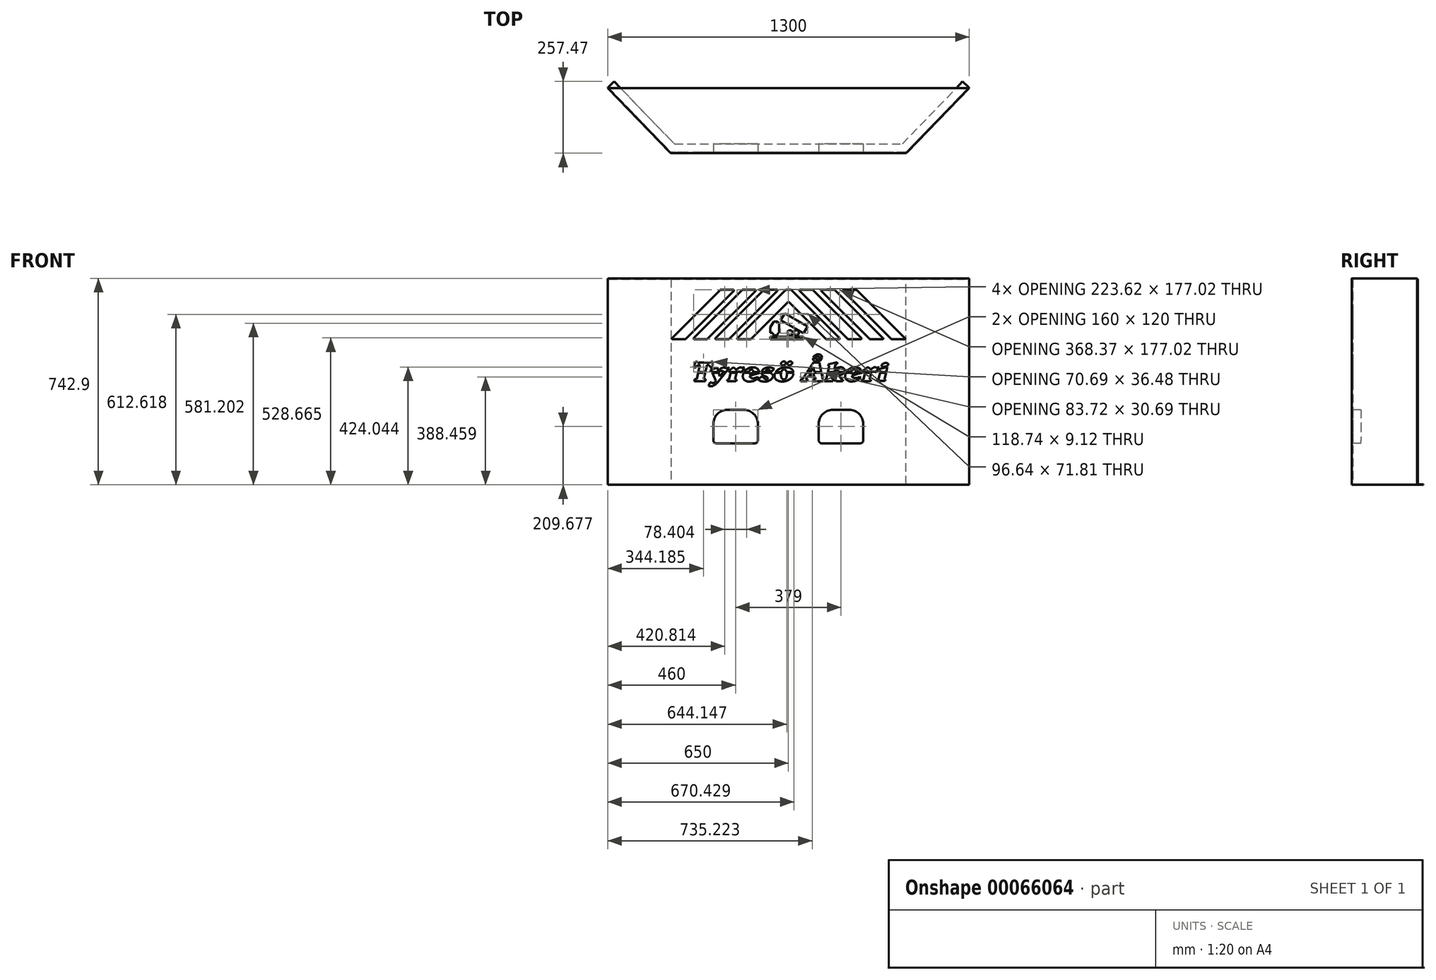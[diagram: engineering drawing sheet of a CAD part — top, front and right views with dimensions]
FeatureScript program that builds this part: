
annotation { "Feature Type Name" : "Feature", "Feature Type Description" : "" }
export const myFeature = defineFeature(function(context is Context, id is Id, definition is map)
    precondition{}
    {
        {
            var Q0;
            Q0=qCreatedBy(makeId("Front.planeOp"),FACE);
            var sketch = newSketch(context, id + "F0", { "sketchPlane" : qUnion([Q0])});
            skLineSegment(sketch, "E0", {"start": v(-649.77, 406.5) * mm, "end": v(-649.77, -376.5) * mm});
            skLineSegment(sketch, "E1", {"start": v(649.77, 406.5) * mm, "end": v(649.77, -376.5) * mm});
            skLineSegment(sketch, "E2", {"start": v(649.77, -376.5) * mm, "end": v(-649.77, -376.5) * mm});
            skLineSegment(sketch, "E3", {"start": v(649.77, 406.5) * mm, "end": v(-649.77, 406.5) * mm});
            skLineSegment(sketch, "E4", {"start": v(-423.5, 366.4) * mm, "end": v(-423.5, -376.5) * mm});
            skLineSegment(sketch, "E5", {"start": v(423.5, 366.4) * mm, "end": v(423.5, -376.5) * mm});
            skLineSegment(sketch, "E6", {"start": v(-423.5, 366.4) * mm, "end": v(423.5, 366.4) * mm});
            skLineSegment(sketch, "E7", {"start": v(134.17, 148.2) * mm, "end": v(1.41, 280.95) * mm});
            skArc(sketch, "E8", {"start": v(1.41, 280.95) * mm, "mid": v(0, 281.53) * mm, "end": v(-1.41, 280.95) * mm});
            skLineSegment(sketch, "E9", {"start": v(183.61, 151.02) * mm, "end": v(10.59, 324.04) * mm});
            skArc(sketch, "E10", {"start": v(10.59, 324.04) * mm, "mid": v(9.94, 324.48) * mm, "end": v(9.17, 324.63) * mm});
            skArc(sketch, "E11", {"start": v(182.2, 147.6) * mm, "mid": v(184.04, 148.84) * mm, "end": v(183.61, 151.02) * mm});
            skLineSegment(sketch, "E12", {"start": v(212.57, 148.2) * mm, "end": v(39.55, 321.22) * mm});
            skLineSegment(sketch, "E13", {"start": v(262.01, 151.02) * mm, "end": v(88.99, 324.04) * mm});
            skArc(sketch, "E14", {"start": v(88.99, 324.04) * mm, "mid": v(88.34, 324.48) * mm, "end": v(87.58, 324.63) * mm});
            skArc(sketch, "E15", {"start": v(260.6, 147.6) * mm, "mid": v(262.45, 148.84) * mm, "end": v(262.01, 151.02) * mm});
            skLineSegment(sketch, "E16", {"start": v(290.98, 148.2) * mm, "end": v(117.95, 321.22) * mm});
            skLineSegment(sketch, "E17", {"start": v(340.42, 151.02) * mm, "end": v(167.4, 324.04) * mm});
            skArc(sketch, "E18", {"start": v(167.4, 324.04) * mm, "mid": v(166.74, 324.48) * mm, "end": v(165.98, 324.63) * mm});
            skArc(sketch, "E19", {"start": v(339, 147.6) * mm, "mid": v(340.85, 148.84) * mm, "end": v(340.42, 151.02) * mm});
            skLineSegment(sketch, "E20", {"start": v(369.38, 148.2) * mm, "end": v(196.36, 321.22) * mm});
            skLineSegment(sketch, "E21", {"start": v(418.82, 151.02) * mm, "end": v(245.8, 324.04) * mm});
            skArc(sketch, "E22", {"start": v(245.8, 324.04) * mm, "mid": v(245.15, 324.48) * mm, "end": v(244.38, 324.63) * mm});
            skArc(sketch, "E23", {"start": v(417.4, 147.6) * mm, "mid": v(419.26, 148.84) * mm, "end": v(418.82, 151.02) * mm});
            skLineSegment(sketch, "E24", {"start": v(339, 147.6) * mm, "end": v(292.4, 147.6) * mm});
            skArc(sketch, "E25", {"start": v(290.98, 148.2) * mm, "mid": v(291.63, 147.76) * mm, "end": v(292.4, 147.6) * mm});
            skLineSegment(sketch, "E26", {"start": v(260.6, 147.6) * mm, "end": v(213.99, 147.6) * mm});
            skArc(sketch, "E27", {"start": v(212.57, 148.2) * mm, "mid": v(213.22, 147.76) * mm, "end": v(213.99, 147.6) * mm});
            skLineSegment(sketch, "E28", {"start": v(182.2, 147.6) * mm, "end": v(135.58, 147.6) * mm});
            skArc(sketch, "E29", {"start": v(134.17, 148.2) * mm, "mid": v(134.82, 147.76) * mm, "end": v(135.58, 147.6) * mm});
            skLineSegment(sketch, "E30", {"start": v(370.8, 147.6) * mm, "end": v(417.4, 147.6) * mm});
            skArc(sketch, "E31", {"start": v(369.38, 148.2) * mm, "mid": v(370.03, 147.76) * mm, "end": v(370.8, 147.6) * mm});
            skLineSegment(sketch, "E32", {"start": v(9.17, 324.63) * mm, "end": v(0, 324.63) * mm});
            skLineSegment(sketch, "E33", {"start": v(40.96, 324.63) * mm, "end": v(87.58, 324.63) * mm});
            skArc(sketch, "E34", {"start": v(40.96, 324.63) * mm, "mid": v(39.12, 323.4) * mm, "end": v(39.55, 321.22) * mm});
            skLineSegment(sketch, "E35", {"start": v(119.37, 324.63) * mm, "end": v(165.98, 324.63) * mm});
            skArc(sketch, "E36", {"start": v(119.37, 324.63) * mm, "mid": v(117.52, 323.4) * mm, "end": v(117.95, 321.22) * mm});
            skLineSegment(sketch, "E37", {"start": v(197.77, 324.63) * mm, "end": v(244.38, 324.63) * mm});
            skArc(sketch, "E38", {"start": v(197.77, 324.63) * mm, "mid": v(195.92, 323.4) * mm, "end": v(196.36, 321.22) * mm});
            skLineSegment(sketch, "E39", {"start": v(-134.17, 148.2) * mm, "end": v(-1.41, 280.95) * mm});
            skLineSegment(sketch, "E40", {"start": v(-183.61, 151.02) * mm, "end": v(-10.59, 324.04) * mm});
            skArc(sketch, "E41", {"start": v(-9.17, 324.63) * mm, "mid": v(-9.94, 324.48) * mm, "end": v(-10.59, 324.04) * mm});
            skArc(sketch, "E42", {"start": v(-183.61, 151.02) * mm, "mid": v(-184.04, 148.84) * mm, "end": v(-182.2, 147.6) * mm});
            skLineSegment(sketch, "E43", {"start": v(-212.57, 148.2) * mm, "end": v(-39.55, 321.22) * mm});
            skLineSegment(sketch, "E44", {"start": v(-262.01, 151.02) * mm, "end": v(-88.99, 324.04) * mm});
            skArc(sketch, "E45", {"start": v(-87.58, 324.63) * mm, "mid": v(-88.34, 324.48) * mm, "end": v(-88.99, 324.04) * mm});
            skArc(sketch, "E46", {"start": v(-262.01, 151.02) * mm, "mid": v(-262.45, 148.84) * mm, "end": v(-260.6, 147.6) * mm});
            skLineSegment(sketch, "E47", {"start": v(-290.98, 148.2) * mm, "end": v(-117.95, 321.22) * mm});
            skLineSegment(sketch, "E48", {"start": v(-340.42, 151.02) * mm, "end": v(-167.4, 324.04) * mm});
            skArc(sketch, "E49", {"start": v(-165.98, 324.63) * mm, "mid": v(-166.74, 324.48) * mm, "end": v(-167.4, 324.04) * mm});
            skArc(sketch, "E50", {"start": v(-340.42, 151.02) * mm, "mid": v(-340.85, 148.84) * mm, "end": v(-339, 147.6) * mm});
            skLineSegment(sketch, "E51", {"start": v(-369.38, 148.2) * mm, "end": v(-196.36, 321.22) * mm});
            skLineSegment(sketch, "E52", {"start": v(-418.82, 151.02) * mm, "end": v(-245.8, 324.04) * mm});
            skArc(sketch, "E53", {"start": v(-244.38, 324.63) * mm, "mid": v(-245.15, 324.48) * mm, "end": v(-245.8, 324.04) * mm});
            skArc(sketch, "E54", {"start": v(-418.82, 151.02) * mm, "mid": v(-419.26, 148.84) * mm, "end": v(-417.4, 147.6) * mm});
            skLineSegment(sketch, "E55", {"start": v(-339, 147.6) * mm, "end": v(-292.4, 147.6) * mm});
            skArc(sketch, "E56", {"start": v(-292.4, 147.6) * mm, "mid": v(-291.63, 147.76) * mm, "end": v(-290.98, 148.2) * mm});
            skLineSegment(sketch, "E57", {"start": v(-260.6, 147.6) * mm, "end": v(-213.99, 147.6) * mm});
            skArc(sketch, "E58", {"start": v(-213.99, 147.6) * mm, "mid": v(-213.22, 147.76) * mm, "end": v(-212.57, 148.2) * mm});
            skLineSegment(sketch, "E59", {"start": v(-182.2, 147.6) * mm, "end": v(-135.58, 147.6) * mm});
            skArc(sketch, "E60", {"start": v(-135.58, 147.6) * mm, "mid": v(-134.82, 147.76) * mm, "end": v(-134.17, 148.2) * mm});
            skLineSegment(sketch, "E61", {"start": v(-370.8, 147.6) * mm, "end": v(-417.4, 147.6) * mm});
            skLineSegment(sketch, "E62", {"start": v(-9.17, 324.63) * mm, "end": v(0, 324.63) * mm});
            skLineSegment(sketch, "E63", {"start": v(-40.96, 324.63) * mm, "end": v(-87.58, 324.63) * mm});
            skArc(sketch, "E64", {"start": v(-39.55, 321.22) * mm, "mid": v(-39.12, 323.4) * mm, "end": v(-40.96, 324.63) * mm});
            skLineSegment(sketch, "E65", {"start": v(-119.37, 324.63) * mm, "end": v(-165.98, 324.63) * mm});
            skArc(sketch, "E66", {"start": v(-117.95, 321.22) * mm, "mid": v(-117.52, 323.4) * mm, "end": v(-119.37, 324.63) * mm});
            skLineSegment(sketch, "E67", {"start": v(-197.77, 324.63) * mm, "end": v(-244.38, 324.63) * mm});
            skArc(sketch, "E68", {"start": v(-196.36, 321.22) * mm, "mid": v(-195.92, 323.4) * mm, "end": v(-197.77, 324.63) * mm});
            skLineSegment(sketch, "E69", {"start": v(119, -226.82) * mm, "end": v(189, -226.82) * mm});
            skLineSegment(sketch, "E70", {"start": v(189, -106.82) * mm, "end": v(159, -106.82) * mm});
            skArc(sketch, "E71", {"start": v(159, -106.82) * mm, "mid": v(123.64, -121.47) * mm, "end": v(109, -156.82) * mm});
            skLineSegment(sketch, "E72", {"start": v(109, -156.82) * mm, "end": v(109, -216.82) * mm});
            skArc(sketch, "E73", {"start": v(109, -216.82) * mm, "mid": v(111.93, -223.9) * mm, "end": v(119, -226.82) * mm});
            skLineSegment(sketch, "E74", {"start": v(-27.89, 215.85) * mm, "end": v(54.63, 168.8) * mm});
            skLineSegment(sketch, "E75", {"start": v(54.63, 168.8) * mm, "end": v(68.75, 193.55) * mm});
            skLineSegment(sketch, "E76", {"start": v(68.75, 193.55) * mm, "end": v(-13.77, 240.6) * mm});
            skLineSegment(sketch, "E77", {"start": v(-13.77, 240.6) * mm, "end": v(-27.89, 215.85) * mm});
            skLineSegment(sketch, "E78", {"start": v(-65.42, 190.73) * mm, "end": v(-65.42, 170.3) * mm});
            skLineSegment(sketch, "E79", {"start": v(-65.42, 170.3) * mm, "end": v(-56.4, 170.3) * mm});
            skLineSegment(sketch, "E80", {"start": v(-37.4, 170.3) * mm, "end": v(-34.07, 170.3) * mm});
            skLineSegment(sketch, "E81", {"start": v(-34.07, 170.3) * mm, "end": v(-34.07, 201.65) * mm});
            skArc(sketch, "E82", {"start": v(-34.07, 201.65) * mm, "mid": v(-36.85, 208.37) * mm, "end": v(-43.57, 211.15) * mm});
            skLineSegment(sketch, "E83", {"start": v(-43.57, 211.15) * mm, "end": v(-53.07, 211.15) * mm});
            skArc(sketch, "E84", {"start": v(-56.4, 170.3) * mm, "mid": v(-46.9, 160.8) * mm, "end": v(-37.4, 170.3) * mm});
            skCircle(sketch, "E85", {"center": v(28.2, 170.12) * mm, "radius": 9.5 * mm});
            skCircle(sketch, "E86", {"center": v(5.53, 170.1) * mm, "radius": 9.5 * mm});
            skLineSegment(sketch, "E87", {"start": v(-53.07, 211.15) * mm, "end": v(-65.42, 190.73) * mm});
            skLineSegment(sketch, "E88", {"start": v(-65.22, 147.6) * mm, "end": v(53.52, 147.6) * mm});
            skLineSegment(sketch, "E89", {"start": v(53.52, 147.6) * mm, "end": v(53.52, 156.72) * mm});
            skLineSegment(sketch, "E90", {"start": v(53.52, 156.72) * mm, "end": v(-65.22, 156.72) * mm});
            skLineSegment(sketch, "E91", {"start": v(-65.22, 156.72) * mm, "end": v(-65.22, 147.6) * mm});
            skLineSegment(sketch, "E92", {"start": v(-326.4, 63.29) * mm, "end": v(-279.7, 63.29) * mm});
            skArc(sketch, "E93", {"start": v(-370.8, 147.6) * mm, "mid": v(-370.03, 147.76) * mm, "end": v(-369.38, 148.2) * mm});
            skLineSegment(sketch, "E94", {"start": v(259, -226.82) * mm, "end": v(189, -226.82) * mm});
            skLineSegment(sketch, "E95", {"start": v(189, -106.82) * mm, "end": v(219, -106.82) * mm});
            skArc(sketch, "E96", {"start": v(269, -156.82) * mm, "mid": v(254.36, -121.47) * mm, "end": v(219, -106.82) * mm});
            skLineSegment(sketch, "E97", {"start": v(269, -156.82) * mm, "end": v(269, -216.82) * mm});
            skArc(sketch, "E98", {"start": v(259, -226.82) * mm, "mid": v(266.07, -223.9) * mm, "end": v(269, -216.82) * mm});
            skLineSegment(sketch, "E99", {"start": v(-260, -226.82) * mm, "end": v(-190, -226.82) * mm});
            skLineSegment(sketch, "E100", {"start": v(-190, -106.82) * mm, "end": v(-220, -106.82) * mm});
            skArc(sketch, "E101", {"start": v(-220, -106.82) * mm, "mid": v(-255.36, -121.47) * mm, "end": v(-270, -156.82) * mm});
            skLineSegment(sketch, "E102", {"start": v(-270, -156.82) * mm, "end": v(-270, -216.82) * mm});
            skArc(sketch, "E103", {"start": v(-270, -216.82) * mm, "mid": v(-267.07, -223.9) * mm, "end": v(-260, -226.82) * mm});
            skLineSegment(sketch, "E104", {"start": v(-120, -226.82) * mm, "end": v(-190, -226.82) * mm});
            skLineSegment(sketch, "E105", {"start": v(-190, -106.82) * mm, "end": v(-160, -106.82) * mm});
            skArc(sketch, "E106", {"start": v(-110, -156.82) * mm, "mid": v(-124.64, -121.47) * mm, "end": v(-160, -106.82) * mm});
            skLineSegment(sketch, "E107", {"start": v(-110, -156.82) * mm, "end": v(-110, -216.82) * mm});
            skArc(sketch, "E108", {"start": v(-120, -226.82) * mm, "mid": v(-112.93, -223.9) * mm, "end": v(-110, -216.82) * mm});
            skLineSegment(sketch, "E109", {"start": v(375, -396.5) * mm, "end": v(305, -396.5) * mm});
            skLineSegment(sketch, "E110", {"start": v(-305, -396.5) * mm, "end": v(-375, -396.5) * mm});
            skLineSegment(sketch, "E111", {"start": v(-295, -376.5) * mm, "end": v(-295, -396.5) * mm});
            skLineSegment(sketch, "E112", {"start": v(-385, -376.5) * mm, "end": v(-385, -396.5) * mm});
            skLineSegment(sketch, "E113", {"start": v(-440, -396.5) * mm, "end": v(-440, -406.5) * mm});
            skLineSegment(sketch, "E114", {"start": v(-240, -396.5) * mm, "end": v(-240, -406.5) * mm});
            skLineSegment(sketch, "E115", {"start": v(-440, -396.5) * mm, "end": v(-240, -396.5) * mm});
            skLineSegment(sketch, "E116", {"start": v(-440, -406.5) * mm, "end": v(-240, -406.5) * mm});
            skLineSegment(sketch, "E117", {"start": v(385, -376.5) * mm, "end": v(385, -396.5) * mm});
            skLineSegment(sketch, "E118", {"start": v(295, -376.5) * mm, "end": v(295, -396.5) * mm});
            skLineSegment(sketch, "E119", {"start": v(240, -396.5) * mm, "end": v(240, -406.5) * mm});
            skLineSegment(sketch, "E120", {"start": v(440, -396.5) * mm, "end": v(440, -406.5) * mm});
            skLineSegment(sketch, "E121", {"start": v(240, -396.5) * mm, "end": v(440, -396.5) * mm});
            skLineSegment(sketch, "E122", {"start": v(240, -406.5) * mm, "end": v(440, -406.5) * mm});
            skLineSegment(sketch, "E123", {"start": v(649.77, 406.5) * mm, "end": v(423.5, 366.4) * mm});
            skLineSegment(sketch, "E124", {"start": v(-649.77, 406.5) * mm, "end": v(-423.5, 366.4) * mm});
            skLineSegment(sketch, "E125", {"start": v(7.65, 67.35) * mm, "end": v(8.83, 67.14) * mm});
            skLineSegment(sketch, "E126", {"start": v(8.83, 67.14) * mm, "end": v(9.98, 66.77) * mm});
            skLineSegment(sketch, "E127", {"start": v(9.98, 66.77) * mm, "end": v(10.9, 66.3) * mm});
            skLineSegment(sketch, "E128", {"start": v(10.9, 66.3) * mm, "end": v(11.75, 65.7) * mm});
            skLineSegment(sketch, "E129", {"start": v(11.75, 65.7) * mm, "end": v(12.4, 65.03) * mm});
            skLineSegment(sketch, "E130", {"start": v(12.4, 65.03) * mm, "end": v(12.92, 64.26) * mm});
            skLineSegment(sketch, "E131", {"start": v(12.92, 64.26) * mm, "end": v(13.28, 63.44) * mm});
            skLineSegment(sketch, "E132", {"start": v(13.28, 63.44) * mm, "end": v(13.49, 62.57) * mm});
            skLineSegment(sketch, "E133", {"start": v(13.49, 62.57) * mm, "end": v(13.52, 61.55) * mm});
            skLineSegment(sketch, "E134", {"start": v(13.52, 61.55) * mm, "end": v(13.38, 60.54) * mm});
            skLineSegment(sketch, "E135", {"start": v(13.38, 60.54) * mm, "end": v(13.08, 59.57) * mm});
            skLineSegment(sketch, "E136", {"start": v(13.08, 59.57) * mm, "end": v(12.63, 58.66) * mm});
            skLineSegment(sketch, "E137", {"start": v(12.63, 58.66) * mm, "end": v(11.95, 57.64) * mm});
            skLineSegment(sketch, "E138", {"start": v(11.95, 57.64) * mm, "end": v(11.14, 56.72) * mm});
            skLineSegment(sketch, "E139", {"start": v(11.14, 56.72) * mm, "end": v(10.12, 55.85) * mm});
            skLineSegment(sketch, "E140", {"start": v(10.12, 55.85) * mm, "end": v(9, 55.12) * mm});
            skLineSegment(sketch, "E141", {"start": v(9, 55.12) * mm, "end": v(7.7, 54.5) * mm});
            skLineSegment(sketch, "E142", {"start": v(7.7, 54.5) * mm, "end": v(6.33, 54.04) * mm});
            skLineSegment(sketch, "E143", {"start": v(6.33, 54.04) * mm, "end": v(4.92, 53.75) * mm});
            skLineSegment(sketch, "E144", {"start": v(4.92, 53.75) * mm, "end": v(3.48, 53.63) * mm});
            skLineSegment(sketch, "E145", {"start": v(3.48, 53.63) * mm, "end": v(2.18, 53.67) * mm});
            skLineSegment(sketch, "E146", {"start": v(2.18, 53.67) * mm, "end": v(0.9, 53.9) * mm});
            skLineSegment(sketch, "E147", {"start": v(0.9, 53.9) * mm, "end": v(-0.16, 54.24) * mm});
            skLineSegment(sketch, "E148", {"start": v(-0.16, 54.24) * mm, "end": v(-1.16, 54.75) * mm});
            skLineSegment(sketch, "E149", {"start": v(-1.16, 54.75) * mm, "end": v(-1.96, 55.33) * mm});
            skLineSegment(sketch, "E150", {"start": v(-1.96, 55.33) * mm, "end": v(-2.66, 56.03) * mm});
            skLineSegment(sketch, "E151", {"start": v(-2.66, 56.03) * mm, "end": v(-3.17, 56.78) * mm});
            skLineSegment(sketch, "E152", {"start": v(-3.17, 56.78) * mm, "end": v(-3.54, 57.6) * mm});
            skLineSegment(sketch, "E153", {"start": v(-3.54, 57.6) * mm, "end": v(-3.75, 58.52) * mm});
            skLineSegment(sketch, "E154", {"start": v(-3.75, 58.52) * mm, "end": v(-3.8, 59.44) * mm});
            skLineSegment(sketch, "E155", {"start": v(-3.8, 59.44) * mm, "end": v(-3.69, 60.37) * mm});
            skLineSegment(sketch, "E156", {"start": v(-3.69, 60.37) * mm, "end": v(-3.36, 61.4) * mm});
            skLineSegment(sketch, "E157", {"start": v(-3.36, 61.4) * mm, "end": v(-2.89, 62.37) * mm});
            skLineSegment(sketch, "E158", {"start": v(-2.89, 62.37) * mm, "end": v(-2.26, 63.25) * mm});
            skLineSegment(sketch, "E159", {"start": v(-2.26, 63.25) * mm, "end": v(-1.37, 64.22) * mm});
            skLineSegment(sketch, "E160", {"start": v(-1.37, 64.22) * mm, "end": v(-0.35, 65.07) * mm});
            skLineSegment(sketch, "E161", {"start": v(-0.35, 65.07) * mm, "end": v(0.86, 65.86) * mm});
            skLineSegment(sketch, "E162", {"start": v(0.86, 65.86) * mm, "end": v(2.17, 66.5) * mm});
            skLineSegment(sketch, "E163", {"start": v(2.17, 66.5) * mm, "end": v(3.54, 66.98) * mm});
            skLineSegment(sketch, "E164", {"start": v(3.54, 66.98) * mm, "end": v(4.95, 67.3) * mm});
            skLineSegment(sketch, "E165", {"start": v(4.95, 67.3) * mm, "end": v(6.3, 67.41) * mm});
            skLineSegment(sketch, "E166", {"start": v(6.3, 67.41) * mm, "end": v(7.65, 67.35) * mm});
            skLineSegment(sketch, "E167", {"start": v(-15.3, 67.36) * mm, "end": v(-14.12, 67.15) * mm});
            skLineSegment(sketch, "E168", {"start": v(-14.12, 67.15) * mm, "end": v(-12.98, 66.78) * mm});
            skLineSegment(sketch, "E169", {"start": v(-12.98, 66.78) * mm, "end": v(-12.06, 66.32) * mm});
            skLineSegment(sketch, "E170", {"start": v(-12.06, 66.32) * mm, "end": v(-11.24, 65.72) * mm});
            skLineSegment(sketch, "E171", {"start": v(-11.24, 65.72) * mm, "end": v(-10.6, 65.06) * mm});
            skLineSegment(sketch, "E172", {"start": v(-10.6, 65.06) * mm, "end": v(-10.08, 64.3) * mm});
            skLineSegment(sketch, "E173", {"start": v(-10.08, 64.3) * mm, "end": v(-9.73, 63.47) * mm});
            skLineSegment(sketch, "E174", {"start": v(-9.73, 63.47) * mm, "end": v(-9.53, 62.6) * mm});
            skLineSegment(sketch, "E175", {"start": v(-9.53, 62.6) * mm, "end": v(-9.5, 61.56) * mm});
            skLineSegment(sketch, "E176", {"start": v(-9.5, 61.56) * mm, "end": v(-9.64, 60.54) * mm});
            skLineSegment(sketch, "E177", {"start": v(-9.64, 60.54) * mm, "end": v(-9.94, 59.56) * mm});
            skLineSegment(sketch, "E178", {"start": v(-9.94, 59.56) * mm, "end": v(-10.4, 58.63) * mm});
            skLineSegment(sketch, "E179", {"start": v(-10.4, 58.63) * mm, "end": v(-11.07, 57.6) * mm});
            skLineSegment(sketch, "E180", {"start": v(-11.07, 57.6) * mm, "end": v(-11.88, 56.69) * mm});
            skLineSegment(sketch, "E181", {"start": v(-11.88, 56.69) * mm, "end": v(-12.88, 55.82) * mm});
            skLineSegment(sketch, "E182", {"start": v(-12.88, 55.82) * mm, "end": v(-14, 55.1) * mm});
            skLineSegment(sketch, "E183", {"start": v(-14, 55.1) * mm, "end": v(-15.27, 54.48) * mm});
            skLineSegment(sketch, "E184", {"start": v(-15.27, 54.48) * mm, "end": v(-16.61, 54.03) * mm});
            skLineSegment(sketch, "E185", {"start": v(-16.61, 54.03) * mm, "end": v(-18, 53.74) * mm});
            skLineSegment(sketch, "E186", {"start": v(-18, 53.74) * mm, "end": v(-19.4, 53.63) * mm});
            skLineSegment(sketch, "E187", {"start": v(-19.4, 53.63) * mm, "end": v(-20.7, 53.68) * mm});
            skLineSegment(sketch, "E188", {"start": v(-20.7, 53.68) * mm, "end": v(-21.99, 53.9) * mm});
            skLineSegment(sketch, "E189", {"start": v(-21.99, 53.9) * mm, "end": v(-23.06, 54.26) * mm});
            skLineSegment(sketch, "E190", {"start": v(-23.06, 54.26) * mm, "end": v(-24.07, 54.76) * mm});
            skLineSegment(sketch, "E191", {"start": v(-24.07, 54.76) * mm, "end": v(-24.87, 55.34) * mm});
            skLineSegment(sketch, "E192", {"start": v(-24.87, 55.34) * mm, "end": v(-25.57, 56.05) * mm});
            skLineSegment(sketch, "E193", {"start": v(-25.57, 56.05) * mm, "end": v(-26.08, 56.8) * mm});
            skLineSegment(sketch, "E194", {"start": v(-26.08, 56.8) * mm, "end": v(-26.45, 57.62) * mm});
            skLineSegment(sketch, "E195", {"start": v(-26.45, 57.62) * mm, "end": v(-26.67, 58.52) * mm});
            skLineSegment(sketch, "E196", {"start": v(-26.67, 58.52) * mm, "end": v(-26.72, 59.45) * mm});
            skLineSegment(sketch, "E197", {"start": v(-26.72, 59.45) * mm, "end": v(-26.6, 60.37) * mm});
            skLineSegment(sketch, "E198", {"start": v(-26.6, 60.37) * mm, "end": v(-26.28, 61.4) * mm});
            skLineSegment(sketch, "E199", {"start": v(-26.28, 61.4) * mm, "end": v(-25.8, 62.36) * mm});
            skLineSegment(sketch, "E200", {"start": v(-25.8, 62.36) * mm, "end": v(-25.18, 63.24) * mm});
            skLineSegment(sketch, "E201", {"start": v(-25.18, 63.24) * mm, "end": v(-24.29, 64.22) * mm});
            skLineSegment(sketch, "E202", {"start": v(-24.29, 64.22) * mm, "end": v(-23.28, 65.07) * mm});
            skLineSegment(sketch, "E203", {"start": v(-23.28, 65.07) * mm, "end": v(-22.06, 65.85) * mm});
            skLineSegment(sketch, "E204", {"start": v(-22.06, 65.85) * mm, "end": v(-20.76, 66.5) * mm});
            skLineSegment(sketch, "E205", {"start": v(-20.76, 66.5) * mm, "end": v(-19.39, 66.97) * mm});
            skLineSegment(sketch, "E206", {"start": v(-19.39, 66.97) * mm, "end": v(-17.97, 67.3) * mm});
            skLineSegment(sketch, "E207", {"start": v(-17.97, 67.3) * mm, "end": v(-16.63, 67.41) * mm});
            skLineSegment(sketch, "E208", {"start": v(-16.63, 67.41) * mm, "end": v(-15.3, 67.36) * mm});
            skLineSegment(sketch, "E209", {"start": v(344.32, 61) * mm, "end": v(346.06, 61.47) * mm});
            skLineSegment(sketch, "E210", {"start": v(346.06, 61.47) * mm, "end": v(347.83, 61.8) * mm});
            skLineSegment(sketch, "E211", {"start": v(347.83, 61.8) * mm, "end": v(349.53, 61.95) * mm});
            skLineSegment(sketch, "E212", {"start": v(349.53, 61.95) * mm, "end": v(351.24, 61.97) * mm});
            skLineSegment(sketch, "E213", {"start": v(351.24, 61.97) * mm, "end": v(352.73, 61.86) * mm});
            skLineSegment(sketch, "E214", {"start": v(352.73, 61.86) * mm, "end": v(354.2, 61.62) * mm});
            skLineSegment(sketch, "E215", {"start": v(354.2, 61.62) * mm, "end": v(355.27, 61.32) * mm});
            skLineSegment(sketch, "E216", {"start": v(355.27, 61.32) * mm, "end": v(356.3, 60.88) * mm});
            skLineSegment(sketch, "E217", {"start": v(356.3, 60.88) * mm, "end": v(357.03, 60.45) * mm});
            skLineSegment(sketch, "E218", {"start": v(357.03, 60.45) * mm, "end": v(357.68, 59.9) * mm});
            skLineSegment(sketch, "E219", {"start": v(357.68, 59.9) * mm, "end": v(358.14, 59.38) * mm});
            skLineSegment(sketch, "E220", {"start": v(358.14, 59.38) * mm, "end": v(358.5, 58.77) * mm});
            skLineSegment(sketch, "E221", {"start": v(358.5, 58.77) * mm, "end": v(358.72, 58.15) * mm});
            skLineSegment(sketch, "E222", {"start": v(358.72, 58.15) * mm, "end": v(358.82, 57.5) * mm});
            skLineSegment(sketch, "E223", {"start": v(358.82, 57.5) * mm, "end": v(358.8, 56.7) * mm});
            skLineSegment(sketch, "E224", {"start": v(358.8, 56.7) * mm, "end": v(358.63, 55.91) * mm});
            skLineSegment(sketch, "E225", {"start": v(358.63, 55.91) * mm, "end": v(358.35, 55.16) * mm});
            skLineSegment(sketch, "E226", {"start": v(358.35, 55.16) * mm, "end": v(357.85, 54.28) * mm});
            skLineSegment(sketch, "E227", {"start": v(357.85, 54.28) * mm, "end": v(357.24, 53.46) * mm});
            skLineSegment(sketch, "E228", {"start": v(357.24, 53.46) * mm, "end": v(356.54, 52.72) * mm});
            skLineSegment(sketch, "E229", {"start": v(356.54, 52.72) * mm, "end": v(355.48, 51.83) * mm});
            skLineSegment(sketch, "E230", {"start": v(355.48, 51.83) * mm, "end": v(354.34, 51.04) * mm});
            skLineSegment(sketch, "E231", {"start": v(354.34, 51.04) * mm, "end": v(352.87, 50.22) * mm});
            skLineSegment(sketch, "E232", {"start": v(352.87, 50.22) * mm, "end": v(351.33, 49.53) * mm});
            skLineSegment(sketch, "E233", {"start": v(351.33, 49.53) * mm, "end": v(349.52, 48.9) * mm});
            skLineSegment(sketch, "E234", {"start": v(349.52, 48.9) * mm, "end": v(347.67, 48.4) * mm});
            skLineSegment(sketch, "E235", {"start": v(347.67, 48.4) * mm, "end": v(345.72, 48.04) * mm});
            skLineSegment(sketch, "E236", {"start": v(345.72, 48.04) * mm, "end": v(343.75, 47.82) * mm});
            skLineSegment(sketch, "E237", {"start": v(343.75, 47.82) * mm, "end": v(342.11, 47.76) * mm});
            skLineSegment(sketch, "E238", {"start": v(342.11, 47.76) * mm, "end": v(340.48, 47.84) * mm});
            skLineSegment(sketch, "E239", {"start": v(340.48, 47.84) * mm, "end": v(339.32, 48.01) * mm});
            skLineSegment(sketch, "E240", {"start": v(339.32, 48.01) * mm, "end": v(338.2, 48.33) * mm});
            skLineSegment(sketch, "E241", {"start": v(338.2, 48.33) * mm, "end": v(337.38, 48.69) * mm});
            skLineSegment(sketch, "E242", {"start": v(337.38, 48.69) * mm, "end": v(336.62, 49.16) * mm});
            skLineSegment(sketch, "E243", {"start": v(336.62, 49.16) * mm, "end": v(336.08, 49.63) * mm});
            skLineSegment(sketch, "E244", {"start": v(336.08, 49.63) * mm, "end": v(335.62, 50.2) * mm});
            skLineSegment(sketch, "E245", {"start": v(335.62, 50.2) * mm, "end": v(335.3, 50.79) * mm});
            skLineSegment(sketch, "E246", {"start": v(335.3, 50.79) * mm, "end": v(335.1, 51.43) * mm});
            skLineSegment(sketch, "E247", {"start": v(335.1, 51.43) * mm, "end": v(335.02, 52.21) * mm});
            skLineSegment(sketch, "E248", {"start": v(335.02, 52.21) * mm, "end": v(335.06, 53) * mm});
            skLineSegment(sketch, "E249", {"start": v(335.06, 53) * mm, "end": v(335.24, 53.77) * mm});
            skLineSegment(sketch, "E250", {"start": v(335.24, 53.77) * mm, "end": v(335.58, 54.65) * mm});
            skLineSegment(sketch, "E251", {"start": v(335.58, 54.65) * mm, "end": v(336.04, 55.47) * mm});
            skLineSegment(sketch, "E252", {"start": v(336.04, 55.47) * mm, "end": v(336.6, 56.22) * mm});
            skLineSegment(sketch, "E253", {"start": v(336.6, 56.22) * mm, "end": v(337.48, 57.15) * mm});
            skLineSegment(sketch, "E254", {"start": v(337.48, 57.15) * mm, "end": v(338.45, 57.99) * mm});
            skLineSegment(sketch, "E255", {"start": v(338.45, 57.99) * mm, "end": v(339.72, 58.88) * mm});
            skLineSegment(sketch, "E256", {"start": v(339.72, 58.88) * mm, "end": v(341.08, 59.66) * mm});
            skLineSegment(sketch, "E257", {"start": v(341.08, 59.66) * mm, "end": v(342.67, 60.4) * mm});
            skLineSegment(sketch, "E258", {"start": v(342.67, 60.4) * mm, "end": v(344.32, 61) * mm});
            skLineSegment(sketch, "E259", {"start": v(-299.17, 27.3) * mm, "end": v(-304.78, 3.67) * mm});
            skLineSegment(sketch, "E260", {"start": v(-304.78, 3.67) * mm, "end": v(-297.73, 3.67) * mm});
            skLineSegment(sketch, "E261", {"start": v(-297.73, 3.67) * mm, "end": v(-299.46, -3.82) * mm});
            skLineSegment(sketch, "E262", {"start": v(-299.46, -3.82) * mm, "end": v(-338.77, -3.82) * mm});
            skLineSegment(sketch, "E263", {"start": v(-338.77, -3.82) * mm, "end": v(-337.04, 3.67) * mm});
            skLineSegment(sketch, "E264", {"start": v(-337.04, 3.67) * mm, "end": v(-329.87, 3.67) * mm});
            skLineSegment(sketch, "E265", {"start": v(-329.87, 3.67) * mm, "end": v(-324.24, 27.3) * mm});
            skLineSegment(sketch, "E266", {"start": v(-324.24, 27.3) * mm, "end": v(-299.17, 27.3) * mm});
            skLineSegment(sketch, "E267", {"start": v(-298.7, 29.3) * mm, "end": v(-323.76, 29.3) * mm});
            skLineSegment(sketch, "E268", {"start": v(-323.76, 29.3) * mm, "end": v(-317.81, 54.27) * mm});
            skLineSegment(sketch, "E269", {"start": v(-317.81, 54.27) * mm, "end": v(-319.23, 54.27) * mm});
            skLineSegment(sketch, "E270", {"start": v(-319.23, 54.27) * mm, "end": v(-320.83, 54.22) * mm});
            skLineSegment(sketch, "E271", {"start": v(-320.83, 54.22) * mm, "end": v(-322.42, 54.03) * mm});
            skLineSegment(sketch, "E272", {"start": v(-322.42, 54.03) * mm, "end": v(-324, 53.7) * mm});
            skLineSegment(sketch, "E273", {"start": v(-324, 53.7) * mm, "end": v(-325.32, 53.28) * mm});
            skLineSegment(sketch, "E274", {"start": v(-325.32, 53.28) * mm, "end": v(-326.6, 52.72) * mm});
            skLineSegment(sketch, "E275", {"start": v(-326.6, 52.72) * mm, "end": v(-327.8, 52.03) * mm});
            skLineSegment(sketch, "E276", {"start": v(-327.8, 52.03) * mm, "end": v(-328.9, 51.2) * mm});
            skLineSegment(sketch, "E277", {"start": v(-328.9, 51.2) * mm, "end": v(-329.91, 50.27) * mm});
            skLineSegment(sketch, "E278", {"start": v(-329.91, 50.27) * mm, "end": v(-330.81, 49.24) * mm});
            skLineSegment(sketch, "E279", {"start": v(-330.81, 49.24) * mm, "end": v(-331.7, 47.98) * mm});
            skLineSegment(sketch, "E280", {"start": v(-331.7, 47.98) * mm, "end": v(-332.48, 46.65) * mm});
            skLineSegment(sketch, "E281", {"start": v(-332.48, 46.65) * mm, "end": v(-333.13, 45.26) * mm});
            skLineSegment(sketch, "E282", {"start": v(-333.13, 45.26) * mm, "end": v(-341.16, 45.26) * mm});
            skLineSegment(sketch, "E283", {"start": v(-341.16, 45.26) * mm, "end": v(-334.54, 65.68) * mm});
            skLineSegment(sketch, "E284", {"start": v(-334.54, 65.68) * mm, "end": v(-326.28, 65.79) * mm});
            skLineSegment(sketch, "E285", {"start": v(-326.28, 65.79) * mm, "end": v(-326.4, 63.29) * mm});
            skLineSegment(sketch, "E286", {"start": v(-279.7, 63.29) * mm, "end": v(-278.72, 65.79) * mm});
            skLineSegment(sketch, "E287", {"start": v(-278.72, 65.79) * mm, "end": v(-270.47, 65.79) * mm});
            skLineSegment(sketch, "E288", {"start": v(-270.47, 65.79) * mm, "end": v(-273.62, 45.26) * mm});
            skLineSegment(sketch, "E289", {"start": v(-273.62, 45.26) * mm, "end": v(-281.54, 45.26) * mm});
            skLineSegment(sketch, "E290", {"start": v(-281.54, 45.26) * mm, "end": v(-281.53, 46.7) * mm});
            skLineSegment(sketch, "E291", {"start": v(-281.53, 46.7) * mm, "end": v(-281.68, 48.12) * mm});
            skLineSegment(sketch, "E292", {"start": v(-281.68, 48.12) * mm, "end": v(-281.94, 49.27) * mm});
            skLineSegment(sketch, "E293", {"start": v(-281.94, 49.27) * mm, "end": v(-282.38, 50.36) * mm});
            skLineSegment(sketch, "E294", {"start": v(-282.38, 50.36) * mm, "end": v(-282.9, 51.24) * mm});
            skLineSegment(sketch, "E295", {"start": v(-282.9, 51.24) * mm, "end": v(-283.57, 52.03) * mm});
            skLineSegment(sketch, "E296", {"start": v(-283.57, 52.03) * mm, "end": v(-284.39, 52.71) * mm});
            skLineSegment(sketch, "E297", {"start": v(-284.39, 52.71) * mm, "end": v(-285.3, 53.26) * mm});
            skLineSegment(sketch, "E298", {"start": v(-285.3, 53.26) * mm, "end": v(-286.53, 53.76) * mm});
            skLineSegment(sketch, "E299", {"start": v(-286.53, 53.76) * mm, "end": v(-287.8, 54.08) * mm});
            skLineSegment(sketch, "E300", {"start": v(-287.8, 54.08) * mm, "end": v(-289.44, 54.3) * mm});
            skLineSegment(sketch, "E301", {"start": v(-289.44, 54.3) * mm, "end": v(-291.08, 54.4) * mm});
            skLineSegment(sketch, "E302", {"start": v(-291.08, 54.4) * mm, "end": v(-292.73, 54.38) * mm});
            skLineSegment(sketch, "E303", {"start": v(-292.73, 54.38) * mm, "end": v(-298.7, 29.3) * mm});
            skLineSegment(sketch, "E304", {"start": v(-226.14, 27.3) * mm, "end": v(-253.2, -5.89) * mm});
            skLineSegment(sketch, "E305", {"start": v(-253.2, -5.89) * mm, "end": v(-255.1, -8.14) * mm});
            skLineSegment(sketch, "E306", {"start": v(-255.1, -8.14) * mm, "end": v(-257.07, -10.32) * mm});
            skLineSegment(sketch, "E307", {"start": v(-257.07, -10.32) * mm, "end": v(-259.13, -12.42) * mm});
            skLineSegment(sketch, "E308", {"start": v(-259.13, -12.42) * mm, "end": v(-261.28, -14.44) * mm});
            skLineSegment(sketch, "E309", {"start": v(-261.28, -14.44) * mm, "end": v(-262.93, -15.84) * mm});
            skLineSegment(sketch, "E310", {"start": v(-262.93, -15.84) * mm, "end": v(-264.67, -17.14) * mm});
            skLineSegment(sketch, "E311", {"start": v(-264.67, -17.14) * mm, "end": v(-266.49, -18.32) * mm});
            skLineSegment(sketch, "E312", {"start": v(-266.49, -18.32) * mm, "end": v(-268.38, -19.4) * mm});
            skLineSegment(sketch, "E313", {"start": v(-268.38, -19.4) * mm, "end": v(-269.92, -20.13) * mm});
            skLineSegment(sketch, "E314", {"start": v(-269.92, -20.13) * mm, "end": v(-271.51, -20.75) * mm});
            skLineSegment(sketch, "E315", {"start": v(-271.51, -20.75) * mm, "end": v(-273.15, -21.25) * mm});
            skLineSegment(sketch, "E316", {"start": v(-273.15, -21.25) * mm, "end": v(-274.82, -21.62) * mm});
            skLineSegment(sketch, "E317", {"start": v(-274.82, -21.62) * mm, "end": v(-276.46, -21.84) * mm});
            skLineSegment(sketch, "E318", {"start": v(-276.46, -21.84) * mm, "end": v(-278.1, -21.95) * mm});
            skLineSegment(sketch, "E319", {"start": v(-278.1, -21.95) * mm, "end": v(-279.77, -21.95) * mm});
            skLineSegment(sketch, "E320", {"start": v(-279.77, -21.95) * mm, "end": v(-281.42, -21.83) * mm});
            skLineSegment(sketch, "E321", {"start": v(-281.42, -21.83) * mm, "end": v(-282.95, -21.62) * mm});
            skLineSegment(sketch, "E322", {"start": v(-282.95, -21.62) * mm, "end": v(-284.47, -21.3) * mm});
            skLineSegment(sketch, "E323", {"start": v(-284.47, -21.3) * mm, "end": v(-285.96, -20.87) * mm});
            skLineSegment(sketch, "E324", {"start": v(-285.96, -20.87) * mm, "end": v(-287.4, -20.33) * mm});
            skLineSegment(sketch, "E325", {"start": v(-287.4, -20.33) * mm, "end": v(-280.9, -7.4) * mm});
            skLineSegment(sketch, "E326", {"start": v(-280.9, -7.4) * mm, "end": v(-279.2, -8.14) * mm});
            skLineSegment(sketch, "E327", {"start": v(-279.2, -8.14) * mm, "end": v(-277.47, -8.76) * mm});
            skLineSegment(sketch, "E328", {"start": v(-277.47, -8.76) * mm, "end": v(-275.7, -9.28) * mm});
            skLineSegment(sketch, "E329", {"start": v(-275.7, -9.28) * mm, "end": v(-274.32, -9.58) * mm});
            skLineSegment(sketch, "E330", {"start": v(-274.32, -9.58) * mm, "end": v(-272.9, -9.75) * mm});
            skLineSegment(sketch, "E331", {"start": v(-272.9, -9.75) * mm, "end": v(-271.48, -9.8) * mm});
            skLineSegment(sketch, "E332", {"start": v(-271.48, -9.8) * mm, "end": v(-270.26, -9.71) * mm});
            skLineSegment(sketch, "E333", {"start": v(-270.26, -9.71) * mm, "end": v(-269.04, -9.51) * mm});
            skLineSegment(sketch, "E334", {"start": v(-269.04, -9.51) * mm, "end": v(-267.85, -9.2) * mm});
            skLineSegment(sketch, "E335", {"start": v(-267.85, -9.2) * mm, "end": v(-266.8, -8.82) * mm});
            skLineSegment(sketch, "E336", {"start": v(-266.8, -8.82) * mm, "end": v(-265.79, -8.33) * mm});
            skLineSegment(sketch, "E337", {"start": v(-265.79, -8.33) * mm, "end": v(-264.84, -7.75) * mm});
            skLineSegment(sketch, "E338", {"start": v(-264.84, -7.75) * mm, "end": v(-264, -7.1) * mm});
            skLineSegment(sketch, "E339", {"start": v(-264, -7.1) * mm, "end": v(-263.23, -6.37) * mm});
            skLineSegment(sketch, "E340", {"start": v(-263.23, -6.37) * mm, "end": v(-262.54, -5.56) * mm});
            skLineSegment(sketch, "E341", {"start": v(-262.54, -5.56) * mm, "end": v(-260.48, -2.84) * mm});
            skLineSegment(sketch, "E342", {"start": v(-260.48, -2.84) * mm, "end": v(-272.99, 27.3) * mm});
            skLineSegment(sketch, "E343", {"start": v(-272.99, 27.3) * mm, "end": v(-250.96, 27.3) * mm});
            skLineSegment(sketch, "E344", {"start": v(-250.96, 27.3) * mm, "end": v(-246.69, 13.77) * mm});
            skLineSegment(sketch, "E345", {"start": v(-246.69, 13.77) * mm, "end": v(-235.7, 27.3) * mm});
            skLineSegment(sketch, "E346", {"start": v(-235.7, 27.3) * mm, "end": v(-226.14, 27.3) * mm});
            skLineSegment(sketch, "E347", {"start": v(-224.5, 29.3) * mm, "end": v(-234.08, 29.3) * mm});
            skLineSegment(sketch, "E348", {"start": v(-234.08, 29.3) * mm, "end": v(-231.27, 32.77) * mm});
            skLineSegment(sketch, "E349", {"start": v(-231.27, 32.77) * mm, "end": v(-232.34, 32.37) * mm});
            skLineSegment(sketch, "E350", {"start": v(-232.34, 32.37) * mm, "end": v(-233.45, 32.09) * mm});
            skLineSegment(sketch, "E351", {"start": v(-233.45, 32.09) * mm, "end": v(-234.16, 32) * mm});
            skLineSegment(sketch, "E352", {"start": v(-234.16, 32) * mm, "end": v(-234.88, 32) * mm});
            skLineSegment(sketch, "E353", {"start": v(-234.88, 32) * mm, "end": v(-235.6, 32.1) * mm});
            skLineSegment(sketch, "E354", {"start": v(-235.6, 32.1) * mm, "end": v(-237.11, 32.44) * mm});
            skLineSegment(sketch, "E355", {"start": v(-237.11, 32.44) * mm, "end": v(-238.62, 32.86) * mm});
            skLineSegment(sketch, "E356", {"start": v(-238.62, 32.86) * mm, "end": v(-240.56, 33.44) * mm});
            skLineSegment(sketch, "E357", {"start": v(-240.56, 33.44) * mm, "end": v(-241.33, 33.62) * mm});
            skLineSegment(sketch, "E358", {"start": v(-241.33, 33.62) * mm, "end": v(-242.12, 33.74) * mm});
            skLineSegment(sketch, "E359", {"start": v(-242.12, 33.74) * mm, "end": v(-242.95, 33.75) * mm});
            skLineSegment(sketch, "E360", {"start": v(-242.95, 33.75) * mm, "end": v(-243.77, 33.64) * mm});
            skLineSegment(sketch, "E361", {"start": v(-243.77, 33.64) * mm, "end": v(-244.73, 33.37) * mm});
            skLineSegment(sketch, "E362", {"start": v(-244.73, 33.37) * mm, "end": v(-245.65, 32.97) * mm});
            skLineSegment(sketch, "E363", {"start": v(-245.65, 32.97) * mm, "end": v(-246.77, 32.33) * mm});
            skLineSegment(sketch, "E364", {"start": v(-246.77, 32.33) * mm, "end": v(-247.82, 31.58) * mm});
            skLineSegment(sketch, "E365", {"start": v(-247.82, 31.58) * mm, "end": v(-249.1, 30.49) * mm});
            skLineSegment(sketch, "E366", {"start": v(-249.1, 30.49) * mm, "end": v(-250.27, 29.3) * mm});
            skLineSegment(sketch, "E367", {"start": v(-250.27, 29.3) * mm, "end": v(-273.82, 29.3) * mm});
            skLineSegment(sketch, "E368", {"start": v(-273.82, 29.3) * mm, "end": v(-275.03, 32.23) * mm});
            skLineSegment(sketch, "E369", {"start": v(-275.03, 32.23) * mm, "end": v(-279.16, 31.04) * mm});
            skLineSegment(sketch, "E370", {"start": v(-279.16, 31.04) * mm, "end": v(-280.78, 35.38) * mm});
            skLineSegment(sketch, "E371", {"start": v(-280.78, 35.38) * mm, "end": v(-255.37, 46.02) * mm});
            skLineSegment(sketch, "E372", {"start": v(-255.37, 46.02) * mm, "end": v(-255.04, 43.08) * mm});
            skLineSegment(sketch, "E373", {"start": v(-255.04, 43.08) * mm, "end": v(-254.52, 40.16) * mm});
            skLineSegment(sketch, "E374", {"start": v(-254.52, 40.16) * mm, "end": v(-253.5, 36.29) * mm});
            skLineSegment(sketch, "E375", {"start": v(-253.5, 36.29) * mm, "end": v(-252.33, 32.45) * mm});
            skLineSegment(sketch, "E376", {"start": v(-252.33, 32.45) * mm, "end": v(-250.22, 34.83) * mm});
            skLineSegment(sketch, "E377", {"start": v(-250.22, 34.83) * mm, "end": v(-248.03, 37.13) * mm});
            skLineSegment(sketch, "E378", {"start": v(-248.03, 37.13) * mm, "end": v(-245.75, 39.36) * mm});
            skLineSegment(sketch, "E379", {"start": v(-245.75, 39.36) * mm, "end": v(-244.29, 40.68) * mm});
            skLineSegment(sketch, "E380", {"start": v(-244.29, 40.68) * mm, "end": v(-242.73, 41.9) * mm});
            skLineSegment(sketch, "E381", {"start": v(-242.73, 41.9) * mm, "end": v(-241.1, 43) * mm});
            skLineSegment(sketch, "E382", {"start": v(-241.1, 43) * mm, "end": v(-239.88, 43.7) * mm});
            skLineSegment(sketch, "E383", {"start": v(-239.88, 43.7) * mm, "end": v(-238.6, 44.27) * mm});
            skLineSegment(sketch, "E384", {"start": v(-238.6, 44.27) * mm, "end": v(-237.29, 44.75) * mm});
            skLineSegment(sketch, "E385", {"start": v(-237.29, 44.75) * mm, "end": v(-236.01, 45.08) * mm});
            skLineSegment(sketch, "E386", {"start": v(-236.01, 45.08) * mm, "end": v(-234.71, 45.28) * mm});
            skLineSegment(sketch, "E387", {"start": v(-234.71, 45.28) * mm, "end": v(-233.4, 45.36) * mm});
            skLineSegment(sketch, "E388", {"start": v(-233.4, 45.36) * mm, "end": v(-231.28, 45.26) * mm});
            skLineSegment(sketch, "E389", {"start": v(-231.28, 45.26) * mm, "end": v(-229.18, 44.97) * mm});
            skLineSegment(sketch, "E390", {"start": v(-229.18, 44.97) * mm, "end": v(-227.44, 44.62) * mm});
            skLineSegment(sketch, "E391", {"start": v(-227.44, 44.62) * mm, "end": v(-225.7, 44.22) * mm});
            skLineSegment(sketch, "E392", {"start": v(-225.7, 44.22) * mm, "end": v(-223.86, 43.83) * mm});
            skLineSegment(sketch, "E393", {"start": v(-223.86, 43.83) * mm, "end": v(-222, 43.57) * mm});
            skLineSegment(sketch, "E394", {"start": v(-222, 43.57) * mm, "end": v(-220.8, 43.52) * mm});
            skLineSegment(sketch, "E395", {"start": v(-220.8, 43.52) * mm, "end": v(-219.59, 43.59) * mm});
            skLineSegment(sketch, "E396", {"start": v(-219.59, 43.59) * mm, "end": v(-218.4, 43.76) * mm});
            skLineSegment(sketch, "E397", {"start": v(-218.4, 43.76) * mm, "end": v(-217.19, 44.05) * mm});
            skLineSegment(sketch, "E398", {"start": v(-217.19, 44.05) * mm, "end": v(-216.01, 44.45) * mm});
            skLineSegment(sketch, "E399", {"start": v(-216.01, 44.45) * mm, "end": v(-214.87, 44.94) * mm});
            skLineSegment(sketch, "E400", {"start": v(-214.87, 44.94) * mm, "end": v(-212.92, 42.76) * mm});
            skLineSegment(sketch, "E401", {"start": v(-212.92, 42.76) * mm, "end": v(-214.54, 41.18) * mm});
            skLineSegment(sketch, "E402", {"start": v(-214.54, 41.18) * mm, "end": v(-216.07, 39.51) * mm});
            skLineSegment(sketch, "E403", {"start": v(-216.07, 39.51) * mm, "end": v(-218.6, 36.54) * mm});
            skLineSegment(sketch, "E404", {"start": v(-218.6, 36.54) * mm, "end": v(-221.06, 33.53) * mm});
            skLineSegment(sketch, "E405", {"start": v(-221.06, 33.53) * mm, "end": v(-224.5, 29.3) * mm});
            skLineSegment(sketch, "E406", {"start": v(-160.46, 27.3) * mm, "end": v(-141.77, 27.3) * mm});
            skLineSegment(sketch, "E407", {"start": v(-141.77, 27.3) * mm, "end": v(-141.8, 25.76) * mm});
            skLineSegment(sketch, "E408", {"start": v(-141.8, 25.76) * mm, "end": v(-141.7, 24.2) * mm});
            skLineSegment(sketch, "E409", {"start": v(-141.7, 24.2) * mm, "end": v(-141.46, 22.67) * mm});
            skLineSegment(sketch, "E410", {"start": v(-141.46, 22.67) * mm, "end": v(-126.58, 27.3) * mm});
            skLineSegment(sketch, "E411", {"start": v(-126.58, 27.3) * mm, "end": v(-103.98, 27.3) * mm});
            skLineSegment(sketch, "E412", {"start": v(-103.98, 27.3) * mm, "end": v(-103.94, 26.66) * mm});
            skLineSegment(sketch, "E413", {"start": v(-103.94, 26.66) * mm, "end": v(-103.96, 26.35) * mm});
            skLineSegment(sketch, "E414", {"start": v(-103.96, 26.35) * mm, "end": v(-104.08, 26.07) * mm});
            skLineSegment(sketch, "E415", {"start": v(-104.08, 26.07) * mm, "end": v(-104.3, 25.84) * mm});
            skLineSegment(sketch, "E416", {"start": v(-104.3, 25.84) * mm, "end": v(-104.58, 25.67) * mm});
            skLineSegment(sketch, "E417", {"start": v(-104.58, 25.67) * mm, "end": v(-105.17, 25.5) * mm});
            skLineSegment(sketch, "E418", {"start": v(-105.17, 25.5) * mm, "end": v(-105.78, 25.39) * mm});
            skLineSegment(sketch, "E419", {"start": v(-105.78, 25.39) * mm, "end": v(-106.25, 25.3) * mm});
            skLineSegment(sketch, "E420", {"start": v(-106.25, 25.3) * mm, "end": v(-107.44, 25.07) * mm});
            skLineSegment(sketch, "E421", {"start": v(-107.44, 25.07) * mm, "end": v(-109.94, 24.55) * mm});
            skLineSegment(sketch, "E422", {"start": v(-109.94, 24.55) * mm, "end": v(-112.4, 23.93) * mm});
            skLineSegment(sketch, "E423", {"start": v(-112.4, 23.93) * mm, "end": v(-114.86, 23.22) * mm});
            skLineSegment(sketch, "E424", {"start": v(-114.86, 23.22) * mm, "end": v(-140.05, 15.4) * mm});
            skLineSegment(sketch, "E425", {"start": v(-140.05, 15.4) * mm, "end": v(-139.47, 14) * mm});
            skLineSegment(sketch, "E426", {"start": v(-139.47, 14) * mm, "end": v(-138.74, 12.66) * mm});
            skLineSegment(sketch, "E427", {"start": v(-138.74, 12.66) * mm, "end": v(-137.87, 11.42) * mm});
            skLineSegment(sketch, "E428", {"start": v(-137.87, 11.42) * mm, "end": v(-136.89, 10.33) * mm});
            skLineSegment(sketch, "E429", {"start": v(-136.89, 10.33) * mm, "end": v(-135.78, 9.38) * mm});
            skLineSegment(sketch, "E430", {"start": v(-135.78, 9.38) * mm, "end": v(-134.55, 8.58) * mm});
            skLineSegment(sketch, "E431", {"start": v(-134.55, 8.58) * mm, "end": v(-133.09, 7.87) * mm});
            skLineSegment(sketch, "E432", {"start": v(-133.09, 7.87) * mm, "end": v(-131.55, 7.34) * mm});
            skLineSegment(sketch, "E433", {"start": v(-131.55, 7.34) * mm, "end": v(-129.97, 7) * mm});
            skLineSegment(sketch, "E434", {"start": v(-129.97, 7) * mm, "end": v(-127.98, 6.76) * mm});
            skLineSegment(sketch, "E435", {"start": v(-127.98, 6.76) * mm, "end": v(-125.98, 6.71) * mm});
            skLineSegment(sketch, "E436", {"start": v(-125.98, 6.71) * mm, "end": v(-123.99, 6.84) * mm});
            skLineSegment(sketch, "E437", {"start": v(-123.99, 6.84) * mm, "end": v(-121.76, 7.18) * mm});
            skLineSegment(sketch, "E438", {"start": v(-121.76, 7.18) * mm, "end": v(-119.57, 7.7) * mm});
            skLineSegment(sketch, "E439", {"start": v(-119.57, 7.7) * mm, "end": v(-117.43, 8.42) * mm});
            skLineSegment(sketch, "E440", {"start": v(-117.43, 8.42) * mm, "end": v(-115.21, 9.38) * mm});
            skLineSegment(sketch, "E441", {"start": v(-115.21, 9.38) * mm, "end": v(-113.08, 10.51) * mm});
            skLineSegment(sketch, "E442", {"start": v(-113.08, 10.51) * mm, "end": v(-111.06, 11.82) * mm});
            skLineSegment(sketch, "E443", {"start": v(-111.06, 11.82) * mm, "end": v(-107.58, 7.9) * mm});
            skLineSegment(sketch, "E444", {"start": v(-107.58, 7.9) * mm, "end": v(-109.91, 6.01) * mm});
            skLineSegment(sketch, "E445", {"start": v(-109.91, 6.01) * mm, "end": v(-112.34, 4.24) * mm});
            skLineSegment(sketch, "E446", {"start": v(-112.34, 4.24) * mm, "end": v(-114.84, 2.58) * mm});
            skLineSegment(sketch, "E447", {"start": v(-114.84, 2.58) * mm, "end": v(-117.43, 1.05) * mm});
            skLineSegment(sketch, "E448", {"start": v(-117.43, 1.05) * mm, "end": v(-119.87, -0.22) * mm});
            skLineSegment(sketch, "E449", {"start": v(-119.87, -0.22) * mm, "end": v(-122.38, -1.36) * mm});
            skLineSegment(sketch, "E450", {"start": v(-122.38, -1.36) * mm, "end": v(-124.95, -2.34) * mm});
            skLineSegment(sketch, "E451", {"start": v(-124.95, -2.34) * mm, "end": v(-127.58, -3.17) * mm});
            skLineSegment(sketch, "E452", {"start": v(-127.58, -3.17) * mm, "end": v(-130.13, -3.82) * mm});
            skLineSegment(sketch, "E453", {"start": v(-130.13, -3.82) * mm, "end": v(-132.71, -4.33) * mm});
            skLineSegment(sketch, "E454", {"start": v(-132.71, -4.33) * mm, "end": v(-135.32, -4.7) * mm});
            skLineSegment(sketch, "E455", {"start": v(-135.32, -4.7) * mm, "end": v(-137.94, -4.93) * mm});
            skLineSegment(sketch, "E456", {"start": v(-137.94, -4.93) * mm, "end": v(-140.26, -5.02) * mm});
            skLineSegment(sketch, "E457", {"start": v(-140.26, -5.02) * mm, "end": v(-142.57, -4.97) * mm});
            skLineSegment(sketch, "E458", {"start": v(-142.57, -4.97) * mm, "end": v(-144.88, -4.8) * mm});
            skLineSegment(sketch, "E459", {"start": v(-144.88, -4.8) * mm, "end": v(-147.17, -4.48) * mm});
            skLineSegment(sketch, "E460", {"start": v(-147.17, -4.48) * mm, "end": v(-148.98, -4.1) * mm});
            skLineSegment(sketch, "E461", {"start": v(-148.98, -4.1) * mm, "end": v(-150.76, -3.59) * mm});
            skLineSegment(sketch, "E462", {"start": v(-150.76, -3.59) * mm, "end": v(-152.49, -2.94) * mm});
            skLineSegment(sketch, "E463", {"start": v(-152.49, -2.94) * mm, "end": v(-154.16, -2.15) * mm});
            skLineSegment(sketch, "E464", {"start": v(-154.16, -2.15) * mm, "end": v(-155.54, -1.37) * mm});
            skLineSegment(sketch, "E465", {"start": v(-155.54, -1.37) * mm, "end": v(-156.85, -0.47) * mm});
            skLineSegment(sketch, "E466", {"start": v(-156.85, -0.47) * mm, "end": v(-158.07, 0.53) * mm});
            skLineSegment(sketch, "E467", {"start": v(-158.07, 0.53) * mm, "end": v(-159.2, 1.64) * mm});
            skLineSegment(sketch, "E468", {"start": v(-159.2, 1.64) * mm, "end": v(-160.18, 2.78) * mm});
            skLineSegment(sketch, "E469", {"start": v(-160.18, 2.78) * mm, "end": v(-161.06, 4) * mm});
            skLineSegment(sketch, "E470", {"start": v(-161.06, 4) * mm, "end": v(-161.82, 5.3) * mm});
            skLineSegment(sketch, "E471", {"start": v(-161.82, 5.3) * mm, "end": v(-162.46, 6.67) * mm});
            skLineSegment(sketch, "E472", {"start": v(-162.46, 6.67) * mm, "end": v(-163, 8.16) * mm});
            skLineSegment(sketch, "E473", {"start": v(-163, 8.16) * mm, "end": v(-163.43, 9.7) * mm});
            skLineSegment(sketch, "E474", {"start": v(-163.43, 9.7) * mm, "end": v(-163.72, 11.26) * mm});
            skLineSegment(sketch, "E475", {"start": v(-163.72, 11.26) * mm, "end": v(-163.87, 12.85) * mm});
            skLineSegment(sketch, "E476", {"start": v(-163.87, 12.85) * mm, "end": v(-163.9, 14.68) * mm});
            skLineSegment(sketch, "E477", {"start": v(-163.9, 14.68) * mm, "end": v(-163.8, 16.5) * mm});
            skLineSegment(sketch, "E478", {"start": v(-163.8, 16.5) * mm, "end": v(-163.57, 18.32) * mm});
            skLineSegment(sketch, "E479", {"start": v(-163.57, 18.32) * mm, "end": v(-163.22, 20.11) * mm});
            skLineSegment(sketch, "E480", {"start": v(-163.22, 20.11) * mm, "end": v(-162.72, 21.98) * mm});
            skLineSegment(sketch, "E481", {"start": v(-162.72, 21.98) * mm, "end": v(-162.09, 23.8) * mm});
            skLineSegment(sketch, "E482", {"start": v(-162.09, 23.8) * mm, "end": v(-161.34, 25.58) * mm});
            skLineSegment(sketch, "E483", {"start": v(-161.34, 25.58) * mm, "end": v(-160.46, 27.3) * mm});
            skLineSegment(sketch, "E484", {"start": v(-159.27, 29.3) * mm, "end": v(-157.91, 31.22) * mm});
            skLineSegment(sketch, "E485", {"start": v(-157.91, 31.22) * mm, "end": v(-156.43, 33.05) * mm});
            skLineSegment(sketch, "E486", {"start": v(-156.43, 33.05) * mm, "end": v(-154.82, 34.77) * mm});
            skLineSegment(sketch, "E487", {"start": v(-154.82, 34.77) * mm, "end": v(-153.1, 36.37) * mm});
            skLineSegment(sketch, "E488", {"start": v(-153.1, 36.37) * mm, "end": v(-151.17, 37.94) * mm});
            skLineSegment(sketch, "E489", {"start": v(-151.17, 37.94) * mm, "end": v(-149.15, 39.4) * mm});
            skLineSegment(sketch, "E490", {"start": v(-149.15, 39.4) * mm, "end": v(-147.04, 40.71) * mm});
            skLineSegment(sketch, "E491", {"start": v(-147.04, 40.71) * mm, "end": v(-144.85, 41.9) * mm});
            skLineSegment(sketch, "E492", {"start": v(-144.85, 41.9) * mm, "end": v(-142.57, 42.96) * mm});
            skLineSegment(sketch, "E493", {"start": v(-142.57, 42.96) * mm, "end": v(-140.22, 43.89) * mm});
            skLineSegment(sketch, "E494", {"start": v(-140.22, 43.89) * mm, "end": v(-137.82, 44.66) * mm});
            skLineSegment(sketch, "E495", {"start": v(-137.82, 44.66) * mm, "end": v(-135.37, 45.28) * mm});
            skLineSegment(sketch, "E496", {"start": v(-135.37, 45.28) * mm, "end": v(-133.04, 45.7) * mm});
            skLineSegment(sketch, "E497", {"start": v(-133.04, 45.7) * mm, "end": v(-130.69, 45.99) * mm});
            skLineSegment(sketch, "E498", {"start": v(-130.69, 45.99) * mm, "end": v(-128.32, 46.12) * mm});
            skLineSegment(sketch, "E499", {"start": v(-128.32, 46.12) * mm, "end": v(-125.95, 46.1) * mm});
            skLineSegment(sketch, "E500", {"start": v(-125.95, 46.1) * mm, "end": v(-123.88, 45.94) * mm});
            skLineSegment(sketch, "E501", {"start": v(-123.88, 45.94) * mm, "end": v(-121.82, 45.64) * mm});
            skLineSegment(sketch, "E502", {"start": v(-121.82, 45.64) * mm, "end": v(-119.79, 45.2) * mm});
            skLineSegment(sketch, "E503", {"start": v(-119.79, 45.2) * mm, "end": v(-117.79, 44.62) * mm});
            skLineSegment(sketch, "E504", {"start": v(-117.79, 44.62) * mm, "end": v(-116.13, 43.98) * mm});
            skLineSegment(sketch, "E505", {"start": v(-116.13, 43.98) * mm, "end": v(-114.53, 43.2) * mm});
            skLineSegment(sketch, "E506", {"start": v(-114.53, 43.2) * mm, "end": v(-113.01, 42.27) * mm});
            skLineSegment(sketch, "E507", {"start": v(-113.01, 42.27) * mm, "end": v(-111.59, 41.21) * mm});
            skLineSegment(sketch, "E508", {"start": v(-111.59, 41.21) * mm, "end": v(-110.3, 40.04) * mm});
            skLineSegment(sketch, "E509", {"start": v(-110.3, 40.04) * mm, "end": v(-109.1, 38.77) * mm});
            skLineSegment(sketch, "E510", {"start": v(-109.1, 38.77) * mm, "end": v(-108.02, 37.4) * mm});
            skLineSegment(sketch, "E511", {"start": v(-108.02, 37.4) * mm, "end": v(-107.06, 35.94) * mm});
            skLineSegment(sketch, "E512", {"start": v(-107.06, 35.94) * mm, "end": v(-106.19, 34.36) * mm});
            skLineSegment(sketch, "E513", {"start": v(-106.19, 34.36) * mm, "end": v(-105.43, 32.72) * mm});
            skLineSegment(sketch, "E514", {"start": v(-105.43, 32.72) * mm, "end": v(-104.8, 31.04) * mm});
            skLineSegment(sketch, "E515", {"start": v(-104.8, 31.04) * mm, "end": v(-104.3, 29.3) * mm});
            skLineSegment(sketch, "E516", {"start": v(-104.3, 29.3) * mm, "end": v(-125.34, 29.3) * mm});
            skLineSegment(sketch, "E517", {"start": v(-125.34, 29.3) * mm, "end": v(-125.8, 31.07) * mm});
            skLineSegment(sketch, "E518", {"start": v(-125.8, 31.07) * mm, "end": v(-126.4, 32.8) * mm});
            skLineSegment(sketch, "E519", {"start": v(-126.4, 32.8) * mm, "end": v(-126.98, 34.03) * mm});
            skLineSegment(sketch, "E520", {"start": v(-126.98, 34.03) * mm, "end": v(-127.7, 35.19) * mm});
            skLineSegment(sketch, "E521", {"start": v(-127.7, 35.19) * mm, "end": v(-128.4, 36.05) * mm});
            skLineSegment(sketch, "E522", {"start": v(-128.4, 36.05) * mm, "end": v(-129.19, 36.81) * mm});
            skLineSegment(sketch, "E523", {"start": v(-129.19, 36.81) * mm, "end": v(-129.97, 37.38) * mm});
            skLineSegment(sketch, "E524", {"start": v(-129.97, 37.38) * mm, "end": v(-130.83, 37.82) * mm});
            skLineSegment(sketch, "E525", {"start": v(-130.83, 37.82) * mm, "end": v(-131.77, 38.12) * mm});
            skLineSegment(sketch, "E526", {"start": v(-131.77, 38.12) * mm, "end": v(-132.74, 38.28) * mm});
            skLineSegment(sketch, "E527", {"start": v(-132.74, 38.28) * mm, "end": v(-133.72, 38.32) * mm});
            skLineSegment(sketch, "E528", {"start": v(-133.72, 38.32) * mm, "end": v(-134.7, 38.21) * mm});
            skLineSegment(sketch, "E529", {"start": v(-134.7, 38.21) * mm, "end": v(-135.64, 37.99) * mm});
            skLineSegment(sketch, "E530", {"start": v(-135.64, 37.99) * mm, "end": v(-136.54, 37.62) * mm});
            skLineSegment(sketch, "E531", {"start": v(-136.54, 37.62) * mm, "end": v(-137.4, 37.12) * mm});
            skLineSegment(sketch, "E532", {"start": v(-137.4, 37.12) * mm, "end": v(-138.18, 36.5) * mm});
            skLineSegment(sketch, "E533", {"start": v(-138.18, 36.5) * mm, "end": v(-138.95, 35.69) * mm});
            skLineSegment(sketch, "E534", {"start": v(-138.95, 35.69) * mm, "end": v(-139.61, 34.78) * mm});
            skLineSegment(sketch, "E535", {"start": v(-139.61, 34.78) * mm, "end": v(-140.26, 33.61) * mm});
            skLineSegment(sketch, "E536", {"start": v(-140.26, 33.61) * mm, "end": v(-140.77, 32.38) * mm});
            skLineSegment(sketch, "E537", {"start": v(-140.77, 32.38) * mm, "end": v(-141.23, 30.86) * mm});
            skLineSegment(sketch, "E538", {"start": v(-141.23, 30.86) * mm, "end": v(-141.55, 29.3) * mm});
            skLineSegment(sketch, "E539", {"start": v(-141.55, 29.3) * mm, "end": v(-159.27, 29.3) * mm});
            skLineSegment(sketch, "E540", {"start": v(-168.1, 29.3) * mm, "end": v(-172.11, 29.3) * mm});
            skLineSegment(sketch, "E541", {"start": v(-172.11, 29.3) * mm, "end": v(-173.62, 29.74) * mm});
            skLineSegment(sketch, "E542", {"start": v(-173.62, 29.74) * mm, "end": v(-175.15, 30.07) * mm});
            skLineSegment(sketch, "E543", {"start": v(-175.15, 30.07) * mm, "end": v(-176.7, 30.3) * mm});
            skLineSegment(sketch, "E544", {"start": v(-176.7, 30.3) * mm, "end": v(-177.86, 30.39) * mm});
            skLineSegment(sketch, "E545", {"start": v(-177.86, 30.39) * mm, "end": v(-179.01, 30.36) * mm});
            skLineSegment(sketch, "E546", {"start": v(-179.01, 30.36) * mm, "end": v(-180.16, 30.22) * mm});
            skLineSegment(sketch, "E547", {"start": v(-180.16, 30.22) * mm, "end": v(-181.1, 30) * mm});
            skLineSegment(sketch, "E548", {"start": v(-181.1, 30) * mm, "end": v(-182.03, 29.7) * mm});
            skLineSegment(sketch, "E549", {"start": v(-182.03, 29.7) * mm, "end": v(-182.93, 29.3) * mm});
            skLineSegment(sketch, "E550", {"start": v(-182.93, 29.3) * mm, "end": v(-207.86, 29.3) * mm});
            skLineSegment(sketch, "E551", {"start": v(-207.86, 29.3) * mm, "end": v(-207.97, 29.74) * mm});
            skLineSegment(sketch, "E552", {"start": v(-207.97, 29.74) * mm, "end": v(-208.18, 30.13) * mm});
            skLineSegment(sketch, "E553", {"start": v(-208.18, 30.13) * mm, "end": v(-208.48, 30.47) * mm});
            skLineSegment(sketch, "E554", {"start": v(-208.48, 30.47) * mm, "end": v(-208.84, 30.77) * mm});
            skLineSegment(sketch, "E555", {"start": v(-208.84, 30.77) * mm, "end": v(-209.22, 31.04) * mm});
            skLineSegment(sketch, "E556", {"start": v(-209.22, 31.04) * mm, "end": v(-211.83, 29.52) * mm});
            skLineSegment(sketch, "E557", {"start": v(-211.83, 29.52) * mm, "end": v(-215.2, 33.42) * mm});
            skLineSegment(sketch, "E558", {"start": v(-215.2, 33.42) * mm, "end": v(-199.23, 46.02) * mm});
            skLineSegment(sketch, "E559", {"start": v(-199.23, 46.02) * mm, "end": v(-197.6, 45.32) * mm});
            skLineSegment(sketch, "E560", {"start": v(-197.6, 45.32) * mm, "end": v(-196, 44.54) * mm});
            skLineSegment(sketch, "E561", {"start": v(-196, 44.54) * mm, "end": v(-194.44, 43.67) * mm});
            skLineSegment(sketch, "E562", {"start": v(-194.44, 43.67) * mm, "end": v(-193.3, 42.95) * mm});
            skLineSegment(sketch, "E563", {"start": v(-193.3, 42.95) * mm, "end": v(-192.23, 42.13) * mm});
            skLineSegment(sketch, "E564", {"start": v(-192.23, 42.13) * mm, "end": v(-191.23, 41.24) * mm});
            skLineSegment(sketch, "E565", {"start": v(-191.23, 41.24) * mm, "end": v(-190.5, 40.48) * mm});
            skLineSegment(sketch, "E566", {"start": v(-190.5, 40.48) * mm, "end": v(-189.86, 39.65) * mm});
            skLineSegment(sketch, "E567", {"start": v(-189.86, 39.65) * mm, "end": v(-189.29, 38.76) * mm});
            skLineSegment(sketch, "E568", {"start": v(-189.29, 38.76) * mm, "end": v(-188.86, 37.92) * mm});
            skLineSegment(sketch, "E569", {"start": v(-188.86, 37.92) * mm, "end": v(-188.52, 37.05) * mm});
            skLineSegment(sketch, "E570", {"start": v(-188.52, 37.05) * mm, "end": v(-188.26, 36.14) * mm});
            skLineSegment(sketch, "E571", {"start": v(-188.26, 36.14) * mm, "end": v(-186.08, 38.28) * mm});
            skLineSegment(sketch, "E572", {"start": v(-186.08, 38.28) * mm, "end": v(-183.82, 40.35) * mm});
            skLineSegment(sketch, "E573", {"start": v(-183.82, 40.35) * mm, "end": v(-181.49, 42.34) * mm});
            skLineSegment(sketch, "E574", {"start": v(-181.49, 42.34) * mm, "end": v(-180.17, 43.4) * mm});
            skLineSegment(sketch, "E575", {"start": v(-180.17, 43.4) * mm, "end": v(-178.76, 44.32) * mm});
            skLineSegment(sketch, "E576", {"start": v(-178.76, 44.32) * mm, "end": v(-177.28, 45.13) * mm});
            skLineSegment(sketch, "E577", {"start": v(-177.28, 45.13) * mm, "end": v(-176.26, 45.56) * mm});
            skLineSegment(sketch, "E578", {"start": v(-176.26, 45.56) * mm, "end": v(-175.2, 45.87) * mm});
            skLineSegment(sketch, "E579", {"start": v(-175.2, 45.87) * mm, "end": v(-174.1, 46.07) * mm});
            skLineSegment(sketch, "E580", {"start": v(-174.1, 46.07) * mm, "end": v(-172.9, 46.13) * mm});
            skLineSegment(sketch, "E581", {"start": v(-172.9, 46.13) * mm, "end": v(-171.7, 46.06) * mm});
            skLineSegment(sketch, "E582", {"start": v(-171.7, 46.06) * mm, "end": v(-170.52, 45.86) * mm});
            skLineSegment(sketch, "E583", {"start": v(-170.52, 45.86) * mm, "end": v(-168.84, 45.46) * mm});
            skLineSegment(sketch, "E584", {"start": v(-168.84, 45.46) * mm, "end": v(-167.2, 44.97) * mm});
            skLineSegment(sketch, "E585", {"start": v(-167.2, 44.97) * mm, "end": v(-165.57, 44.4) * mm});
            skLineSegment(sketch, "E586", {"start": v(-165.57, 44.4) * mm, "end": v(-163.72, 46.56) * mm});
            skLineSegment(sketch, "E587", {"start": v(-163.72, 46.56) * mm, "end": v(-157.75, 44.72) * mm});
            skLineSegment(sketch, "E588", {"start": v(-157.75, 44.72) * mm, "end": v(-168.1, 29.3) * mm});
            skLineSegment(sketch, "E589", {"start": v(-185.5, 27.3) * mm, "end": v(-186.22, 26.34) * mm});
            skLineSegment(sketch, "E590", {"start": v(-186.22, 26.34) * mm, "end": v(-186.84, 25.3) * mm});
            skLineSegment(sketch, "E591", {"start": v(-186.84, 25.3) * mm, "end": v(-187.35, 24.12) * mm});
            skLineSegment(sketch, "E592", {"start": v(-187.35, 24.12) * mm, "end": v(-187.72, 22.9) * mm});
            skLineSegment(sketch, "E593", {"start": v(-187.72, 22.9) * mm, "end": v(-192.6, 2.37) * mm});
            skLineSegment(sketch, "E594", {"start": v(-192.6, 2.37) * mm, "end": v(-186.53, 2.37) * mm});
            skLineSegment(sketch, "E595", {"start": v(-186.53, 2.37) * mm, "end": v(-187.94, -3.71) * mm});
            skLineSegment(sketch, "E596", {"start": v(-187.94, -3.71) * mm, "end": v(-219.76, -3.71) * mm});
            skLineSegment(sketch, "E597", {"start": v(-219.76, -3.71) * mm, "end": v(-218.34, 2.37) * mm});
            skLineSegment(sketch, "E598", {"start": v(-218.34, 2.37) * mm, "end": v(-214.1, 2.37) * mm});
            skLineSegment(sketch, "E599", {"start": v(-214.1, 2.37) * mm, "end": v(-208.1, 27.3) * mm});
            skLineSegment(sketch, "E600", {"start": v(-208.1, 27.3) * mm, "end": v(-185.5, 27.3) * mm});
            skLineSegment(sketch, "E601", {"start": v(17.88, 27.3) * mm, "end": v(17.93, 25.53) * mm});
            skLineSegment(sketch, "E602", {"start": v(17.93, 25.53) * mm, "end": v(17.83, 23.76) * mm});
            skLineSegment(sketch, "E603", {"start": v(17.83, 23.76) * mm, "end": v(17.59, 22) * mm});
            skLineSegment(sketch, "E604", {"start": v(17.59, 22) * mm, "end": v(17.2, 20.27) * mm});
            skLineSegment(sketch, "E605", {"start": v(17.2, 20.27) * mm, "end": v(16.65, 18.4) * mm});
            skLineSegment(sketch, "E606", {"start": v(16.65, 18.4) * mm, "end": v(15.96, 16.6) * mm});
            skLineSegment(sketch, "E607", {"start": v(15.96, 16.6) * mm, "end": v(15.13, 14.83) * mm});
            skLineSegment(sketch, "E608", {"start": v(15.13, 14.83) * mm, "end": v(14.18, 13.14) * mm});
            skLineSegment(sketch, "E609", {"start": v(14.18, 13.14) * mm, "end": v(13, 11.33) * mm});
            skLineSegment(sketch, "E610", {"start": v(13, 11.33) * mm, "end": v(11.69, 9.61) * mm});
            skLineSegment(sketch, "E611", {"start": v(11.69, 9.61) * mm, "end": v(10.27, 7.99) * mm});
            skLineSegment(sketch, "E612", {"start": v(10.27, 7.99) * mm, "end": v(8.74, 6.47) * mm});
            skLineSegment(sketch, "E613", {"start": v(8.74, 6.47) * mm, "end": v(6.93, 4.89) * mm});
            skLineSegment(sketch, "E614", {"start": v(6.93, 4.89) * mm, "end": v(5.03, 3.42) * mm});
            skLineSegment(sketch, "E615", {"start": v(5.03, 3.42) * mm, "end": v(3.04, 2.08) * mm});
            skLineSegment(sketch, "E616", {"start": v(3.04, 2.08) * mm, "end": v(0.97, 0.86) * mm});
            skLineSegment(sketch, "E617", {"start": v(0.97, 0.86) * mm, "end": v(-1.37, -0.33) * mm});
            skLineSegment(sketch, "E618", {"start": v(-1.37, -0.33) * mm, "end": v(-3.77, -1.39) * mm});
            skLineSegment(sketch, "E619", {"start": v(-3.77, -1.39) * mm, "end": v(-6.24, -2.3) * mm});
            skLineSegment(sketch, "E620", {"start": v(-6.24, -2.3) * mm, "end": v(-8.75, -3.06) * mm});
            skLineSegment(sketch, "E621", {"start": v(-8.75, -3.06) * mm, "end": v(-11.46, -3.72) * mm});
            skLineSegment(sketch, "E622", {"start": v(-11.46, -3.72) * mm, "end": v(-14.2, -4.24) * mm});
            skLineSegment(sketch, "E623", {"start": v(-14.2, -4.24) * mm, "end": v(-16.96, -4.6) * mm});
            skLineSegment(sketch, "E624", {"start": v(-16.96, -4.6) * mm, "end": v(-19.74, -4.83) * mm});
            skLineSegment(sketch, "E625", {"start": v(-19.74, -4.83) * mm, "end": v(-22.34, -4.9) * mm});
            skLineSegment(sketch, "E626", {"start": v(-22.34, -4.9) * mm, "end": v(-24.95, -4.84) * mm});
            skLineSegment(sketch, "E627", {"start": v(-24.95, -4.84) * mm, "end": v(-27.54, -4.63) * mm});
            skLineSegment(sketch, "E628", {"start": v(-27.54, -4.63) * mm, "end": v(-30.12, -4.27) * mm});
            skLineSegment(sketch, "E629", {"start": v(-30.12, -4.27) * mm, "end": v(-32.3, -3.83) * mm});
            skLineSegment(sketch, "E630", {"start": v(-32.3, -3.83) * mm, "end": v(-34.42, -3.24) * mm});
            skLineSegment(sketch, "E631", {"start": v(-34.42, -3.24) * mm, "end": v(-36.51, -2.51) * mm});
            skLineSegment(sketch, "E632", {"start": v(-36.51, -2.51) * mm, "end": v(-38.55, -1.65) * mm});
            skLineSegment(sketch, "E633", {"start": v(-38.55, -1.65) * mm, "end": v(-40.17, -0.82) * mm});
            skLineSegment(sketch, "E634", {"start": v(-40.17, -0.82) * mm, "end": v(-41.73, 0.13) * mm});
            skLineSegment(sketch, "E635", {"start": v(-41.73, 0.13) * mm, "end": v(-43.2, 1.2) * mm});
            skLineSegment(sketch, "E636", {"start": v(-43.2, 1.2) * mm, "end": v(-44.6, 2.4) * mm});
            skLineSegment(sketch, "E637", {"start": v(-44.6, 2.4) * mm, "end": v(-45.71, 3.53) * mm});
            skLineSegment(sketch, "E638", {"start": v(-45.71, 3.53) * mm, "end": v(-46.73, 4.76) * mm});
            skLineSegment(sketch, "E639", {"start": v(-46.73, 4.76) * mm, "end": v(-47.63, 6.08) * mm});
            skLineSegment(sketch, "E640", {"start": v(-47.63, 6.08) * mm, "end": v(-48.4, 7.47) * mm});
            skLineSegment(sketch, "E641", {"start": v(-48.4, 7.47) * mm, "end": v(-49.04, 8.9) * mm});
            skLineSegment(sketch, "E642", {"start": v(-49.04, 8.9) * mm, "end": v(-49.54, 10.38) * mm});
            skLineSegment(sketch, "E643", {"start": v(-49.54, 10.38) * mm, "end": v(-49.9, 11.9) * mm});
            skLineSegment(sketch, "E644", {"start": v(-49.9, 11.9) * mm, "end": v(-50.13, 13.44) * mm});
            skLineSegment(sketch, "E645", {"start": v(-50.13, 13.44) * mm, "end": v(-50.23, 15.15) * mm});
            skLineSegment(sketch, "E646", {"start": v(-50.23, 15.15) * mm, "end": v(-50.18, 16.87) * mm});
            skLineSegment(sketch, "E647", {"start": v(-50.18, 16.87) * mm, "end": v(-50, 18.58) * mm});
            skLineSegment(sketch, "E648", {"start": v(-50, 18.58) * mm, "end": v(-49.68, 20.26) * mm});
            skLineSegment(sketch, "E649", {"start": v(-49.68, 20.26) * mm, "end": v(-49.2, 22.1) * mm});
            skLineSegment(sketch, "E650", {"start": v(-49.2, 22.1) * mm, "end": v(-48.58, 23.88) * mm});
            skLineSegment(sketch, "E651", {"start": v(-48.58, 23.88) * mm, "end": v(-47.83, 25.62) * mm});
            skLineSegment(sketch, "E652", {"start": v(-47.83, 25.62) * mm, "end": v(-46.97, 27.3) * mm});
            skLineSegment(sketch, "E653", {"start": v(-46.97, 27.3) * mm, "end": v(-25.96, 27.3) * mm});
            skLineSegment(sketch, "E654", {"start": v(-25.96, 27.3) * mm, "end": v(-26.4, 25.2) * mm});
            skLineSegment(sketch, "E655", {"start": v(-26.4, 25.2) * mm, "end": v(-26.73, 23.08) * mm});
            skLineSegment(sketch, "E656", {"start": v(-26.73, 23.08) * mm, "end": v(-26.94, 20.93) * mm});
            skLineSegment(sketch, "E657", {"start": v(-26.94, 20.93) * mm, "end": v(-27, 19.04) * mm});
            skLineSegment(sketch, "E658", {"start": v(-27, 19.04) * mm, "end": v(-26.96, 17.15) * mm});
            skLineSegment(sketch, "E659", {"start": v(-26.96, 17.15) * mm, "end": v(-26.8, 15.26) * mm});
            skLineSegment(sketch, "E660", {"start": v(-26.8, 15.26) * mm, "end": v(-26.54, 13.66) * mm});
            skLineSegment(sketch, "E661", {"start": v(-26.54, 13.66) * mm, "end": v(-26.18, 12.08) * mm});
            skLineSegment(sketch, "E662", {"start": v(-26.18, 12.08) * mm, "end": v(-25.7, 10.53) * mm});
            skLineSegment(sketch, "E663", {"start": v(-25.7, 10.53) * mm, "end": v(-25.22, 9.27) * mm});
            skLineSegment(sketch, "E664", {"start": v(-25.22, 9.27) * mm, "end": v(-24.63, 8.05) * mm});
            skLineSegment(sketch, "E665", {"start": v(-24.63, 8.05) * mm, "end": v(-23.94, 6.89) * mm});
            skLineSegment(sketch, "E666", {"start": v(-23.94, 6.89) * mm, "end": v(-23.3, 5.98) * mm});
            skLineSegment(sketch, "E667", {"start": v(-23.3, 5.98) * mm, "end": v(-22.56, 5.15) * mm});
            skLineSegment(sketch, "E668", {"start": v(-22.56, 5.15) * mm, "end": v(-21.76, 4.38) * mm});
            skLineSegment(sketch, "E669", {"start": v(-21.76, 4.38) * mm, "end": v(-21.02, 3.81) * mm});
            skLineSegment(sketch, "E670", {"start": v(-21.02, 3.81) * mm, "end": v(-20.22, 3.33) * mm});
            skLineSegment(sketch, "E671", {"start": v(-20.22, 3.33) * mm, "end": v(-19.38, 2.94) * mm});
            skLineSegment(sketch, "E672", {"start": v(-19.38, 2.94) * mm, "end": v(-18.37, 2.65) * mm});
            skLineSegment(sketch, "E673", {"start": v(-18.37, 2.65) * mm, "end": v(-17.33, 2.5) * mm});
            skLineSegment(sketch, "E674", {"start": v(-17.33, 2.5) * mm, "end": v(-16.28, 2.49) * mm});
            skLineSegment(sketch, "E675", {"start": v(-16.28, 2.49) * mm, "end": v(-15.24, 2.63) * mm});
            skLineSegment(sketch, "E676", {"start": v(-15.24, 2.63) * mm, "end": v(-14.23, 2.91) * mm});
            skLineSegment(sketch, "E677", {"start": v(-14.23, 2.91) * mm, "end": v(-13.36, 3.26) * mm});
            skLineSegment(sketch, "E678", {"start": v(-13.36, 3.26) * mm, "end": v(-12.53, 3.72) * mm});
            skLineSegment(sketch, "E679", {"start": v(-12.53, 3.72) * mm, "end": v(-11.76, 4.26) * mm});
            skLineSegment(sketch, "E680", {"start": v(-11.76, 4.26) * mm, "end": v(-10.92, 4.99) * mm});
            skLineSegment(sketch, "E681", {"start": v(-10.92, 4.99) * mm, "end": v(-10.17, 5.8) * mm});
            skLineSegment(sketch, "E682", {"start": v(-10.17, 5.8) * mm, "end": v(-9.5, 6.68) * mm});
            skLineSegment(sketch, "E683", {"start": v(-9.5, 6.68) * mm, "end": v(-8.72, 7.9) * mm});
            skLineSegment(sketch, "E684", {"start": v(-8.72, 7.9) * mm, "end": v(-8.05, 9.18) * mm});
            skLineSegment(sketch, "E685", {"start": v(-8.05, 9.18) * mm, "end": v(-7.5, 10.5) * mm});
            skLineSegment(sketch, "E686", {"start": v(-7.5, 10.5) * mm, "end": v(-6.88, 12.29) * mm});
            skLineSegment(sketch, "E687", {"start": v(-6.88, 12.29) * mm, "end": v(-6.36, 14.1) * mm});
            skLineSegment(sketch, "E688", {"start": v(-6.36, 14.1) * mm, "end": v(-5.96, 15.93) * mm});
            skLineSegment(sketch, "E689", {"start": v(-5.96, 15.93) * mm, "end": v(-5.62, 17.9) * mm});
            skLineSegment(sketch, "E690", {"start": v(-5.62, 17.9) * mm, "end": v(-5.4, 19.9) * mm});
            skLineSegment(sketch, "E691", {"start": v(-5.4, 19.9) * mm, "end": v(-5.28, 21.89) * mm});
            skLineSegment(sketch, "E692", {"start": v(-5.28, 21.89) * mm, "end": v(-5.29, 23.7) * mm});
            skLineSegment(sketch, "E693", {"start": v(-5.29, 23.7) * mm, "end": v(-5.43, 25.51) * mm});
            skLineSegment(sketch, "E694", {"start": v(-5.43, 25.51) * mm, "end": v(-5.7, 27.3) * mm});
            skLineSegment(sketch, "E695", {"start": v(-5.7, 27.3) * mm, "end": v(17.88, 27.3) * mm});
            skLineSegment(sketch, "E696", {"start": v(17.63, 29.3) * mm, "end": v(-6.16, 29.3) * mm});
            skLineSegment(sketch, "E697", {"start": v(-6.16, 29.3) * mm, "end": v(-6.75, 31.08) * mm});
            skLineSegment(sketch, "E698", {"start": v(-6.75, 31.08) * mm, "end": v(-7.52, 32.79) * mm});
            skLineSegment(sketch, "E699", {"start": v(-7.52, 32.79) * mm, "end": v(-8.34, 34.21) * mm});
            skLineSegment(sketch, "E700", {"start": v(-8.34, 34.21) * mm, "end": v(-9.32, 35.53) * mm});
            skLineSegment(sketch, "E701", {"start": v(-9.32, 35.53) * mm, "end": v(-10.25, 36.53) * mm});
            skLineSegment(sketch, "E702", {"start": v(-10.25, 36.53) * mm, "end": v(-11.3, 37.38) * mm});
            skLineSegment(sketch, "E703", {"start": v(-11.3, 37.38) * mm, "end": v(-12.47, 38.1) * mm});
            skLineSegment(sketch, "E704", {"start": v(-12.47, 38.1) * mm, "end": v(-13.49, 38.5) * mm});
            skLineSegment(sketch, "E705", {"start": v(-13.49, 38.5) * mm, "end": v(-14.56, 38.77) * mm});
            skLineSegment(sketch, "E706", {"start": v(-14.56, 38.77) * mm, "end": v(-15.66, 38.85) * mm});
            skLineSegment(sketch, "E707", {"start": v(-15.66, 38.85) * mm, "end": v(-16.83, 38.76) * mm});
            skLineSegment(sketch, "E708", {"start": v(-16.83, 38.76) * mm, "end": v(-17.98, 38.5) * mm});
            skLineSegment(sketch, "E709", {"start": v(-17.98, 38.5) * mm, "end": v(-19.07, 38.07) * mm});
            skLineSegment(sketch, "E710", {"start": v(-19.07, 38.07) * mm, "end": v(-20.1, 37.48) * mm});
            skLineSegment(sketch, "E711", {"start": v(-20.1, 37.48) * mm, "end": v(-21.17, 36.65) * mm});
            skLineSegment(sketch, "E712", {"start": v(-21.17, 36.65) * mm, "end": v(-22.12, 35.67) * mm});
            skLineSegment(sketch, "E713", {"start": v(-22.12, 35.67) * mm, "end": v(-23.11, 34.38) * mm});
            skLineSegment(sketch, "E714", {"start": v(-23.11, 34.38) * mm, "end": v(-23.95, 32.97) * mm});
            skLineSegment(sketch, "E715", {"start": v(-23.95, 32.97) * mm, "end": v(-24.77, 31.17) * mm});
            skLineSegment(sketch, "E716", {"start": v(-24.77, 31.17) * mm, "end": v(-25.42, 29.3) * mm});
            skLineSegment(sketch, "E717", {"start": v(-25.42, 29.3) * mm, "end": v(-45.74, 29.3) * mm});
            skLineSegment(sketch, "E718", {"start": v(-45.74, 29.3) * mm, "end": v(-44.3, 31.26) * mm});
            skLineSegment(sketch, "E719", {"start": v(-44.3, 31.26) * mm, "end": v(-42.73, 33.11) * mm});
            skLineSegment(sketch, "E720", {"start": v(-42.73, 33.11) * mm, "end": v(-41.03, 34.85) * mm});
            skLineSegment(sketch, "E721", {"start": v(-41.03, 34.85) * mm, "end": v(-39.2, 36.45) * mm});
            skLineSegment(sketch, "E722", {"start": v(-39.2, 36.45) * mm, "end": v(-37.08, 38.07) * mm});
            skLineSegment(sketch, "E723", {"start": v(-37.08, 38.07) * mm, "end": v(-34.86, 39.55) * mm});
            skLineSegment(sketch, "E724", {"start": v(-34.86, 39.55) * mm, "end": v(-32.54, 40.87) * mm});
            skLineSegment(sketch, "E725", {"start": v(-32.54, 40.87) * mm, "end": v(-30.14, 42.04) * mm});
            skLineSegment(sketch, "E726", {"start": v(-30.14, 42.04) * mm, "end": v(-27.43, 43.15) * mm});
            skLineSegment(sketch, "E727", {"start": v(-27.43, 43.15) * mm, "end": v(-24.67, 44.09) * mm});
            skLineSegment(sketch, "E728", {"start": v(-24.67, 44.09) * mm, "end": v(-21.85, 44.86) * mm});
            skLineSegment(sketch, "E729", {"start": v(-21.85, 44.86) * mm, "end": v(-19, 45.47) * mm});
            skLineSegment(sketch, "E730", {"start": v(-19, 45.47) * mm, "end": v(-16.09, 45.92) * mm});
            skLineSegment(sketch, "E731", {"start": v(-16.09, 45.92) * mm, "end": v(-13.16, 46.21) * mm});
            skLineSegment(sketch, "E732", {"start": v(-13.16, 46.21) * mm, "end": v(-10.21, 46.33) * mm});
            skLineSegment(sketch, "E733", {"start": v(-10.21, 46.33) * mm, "end": v(-7.27, 46.29) * mm});
            skLineSegment(sketch, "E734", {"start": v(-7.27, 46.29) * mm, "end": v(-4.72, 46.09) * mm});
            skLineSegment(sketch, "E735", {"start": v(-4.72, 46.09) * mm, "end": v(-2.2, 45.71) * mm});
            skLineSegment(sketch, "E736", {"start": v(-2.2, 45.71) * mm, "end": v(0.3, 45.17) * mm});
            skLineSegment(sketch, "E737", {"start": v(0.3, 45.17) * mm, "end": v(2.76, 44.46) * mm});
            skLineSegment(sketch, "E738", {"start": v(2.76, 44.46) * mm, "end": v(4.75, 43.73) * mm});
            skLineSegment(sketch, "E739", {"start": v(4.75, 43.73) * mm, "end": v(6.68, 42.84) * mm});
            skLineSegment(sketch, "E740", {"start": v(6.68, 42.84) * mm, "end": v(8.54, 41.8) * mm});
            skLineSegment(sketch, "E741", {"start": v(8.54, 41.8) * mm, "end": v(10.3, 40.63) * mm});
            skLineSegment(sketch, "E742", {"start": v(10.3, 40.63) * mm, "end": v(11.7, 39.5) * mm});
            skLineSegment(sketch, "E743", {"start": v(11.7, 39.5) * mm, "end": v(13, 38.26) * mm});
            skLineSegment(sketch, "E744", {"start": v(13, 38.26) * mm, "end": v(14.17, 36.9) * mm});
            skLineSegment(sketch, "E745", {"start": v(14.17, 36.9) * mm, "end": v(15.21, 35.44) * mm});
            skLineSegment(sketch, "E746", {"start": v(15.21, 35.44) * mm, "end": v(16.04, 34) * mm});
            skLineSegment(sketch, "E747", {"start": v(16.04, 34) * mm, "end": v(16.72, 32.49) * mm});
            skLineSegment(sketch, "E748", {"start": v(16.72, 32.49) * mm, "end": v(17.25, 30.92) * mm});
            skLineSegment(sketch, "E749", {"start": v(17.25, 30.92) * mm, "end": v(17.63, 29.3) * mm});
            skLineSegment(sketch, "E750", {"start": v(-67.79, 27.3) * mm, "end": v(-65.38, 26.15) * mm});
            skLineSegment(sketch, "E751", {"start": v(-65.38, 26.15) * mm, "end": v(-63.03, 24.86) * mm});
            skLineSegment(sketch, "E752", {"start": v(-63.03, 24.86) * mm, "end": v(-60.76, 23.45) * mm});
            skLineSegment(sketch, "E753", {"start": v(-60.76, 23.45) * mm, "end": v(-59.5, 22.54) * mm});
            skLineSegment(sketch, "E754", {"start": v(-59.5, 22.54) * mm, "end": v(-58.35, 21.5) * mm});
            skLineSegment(sketch, "E755", {"start": v(-58.35, 21.5) * mm, "end": v(-57.32, 20.33) * mm});
            skLineSegment(sketch, "E756", {"start": v(-57.32, 20.33) * mm, "end": v(-56.72, 19.46) * mm});
            skLineSegment(sketch, "E757", {"start": v(-56.72, 19.46) * mm, "end": v(-56.23, 18.53) * mm});
            skLineSegment(sketch, "E758", {"start": v(-56.23, 18.53) * mm, "end": v(-55.86, 17.53) * mm});
            skLineSegment(sketch, "E759", {"start": v(-55.86, 17.53) * mm, "end": v(-55.63, 16.5) * mm});
            skLineSegment(sketch, "E760", {"start": v(-55.63, 16.5) * mm, "end": v(-55.54, 15.44) * mm});
            skLineSegment(sketch, "E761", {"start": v(-55.54, 15.44) * mm, "end": v(-55.59, 14.37) * mm});
            skLineSegment(sketch, "E762", {"start": v(-55.59, 14.37) * mm, "end": v(-55.87, 12.71) * mm});
            skLineSegment(sketch, "E763", {"start": v(-55.87, 12.71) * mm, "end": v(-56.34, 11.1) * mm});
            skLineSegment(sketch, "E764", {"start": v(-56.34, 11.1) * mm, "end": v(-56.98, 9.54) * mm});
            skLineSegment(sketch, "E765", {"start": v(-56.98, 9.54) * mm, "end": v(-57.8, 8.06) * mm});
            skLineSegment(sketch, "E766", {"start": v(-57.8, 8.06) * mm, "end": v(-58.77, 6.69) * mm});
            skLineSegment(sketch, "E767", {"start": v(-58.77, 6.69) * mm, "end": v(-59.93, 5.3) * mm});
            skLineSegment(sketch, "E768", {"start": v(-59.93, 5.3) * mm, "end": v(-61.19, 4.01) * mm});
            skLineSegment(sketch, "E769", {"start": v(-61.19, 4.01) * mm, "end": v(-62.54, 2.82) * mm});
            skLineSegment(sketch, "E770", {"start": v(-62.54, 2.82) * mm, "end": v(-64.22, 1.55) * mm});
            skLineSegment(sketch, "E771", {"start": v(-64.22, 1.55) * mm, "end": v(-65.97, 0.4) * mm});
            skLineSegment(sketch, "E772", {"start": v(-65.97, 0.4) * mm, "end": v(-67.8, -0.63) * mm});
            skLineSegment(sketch, "E773", {"start": v(-67.8, -0.63) * mm, "end": v(-69.94, -1.64) * mm});
            skLineSegment(sketch, "E774", {"start": v(-69.94, -1.64) * mm, "end": v(-72.13, -2.52) * mm});
            skLineSegment(sketch, "E775", {"start": v(-72.13, -2.52) * mm, "end": v(-74.37, -3.27) * mm});
            skLineSegment(sketch, "E776", {"start": v(-74.37, -3.27) * mm, "end": v(-76.82, -3.9) * mm});
            skLineSegment(sketch, "E777", {"start": v(-76.82, -3.9) * mm, "end": v(-79.3, -4.4) * mm});
            skLineSegment(sketch, "E778", {"start": v(-79.3, -4.4) * mm, "end": v(-81.8, -4.75) * mm});
            skLineSegment(sketch, "E779", {"start": v(-81.8, -4.75) * mm, "end": v(-84.35, -4.96) * mm});
            skLineSegment(sketch, "E780", {"start": v(-84.35, -4.96) * mm, "end": v(-86.9, -5.01) * mm});
            skLineSegment(sketch, "E781", {"start": v(-86.9, -5.01) * mm, "end": v(-89.46, -4.91) * mm});
            skLineSegment(sketch, "E782", {"start": v(-89.46, -4.91) * mm, "end": v(-91.87, -4.68) * mm});
            skLineSegment(sketch, "E783", {"start": v(-91.87, -4.68) * mm, "end": v(-94.26, -4.3) * mm});
            skLineSegment(sketch, "E784", {"start": v(-94.26, -4.3) * mm, "end": v(-96.63, -3.77) * mm});
            skLineSegment(sketch, "E785", {"start": v(-96.63, -3.77) * mm, "end": v(-98.78, -3.13) * mm});
            skLineSegment(sketch, "E786", {"start": v(-98.78, -3.13) * mm, "end": v(-100.89, -2.35) * mm});
            skLineSegment(sketch, "E787", {"start": v(-100.89, -2.35) * mm, "end": v(-102.93, -1.43) * mm});
            skLineSegment(sketch, "E788", {"start": v(-102.93, -1.43) * mm, "end": v(-104.85, -0.4) * mm});
            skLineSegment(sketch, "E789", {"start": v(-104.85, -0.4) * mm, "end": v(-106.7, 0.76) * mm});
            skLineSegment(sketch, "E790", {"start": v(-106.7, 0.76) * mm, "end": v(-108.45, 2.04) * mm});
            skLineSegment(sketch, "E791", {"start": v(-108.45, 2.04) * mm, "end": v(-95.53, 14.53) * mm});
            skLineSegment(sketch, "E792", {"start": v(-95.53, 14.53) * mm, "end": v(-93.4, 12.21) * mm});
            skLineSegment(sketch, "E793", {"start": v(-93.4, 12.21) * mm, "end": v(-91.16, 9.98) * mm});
            skLineSegment(sketch, "E794", {"start": v(-91.16, 9.98) * mm, "end": v(-89.3, 8.3) * mm});
            skLineSegment(sketch, "E795", {"start": v(-89.3, 8.3) * mm, "end": v(-87.35, 6.72) * mm});
            skLineSegment(sketch, "E796", {"start": v(-87.35, 6.72) * mm, "end": v(-85.8, 5.63) * mm});
            skLineSegment(sketch, "E797", {"start": v(-85.8, 5.63) * mm, "end": v(-84.18, 4.65) * mm});
            skLineSegment(sketch, "E798", {"start": v(-84.18, 4.65) * mm, "end": v(-82.9, 4) * mm});
            skLineSegment(sketch, "E799", {"start": v(-82.9, 4) * mm, "end": v(-81.57, 3.48) * mm});
            skLineSegment(sketch, "E800", {"start": v(-81.57, 3.48) * mm, "end": v(-80.47, 3.17) * mm});
            skLineSegment(sketch, "E801", {"start": v(-80.47, 3.17) * mm, "end": v(-79.34, 2.97) * mm});
            skLineSegment(sketch, "E802", {"start": v(-79.34, 2.97) * mm, "end": v(-78.36, 2.91) * mm});
            skLineSegment(sketch, "E803", {"start": v(-78.36, 2.91) * mm, "end": v(-77.38, 2.96) * mm});
            skLineSegment(sketch, "E804", {"start": v(-77.38, 2.96) * mm, "end": v(-76.58, 3.1) * mm});
            skLineSegment(sketch, "E805", {"start": v(-76.58, 3.1) * mm, "end": v(-75.8, 3.34) * mm});
            skLineSegment(sketch, "E806", {"start": v(-75.8, 3.34) * mm, "end": v(-75.2, 3.61) * mm});
            skLineSegment(sketch, "E807", {"start": v(-75.2, 3.61) * mm, "end": v(-74.67, 3.98) * mm});
            skLineSegment(sketch, "E808", {"start": v(-74.67, 3.98) * mm, "end": v(-74.2, 4.46) * mm});
            skLineSegment(sketch, "E809", {"start": v(-74.2, 4.46) * mm, "end": v(-73.82, 5.01) * mm});
            skLineSegment(sketch, "E810", {"start": v(-73.82, 5.01) * mm, "end": v(-73.56, 5.63) * mm});
            skLineSegment(sketch, "E811", {"start": v(-73.56, 5.63) * mm, "end": v(-73.44, 6.29) * mm});
            skLineSegment(sketch, "E812", {"start": v(-73.44, 6.29) * mm, "end": v(-73.44, 6.96) * mm});
            skLineSegment(sketch, "E813", {"start": v(-73.44, 6.96) * mm, "end": v(-73.6, 7.46) * mm});
            skLineSegment(sketch, "E814", {"start": v(-73.6, 7.46) * mm, "end": v(-73.84, 7.91) * mm});
            skLineSegment(sketch, "E815", {"start": v(-73.84, 7.91) * mm, "end": v(-74.32, 8.51) * mm});
            skLineSegment(sketch, "E816", {"start": v(-74.32, 8.51) * mm, "end": v(-74.9, 9.03) * mm});
            skLineSegment(sketch, "E817", {"start": v(-74.9, 9.03) * mm, "end": v(-76.32, 10.02) * mm});
            skLineSegment(sketch, "E818", {"start": v(-76.32, 10.02) * mm, "end": v(-77.84, 10.87) * mm});
            skLineSegment(sketch, "E819", {"start": v(-77.84, 10.87) * mm, "end": v(-80.68, 12.35) * mm});
            skLineSegment(sketch, "E820", {"start": v(-80.68, 12.35) * mm, "end": v(-83.55, 13.78) * mm});
            skLineSegment(sketch, "E821", {"start": v(-83.55, 13.78) * mm, "end": v(-87.04, 15.53) * mm});
            skLineSegment(sketch, "E822", {"start": v(-87.04, 15.53) * mm, "end": v(-89.23, 16.71) * mm});
            skLineSegment(sketch, "E823", {"start": v(-89.23, 16.71) * mm, "end": v(-91.39, 17.95) * mm});
            skLineSegment(sketch, "E824", {"start": v(-91.39, 17.95) * mm, "end": v(-92.72, 18.83) * mm});
            skLineSegment(sketch, "E825", {"start": v(-92.72, 18.83) * mm, "end": v(-93.96, 19.84) * mm});
            skLineSegment(sketch, "E826", {"start": v(-93.96, 19.84) * mm, "end": v(-94.7, 20.59) * mm});
            skLineSegment(sketch, "E827", {"start": v(-94.7, 20.59) * mm, "end": v(-95.35, 21.41) * mm});
            skLineSegment(sketch, "E828", {"start": v(-95.35, 21.41) * mm, "end": v(-95.9, 22.3) * mm});
            skLineSegment(sketch, "E829", {"start": v(-95.9, 22.3) * mm, "end": v(-96.36, 23.25) * mm});
            skLineSegment(sketch, "E830", {"start": v(-96.36, 23.25) * mm, "end": v(-96.67, 24.23) * mm});
            skLineSegment(sketch, "E831", {"start": v(-96.67, 24.23) * mm, "end": v(-96.86, 25.25) * mm});
            skLineSegment(sketch, "E832", {"start": v(-96.86, 25.25) * mm, "end": v(-96.94, 26.28) * mm});
            skLineSegment(sketch, "E833", {"start": v(-96.94, 26.28) * mm, "end": v(-96.9, 27.3) * mm});
            skLineSegment(sketch, "E834", {"start": v(-96.9, 27.3) * mm, "end": v(-67.79, 27.3) * mm});
            skLineSegment(sketch, "E835", {"start": v(-72.07, 29.3) * mm, "end": v(-96.6, 29.3) * mm});
            skLineSegment(sketch, "E836", {"start": v(-96.6, 29.3) * mm, "end": v(-96.23, 30.73) * mm});
            skLineSegment(sketch, "E837", {"start": v(-96.23, 30.73) * mm, "end": v(-95.74, 32.12) * mm});
            skLineSegment(sketch, "E838", {"start": v(-95.74, 32.12) * mm, "end": v(-95.13, 33.47) * mm});
            skLineSegment(sketch, "E839", {"start": v(-95.13, 33.47) * mm, "end": v(-94.4, 34.75) * mm});
            skLineSegment(sketch, "E840", {"start": v(-94.4, 34.75) * mm, "end": v(-93.5, 36.1) * mm});
            skLineSegment(sketch, "E841", {"start": v(-93.5, 36.1) * mm, "end": v(-92.48, 37.35) * mm});
            skLineSegment(sketch, "E842", {"start": v(-92.48, 37.35) * mm, "end": v(-91.38, 38.53) * mm});
            skLineSegment(sketch, "E843", {"start": v(-91.38, 38.53) * mm, "end": v(-90.18, 39.61) * mm});
            skLineSegment(sketch, "E844", {"start": v(-90.18, 39.61) * mm, "end": v(-88.74, 40.73) * mm});
            skLineSegment(sketch, "E845", {"start": v(-88.74, 40.73) * mm, "end": v(-87.23, 41.74) * mm});
            skLineSegment(sketch, "E846", {"start": v(-87.23, 41.74) * mm, "end": v(-85.64, 42.65) * mm});
            skLineSegment(sketch, "E847", {"start": v(-85.64, 42.65) * mm, "end": v(-84, 43.43) * mm});
            skLineSegment(sketch, "E848", {"start": v(-84, 43.43) * mm, "end": v(-82.07, 44.2) * mm});
            skLineSegment(sketch, "E849", {"start": v(-82.07, 44.2) * mm, "end": v(-80.09, 44.85) * mm});
            skLineSegment(sketch, "E850", {"start": v(-80.09, 44.85) * mm, "end": v(-78.08, 45.37) * mm});
            skLineSegment(sketch, "E851", {"start": v(-78.08, 45.37) * mm, "end": v(-76.03, 45.75) * mm});
            skLineSegment(sketch, "E852", {"start": v(-76.03, 45.75) * mm, "end": v(-73.77, 46.04) * mm});
            skLineSegment(sketch, "E853", {"start": v(-73.77, 46.04) * mm, "end": v(-71.5, 46.2) * mm});
            skLineSegment(sketch, "E854", {"start": v(-71.5, 46.2) * mm, "end": v(-69.23, 46.24) * mm});
            skLineSegment(sketch, "E855", {"start": v(-69.23, 46.24) * mm, "end": v(-66.95, 46.14) * mm});
            skLineSegment(sketch, "E856", {"start": v(-66.95, 46.14) * mm, "end": v(-64.77, 45.93) * mm});
            skLineSegment(sketch, "E857", {"start": v(-64.77, 45.93) * mm, "end": v(-62.6, 45.59) * mm});
            skLineSegment(sketch, "E858", {"start": v(-62.6, 45.59) * mm, "end": v(-60.46, 45.1) * mm});
            skLineSegment(sketch, "E859", {"start": v(-60.46, 45.1) * mm, "end": v(-58.36, 44.5) * mm});
            skLineSegment(sketch, "E860", {"start": v(-58.36, 44.5) * mm, "end": v(-56.38, 43.76) * mm});
            skLineSegment(sketch, "E861", {"start": v(-56.38, 43.76) * mm, "end": v(-54.45, 42.9) * mm});
            skLineSegment(sketch, "E862", {"start": v(-54.45, 42.9) * mm, "end": v(-52.58, 41.92) * mm});
            skLineSegment(sketch, "E863", {"start": v(-52.58, 41.92) * mm, "end": v(-50.79, 40.8) * mm});
            skLineSegment(sketch, "E864", {"start": v(-50.79, 40.8) * mm, "end": v(-62.3, 29.52) * mm});
            skLineSegment(sketch, "E865", {"start": v(-62.3, 29.52) * mm, "end": v(-63.8, 31.32) * mm});
            skLineSegment(sketch, "E866", {"start": v(-63.8, 31.32) * mm, "end": v(-65.36, 33.05) * mm});
            skLineSegment(sketch, "E867", {"start": v(-65.36, 33.05) * mm, "end": v(-66.71, 34.4) * mm});
            skLineSegment(sketch, "E868", {"start": v(-66.71, 34.4) * mm, "end": v(-68.14, 35.65) * mm});
            skLineSegment(sketch, "E869", {"start": v(-68.14, 35.65) * mm, "end": v(-69.3, 36.55) * mm});
            skLineSegment(sketch, "E870", {"start": v(-69.3, 36.55) * mm, "end": v(-70.54, 37.36) * mm});
            skLineSegment(sketch, "E871", {"start": v(-70.54, 37.36) * mm, "end": v(-71.58, 37.93) * mm});
            skLineSegment(sketch, "E872", {"start": v(-71.58, 37.93) * mm, "end": v(-72.66, 38.4) * mm});
            skLineSegment(sketch, "E873", {"start": v(-72.66, 38.4) * mm, "end": v(-73.62, 38.72) * mm});
            skLineSegment(sketch, "E874", {"start": v(-73.62, 38.72) * mm, "end": v(-74.6, 38.94) * mm});
            skLineSegment(sketch, "E875", {"start": v(-74.6, 38.94) * mm, "end": v(-75.46, 39.05) * mm});
            skLineSegment(sketch, "E876", {"start": v(-75.46, 39.05) * mm, "end": v(-76.34, 39.07) * mm});
            skLineSegment(sketch, "E877", {"start": v(-76.34, 39.07) * mm, "end": v(-77.08, 39) * mm});
            skLineSegment(sketch, "E878", {"start": v(-77.08, 39) * mm, "end": v(-77.8, 38.84) * mm});
            skLineSegment(sketch, "E879", {"start": v(-77.8, 38.84) * mm, "end": v(-78.39, 38.63) * mm});
            skLineSegment(sketch, "E880", {"start": v(-78.39, 38.63) * mm, "end": v(-78.94, 38.35) * mm});
            skLineSegment(sketch, "E881", {"start": v(-78.94, 38.35) * mm, "end": v(-79.38, 38.03) * mm});
            skLineSegment(sketch, "E882", {"start": v(-79.38, 38.03) * mm, "end": v(-79.76, 37.66) * mm});
            skLineSegment(sketch, "E883", {"start": v(-79.76, 37.66) * mm, "end": v(-80.17, 37.04) * mm});
            skLineSegment(sketch, "E884", {"start": v(-80.17, 37.04) * mm, "end": v(-80.42, 36.35) * mm});
            skLineSegment(sketch, "E885", {"start": v(-80.42, 36.35) * mm, "end": v(-80.5, 35.61) * mm});
            skLineSegment(sketch, "E886", {"start": v(-80.5, 35.61) * mm, "end": v(-80.42, 34.88) * mm});
            skLineSegment(sketch, "E887", {"start": v(-80.42, 34.88) * mm, "end": v(-80.22, 34.4) * mm});
            skLineSegment(sketch, "E888", {"start": v(-80.22, 34.4) * mm, "end": v(-79.95, 33.98) * mm});
            skLineSegment(sketch, "E889", {"start": v(-79.95, 33.98) * mm, "end": v(-79.48, 33.43) * mm});
            skLineSegment(sketch, "E890", {"start": v(-79.48, 33.43) * mm, "end": v(-78.95, 32.96) * mm});
            skLineSegment(sketch, "E891", {"start": v(-78.95, 32.96) * mm, "end": v(-77.89, 32.2) * mm});
            skLineSegment(sketch, "E892", {"start": v(-77.89, 32.2) * mm, "end": v(-76.76, 31.57) * mm});
            skLineSegment(sketch, "E893", {"start": v(-76.76, 31.57) * mm, "end": v(-73.22, 29.83) * mm});
            skLineSegment(sketch, "E894", {"start": v(-73.22, 29.83) * mm, "end": v(-72.07, 29.3) * mm});
            skLineSegment(sketch, "E895", {"start": v(141.16, 27.3) * mm, "end": v(162.38, 27.3) * mm});
            skLineSegment(sketch, "E896", {"start": v(162.38, 27.3) * mm, "end": v(159.99, 17.35) * mm});
            skLineSegment(sketch, "E897", {"start": v(159.99, 17.35) * mm, "end": v(174.21, 24.74) * mm});
            skLineSegment(sketch, "E898", {"start": v(174.21, 24.74) * mm, "end": v(175.73, 24.74) * mm});
            skLineSegment(sketch, "E899", {"start": v(175.73, 24.74) * mm, "end": v(178.34, 21.05) * mm});
            skLineSegment(sketch, "E900", {"start": v(178.34, 21.05) * mm, "end": v(179.45, 21.9) * mm});
            skLineSegment(sketch, "E901", {"start": v(179.45, 21.9) * mm, "end": v(180.43, 22.88) * mm});
            skLineSegment(sketch, "E902", {"start": v(180.43, 22.88) * mm, "end": v(181.17, 23.86) * mm});
            skLineSegment(sketch, "E903", {"start": v(181.17, 23.86) * mm, "end": v(181.75, 24.94) * mm});
            skLineSegment(sketch, "E904", {"start": v(181.75, 24.94) * mm, "end": v(182.15, 26.1) * mm});
            skLineSegment(sketch, "E905", {"start": v(182.15, 26.1) * mm, "end": v(182.38, 27.3) * mm});
            skLineSegment(sketch, "E906", {"start": v(182.38, 27.3) * mm, "end": v(199.4, 27.3) * mm});
            skLineSegment(sketch, "E907", {"start": v(199.4, 27.3) * mm, "end": v(198.17, 25.81) * mm});
            skLineSegment(sketch, "E908", {"start": v(198.17, 25.81) * mm, "end": v(196.8, 24.44) * mm});
            skLineSegment(sketch, "E909", {"start": v(196.8, 24.44) * mm, "end": v(195.3, 23.21) * mm});
            skLineSegment(sketch, "E910", {"start": v(195.3, 23.21) * mm, "end": v(193.34, 21.89) * mm});
            skLineSegment(sketch, "E911", {"start": v(193.34, 21.89) * mm, "end": v(191.3, 20.72) * mm});
            skLineSegment(sketch, "E912", {"start": v(191.3, 20.72) * mm, "end": v(189.16, 19.72) * mm});
            skLineSegment(sketch, "E913", {"start": v(189.16, 19.72) * mm, "end": v(186.48, 18.69) * mm});
            skLineSegment(sketch, "E914", {"start": v(186.48, 18.69) * mm, "end": v(183.73, 17.82) * mm});
            skLineSegment(sketch, "E915", {"start": v(183.73, 17.82) * mm, "end": v(180.95, 17.14) * mm});
            skLineSegment(sketch, "E916", {"start": v(180.95, 17.14) * mm, "end": v(191.37, 2.91) * mm});
            skLineSegment(sketch, "E917", {"start": v(191.37, 2.91) * mm, "end": v(196.57, 2.91) * mm});
            skLineSegment(sketch, "E918", {"start": v(196.57, 2.91) * mm, "end": v(195.16, -3.28) * mm});
            skLineSegment(sketch, "E919", {"start": v(195.16, -3.28) * mm, "end": v(170.41, -3.28) * mm});
            skLineSegment(sketch, "E920", {"start": v(170.41, -3.28) * mm, "end": v(159.44, 14.96) * mm});
            skLineSegment(sketch, "E921", {"start": v(159.44, 14.96) * mm, "end": v(156.51, 2.8) * mm});
            skLineSegment(sketch, "E922", {"start": v(156.51, 2.8) * mm, "end": v(160.64, 2.8) * mm});
            skLineSegment(sketch, "E923", {"start": v(160.64, 2.8) * mm, "end": v(159.12, -3.28) * mm});
            skLineSegment(sketch, "E924", {"start": v(159.12, -3.28) * mm, "end": v(129.58, -3.28) * mm});
            skLineSegment(sketch, "E925", {"start": v(129.58, -3.28) * mm, "end": v(131.1, 2.8) * mm});
            skLineSegment(sketch, "E926", {"start": v(131.1, 2.8) * mm, "end": v(135.34, 2.8) * mm});
            skLineSegment(sketch, "E927", {"start": v(135.34, 2.8) * mm, "end": v(141.16, 27.3) * mm});
            skLineSegment(sketch, "E928", {"start": v(141.64, 29.3) * mm, "end": v(146.96, 51.67) * mm});
            skLineSegment(sketch, "E929", {"start": v(146.96, 51.67) * mm, "end": v(142.5, 50.58) * mm});
            skLineSegment(sketch, "E930", {"start": v(142.5, 50.58) * mm, "end": v(144.02, 56.77) * mm});
            skLineSegment(sketch, "E931", {"start": v(144.02, 56.77) * mm, "end": v(175.84, 64.7) * mm});
            skLineSegment(sketch, "E932", {"start": v(175.84, 64.7) * mm, "end": v(174.32, 58.5) * mm});
            skLineSegment(sketch, "E933", {"start": v(174.32, 58.5) * mm, "end": v(169.54, 57.32) * mm});
            skLineSegment(sketch, "E934", {"start": v(169.54, 57.32) * mm, "end": v(165.1, 38.53) * mm});
            skLineSegment(sketch, "E935", {"start": v(165.1, 38.53) * mm, "end": v(167.83, 40.12) * mm});
            skLineSegment(sketch, "E936", {"start": v(167.83, 40.12) * mm, "end": v(170.62, 41.6) * mm});
            skLineSegment(sketch, "E937", {"start": v(170.62, 41.6) * mm, "end": v(173.47, 42.99) * mm});
            skLineSegment(sketch, "E938", {"start": v(173.47, 42.99) * mm, "end": v(175.66, 43.94) * mm});
            skLineSegment(sketch, "E939", {"start": v(175.66, 43.94) * mm, "end": v(177.9, 44.78) * mm});
            skLineSegment(sketch, "E940", {"start": v(177.9, 44.78) * mm, "end": v(180.2, 45.49) * mm});
            skLineSegment(sketch, "E941", {"start": v(180.2, 45.49) * mm, "end": v(182.05, 45.94) * mm});
            skLineSegment(sketch, "E942", {"start": v(182.05, 45.94) * mm, "end": v(183.92, 46.27) * mm});
            skLineSegment(sketch, "E943", {"start": v(183.92, 46.27) * mm, "end": v(185.82, 46.49) * mm});
            skLineSegment(sketch, "E944", {"start": v(185.82, 46.49) * mm, "end": v(187.44, 46.56) * mm});
            skLineSegment(sketch, "E945", {"start": v(187.44, 46.56) * mm, "end": v(189.07, 46.53) * mm});
            skLineSegment(sketch, "E946", {"start": v(189.07, 46.53) * mm, "end": v(190.7, 46.38) * mm});
            skLineSegment(sketch, "E947", {"start": v(190.7, 46.38) * mm, "end": v(192.07, 46.16) * mm});
            skLineSegment(sketch, "E948", {"start": v(192.07, 46.16) * mm, "end": v(193.43, 45.83) * mm});
            skLineSegment(sketch, "E949", {"start": v(193.43, 45.83) * mm, "end": v(194.75, 45.39) * mm});
            skLineSegment(sketch, "E950", {"start": v(194.75, 45.39) * mm, "end": v(195.86, 44.92) * mm});
            skLineSegment(sketch, "E951", {"start": v(195.86, 44.92) * mm, "end": v(196.91, 44.36) * mm});
            skLineSegment(sketch, "E952", {"start": v(196.91, 44.36) * mm, "end": v(197.92, 43.7) * mm});
            skLineSegment(sketch, "E953", {"start": v(197.92, 43.7) * mm, "end": v(198.75, 43.05) * mm});
            skLineSegment(sketch, "E954", {"start": v(198.75, 43.05) * mm, "end": v(199.51, 42.31) * mm});
            skLineSegment(sketch, "E955", {"start": v(199.51, 42.31) * mm, "end": v(200.2, 41.5) * mm});
            skLineSegment(sketch, "E956", {"start": v(200.2, 41.5) * mm, "end": v(200.77, 40.69) * mm});
            skLineSegment(sketch, "E957", {"start": v(200.77, 40.69) * mm, "end": v(201.25, 39.82) * mm});
            skLineSegment(sketch, "E958", {"start": v(201.25, 39.82) * mm, "end": v(201.64, 38.9) * mm});
            skLineSegment(sketch, "E959", {"start": v(201.64, 38.9) * mm, "end": v(201.94, 37.94) * mm});
            skLineSegment(sketch, "E960", {"start": v(201.94, 37.94) * mm, "end": v(202.13, 36.95) * mm});
            skLineSegment(sketch, "E961", {"start": v(202.13, 36.95) * mm, "end": v(202.23, 35.95) * mm});
            skLineSegment(sketch, "E962", {"start": v(202.23, 35.95) * mm, "end": v(202.22, 34.85) * mm});
            skLineSegment(sketch, "E963", {"start": v(202.22, 34.85) * mm, "end": v(202.12, 33.76) * mm});
            skLineSegment(sketch, "E964", {"start": v(202.12, 33.76) * mm, "end": v(201.91, 32.68) * mm});
            skLineSegment(sketch, "E965", {"start": v(201.91, 32.68) * mm, "end": v(201.58, 31.52) * mm});
            skLineSegment(sketch, "E966", {"start": v(201.58, 31.52) * mm, "end": v(201.16, 30.4) * mm});
            skLineSegment(sketch, "E967", {"start": v(201.16, 30.4) * mm, "end": v(200.64, 29.3) * mm});
            skLineSegment(sketch, "E968", {"start": v(200.64, 29.3) * mm, "end": v(182.26, 29.3) * mm});
            skLineSegment(sketch, "E969", {"start": v(182.26, 29.3) * mm, "end": v(181.94, 30.3) * mm});
            skLineSegment(sketch, "E970", {"start": v(181.94, 30.3) * mm, "end": v(181.44, 31.2) * mm});
            skLineSegment(sketch, "E971", {"start": v(181.44, 31.2) * mm, "end": v(180.74, 32.08) * mm});
            skLineSegment(sketch, "E972", {"start": v(180.74, 32.08) * mm, "end": v(179.9, 32.82) * mm});
            skLineSegment(sketch, "E973", {"start": v(179.9, 32.82) * mm, "end": v(178.8, 33.52) * mm});
            skLineSegment(sketch, "E974", {"start": v(178.8, 33.52) * mm, "end": v(177.62, 34.03) * mm});
            skLineSegment(sketch, "E975", {"start": v(177.62, 34.03) * mm, "end": v(176.61, 34.33) * mm});
            skLineSegment(sketch, "E976", {"start": v(176.61, 34.33) * mm, "end": v(175.59, 34.55) * mm});
            skLineSegment(sketch, "E977", {"start": v(175.59, 34.55) * mm, "end": v(174.55, 34.67) * mm});
            skLineSegment(sketch, "E978", {"start": v(174.55, 34.67) * mm, "end": v(173.02, 34.72) * mm});
            skLineSegment(sketch, "E979", {"start": v(173.02, 34.72) * mm, "end": v(171.5, 34.63) * mm});
            skLineSegment(sketch, "E980", {"start": v(171.5, 34.63) * mm, "end": v(170, 34.42) * mm});
            skLineSegment(sketch, "E981", {"start": v(170, 34.42) * mm, "end": v(168.5, 34.07) * mm});
            skLineSegment(sketch, "E982", {"start": v(168.5, 34.07) * mm, "end": v(167.06, 33.6) * mm});
            skLineSegment(sketch, "E983", {"start": v(167.06, 33.6) * mm, "end": v(165.82, 33.08) * mm});
            skLineSegment(sketch, "E984", {"start": v(165.82, 33.08) * mm, "end": v(164.62, 32.48) * mm});
            skLineSegment(sketch, "E985", {"start": v(164.62, 32.48) * mm, "end": v(163.46, 31.8) * mm});
            skLineSegment(sketch, "E986", {"start": v(163.46, 31.8) * mm, "end": v(162.86, 29.3) * mm});
            skLineSegment(sketch, "E987", {"start": v(162.86, 29.3) * mm, "end": v(141.64, 29.3) * mm});
            skLineSegment(sketch, "E988", {"start": v(118.45, 27.3) * mm, "end": v(122.74, 4.21) * mm});
            skLineSegment(sketch, "E989", {"start": v(122.74, 4.21) * mm, "end": v(127.08, 4.21) * mm});
            skLineSegment(sketch, "E990", {"start": v(127.08, 4.21) * mm, "end": v(125.24, -3.28) * mm});
            skLineSegment(sketch, "E991", {"start": v(125.24, -3.28) * mm, "end": v(88.2, -3.39) * mm});
            skLineSegment(sketch, "E992", {"start": v(88.2, -3.39) * mm, "end": v(90.05, 4.1) * mm});
            skLineSegment(sketch, "E993", {"start": v(90.05, 4.1) * mm, "end": v(97, 4.1) * mm});
            skLineSegment(sketch, "E994", {"start": v(97, 4.1) * mm, "end": v(95.7, 13.12) * mm});
            skLineSegment(sketch, "E995", {"start": v(95.7, 13.12) * mm, "end": v(67.68, 13.12) * mm});
            skLineSegment(sketch, "E996", {"start": v(67.68, 13.12) * mm, "end": v(61.82, 4.1) * mm});
            skLineSegment(sketch, "E997", {"start": v(61.82, 4.1) * mm, "end": v(68.99, 4.1) * mm});
            skLineSegment(sketch, "E998", {"start": v(68.99, 4.1) * mm, "end": v(67.14, -3.39) * mm});
            skLineSegment(sketch, "E999", {"start": v(67.14, -3.39) * mm, "end": v(43.36, -3.39) * mm});
            skLineSegment(sketch, "E1000", {"start": v(43.36, -3.39) * mm, "end": v(45.2, 4.1) * mm});
            skLineSegment(sketch, "E1001", {"start": v(45.2, 4.1) * mm, "end": v(50.31, 4.1) * mm});
            skLineSegment(sketch, "E1002", {"start": v(50.31, 4.1) * mm, "end": v(65.65, 27.3) * mm});
            skLineSegment(sketch, "E1003", {"start": v(65.65, 27.3) * mm, "end": v(77.1, 27.3) * mm});
            skLineSegment(sketch, "E1004", {"start": v(77.1, 27.3) * mm, "end": v(73.55, 21.91) * mm});
            skLineSegment(sketch, "E1005", {"start": v(73.55, 21.91) * mm, "end": v(94.18, 22.02) * mm});
            skLineSegment(sketch, "E1006", {"start": v(94.18, 22.02) * mm, "end": v(93.28, 27.3) * mm});
            skLineSegment(sketch, "E1007", {"start": v(93.28, 27.3) * mm, "end": v(118.45, 27.3) * mm});
            skLineSegment(sketch, "E1008", {"start": v(118.08, 29.3) * mm, "end": v(92.94, 29.3) * mm});
            skLineSegment(sketch, "E1009", {"start": v(92.94, 29.3) * mm, "end": v(89.95, 46.78) * mm});
            skLineSegment(sketch, "E1010", {"start": v(89.95, 46.78) * mm, "end": v(78.42, 29.3) * mm});
            skLineSegment(sketch, "E1011", {"start": v(78.42, 29.3) * mm, "end": v(66.97, 29.3) * mm});
            skLineSegment(sketch, "E1012", {"start": v(66.97, 29.3) * mm, "end": v(89.73, 63.72) * mm});
            skLineSegment(sketch, "E1013", {"start": v(89.73, 63.72) * mm, "end": v(111.66, 63.83) * mm});
            skLineSegment(sketch, "E1014", {"start": v(111.66, 63.83) * mm, "end": v(118.08, 29.3) * mm});
            skLineSegment(sketch, "E1015", {"start": v(315.14, 29.3) * mm, "end": v(313.56, 29.3) * mm});
            skLineSegment(sketch, "E1016", {"start": v(313.56, 29.3) * mm, "end": v(310.92, 30.12) * mm});
            skLineSegment(sketch, "E1017", {"start": v(310.92, 30.12) * mm, "end": v(308.24, 30.75) * mm});
            skLineSegment(sketch, "E1018", {"start": v(308.24, 30.75) * mm, "end": v(307.1, 30.94) * mm});
            skLineSegment(sketch, "E1019", {"start": v(307.1, 30.94) * mm, "end": v(305.93, 31.03) * mm});
            skLineSegment(sketch, "E1020", {"start": v(305.93, 31.03) * mm, "end": v(304.76, 31.01) * mm});
            skLineSegment(sketch, "E1021", {"start": v(304.76, 31.01) * mm, "end": v(303.4, 30.83) * mm});
            skLineSegment(sketch, "E1022", {"start": v(303.4, 30.83) * mm, "end": v(302.07, 30.48) * mm});
            skLineSegment(sketch, "E1023", {"start": v(302.07, 30.48) * mm, "end": v(300.9, 29.97) * mm});
            skLineSegment(sketch, "E1024", {"start": v(300.9, 29.97) * mm, "end": v(299.79, 29.3) * mm});
            skLineSegment(sketch, "E1025", {"start": v(299.79, 29.3) * mm, "end": v(275.85, 29.3) * mm});
            skLineSegment(sketch, "E1026", {"start": v(275.85, 29.3) * mm, "end": v(275.88, 29.8) * mm});
            skLineSegment(sketch, "E1027", {"start": v(275.88, 29.8) * mm, "end": v(275.79, 30.29) * mm});
            skLineSegment(sketch, "E1028", {"start": v(275.79, 30.29) * mm, "end": v(275.57, 30.73) * mm});
            skLineSegment(sketch, "E1029", {"start": v(275.57, 30.73) * mm, "end": v(275.24, 31.1) * mm});
            skLineSegment(sketch, "E1030", {"start": v(275.24, 31.1) * mm, "end": v(274.55, 31.58) * mm});
            skLineSegment(sketch, "E1031", {"start": v(274.55, 31.58) * mm, "end": v(271.95, 30.06) * mm});
            skLineSegment(sketch, "E1032", {"start": v(271.95, 30.06) * mm, "end": v(268.47, 33.97) * mm});
            skLineSegment(sketch, "E1033", {"start": v(268.47, 33.97) * mm, "end": v(284.54, 46.67) * mm});
            skLineSegment(sketch, "E1034", {"start": v(284.54, 46.67) * mm, "end": v(286.2, 45.94) * mm});
            skLineSegment(sketch, "E1035", {"start": v(286.2, 45.94) * mm, "end": v(287.8, 45.13) * mm});
            skLineSegment(sketch, "E1036", {"start": v(287.8, 45.13) * mm, "end": v(289.37, 44.23) * mm});
            skLineSegment(sketch, "E1037", {"start": v(289.37, 44.23) * mm, "end": v(290.51, 43.48) * mm});
            skLineSegment(sketch, "E1038", {"start": v(290.51, 43.48) * mm, "end": v(291.59, 42.65) * mm});
            skLineSegment(sketch, "E1039", {"start": v(291.59, 42.65) * mm, "end": v(292.6, 41.73) * mm});
            skLineSegment(sketch, "E1040", {"start": v(292.6, 41.73) * mm, "end": v(293.3, 40.97) * mm});
            skLineSegment(sketch, "E1041", {"start": v(293.3, 40.97) * mm, "end": v(293.9, 40.15) * mm});
            skLineSegment(sketch, "E1042", {"start": v(293.9, 40.15) * mm, "end": v(294.45, 39.28) * mm});
            skLineSegment(sketch, "E1043", {"start": v(294.45, 39.28) * mm, "end": v(294.86, 38.45) * mm});
            skLineSegment(sketch, "E1044", {"start": v(294.86, 38.45) * mm, "end": v(295.17, 37.58) * mm});
            skLineSegment(sketch, "E1045", {"start": v(295.17, 37.58) * mm, "end": v(295.4, 36.68) * mm});
            skLineSegment(sketch, "E1046", {"start": v(295.4, 36.68) * mm, "end": v(297.58, 38.81) * mm});
            skLineSegment(sketch, "E1047", {"start": v(297.58, 38.81) * mm, "end": v(299.83, 40.87) * mm});
            skLineSegment(sketch, "E1048", {"start": v(299.83, 40.87) * mm, "end": v(302.16, 42.84) * mm});
            skLineSegment(sketch, "E1049", {"start": v(302.16, 42.84) * mm, "end": v(303.5, 43.9) * mm});
            skLineSegment(sketch, "E1050", {"start": v(303.5, 43.9) * mm, "end": v(304.94, 44.84) * mm});
            skLineSegment(sketch, "E1051", {"start": v(304.94, 44.84) * mm, "end": v(306.44, 45.66) * mm});
            skLineSegment(sketch, "E1052", {"start": v(306.44, 45.66) * mm, "end": v(307.49, 46.1) * mm});
            skLineSegment(sketch, "E1053", {"start": v(307.49, 46.1) * mm, "end": v(308.57, 46.42) * mm});
            skLineSegment(sketch, "E1054", {"start": v(308.57, 46.42) * mm, "end": v(309.68, 46.61) * mm});
            skLineSegment(sketch, "E1055", {"start": v(309.68, 46.61) * mm, "end": v(310.88, 46.67) * mm});
            skLineSegment(sketch, "E1056", {"start": v(310.88, 46.67) * mm, "end": v(312.08, 46.6) * mm});
            skLineSegment(sketch, "E1057", {"start": v(312.08, 46.6) * mm, "end": v(313.27, 46.4) * mm});
            skLineSegment(sketch, "E1058", {"start": v(313.27, 46.4) * mm, "end": v(314.9, 46) * mm});
            skLineSegment(sketch, "E1059", {"start": v(314.9, 46) * mm, "end": v(316.52, 45.52) * mm});
            skLineSegment(sketch, "E1060", {"start": v(316.52, 45.52) * mm, "end": v(318.1, 44.94) * mm});
            skLineSegment(sketch, "E1061", {"start": v(318.1, 44.94) * mm, "end": v(320.05, 47.22) * mm});
            skLineSegment(sketch, "E1062", {"start": v(320.05, 47.22) * mm, "end": v(325.92, 45.26) * mm});
            skLineSegment(sketch, "E1063", {"start": v(325.92, 45.26) * mm, "end": v(315.14, 29.3) * mm});
            skLineSegment(sketch, "E1064", {"start": v(297.77, 27.3) * mm, "end": v(297.22, 26.45) * mm});
            skLineSegment(sketch, "E1065", {"start": v(297.22, 26.45) * mm, "end": v(296.75, 25.55) * mm});
            skLineSegment(sketch, "E1066", {"start": v(296.75, 25.55) * mm, "end": v(296.35, 24.5) * mm});
            skLineSegment(sketch, "E1067", {"start": v(296.35, 24.5) * mm, "end": v(296.05, 23.43) * mm});
            skLineSegment(sketch, "E1068", {"start": v(296.05, 23.43) * mm, "end": v(291.17, 3.02) * mm});
            skLineSegment(sketch, "E1069", {"start": v(291.17, 3.02) * mm, "end": v(297.25, 3.02) * mm});
            skLineSegment(sketch, "E1070", {"start": v(297.25, 3.02) * mm, "end": v(295.84, -3.17) * mm});
            skLineSegment(sketch, "E1071", {"start": v(295.84, -3.17) * mm, "end": v(263.9, -3.17) * mm});
            skLineSegment(sketch, "E1072", {"start": v(263.9, -3.17) * mm, "end": v(265.43, 2.91) * mm});
            skLineSegment(sketch, "E1073", {"start": v(265.43, 2.91) * mm, "end": v(269.66, 2.91) * mm});
            skLineSegment(sketch, "E1074", {"start": v(269.66, 2.91) * mm, "end": v(275.44, 27.3) * mm});
            skLineSegment(sketch, "E1075", {"start": v(275.44, 27.3) * mm, "end": v(297.77, 27.3) * mm});
            skLineSegment(sketch, "E1076", {"start": v(207.07, 27.3) * mm, "end": v(225.94, 27.3) * mm});
            skLineSegment(sketch, "E1077", {"start": v(225.94, 27.3) * mm, "end": v(225.99, 25.2) * mm});
            skLineSegment(sketch, "E1078", {"start": v(225.99, 25.2) * mm, "end": v(226.23, 23.1) * mm});
            skLineSegment(sketch, "E1079", {"start": v(226.23, 23.1) * mm, "end": v(239.72, 27.3) * mm});
            skLineSegment(sketch, "E1080", {"start": v(239.72, 27.3) * mm, "end": v(263.78, 27.3) * mm});
            skLineSegment(sketch, "E1081", {"start": v(263.78, 27.3) * mm, "end": v(263.81, 26.87) * mm});
            skLineSegment(sketch, "E1082", {"start": v(263.81, 26.87) * mm, "end": v(263.78, 26.62) * mm});
            skLineSegment(sketch, "E1083", {"start": v(263.78, 26.62) * mm, "end": v(263.63, 26.42) * mm});
            skLineSegment(sketch, "E1084", {"start": v(263.63, 26.42) * mm, "end": v(263.43, 26.26) * mm});
            skLineSegment(sketch, "E1085", {"start": v(263.43, 26.26) * mm, "end": v(263.2, 26.15) * mm});
            skLineSegment(sketch, "E1086", {"start": v(263.2, 26.15) * mm, "end": v(262.2, 25.89) * mm});
            skLineSegment(sketch, "E1087", {"start": v(262.2, 25.89) * mm, "end": v(260.38, 25.53) * mm});
            skLineSegment(sketch, "E1088", {"start": v(260.38, 25.53) * mm, "end": v(257.08, 24.82) * mm});
            skLineSegment(sketch, "E1089", {"start": v(257.08, 24.82) * mm, "end": v(254.95, 24.27) * mm});
            skLineSegment(sketch, "E1090", {"start": v(254.95, 24.27) * mm, "end": v(252.83, 23.65) * mm});
            skLineSegment(sketch, "E1091", {"start": v(252.83, 23.65) * mm, "end": v(227.64, 15.83) * mm});
            skLineSegment(sketch, "E1092", {"start": v(227.64, 15.83) * mm, "end": v(228.22, 14.43) * mm});
            skLineSegment(sketch, "E1093", {"start": v(228.22, 14.43) * mm, "end": v(228.95, 13.1) * mm});
            skLineSegment(sketch, "E1094", {"start": v(228.95, 13.1) * mm, "end": v(229.82, 11.85) * mm});
            skLineSegment(sketch, "E1095", {"start": v(229.82, 11.85) * mm, "end": v(230.8, 10.77) * mm});
            skLineSegment(sketch, "E1096", {"start": v(230.8, 10.77) * mm, "end": v(231.91, 9.82) * mm});
            skLineSegment(sketch, "E1097", {"start": v(231.91, 9.82) * mm, "end": v(233.13, 9.02) * mm});
            skLineSegment(sketch, "E1098", {"start": v(233.13, 9.02) * mm, "end": v(234.6, 8.31) * mm});
            skLineSegment(sketch, "E1099", {"start": v(234.6, 8.31) * mm, "end": v(236.14, 7.78) * mm});
            skLineSegment(sketch, "E1100", {"start": v(236.14, 7.78) * mm, "end": v(237.73, 7.43) * mm});
            skLineSegment(sketch, "E1101", {"start": v(237.73, 7.43) * mm, "end": v(239.72, 7.2) * mm});
            skLineSegment(sketch, "E1102", {"start": v(239.72, 7.2) * mm, "end": v(241.72, 7.15) * mm});
            skLineSegment(sketch, "E1103", {"start": v(241.72, 7.15) * mm, "end": v(243.72, 7.27) * mm});
            skLineSegment(sketch, "E1104", {"start": v(243.72, 7.27) * mm, "end": v(245.94, 7.6) * mm});
            skLineSegment(sketch, "E1105", {"start": v(245.94, 7.6) * mm, "end": v(248.12, 8.13) * mm});
            skLineSegment(sketch, "E1106", {"start": v(248.12, 8.13) * mm, "end": v(250.25, 8.85) * mm});
            skLineSegment(sketch, "E1107", {"start": v(250.25, 8.85) * mm, "end": v(252.47, 9.81) * mm});
            skLineSegment(sketch, "E1108", {"start": v(252.47, 9.81) * mm, "end": v(254.6, 10.95) * mm});
            skLineSegment(sketch, "E1109", {"start": v(254.6, 10.95) * mm, "end": v(256.63, 12.25) * mm});
            skLineSegment(sketch, "E1110", {"start": v(256.63, 12.25) * mm, "end": v(260.1, 8.34) * mm});
            skLineSegment(sketch, "E1111", {"start": v(260.1, 8.34) * mm, "end": v(257.79, 6.46) * mm});
            skLineSegment(sketch, "E1112", {"start": v(257.79, 6.46) * mm, "end": v(255.38, 4.7) * mm});
            skLineSegment(sketch, "E1113", {"start": v(255.38, 4.7) * mm, "end": v(252.9, 3.05) * mm});
            skLineSegment(sketch, "E1114", {"start": v(252.9, 3.05) * mm, "end": v(250.33, 1.53) * mm});
            skLineSegment(sketch, "E1115", {"start": v(250.33, 1.53) * mm, "end": v(247.92, 0.26) * mm});
            skLineSegment(sketch, "E1116", {"start": v(247.92, 0.26) * mm, "end": v(245.45, -0.87) * mm});
            skLineSegment(sketch, "E1117", {"start": v(245.45, -0.87) * mm, "end": v(242.91, -1.84) * mm});
            skLineSegment(sketch, "E1118", {"start": v(242.91, -1.84) * mm, "end": v(240.32, -2.67) * mm});
            skLineSegment(sketch, "E1119", {"start": v(240.32, -2.67) * mm, "end": v(237.76, -3.32) * mm});
            skLineSegment(sketch, "E1120", {"start": v(237.76, -3.32) * mm, "end": v(235.18, -3.83) * mm});
            skLineSegment(sketch, "E1121", {"start": v(235.18, -3.83) * mm, "end": v(232.57, -4.21) * mm});
            skLineSegment(sketch, "E1122", {"start": v(232.57, -4.21) * mm, "end": v(229.94, -4.46) * mm});
            skLineSegment(sketch, "E1123", {"start": v(229.94, -4.46) * mm, "end": v(227.65, -4.57) * mm});
            skLineSegment(sketch, "E1124", {"start": v(227.65, -4.57) * mm, "end": v(225.35, -4.55) * mm});
            skLineSegment(sketch, "E1125", {"start": v(225.35, -4.55) * mm, "end": v(223.07, -4.4) * mm});
            skLineSegment(sketch, "E1126", {"start": v(223.07, -4.4) * mm, "end": v(220.8, -4.11) * mm});
            skLineSegment(sketch, "E1127", {"start": v(220.8, -4.11) * mm, "end": v(218.98, -3.75) * mm});
            skLineSegment(sketch, "E1128", {"start": v(218.98, -3.75) * mm, "end": v(217.2, -3.25) * mm});
            skLineSegment(sketch, "E1129", {"start": v(217.2, -3.25) * mm, "end": v(215.47, -2.62) * mm});
            skLineSegment(sketch, "E1130", {"start": v(215.47, -2.62) * mm, "end": v(213.79, -1.85) * mm});
            skLineSegment(sketch, "E1131", {"start": v(213.79, -1.85) * mm, "end": v(212.4, -1.1) * mm});
            skLineSegment(sketch, "E1132", {"start": v(212.4, -1.1) * mm, "end": v(211.1, -0.21) * mm});
            skLineSegment(sketch, "E1133", {"start": v(211.1, -0.21) * mm, "end": v(209.86, 0.77) * mm});
            skLineSegment(sketch, "E1134", {"start": v(209.86, 0.77) * mm, "end": v(208.71, 1.85) * mm});
            skLineSegment(sketch, "E1135", {"start": v(208.71, 1.85) * mm, "end": v(207.72, 2.96) * mm});
            skLineSegment(sketch, "E1136", {"start": v(207.72, 2.96) * mm, "end": v(206.84, 4.15) * mm});
            skLineSegment(sketch, "E1137", {"start": v(206.84, 4.15) * mm, "end": v(206.07, 5.42) * mm});
            skLineSegment(sketch, "E1138", {"start": v(206.07, 5.42) * mm, "end": v(205.4, 6.75) * mm});
            skLineSegment(sketch, "E1139", {"start": v(205.4, 6.75) * mm, "end": v(204.84, 8.21) * mm});
            skLineSegment(sketch, "E1140", {"start": v(204.84, 8.21) * mm, "end": v(204.4, 9.72) * mm});
            skLineSegment(sketch, "E1141", {"start": v(204.4, 9.72) * mm, "end": v(204.09, 11.25) * mm});
            skLineSegment(sketch, "E1142", {"start": v(204.09, 11.25) * mm, "end": v(203.9, 12.8) * mm});
            skLineSegment(sketch, "E1143", {"start": v(203.9, 12.8) * mm, "end": v(203.85, 14.6) * mm});
            skLineSegment(sketch, "E1144", {"start": v(203.85, 14.6) * mm, "end": v(203.91, 16.4) * mm});
            skLineSegment(sketch, "E1145", {"start": v(203.91, 16.4) * mm, "end": v(204.1, 18.18) * mm});
            skLineSegment(sketch, "E1146", {"start": v(204.1, 18.18) * mm, "end": v(204.43, 19.94) * mm});
            skLineSegment(sketch, "E1147", {"start": v(204.43, 19.94) * mm, "end": v(204.9, 21.84) * mm});
            skLineSegment(sketch, "E1148", {"start": v(204.9, 21.84) * mm, "end": v(205.5, 23.71) * mm});
            skLineSegment(sketch, "E1149", {"start": v(205.5, 23.71) * mm, "end": v(206.23, 25.53) * mm});
            skLineSegment(sketch, "E1150", {"start": v(206.23, 25.53) * mm, "end": v(207.07, 27.3) * mm});
            skLineSegment(sketch, "E1151", {"start": v(208.2, 29.3) * mm, "end": v(209.52, 31.26) * mm});
            skLineSegment(sketch, "E1152", {"start": v(209.52, 31.26) * mm, "end": v(210.98, 33.11) * mm});
            skLineSegment(sketch, "E1153", {"start": v(210.98, 33.11) * mm, "end": v(212.56, 34.86) * mm});
            skLineSegment(sketch, "E1154", {"start": v(212.56, 34.86) * mm, "end": v(214.27, 36.5) * mm});
            skLineSegment(sketch, "E1155", {"start": v(214.27, 36.5) * mm, "end": v(216.2, 38.11) * mm});
            skLineSegment(sketch, "E1156", {"start": v(216.2, 38.11) * mm, "end": v(218.23, 39.6) * mm});
            skLineSegment(sketch, "E1157", {"start": v(218.23, 39.6) * mm, "end": v(220.34, 40.96) * mm});
            skLineSegment(sketch, "E1158", {"start": v(220.34, 40.96) * mm, "end": v(222.55, 42.18) * mm});
            skLineSegment(sketch, "E1159", {"start": v(222.55, 42.18) * mm, "end": v(224.85, 43.28) * mm});
            skLineSegment(sketch, "E1160", {"start": v(224.85, 43.28) * mm, "end": v(227.22, 44.23) * mm});
            skLineSegment(sketch, "E1161", {"start": v(227.22, 44.23) * mm, "end": v(229.64, 45.03) * mm});
            skLineSegment(sketch, "E1162", {"start": v(229.64, 45.03) * mm, "end": v(232.11, 45.67) * mm});
            skLineSegment(sketch, "E1163", {"start": v(232.11, 45.67) * mm, "end": v(234.47, 46.12) * mm});
            skLineSegment(sketch, "E1164", {"start": v(234.47, 46.12) * mm, "end": v(236.86, 46.41) * mm});
            skLineSegment(sketch, "E1165", {"start": v(236.86, 46.41) * mm, "end": v(239.26, 46.55) * mm});
            skLineSegment(sketch, "E1166", {"start": v(239.26, 46.55) * mm, "end": v(241.67, 46.53) * mm});
            skLineSegment(sketch, "E1167", {"start": v(241.67, 46.53) * mm, "end": v(243.8, 46.37) * mm});
            skLineSegment(sketch, "E1168", {"start": v(243.8, 46.37) * mm, "end": v(245.9, 46.08) * mm});
            skLineSegment(sketch, "E1169", {"start": v(245.9, 46.08) * mm, "end": v(247.98, 45.63) * mm});
            skLineSegment(sketch, "E1170", {"start": v(247.98, 45.63) * mm, "end": v(250.03, 45.03) * mm});
            skLineSegment(sketch, "E1171", {"start": v(250.03, 45.03) * mm, "end": v(251.7, 44.4) * mm});
            skLineSegment(sketch, "E1172", {"start": v(251.7, 44.4) * mm, "end": v(253.3, 43.6) * mm});
            skLineSegment(sketch, "E1173", {"start": v(253.3, 43.6) * mm, "end": v(254.82, 42.65) * mm});
            skLineSegment(sketch, "E1174", {"start": v(254.82, 42.65) * mm, "end": v(256.25, 41.57) * mm});
            skLineSegment(sketch, "E1175", {"start": v(256.25, 41.57) * mm, "end": v(257.54, 40.37) * mm});
            skLineSegment(sketch, "E1176", {"start": v(257.54, 40.37) * mm, "end": v(258.72, 39.07) * mm});
            skLineSegment(sketch, "E1177", {"start": v(258.72, 39.07) * mm, "end": v(259.8, 37.67) * mm});
            skLineSegment(sketch, "E1178", {"start": v(259.8, 37.67) * mm, "end": v(260.74, 36.19) * mm});
            skLineSegment(sketch, "E1179", {"start": v(260.74, 36.19) * mm, "end": v(261.62, 34.55) * mm});
            skLineSegment(sketch, "E1180", {"start": v(261.62, 34.55) * mm, "end": v(262.38, 32.85) * mm});
            skLineSegment(sketch, "E1181", {"start": v(262.38, 32.85) * mm, "end": v(263, 31.1) * mm});
            skLineSegment(sketch, "E1182", {"start": v(263, 31.1) * mm, "end": v(263.51, 29.3) * mm});
            skLineSegment(sketch, "E1183", {"start": v(263.51, 29.3) * mm, "end": v(242.44, 29.3) * mm});
            skLineSegment(sketch, "E1184", {"start": v(242.44, 29.3) * mm, "end": v(242, 31.07) * mm});
            skLineSegment(sketch, "E1185", {"start": v(242, 31.07) * mm, "end": v(241.44, 32.8) * mm});
            skLineSegment(sketch, "E1186", {"start": v(241.44, 32.8) * mm, "end": v(240.88, 34.1) * mm});
            skLineSegment(sketch, "E1187", {"start": v(240.88, 34.1) * mm, "end": v(240.17, 35.33) * mm});
            skLineSegment(sketch, "E1188", {"start": v(240.17, 35.33) * mm, "end": v(239.47, 36.25) * mm});
            skLineSegment(sketch, "E1189", {"start": v(239.47, 36.25) * mm, "end": v(238.64, 37.08) * mm});
            skLineSegment(sketch, "E1190", {"start": v(238.64, 37.08) * mm, "end": v(237.83, 37.7) * mm});
            skLineSegment(sketch, "E1191", {"start": v(237.83, 37.7) * mm, "end": v(236.93, 38.18) * mm});
            skLineSegment(sketch, "E1192", {"start": v(236.93, 38.18) * mm, "end": v(235.98, 38.51) * mm});
            skLineSegment(sketch, "E1193", {"start": v(235.98, 38.51) * mm, "end": v(235, 38.7) * mm});
            skLineSegment(sketch, "E1194", {"start": v(235, 38.7) * mm, "end": v(234, 38.75) * mm});
            skLineSegment(sketch, "E1195", {"start": v(234, 38.75) * mm, "end": v(233, 38.65) * mm});
            skLineSegment(sketch, "E1196", {"start": v(233, 38.65) * mm, "end": v(232.03, 38.41) * mm});
            skLineSegment(sketch, "E1197", {"start": v(232.03, 38.41) * mm, "end": v(231.1, 38.04) * mm});
            skLineSegment(sketch, "E1198", {"start": v(231.1, 38.04) * mm, "end": v(230.22, 37.5) * mm});
            skLineSegment(sketch, "E1199", {"start": v(230.22, 37.5) * mm, "end": v(229.42, 36.85) * mm});
            skLineSegment(sketch, "E1200", {"start": v(229.42, 36.85) * mm, "end": v(228.63, 35.98) * mm});
            skLineSegment(sketch, "E1201", {"start": v(228.63, 35.98) * mm, "end": v(227.96, 35.02) * mm});
            skLineSegment(sketch, "E1202", {"start": v(227.96, 35.02) * mm, "end": v(227.3, 33.78) * mm});
            skLineSegment(sketch, "E1203", {"start": v(227.3, 33.78) * mm, "end": v(226.8, 32.48) * mm});
            skLineSegment(sketch, "E1204", {"start": v(226.8, 32.48) * mm, "end": v(226.37, 30.9) * mm});
            skLineSegment(sketch, "E1205", {"start": v(226.37, 30.9) * mm, "end": v(226.1, 29.3) * mm});
            skLineSegment(sketch, "E1206", {"start": v(226.1, 29.3) * mm, "end": v(208.2, 29.3) * mm});
            skLineSegment(sketch, "E1207", {"start": v(350.8, 27.3) * mm, "end": v(345.03, 3.02) * mm});
            skLineSegment(sketch, "E1208", {"start": v(345.03, 3.02) * mm, "end": v(349.26, 3.02) * mm});
            skLineSegment(sketch, "E1209", {"start": v(349.26, 3.02) * mm, "end": v(347.74, -3.06) * mm});
            skLineSegment(sketch, "E1210", {"start": v(347.74, -3.06) * mm, "end": v(317.88, -3.06) * mm});
            skLineSegment(sketch, "E1211", {"start": v(317.88, -3.06) * mm, "end": v(319.3, 3.02) * mm});
            skLineSegment(sketch, "E1212", {"start": v(319.3, 3.02) * mm, "end": v(323.53, 3.02) * mm});
            skLineSegment(sketch, "E1213", {"start": v(323.53, 3.02) * mm, "end": v(329.36, 27.3) * mm});
            skLineSegment(sketch, "E1214", {"start": v(329.36, 27.3) * mm, "end": v(350.8, 27.3) * mm});
            skLineSegment(sketch, "E1215", {"start": v(351.27, 29.3) * mm, "end": v(329.84, 29.3) * mm});
            skLineSegment(sketch, "E1216", {"start": v(329.84, 29.3) * mm, "end": v(331.45, 36.03) * mm});
            skLineSegment(sketch, "E1217", {"start": v(331.45, 36.03) * mm, "end": v(327.1, 35.49) * mm});
            skLineSegment(sketch, "E1218", {"start": v(327.1, 35.49) * mm, "end": v(328.41, 41.03) * mm});
            skLineSegment(sketch, "E1219", {"start": v(328.41, 41.03) * mm, "end": v(355.23, 46.67) * mm});
            skLineSegment(sketch, "E1220", {"start": v(355.23, 46.67) * mm, "end": v(356.1, 46.67) * mm});
            skLineSegment(sketch, "E1221", {"start": v(356.1, 46.67) * mm, "end": v(354.42, 41.77) * mm});
            skLineSegment(sketch, "E1222", {"start": v(354.42, 41.77) * mm, "end": v(353.87, 40) * mm});
            skLineSegment(sketch, "E1223", {"start": v(353.87, 40) * mm, "end": v(353.39, 38.2) * mm});
            skLineSegment(sketch, "E1224", {"start": v(353.39, 38.2) * mm, "end": v(351.27, 29.3) * mm});
            skLineSegment(sketch, "E1225", {"start": v(120.67, 81.1) * mm, "end": v(111.45, 81.1) * mm});
            skLineSegment(sketch, "E1226", {"start": v(111.45, 81.1) * mm, "end": v(111.35, 81.82) * mm});
            skLineSegment(sketch, "E1227", {"start": v(111.35, 81.82) * mm, "end": v(111.14, 82.51) * mm});
            skLineSegment(sketch, "E1228", {"start": v(111.14, 82.51) * mm, "end": v(110.8, 83.16) * mm});
            skLineSegment(sketch, "E1229", {"start": v(110.8, 83.16) * mm, "end": v(110.36, 83.74) * mm});
            skLineSegment(sketch, "E1230", {"start": v(110.36, 83.74) * mm, "end": v(109.77, 84.27) * mm});
            skLineSegment(sketch, "E1231", {"start": v(109.77, 84.27) * mm, "end": v(109.11, 84.7) * mm});
            skLineSegment(sketch, "E1232", {"start": v(109.11, 84.7) * mm, "end": v(108.29, 85.06) * mm});
            skLineSegment(sketch, "E1233", {"start": v(108.29, 85.06) * mm, "end": v(107.42, 85.3) * mm});
            skLineSegment(sketch, "E1234", {"start": v(107.42, 85.3) * mm, "end": v(106.34, 85.42) * mm});
            skLineSegment(sketch, "E1235", {"start": v(106.34, 85.42) * mm, "end": v(105.25, 85.41) * mm});
            skLineSegment(sketch, "E1236", {"start": v(105.25, 85.41) * mm, "end": v(104.18, 85.27) * mm});
            skLineSegment(sketch, "E1237", {"start": v(104.18, 85.27) * mm, "end": v(103.13, 85) * mm});
            skLineSegment(sketch, "E1238", {"start": v(103.13, 85) * mm, "end": v(102.06, 84.58) * mm});
            skLineSegment(sketch, "E1239", {"start": v(102.06, 84.58) * mm, "end": v(101.05, 84.04) * mm});
            skLineSegment(sketch, "E1240", {"start": v(101.05, 84.04) * mm, "end": v(100.17, 83.42) * mm});
            skLineSegment(sketch, "E1241", {"start": v(100.17, 83.42) * mm, "end": v(99.37, 82.7) * mm});
            skLineSegment(sketch, "E1242", {"start": v(99.37, 82.7) * mm, "end": v(98.74, 81.93) * mm});
            skLineSegment(sketch, "E1243", {"start": v(98.74, 81.93) * mm, "end": v(98.22, 81.1) * mm});
            skLineSegment(sketch, "E1244", {"start": v(98.22, 81.1) * mm, "end": v(88.85, 81.1) * mm});
            skLineSegment(sketch, "E1245", {"start": v(88.85, 81.1) * mm, "end": v(89.39, 82.43) * mm});
            skLineSegment(sketch, "E1246", {"start": v(89.39, 82.43) * mm, "end": v(90.06, 83.71) * mm});
            skLineSegment(sketch, "E1247", {"start": v(90.06, 83.71) * mm, "end": v(90.85, 84.92) * mm});
            skLineSegment(sketch, "E1248", {"start": v(90.85, 84.92) * mm, "end": v(91.86, 86.16) * mm});
            skLineSegment(sketch, "E1249", {"start": v(91.86, 86.16) * mm, "end": v(92.97, 87.31) * mm});
            skLineSegment(sketch, "E1250", {"start": v(92.97, 87.31) * mm, "end": v(94.18, 88.36) * mm});
            skLineSegment(sketch, "E1251", {"start": v(94.18, 88.36) * mm, "end": v(95.6, 89.4) * mm});
            skLineSegment(sketch, "E1252", {"start": v(95.6, 89.4) * mm, "end": v(97.08, 90.3) * mm});
            skLineSegment(sketch, "E1253", {"start": v(97.08, 90.3) * mm, "end": v(98.65, 91.08) * mm});
            skLineSegment(sketch, "E1254", {"start": v(98.65, 91.08) * mm, "end": v(100.31, 91.76) * mm});
            skLineSegment(sketch, "E1255", {"start": v(100.31, 91.76) * mm, "end": v(102.03, 92.3) * mm});
            skLineSegment(sketch, "E1256", {"start": v(102.03, 92.3) * mm, "end": v(103.78, 92.7) * mm});
            skLineSegment(sketch, "E1257", {"start": v(103.78, 92.7) * mm, "end": v(105.48, 92.93) * mm});
            skLineSegment(sketch, "E1258", {"start": v(105.48, 92.93) * mm, "end": v(107.2, 93.04) * mm});
            skLineSegment(sketch, "E1259", {"start": v(107.2, 93.04) * mm, "end": v(108.92, 93) * mm});
            skLineSegment(sketch, "E1260", {"start": v(108.92, 93) * mm, "end": v(110.45, 92.83) * mm});
            skLineSegment(sketch, "E1261", {"start": v(110.45, 92.83) * mm, "end": v(111.96, 92.52) * mm});
            skLineSegment(sketch, "E1262", {"start": v(111.96, 92.52) * mm, "end": v(113.43, 92.08) * mm});
            skLineSegment(sketch, "E1263", {"start": v(113.43, 92.08) * mm, "end": v(114.66, 91.57) * mm});
            skLineSegment(sketch, "E1264", {"start": v(114.66, 91.57) * mm, "end": v(115.83, 90.94) * mm});
            skLineSegment(sketch, "E1265", {"start": v(115.83, 90.94) * mm, "end": v(116.93, 90.19) * mm});
            skLineSegment(sketch, "E1266", {"start": v(116.93, 90.19) * mm, "end": v(117.83, 89.42) * mm});
            skLineSegment(sketch, "E1267", {"start": v(117.83, 89.42) * mm, "end": v(118.63, 88.55) * mm});
            skLineSegment(sketch, "E1268", {"start": v(118.63, 88.55) * mm, "end": v(119.32, 87.6) * mm});
            skLineSegment(sketch, "E1269", {"start": v(119.32, 87.6) * mm, "end": v(119.96, 86.4) * mm});
            skLineSegment(sketch, "E1270", {"start": v(119.96, 86.4) * mm, "end": v(120.42, 85.13) * mm});
            skLineSegment(sketch, "E1271", {"start": v(120.42, 85.13) * mm, "end": v(120.7, 83.8) * mm});
            skLineSegment(sketch, "E1272", {"start": v(120.7, 83.8) * mm, "end": v(120.78, 82.45) * mm});
            skLineSegment(sketch, "E1273", {"start": v(120.78, 82.45) * mm, "end": v(120.67, 81.1) * mm});
            skLineSegment(sketch, "E1274", {"start": v(120.2, 79.1) * mm, "end": v(119.68, 77.74) * mm});
            skLineSegment(sketch, "E1275", {"start": v(119.68, 77.74) * mm, "end": v(119.02, 76.45) * mm});
            skLineSegment(sketch, "E1276", {"start": v(119.02, 76.45) * mm, "end": v(118.23, 75.23) * mm});
            skLineSegment(sketch, "E1277", {"start": v(118.23, 75.23) * mm, "end": v(117.23, 73.97) * mm});
            skLineSegment(sketch, "E1278", {"start": v(117.23, 73.97) * mm, "end": v(116.13, 72.8) * mm});
            skLineSegment(sketch, "E1279", {"start": v(116.13, 72.8) * mm, "end": v(114.92, 71.75) * mm});
            skLineSegment(sketch, "E1280", {"start": v(114.92, 71.75) * mm, "end": v(113.5, 70.7) * mm});
            skLineSegment(sketch, "E1281", {"start": v(113.5, 70.7) * mm, "end": v(112, 69.78) * mm});
            skLineSegment(sketch, "E1282", {"start": v(112, 69.78) * mm, "end": v(110.42, 68.98) * mm});
            skLineSegment(sketch, "E1283", {"start": v(110.42, 68.98) * mm, "end": v(108.73, 68.3) * mm});
            skLineSegment(sketch, "E1284", {"start": v(108.73, 68.3) * mm, "end": v(106.99, 67.75) * mm});
            skLineSegment(sketch, "E1285", {"start": v(106.99, 67.75) * mm, "end": v(105.2, 67.35) * mm});
            skLineSegment(sketch, "E1286", {"start": v(105.2, 67.35) * mm, "end": v(103.45, 67.1) * mm});
            skLineSegment(sketch, "E1287", {"start": v(103.45, 67.1) * mm, "end": v(101.68, 66.98) * mm});
            skLineSegment(sketch, "E1288", {"start": v(101.68, 66.98) * mm, "end": v(99.9, 67.02) * mm});
            skLineSegment(sketch, "E1289", {"start": v(99.9, 67.02) * mm, "end": v(98.37, 67.17) * mm});
            skLineSegment(sketch, "E1290", {"start": v(98.37, 67.17) * mm, "end": v(96.86, 67.47) * mm});
            skLineSegment(sketch, "E1291", {"start": v(96.86, 67.47) * mm, "end": v(95.38, 67.92) * mm});
            skLineSegment(sketch, "E1292", {"start": v(95.38, 67.92) * mm, "end": v(94.17, 68.42) * mm});
            skLineSegment(sketch, "E1293", {"start": v(94.17, 68.42) * mm, "end": v(93.01, 69.05) * mm});
            skLineSegment(sketch, "E1294", {"start": v(93.01, 69.05) * mm, "end": v(91.93, 69.8) * mm});
            skLineSegment(sketch, "E1295", {"start": v(91.93, 69.8) * mm, "end": v(91.05, 70.58) * mm});
            skLineSegment(sketch, "E1296", {"start": v(91.05, 70.58) * mm, "end": v(90.27, 71.46) * mm});
            skLineSegment(sketch, "E1297", {"start": v(90.27, 71.46) * mm, "end": v(89.6, 72.42) * mm});
            skLineSegment(sketch, "E1298", {"start": v(89.6, 72.42) * mm, "end": v(88.97, 73.65) * mm});
            skLineSegment(sketch, "E1299", {"start": v(88.97, 73.65) * mm, "end": v(88.52, 74.97) * mm});
            skLineSegment(sketch, "E1300", {"start": v(88.52, 74.97) * mm, "end": v(88.27, 76.33) * mm});
            skLineSegment(sketch, "E1301", {"start": v(88.27, 76.33) * mm, "end": v(88.21, 77.72) * mm});
            skLineSegment(sketch, "E1302", {"start": v(88.21, 77.72) * mm, "end": v(88.35, 79.1) * mm});
            skLineSegment(sketch, "E1303", {"start": v(88.35, 79.1) * mm, "end": v(97.66, 79.1) * mm});
            skLineSegment(sketch, "E1304", {"start": v(97.66, 79.1) * mm, "end": v(97.7, 78.35) * mm});
            skLineSegment(sketch, "E1305", {"start": v(97.7, 78.35) * mm, "end": v(97.86, 77.63) * mm});
            skLineSegment(sketch, "E1306", {"start": v(97.86, 77.63) * mm, "end": v(98.17, 76.94) * mm});
            skLineSegment(sketch, "E1307", {"start": v(98.17, 76.94) * mm, "end": v(98.6, 76.33) * mm});
            skLineSegment(sketch, "E1308", {"start": v(98.6, 76.33) * mm, "end": v(99.2, 75.75) * mm});
            skLineSegment(sketch, "E1309", {"start": v(99.2, 75.75) * mm, "end": v(99.87, 75.3) * mm});
            skLineSegment(sketch, "E1310", {"start": v(99.87, 75.3) * mm, "end": v(100.74, 74.9) * mm});
            skLineSegment(sketch, "E1311", {"start": v(100.74, 74.9) * mm, "end": v(101.66, 74.63) * mm});
            skLineSegment(sketch, "E1312", {"start": v(101.66, 74.63) * mm, "end": v(102.8, 74.5) * mm});
            skLineSegment(sketch, "E1313", {"start": v(102.8, 74.5) * mm, "end": v(103.94, 74.5) * mm});
            skLineSegment(sketch, "E1314", {"start": v(103.94, 74.5) * mm, "end": v(105.08, 74.65) * mm});
            skLineSegment(sketch, "E1315", {"start": v(105.08, 74.65) * mm, "end": v(106.19, 74.95) * mm});
            skLineSegment(sketch, "E1316", {"start": v(106.19, 74.95) * mm, "end": v(107.29, 75.4) * mm});
            skLineSegment(sketch, "E1317", {"start": v(107.29, 75.4) * mm, "end": v(108.33, 75.98) * mm});
            skLineSegment(sketch, "E1318", {"start": v(108.33, 75.98) * mm, "end": v(109.2, 76.65) * mm});
            skLineSegment(sketch, "E1319", {"start": v(109.2, 76.65) * mm, "end": v(110, 77.42) * mm});
            skLineSegment(sketch, "E1320", {"start": v(110, 77.42) * mm, "end": v(110.6, 78.22) * mm});
            skLineSegment(sketch, "E1321", {"start": v(110.6, 78.22) * mm, "end": v(111.07, 79.1) * mm});
            skLineSegment(sketch, "E1322", {"start": v(111.07, 79.1) * mm, "end": v(120.2, 79.1) * mm});
            skSolve(sketch);
        }
        {
            var Q0;
            {var subQ3=sQuery(id+"F0.wireOp",EDGE,"E4");Q0=makeQuery(id+"F0.imprint","IMPRINT",FACE,{"disambiguationData":[TD([[makeQuery(id+"F0.imprint","IMPRINT",EDGE,{"derivedFrom":subQ3}),1.0]])]});}
            extrude(context, id + "F1", {"entities" : qUnion([Q0]), "oppositeDirection" : true, "depth" : 3 * mm});
        }
        {
            var Q0;
            Q0=makeQuery(id+"F1.opExtrude","SWEPT_FACE",FACE,{"disambiguationData":[OSD([sQuery(id+"F0.wireOp",EDGE,"E6")])]});
            var sketch = newSketch(context, id + "F2", { "sketchPlane" : qUnion([Q0])});
            skLineSegment(sketch, "E1323", {"start": v(423.5, 0) * mm, "end": v(650, 234.55) * mm});
            skLineSegment(sketch, "E1324", {"start": v(650, 234.55) * mm, "end": v(-650, 234.55) * mm});
            skLineSegment(sketch, "E1325", {"start": v(-650, 234.55) * mm, "end": v(-423.5, 0) * mm});
            skSolve(sketch);
        }
        {
            var Q0;
            Q0=makeQuery(id+"F2.imprint","IMPRINT",FACE,{"disambiguationData":[TD([[makeQuery(id+"F2.imprint","IMPRINT",EDGE,{"derivedFrom":sQuery(id+"F2.wireOp",EDGE,"E1323")}),1.0]])]});
            extrude(context, id + "F3", {"entities" : qUnion([Q0]), "oppositeDirection" : true, "depth" : 3 * mm});
        }
        {
            var Q0;
            Q0=makeQuery(id+"F3.opExtrude","SWEPT_FACE",FACE,{"disambiguationData":[OSD([sQuery(id+"F2.wireOp",EDGE,"E1325")])]});
            var sketch = newSketch(context, id + "F4", { "sketchPlane" : qUnion([Q0])});
            skLineSegment(sketch, "E1326", {"start": v(-294.19, 366.4) * mm, "end": v(-294.19, -383.21) * mm});
            skLineSegment(sketch, "E1327", {"start": v(-294.19, -383.21) * mm, "end": v(-620.25, -383.21) * mm});
            skLineSegment(sketch, "E1328", {"start": v(-620.25, -383.21) * mm, "end": v(-620.25, 363.4) * mm});
            skSolve(sketch);
        }
        {
            var Q0;
            Q0=makeQuery(id+"F4.imprint","IMPRINT",FACE,{"disambiguationData":[TD([[makeQuery(id+"F4.imprint","IMPRINT",EDGE,{"derivedFrom":sQuery(id+"F4.wireOp",EDGE,"E1326")}),-1.0]])]});
            extrude(context, id + "F5", {"entities" : qUnion([Q0]), "oppositeDirection" : true, "depth" : 3 * mm});
        }
        {
            var Q0;
            Q0=makeQuery(id+"F3.opExtrude","SWEPT_FACE",FACE,{"disambiguationData":[OSD([sQuery(id+"F2.wireOp",EDGE,"E1323")])]});
            var sketch = newSketch(context, id + "F6", { "sketchPlane" : qUnion([Q0])});
            skLineSegment(sketch, "E1329", {"start": v(294.19, 363.4) * mm, "end": v(294.19, -383.14) * mm});
            skLineSegment(sketch, "E1330", {"start": v(294.19, -383.14) * mm, "end": v(620.25, -383.14) * mm});
            skLineSegment(sketch, "E1331", {"start": v(620.25, -383.14) * mm, "end": v(620.25, 363.4) * mm});
            skSolve(sketch);
        }
        {
            var Q0;
            {var subQ2=sQuery(id+"F6.wireOp",EDGE,"E1330");Q0=makeQuery(id+"F6.imprint","IMPRINT",FACE,{"disambiguationData":[TD([[makeQuery(id+"F6.imprint","IMPRINT",EDGE,{"derivedFrom":subQ2}),1.0]])]});}
            extrude(context, id + "F7", {"entities" : qUnion([Q0]), "oppositeDirection" : true, "depth" : 3 * mm});
        }
        {
            var Q0;
            Q0=makeQuery(id+"F1.opExtrude","SWEPT_BODY",BODY,{"disambiguationData":[OSD([sQuery(id+"F0.wireOp",EDGE,"E2"),sQuery(id+"F0.wireOp",EDGE,"E4"),sQuery(id+"F0.wireOp",EDGE,"E5"),sQuery(id+"F0.wireOp",EDGE,"E6"),sQuery(id+"F0.wireOp",EDGE,"E7"),sQuery(id+"F0.wireOp",EDGE,"E8"),sQuery(id+"F0.wireOp",EDGE,"E9"),sQuery(id+"F0.wireOp",EDGE,"E10"),sQuery(id+"F0.wireOp",EDGE,"E11"),sQuery(id+"F0.wireOp",EDGE,"E12"),sQuery(id+"F0.wireOp",EDGE,"E13"),sQuery(id+"F0.wireOp",EDGE,"E14"),sQuery(id+"F0.wireOp",EDGE,"E15"),sQuery(id+"F0.wireOp",EDGE,"E16"),sQuery(id+"F0.wireOp",EDGE,"E17"),sQuery(id+"F0.wireOp",EDGE,"E18"),sQuery(id+"F0.wireOp",EDGE,"E19"),sQuery(id+"F0.wireOp",EDGE,"E20"),sQuery(id+"F0.wireOp",EDGE,"E21"),sQuery(id+"F0.wireOp",EDGE,"E22"),sQuery(id+"F0.wireOp",EDGE,"E23"),sQuery(id+"F0.wireOp",EDGE,"E24"),sQuery(id+"F0.wireOp",EDGE,"E25"),sQuery(id+"F0.wireOp",EDGE,"E26"),sQuery(id+"F0.wireOp",EDGE,"E27"),sQuery(id+"F0.wireOp",EDGE,"E28"),sQuery(id+"F0.wireOp",EDGE,"E29"),sQuery(id+"F0.wireOp",EDGE,"E30"),sQuery(id+"F0.wireOp",EDGE,"E31"),sQuery(id+"F0.wireOp",EDGE,"E32"),sQuery(id+"F0.wireOp",EDGE,"E33"),sQuery(id+"F0.wireOp",EDGE,"E34"),sQuery(id+"F0.wireOp",EDGE,"E35"),sQuery(id+"F0.wireOp",EDGE,"E36"),sQuery(id+"F0.wireOp",EDGE,"E37"),sQuery(id+"F0.wireOp",EDGE,"E38"),sQuery(id+"F0.wireOp",EDGE,"E39"),sQuery(id+"F0.wireOp",EDGE,"E40"),sQuery(id+"F0.wireOp",EDGE,"E41"),sQuery(id+"F0.wireOp",EDGE,"E42"),sQuery(id+"F0.wireOp",EDGE,"E43"),sQuery(id+"F0.wireOp",EDGE,"E44"),sQuery(id+"F0.wireOp",EDGE,"E45"),sQuery(id+"F0.wireOp",EDGE,"E46"),sQuery(id+"F0.wireOp",EDGE,"E47"),sQuery(id+"F0.wireOp",EDGE,"E48"),sQuery(id+"F0.wireOp",EDGE,"E49"),sQuery(id+"F0.wireOp",EDGE,"E50"),sQuery(id+"F0.wireOp",EDGE,"E51"),sQuery(id+"F0.wireOp",EDGE,"E52"),sQuery(id+"F0.wireOp",EDGE,"E53"),sQuery(id+"F0.wireOp",EDGE,"E54"),sQuery(id+"F0.wireOp",EDGE,"E55"),sQuery(id+"F0.wireOp",EDGE,"E56"),sQuery(id+"F0.wireOp",EDGE,"E57"),sQuery(id+"F0.wireOp",EDGE,"E58"),sQuery(id+"F0.wireOp",EDGE,"E59"),sQuery(id+"F0.wireOp",EDGE,"E60"),sQuery(id+"F0.wireOp",EDGE,"E61"),sQuery(id+"F0.wireOp",EDGE,"E62"),sQuery(id+"F0.wireOp",EDGE,"E63"),sQuery(id+"F0.wireOp",EDGE,"E64"),sQuery(id+"F0.wireOp",EDGE,"E65"),sQuery(id+"F0.wireOp",EDGE,"E66"),sQuery(id+"F0.wireOp",EDGE,"E67"),sQuery(id+"F0.wireOp",EDGE,"E68"),sQuery(id+"F0.wireOp",EDGE,"E69"),sQuery(id+"F0.wireOp",EDGE,"E70"),sQuery(id+"F0.wireOp",EDGE,"E71"),sQuery(id+"F0.wireOp",EDGE,"E72"),sQuery(id+"F0.wireOp",EDGE,"E73"),sQuery(id+"F0.wireOp",EDGE,"E74"),sQuery(id+"F0.wireOp",EDGE,"E75"),sQuery(id+"F0.wireOp",EDGE,"E76"),sQuery(id+"F0.wireOp",EDGE,"E77"),sQuery(id+"F0.wireOp",EDGE,"E78"),sQuery(id+"F0.wireOp",EDGE,"E79"),sQuery(id+"F0.wireOp",EDGE,"E80"),sQuery(id+"F0.wireOp",EDGE,"E81"),sQuery(id+"F0.wireOp",EDGE,"E82"),sQuery(id+"F0.wireOp",EDGE,"E83"),sQuery(id+"F0.wireOp",EDGE,"E84"),sQuery(id+"F0.wireOp",EDGE,"E85"),sQuery(id+"F0.wireOp",EDGE,"E86"),sQuery(id+"F0.wireOp",EDGE,"E87"),sQuery(id+"F0.wireOp",EDGE,"E88"),sQuery(id+"F0.wireOp",EDGE,"E89"),sQuery(id+"F0.wireOp",EDGE,"E90"),sQuery(id+"F0.wireOp",EDGE,"E91"),sQuery(id+"F0.wireOp",EDGE,"E93"),sQuery(id+"F0.wireOp",EDGE,"E94"),sQuery(id+"F0.wireOp",EDGE,"E95"),sQuery(id+"F0.wireOp",EDGE,"E96"),sQuery(id+"F0.wireOp",EDGE,"E97"),sQuery(id+"F0.wireOp",EDGE,"E98"),sQuery(id+"F0.wireOp",EDGE,"E99"),sQuery(id+"F0.wireOp",EDGE,"E100"),sQuery(id+"F0.wireOp",EDGE,"E101"),sQuery(id+"F0.wireOp",EDGE,"E102"),sQuery(id+"F0.wireOp",EDGE,"E103"),sQuery(id+"F0.wireOp",EDGE,"E104"),sQuery(id+"F0.wireOp",EDGE,"E105"),sQuery(id+"F0.wireOp",EDGE,"E106"),sQuery(id+"F0.wireOp",EDGE,"E107"),sQuery(id+"F0.wireOp",EDGE,"E108"),sQuery(id+"F0.wireOp",EDGE,"E125"),sQuery(id+"F0.wireOp",EDGE,"E126"),sQuery(id+"F0.wireOp",EDGE,"E127"),sQuery(id+"F0.wireOp",EDGE,"E128"),sQuery(id+"F0.wireOp",EDGE,"E129"),sQuery(id+"F0.wireOp",EDGE,"E130"),sQuery(id+"F0.wireOp",EDGE,"E131"),sQuery(id+"F0.wireOp",EDGE,"E132"),sQuery(id+"F0.wireOp",EDGE,"E133"),sQuery(id+"F0.wireOp",EDGE,"E134"),sQuery(id+"F0.wireOp",EDGE,"E135"),sQuery(id+"F0.wireOp",EDGE,"E136"),sQuery(id+"F0.wireOp",EDGE,"E137"),sQuery(id+"F0.wireOp",EDGE,"E138"),sQuery(id+"F0.wireOp",EDGE,"E139"),sQuery(id+"F0.wireOp",EDGE,"E140"),sQuery(id+"F0.wireOp",EDGE,"E141"),sQuery(id+"F0.wireOp",EDGE,"E142"),sQuery(id+"F0.wireOp",EDGE,"E143"),sQuery(id+"F0.wireOp",EDGE,"E144"),sQuery(id+"F0.wireOp",EDGE,"E145"),sQuery(id+"F0.wireOp",EDGE,"E146"),sQuery(id+"F0.wireOp",EDGE,"E147"),sQuery(id+"F0.wireOp",EDGE,"E148"),sQuery(id+"F0.wireOp",EDGE,"E149"),sQuery(id+"F0.wireOp",EDGE,"E150"),sQuery(id+"F0.wireOp",EDGE,"E151"),sQuery(id+"F0.wireOp",EDGE,"E152"),sQuery(id+"F0.wireOp",EDGE,"E153"),sQuery(id+"F0.wireOp",EDGE,"E154"),sQuery(id+"F0.wireOp",EDGE,"E155"),sQuery(id+"F0.wireOp",EDGE,"E156"),sQuery(id+"F0.wireOp",EDGE,"E157"),sQuery(id+"F0.wireOp",EDGE,"E158"),sQuery(id+"F0.wireOp",EDGE,"E159"),sQuery(id+"F0.wireOp",EDGE,"E160"),sQuery(id+"F0.wireOp",EDGE,"E161"),sQuery(id+"F0.wireOp",EDGE,"E162"),sQuery(id+"F0.wireOp",EDGE,"E163"),sQuery(id+"F0.wireOp",EDGE,"E164"),sQuery(id+"F0.wireOp",EDGE,"E165"),sQuery(id+"F0.wireOp",EDGE,"E166"),sQuery(id+"F0.wireOp",EDGE,"E167"),sQuery(id+"F0.wireOp",EDGE,"E168"),sQuery(id+"F0.wireOp",EDGE,"E169"),sQuery(id+"F0.wireOp",EDGE,"E170"),sQuery(id+"F0.wireOp",EDGE,"E171"),sQuery(id+"F0.wireOp",EDGE,"E172"),sQuery(id+"F0.wireOp",EDGE,"E173"),sQuery(id+"F0.wireOp",EDGE,"E174"),sQuery(id+"F0.wireOp",EDGE,"E175"),sQuery(id+"F0.wireOp",EDGE,"E176"),sQuery(id+"F0.wireOp",EDGE,"E177"),sQuery(id+"F0.wireOp",EDGE,"E178"),sQuery(id+"F0.wireOp",EDGE,"E179"),sQuery(id+"F0.wireOp",EDGE,"E180"),sQuery(id+"F0.wireOp",EDGE,"E181"),sQuery(id+"F0.wireOp",EDGE,"E182"),sQuery(id+"F0.wireOp",EDGE,"E183"),sQuery(id+"F0.wireOp",EDGE,"E184"),sQuery(id+"F0.wireOp",EDGE,"E185"),sQuery(id+"F0.wireOp",EDGE,"E186"),sQuery(id+"F0.wireOp",EDGE,"E187"),sQuery(id+"F0.wireOp",EDGE,"E188"),sQuery(id+"F0.wireOp",EDGE,"E189"),sQuery(id+"F0.wireOp",EDGE,"E190"),sQuery(id+"F0.wireOp",EDGE,"E191"),sQuery(id+"F0.wireOp",EDGE,"E192"),sQuery(id+"F0.wireOp",EDGE,"E193"),sQuery(id+"F0.wireOp",EDGE,"E194"),sQuery(id+"F0.wireOp",EDGE,"E195"),sQuery(id+"F0.wireOp",EDGE,"E196"),sQuery(id+"F0.wireOp",EDGE,"E197"),sQuery(id+"F0.wireOp",EDGE,"E198"),sQuery(id+"F0.wireOp",EDGE,"E199"),sQuery(id+"F0.wireOp",EDGE,"E200"),sQuery(id+"F0.wireOp",EDGE,"E201"),sQuery(id+"F0.wireOp",EDGE,"E202"),sQuery(id+"F0.wireOp",EDGE,"E203"),sQuery(id+"F0.wireOp",EDGE,"E204"),sQuery(id+"F0.wireOp",EDGE,"E205"),sQuery(id+"F0.wireOp",EDGE,"E206"),sQuery(id+"F0.wireOp",EDGE,"E207"),sQuery(id+"F0.wireOp",EDGE,"E208"),sQuery(id+"F0.wireOp",EDGE,"E209"),sQuery(id+"F0.wireOp",EDGE,"E210"),sQuery(id+"F0.wireOp",EDGE,"E211"),sQuery(id+"F0.wireOp",EDGE,"E212"),sQuery(id+"F0.wireOp",EDGE,"E213"),sQuery(id+"F0.wireOp",EDGE,"E214"),sQuery(id+"F0.wireOp",EDGE,"E215"),sQuery(id+"F0.wireOp",EDGE,"E216"),sQuery(id+"F0.wireOp",EDGE,"E217"),sQuery(id+"F0.wireOp",EDGE,"E218"),sQuery(id+"F0.wireOp",EDGE,"E219"),sQuery(id+"F0.wireOp",EDGE,"E220"),sQuery(id+"F0.wireOp",EDGE,"E221"),sQuery(id+"F0.wireOp",EDGE,"E222"),sQuery(id+"F0.wireOp",EDGE,"E223"),sQuery(id+"F0.wireOp",EDGE,"E224"),sQuery(id+"F0.wireOp",EDGE,"E225"),sQuery(id+"F0.wireOp",EDGE,"E226"),sQuery(id+"F0.wireOp",EDGE,"E227"),sQuery(id+"F0.wireOp",EDGE,"E228"),sQuery(id+"F0.wireOp",EDGE,"E229"),sQuery(id+"F0.wireOp",EDGE,"E230"),sQuery(id+"F0.wireOp",EDGE,"E231"),sQuery(id+"F0.wireOp",EDGE,"E232"),sQuery(id+"F0.wireOp",EDGE,"E233"),sQuery(id+"F0.wireOp",EDGE,"E234"),sQuery(id+"F0.wireOp",EDGE,"E235"),sQuery(id+"F0.wireOp",EDGE,"E236"),sQuery(id+"F0.wireOp",EDGE,"E237"),sQuery(id+"F0.wireOp",EDGE,"E238"),sQuery(id+"F0.wireOp",EDGE,"E239"),sQuery(id+"F0.wireOp",EDGE,"E240"),sQuery(id+"F0.wireOp",EDGE,"E241"),sQuery(id+"F0.wireOp",EDGE,"E242"),sQuery(id+"F0.wireOp",EDGE,"E243"),sQuery(id+"F0.wireOp",EDGE,"E244"),sQuery(id+"F0.wireOp",EDGE,"E245"),sQuery(id+"F0.wireOp",EDGE,"E246"),sQuery(id+"F0.wireOp",EDGE,"E247"),sQuery(id+"F0.wireOp",EDGE,"E248"),sQuery(id+"F0.wireOp",EDGE,"E249"),sQuery(id+"F0.wireOp",EDGE,"E250"),sQuery(id+"F0.wireOp",EDGE,"E251"),sQuery(id+"F0.wireOp",EDGE,"E252"),sQuery(id+"F0.wireOp",EDGE,"E253"),sQuery(id+"F0.wireOp",EDGE,"E254"),sQuery(id+"F0.wireOp",EDGE,"E255"),sQuery(id+"F0.wireOp",EDGE,"E256"),sQuery(id+"F0.wireOp",EDGE,"E257"),sQuery(id+"F0.wireOp",EDGE,"E258"),sQuery(id+"F0.wireOp",EDGE,"E259"),sQuery(id+"F0.wireOp",EDGE,"E260"),sQuery(id+"F0.wireOp",EDGE,"E261"),sQuery(id+"F0.wireOp",EDGE,"E262"),sQuery(id+"F0.wireOp",EDGE,"E263"),sQuery(id+"F0.wireOp",EDGE,"E264"),sQuery(id+"F0.wireOp",EDGE,"E265"),sQuery(id+"F0.wireOp",EDGE,"E266"),sQuery(id+"F0.wireOp",EDGE,"E267"),sQuery(id+"F0.wireOp",EDGE,"E268"),sQuery(id+"F0.wireOp",EDGE,"E269"),sQuery(id+"F0.wireOp",EDGE,"E270"),sQuery(id+"F0.wireOp",EDGE,"E271"),sQuery(id+"F0.wireOp",EDGE,"E272"),sQuery(id+"F0.wireOp",EDGE,"E273"),sQuery(id+"F0.wireOp",EDGE,"E274"),sQuery(id+"F0.wireOp",EDGE,"E275"),sQuery(id+"F0.wireOp",EDGE,"E276"),sQuery(id+"F0.wireOp",EDGE,"E277"),sQuery(id+"F0.wireOp",EDGE,"E278"),sQuery(id+"F0.wireOp",EDGE,"E279"),sQuery(id+"F0.wireOp",EDGE,"E280"),sQuery(id+"F0.wireOp",EDGE,"E281"),sQuery(id+"F0.wireOp",EDGE,"E282"),sQuery(id+"F0.wireOp",EDGE,"E283"),sQuery(id+"F0.wireOp",EDGE,"E284"),sQuery(id+"F0.wireOp",EDGE,"E285"),sQuery(id+"F0.wireOp",EDGE,"E92"),sQuery(id+"F0.wireOp",EDGE,"E286"),sQuery(id+"F0.wireOp",EDGE,"E287"),sQuery(id+"F0.wireOp",EDGE,"E288"),sQuery(id+"F0.wireOp",EDGE,"E289"),sQuery(id+"F0.wireOp",EDGE,"E290"),sQuery(id+"F0.wireOp",EDGE,"E291"),sQuery(id+"F0.wireOp",EDGE,"E292"),sQuery(id+"F0.wireOp",EDGE,"E293"),sQuery(id+"F0.wireOp",EDGE,"E294"),sQuery(id+"F0.wireOp",EDGE,"E295"),sQuery(id+"F0.wireOp",EDGE,"E296"),sQuery(id+"F0.wireOp",EDGE,"E297"),sQuery(id+"F0.wireOp",EDGE,"E298"),sQuery(id+"F0.wireOp",EDGE,"E299"),sQuery(id+"F0.wireOp",EDGE,"E300"),sQuery(id+"F0.wireOp",EDGE,"E301"),sQuery(id+"F0.wireOp",EDGE,"E302"),sQuery(id+"F0.wireOp",EDGE,"E303"),sQuery(id+"F0.wireOp",EDGE,"E304"),sQuery(id+"F0.wireOp",EDGE,"E305"),sQuery(id+"F0.wireOp",EDGE,"E306"),sQuery(id+"F0.wireOp",EDGE,"E307"),sQuery(id+"F0.wireOp",EDGE,"E308"),sQuery(id+"F0.wireOp",EDGE,"E309"),sQuery(id+"F0.wireOp",EDGE,"E310"),sQuery(id+"F0.wireOp",EDGE,"E311"),sQuery(id+"F0.wireOp",EDGE,"E312"),sQuery(id+"F0.wireOp",EDGE,"E313"),sQuery(id+"F0.wireOp",EDGE,"E314"),sQuery(id+"F0.wireOp",EDGE,"E315"),sQuery(id+"F0.wireOp",EDGE,"E316"),sQuery(id+"F0.wireOp",EDGE,"E317"),sQuery(id+"F0.wireOp",EDGE,"E318"),sQuery(id+"F0.wireOp",EDGE,"E319"),sQuery(id+"F0.wireOp",EDGE,"E320"),sQuery(id+"F0.wireOp",EDGE,"E321"),sQuery(id+"F0.wireOp",EDGE,"E322"),sQuery(id+"F0.wireOp",EDGE,"E323"),sQuery(id+"F0.wireOp",EDGE,"E324"),sQuery(id+"F0.wireOp",EDGE,"E325"),sQuery(id+"F0.wireOp",EDGE,"E326"),sQuery(id+"F0.wireOp",EDGE,"E327"),sQuery(id+"F0.wireOp",EDGE,"E328"),sQuery(id+"F0.wireOp",EDGE,"E329"),sQuery(id+"F0.wireOp",EDGE,"E330"),sQuery(id+"F0.wireOp",EDGE,"E331"),sQuery(id+"F0.wireOp",EDGE,"E332"),sQuery(id+"F0.wireOp",EDGE,"E333"),sQuery(id+"F0.wireOp",EDGE,"E334"),sQuery(id+"F0.wireOp",EDGE,"E335"),sQuery(id+"F0.wireOp",EDGE,"E336"),sQuery(id+"F0.wireOp",EDGE,"E337"),sQuery(id+"F0.wireOp",EDGE,"E338"),sQuery(id+"F0.wireOp",EDGE,"E339"),sQuery(id+"F0.wireOp",EDGE,"E340"),sQuery(id+"F0.wireOp",EDGE,"E341"),sQuery(id+"F0.wireOp",EDGE,"E342"),sQuery(id+"F0.wireOp",EDGE,"E343"),sQuery(id+"F0.wireOp",EDGE,"E344"),sQuery(id+"F0.wireOp",EDGE,"E345"),sQuery(id+"F0.wireOp",EDGE,"E346"),sQuery(id+"F0.wireOp",EDGE,"E347"),sQuery(id+"F0.wireOp",EDGE,"E348"),sQuery(id+"F0.wireOp",EDGE,"E349"),sQuery(id+"F0.wireOp",EDGE,"E350"),sQuery(id+"F0.wireOp",EDGE,"E351"),sQuery(id+"F0.wireOp",EDGE,"E352"),sQuery(id+"F0.wireOp",EDGE,"E353"),sQuery(id+"F0.wireOp",EDGE,"E354"),sQuery(id+"F0.wireOp",EDGE,"E355"),sQuery(id+"F0.wireOp",EDGE,"E356"),sQuery(id+"F0.wireOp",EDGE,"E357"),sQuery(id+"F0.wireOp",EDGE,"E358"),sQuery(id+"F0.wireOp",EDGE,"E359"),sQuery(id+"F0.wireOp",EDGE,"E360"),sQuery(id+"F0.wireOp",EDGE,"E361"),sQuery(id+"F0.wireOp",EDGE,"E362"),sQuery(id+"F0.wireOp",EDGE,"E363"),sQuery(id+"F0.wireOp",EDGE,"E364"),sQuery(id+"F0.wireOp",EDGE,"E365"),sQuery(id+"F0.wireOp",EDGE,"E366"),sQuery(id+"F0.wireOp",EDGE,"E367"),sQuery(id+"F0.wireOp",EDGE,"E368"),sQuery(id+"F0.wireOp",EDGE,"E369"),sQuery(id+"F0.wireOp",EDGE,"E370"),sQuery(id+"F0.wireOp",EDGE,"E371"),sQuery(id+"F0.wireOp",EDGE,"E372"),sQuery(id+"F0.wireOp",EDGE,"E373"),sQuery(id+"F0.wireOp",EDGE,"E374"),sQuery(id+"F0.wireOp",EDGE,"E375"),sQuery(id+"F0.wireOp",EDGE,"E376"),sQuery(id+"F0.wireOp",EDGE,"E377"),sQuery(id+"F0.wireOp",EDGE,"E378"),sQuery(id+"F0.wireOp",EDGE,"E379"),sQuery(id+"F0.wireOp",EDGE,"E380"),sQuery(id+"F0.wireOp",EDGE,"E381"),sQuery(id+"F0.wireOp",EDGE,"E382"),sQuery(id+"F0.wireOp",EDGE,"E383"),sQuery(id+"F0.wireOp",EDGE,"E384"),sQuery(id+"F0.wireOp",EDGE,"E385"),sQuery(id+"F0.wireOp",EDGE,"E386"),sQuery(id+"F0.wireOp",EDGE,"E387"),sQuery(id+"F0.wireOp",EDGE,"E388"),sQuery(id+"F0.wireOp",EDGE,"E389"),sQuery(id+"F0.wireOp",EDGE,"E390"),sQuery(id+"F0.wireOp",EDGE,"E391"),sQuery(id+"F0.wireOp",EDGE,"E392"),sQuery(id+"F0.wireOp",EDGE,"E393"),sQuery(id+"F0.wireOp",EDGE,"E394"),sQuery(id+"F0.wireOp",EDGE,"E395"),sQuery(id+"F0.wireOp",EDGE,"E396"),sQuery(id+"F0.wireOp",EDGE,"E397"),sQuery(id+"F0.wireOp",EDGE,"E398"),sQuery(id+"F0.wireOp",EDGE,"E399"),sQuery(id+"F0.wireOp",EDGE,"E400"),sQuery(id+"F0.wireOp",EDGE,"E401"),sQuery(id+"F0.wireOp",EDGE,"E402"),sQuery(id+"F0.wireOp",EDGE,"E403"),sQuery(id+"F0.wireOp",EDGE,"E404"),sQuery(id+"F0.wireOp",EDGE,"E405"),sQuery(id+"F0.wireOp",EDGE,"E406"),sQuery(id+"F0.wireOp",EDGE,"E407"),sQuery(id+"F0.wireOp",EDGE,"E408"),sQuery(id+"F0.wireOp",EDGE,"E409"),sQuery(id+"F0.wireOp",EDGE,"E410"),sQuery(id+"F0.wireOp",EDGE,"E411"),sQuery(id+"F0.wireOp",EDGE,"E412"),sQuery(id+"F0.wireOp",EDGE,"E413"),sQuery(id+"F0.wireOp",EDGE,"E414"),sQuery(id+"F0.wireOp",EDGE,"E415"),sQuery(id+"F0.wireOp",EDGE,"E416"),sQuery(id+"F0.wireOp",EDGE,"E417"),sQuery(id+"F0.wireOp",EDGE,"E418"),sQuery(id+"F0.wireOp",EDGE,"E419"),sQuery(id+"F0.wireOp",EDGE,"E420"),sQuery(id+"F0.wireOp",EDGE,"E421"),sQuery(id+"F0.wireOp",EDGE,"E422"),sQuery(id+"F0.wireOp",EDGE,"E423"),sQuery(id+"F0.wireOp",EDGE,"E424"),sQuery(id+"F0.wireOp",EDGE,"E425"),sQuery(id+"F0.wireOp",EDGE,"E426"),sQuery(id+"F0.wireOp",EDGE,"E427"),sQuery(id+"F0.wireOp",EDGE,"E428"),sQuery(id+"F0.wireOp",EDGE,"E429"),sQuery(id+"F0.wireOp",EDGE,"E430"),sQuery(id+"F0.wireOp",EDGE,"E431"),sQuery(id+"F0.wireOp",EDGE,"E432"),sQuery(id+"F0.wireOp",EDGE,"E433"),sQuery(id+"F0.wireOp",EDGE,"E434"),sQuery(id+"F0.wireOp",EDGE,"E435"),sQuery(id+"F0.wireOp",EDGE,"E436"),sQuery(id+"F0.wireOp",EDGE,"E437"),sQuery(id+"F0.wireOp",EDGE,"E438"),sQuery(id+"F0.wireOp",EDGE,"E439"),sQuery(id+"F0.wireOp",EDGE,"E440"),sQuery(id+"F0.wireOp",EDGE,"E441"),sQuery(id+"F0.wireOp",EDGE,"E442"),sQuery(id+"F0.wireOp",EDGE,"E443"),sQuery(id+"F0.wireOp",EDGE,"E444"),sQuery(id+"F0.wireOp",EDGE,"E445"),sQuery(id+"F0.wireOp",EDGE,"E446"),sQuery(id+"F0.wireOp",EDGE,"E447"),sQuery(id+"F0.wireOp",EDGE,"E448"),sQuery(id+"F0.wireOp",EDGE,"E449"),sQuery(id+"F0.wireOp",EDGE,"E450"),sQuery(id+"F0.wireOp",EDGE,"E451"),sQuery(id+"F0.wireOp",EDGE,"E452"),sQuery(id+"F0.wireOp",EDGE,"E453"),sQuery(id+"F0.wireOp",EDGE,"E454"),sQuery(id+"F0.wireOp",EDGE,"E455"),sQuery(id+"F0.wireOp",EDGE,"E456"),sQuery(id+"F0.wireOp",EDGE,"E457"),sQuery(id+"F0.wireOp",EDGE,"E458"),sQuery(id+"F0.wireOp",EDGE,"E459"),sQuery(id+"F0.wireOp",EDGE,"E460"),sQuery(id+"F0.wireOp",EDGE,"E461"),sQuery(id+"F0.wireOp",EDGE,"E462"),sQuery(id+"F0.wireOp",EDGE,"E463"),sQuery(id+"F0.wireOp",EDGE,"E464"),sQuery(id+"F0.wireOp",EDGE,"E465"),sQuery(id+"F0.wireOp",EDGE,"E466"),sQuery(id+"F0.wireOp",EDGE,"E467"),sQuery(id+"F0.wireOp",EDGE,"E468"),sQuery(id+"F0.wireOp",EDGE,"E469"),sQuery(id+"F0.wireOp",EDGE,"E470"),sQuery(id+"F0.wireOp",EDGE,"E471"),sQuery(id+"F0.wireOp",EDGE,"E472"),sQuery(id+"F0.wireOp",EDGE,"E473"),sQuery(id+"F0.wireOp",EDGE,"E474"),sQuery(id+"F0.wireOp",EDGE,"E475"),sQuery(id+"F0.wireOp",EDGE,"E476"),sQuery(id+"F0.wireOp",EDGE,"E477"),sQuery(id+"F0.wireOp",EDGE,"E478"),sQuery(id+"F0.wireOp",EDGE,"E479"),sQuery(id+"F0.wireOp",EDGE,"E480"),sQuery(id+"F0.wireOp",EDGE,"E481"),sQuery(id+"F0.wireOp",EDGE,"E482"),sQuery(id+"F0.wireOp",EDGE,"E483"),sQuery(id+"F0.wireOp",EDGE,"E484"),sQuery(id+"F0.wireOp",EDGE,"E485"),sQuery(id+"F0.wireOp",EDGE,"E486"),sQuery(id+"F0.wireOp",EDGE,"E487"),sQuery(id+"F0.wireOp",EDGE,"E488"),sQuery(id+"F0.wireOp",EDGE,"E489"),sQuery(id+"F0.wireOp",EDGE,"E490"),sQuery(id+"F0.wireOp",EDGE,"E491"),sQuery(id+"F0.wireOp",EDGE,"E492"),sQuery(id+"F0.wireOp",EDGE,"E493"),sQuery(id+"F0.wireOp",EDGE,"E494"),sQuery(id+"F0.wireOp",EDGE,"E495"),sQuery(id+"F0.wireOp",EDGE,"E496"),sQuery(id+"F0.wireOp",EDGE,"E497"),sQuery(id+"F0.wireOp",EDGE,"E498"),sQuery(id+"F0.wireOp",EDGE,"E499"),sQuery(id+"F0.wireOp",EDGE,"E500"),sQuery(id+"F0.wireOp",EDGE,"E501"),sQuery(id+"F0.wireOp",EDGE,"E502"),sQuery(id+"F0.wireOp",EDGE,"E503"),sQuery(id+"F0.wireOp",EDGE,"E504"),sQuery(id+"F0.wireOp",EDGE,"E505"),sQuery(id+"F0.wireOp",EDGE,"E506"),sQuery(id+"F0.wireOp",EDGE,"E507"),sQuery(id+"F0.wireOp",EDGE,"E508"),sQuery(id+"F0.wireOp",EDGE,"E509"),sQuery(id+"F0.wireOp",EDGE,"E510"),sQuery(id+"F0.wireOp",EDGE,"E511"),sQuery(id+"F0.wireOp",EDGE,"E512"),sQuery(id+"F0.wireOp",EDGE,"E513"),sQuery(id+"F0.wireOp",EDGE,"E514"),sQuery(id+"F0.wireOp",EDGE,"E515"),sQuery(id+"F0.wireOp",EDGE,"E516"),sQuery(id+"F0.wireOp",EDGE,"E517"),sQuery(id+"F0.wireOp",EDGE,"E518"),sQuery(id+"F0.wireOp",EDGE,"E519"),sQuery(id+"F0.wireOp",EDGE,"E520"),sQuery(id+"F0.wireOp",EDGE,"E521"),sQuery(id+"F0.wireOp",EDGE,"E522"),sQuery(id+"F0.wireOp",EDGE,"E523"),sQuery(id+"F0.wireOp",EDGE,"E524"),sQuery(id+"F0.wireOp",EDGE,"E525"),sQuery(id+"F0.wireOp",EDGE,"E526"),sQuery(id+"F0.wireOp",EDGE,"E527"),sQuery(id+"F0.wireOp",EDGE,"E528"),sQuery(id+"F0.wireOp",EDGE,"E529"),sQuery(id+"F0.wireOp",EDGE,"E530"),sQuery(id+"F0.wireOp",EDGE,"E531"),sQuery(id+"F0.wireOp",EDGE,"E532"),sQuery(id+"F0.wireOp",EDGE,"E533"),sQuery(id+"F0.wireOp",EDGE,"E534"),sQuery(id+"F0.wireOp",EDGE,"E535"),sQuery(id+"F0.wireOp",EDGE,"E536"),sQuery(id+"F0.wireOp",EDGE,"E537"),sQuery(id+"F0.wireOp",EDGE,"E538"),sQuery(id+"F0.wireOp",EDGE,"E539"),sQuery(id+"F0.wireOp",EDGE,"E540"),sQuery(id+"F0.wireOp",EDGE,"E541"),sQuery(id+"F0.wireOp",EDGE,"E542"),sQuery(id+"F0.wireOp",EDGE,"E543"),sQuery(id+"F0.wireOp",EDGE,"E544"),sQuery(id+"F0.wireOp",EDGE,"E545"),sQuery(id+"F0.wireOp",EDGE,"E546"),sQuery(id+"F0.wireOp",EDGE,"E547"),sQuery(id+"F0.wireOp",EDGE,"E548"),sQuery(id+"F0.wireOp",EDGE,"E549"),sQuery(id+"F0.wireOp",EDGE,"E550"),sQuery(id+"F0.wireOp",EDGE,"E551"),sQuery(id+"F0.wireOp",EDGE,"E552"),sQuery(id+"F0.wireOp",EDGE,"E553"),sQuery(id+"F0.wireOp",EDGE,"E554"),sQuery(id+"F0.wireOp",EDGE,"E555"),sQuery(id+"F0.wireOp",EDGE,"E556"),sQuery(id+"F0.wireOp",EDGE,"E557"),sQuery(id+"F0.wireOp",EDGE,"E558"),sQuery(id+"F0.wireOp",EDGE,"E559"),sQuery(id+"F0.wireOp",EDGE,"E560"),sQuery(id+"F0.wireOp",EDGE,"E561"),sQuery(id+"F0.wireOp",EDGE,"E562"),sQuery(id+"F0.wireOp",EDGE,"E563"),sQuery(id+"F0.wireOp",EDGE,"E564"),sQuery(id+"F0.wireOp",EDGE,"E565"),sQuery(id+"F0.wireOp",EDGE,"E566"),sQuery(id+"F0.wireOp",EDGE,"E567"),sQuery(id+"F0.wireOp",EDGE,"E568"),sQuery(id+"F0.wireOp",EDGE,"E569"),sQuery(id+"F0.wireOp",EDGE,"E570"),sQuery(id+"F0.wireOp",EDGE,"E571"),sQuery(id+"F0.wireOp",EDGE,"E572"),sQuery(id+"F0.wireOp",EDGE,"E573"),sQuery(id+"F0.wireOp",EDGE,"E574"),sQuery(id+"F0.wireOp",EDGE,"E575"),sQuery(id+"F0.wireOp",EDGE,"E576"),sQuery(id+"F0.wireOp",EDGE,"E577"),sQuery(id+"F0.wireOp",EDGE,"E578"),sQuery(id+"F0.wireOp",EDGE,"E579"),sQuery(id+"F0.wireOp",EDGE,"E580"),sQuery(id+"F0.wireOp",EDGE,"E581"),sQuery(id+"F0.wireOp",EDGE,"E582"),sQuery(id+"F0.wireOp",EDGE,"E583"),sQuery(id+"F0.wireOp",EDGE,"E584"),sQuery(id+"F0.wireOp",EDGE,"E585"),sQuery(id+"F0.wireOp",EDGE,"E586"),sQuery(id+"F0.wireOp",EDGE,"E587"),sQuery(id+"F0.wireOp",EDGE,"E588"),sQuery(id+"F0.wireOp",EDGE,"E589"),sQuery(id+"F0.wireOp",EDGE,"E590"),sQuery(id+"F0.wireOp",EDGE,"E591"),sQuery(id+"F0.wireOp",EDGE,"E592"),sQuery(id+"F0.wireOp",EDGE,"E593"),sQuery(id+"F0.wireOp",EDGE,"E594"),sQuery(id+"F0.wireOp",EDGE,"E595"),sQuery(id+"F0.wireOp",EDGE,"E596"),sQuery(id+"F0.wireOp",EDGE,"E597"),sQuery(id+"F0.wireOp",EDGE,"E598"),sQuery(id+"F0.wireOp",EDGE,"E599"),sQuery(id+"F0.wireOp",EDGE,"E600"),sQuery(id+"F0.wireOp",EDGE,"E601"),sQuery(id+"F0.wireOp",EDGE,"E602"),sQuery(id+"F0.wireOp",EDGE,"E603"),sQuery(id+"F0.wireOp",EDGE,"E604"),sQuery(id+"F0.wireOp",EDGE,"E605"),sQuery(id+"F0.wireOp",EDGE,"E606"),sQuery(id+"F0.wireOp",EDGE,"E607"),sQuery(id+"F0.wireOp",EDGE,"E608"),sQuery(id+"F0.wireOp",EDGE,"E609"),sQuery(id+"F0.wireOp",EDGE,"E610"),sQuery(id+"F0.wireOp",EDGE,"E611"),sQuery(id+"F0.wireOp",EDGE,"E612"),sQuery(id+"F0.wireOp",EDGE,"E613"),sQuery(id+"F0.wireOp",EDGE,"E614"),sQuery(id+"F0.wireOp",EDGE,"E615"),sQuery(id+"F0.wireOp",EDGE,"E616"),sQuery(id+"F0.wireOp",EDGE,"E617"),sQuery(id+"F0.wireOp",EDGE,"E618"),sQuery(id+"F0.wireOp",EDGE,"E619"),sQuery(id+"F0.wireOp",EDGE,"E620"),sQuery(id+"F0.wireOp",EDGE,"E621"),sQuery(id+"F0.wireOp",EDGE,"E622"),sQuery(id+"F0.wireOp",EDGE,"E623"),sQuery(id+"F0.wireOp",EDGE,"E624"),sQuery(id+"F0.wireOp",EDGE,"E625"),sQuery(id+"F0.wireOp",EDGE,"E626"),sQuery(id+"F0.wireOp",EDGE,"E627"),sQuery(id+"F0.wireOp",EDGE,"E628"),sQuery(id+"F0.wireOp",EDGE,"E629"),sQuery(id+"F0.wireOp",EDGE,"E630"),sQuery(id+"F0.wireOp",EDGE,"E631"),sQuery(id+"F0.wireOp",EDGE,"E632"),sQuery(id+"F0.wireOp",EDGE,"E633"),sQuery(id+"F0.wireOp",EDGE,"E634"),sQuery(id+"F0.wireOp",EDGE,"E635"),sQuery(id+"F0.wireOp",EDGE,"E636"),sQuery(id+"F0.wireOp",EDGE,"E637"),sQuery(id+"F0.wireOp",EDGE,"E638"),sQuery(id+"F0.wireOp",EDGE,"E639"),sQuery(id+"F0.wireOp",EDGE,"E640"),sQuery(id+"F0.wireOp",EDGE,"E641"),sQuery(id+"F0.wireOp",EDGE,"E642"),sQuery(id+"F0.wireOp",EDGE,"E643"),sQuery(id+"F0.wireOp",EDGE,"E644"),sQuery(id+"F0.wireOp",EDGE,"E645"),sQuery(id+"F0.wireOp",EDGE,"E646"),sQuery(id+"F0.wireOp",EDGE,"E647"),sQuery(id+"F0.wireOp",EDGE,"E648"),sQuery(id+"F0.wireOp",EDGE,"E649"),sQuery(id+"F0.wireOp",EDGE,"E650"),sQuery(id+"F0.wireOp",EDGE,"E651"),sQuery(id+"F0.wireOp",EDGE,"E652"),sQuery(id+"F0.wireOp",EDGE,"E653"),sQuery(id+"F0.wireOp",EDGE,"E654"),sQuery(id+"F0.wireOp",EDGE,"E655"),sQuery(id+"F0.wireOp",EDGE,"E656"),sQuery(id+"F0.wireOp",EDGE,"E657"),sQuery(id+"F0.wireOp",EDGE,"E658"),sQuery(id+"F0.wireOp",EDGE,"E659"),sQuery(id+"F0.wireOp",EDGE,"E660"),sQuery(id+"F0.wireOp",EDGE,"E661"),sQuery(id+"F0.wireOp",EDGE,"E662"),sQuery(id+"F0.wireOp",EDGE,"E663"),sQuery(id+"F0.wireOp",EDGE,"E664"),sQuery(id+"F0.wireOp",EDGE,"E665"),sQuery(id+"F0.wireOp",EDGE,"E666"),sQuery(id+"F0.wireOp",EDGE,"E667"),sQuery(id+"F0.wireOp",EDGE,"E668"),sQuery(id+"F0.wireOp",EDGE,"E669"),sQuery(id+"F0.wireOp",EDGE,"E670"),sQuery(id+"F0.wireOp",EDGE,"E671"),sQuery(id+"F0.wireOp",EDGE,"E672"),sQuery(id+"F0.wireOp",EDGE,"E673"),sQuery(id+"F0.wireOp",EDGE,"E674"),sQuery(id+"F0.wireOp",EDGE,"E675"),sQuery(id+"F0.wireOp",EDGE,"E676"),sQuery(id+"F0.wireOp",EDGE,"E677"),sQuery(id+"F0.wireOp",EDGE,"E678"),sQuery(id+"F0.wireOp",EDGE,"E679"),sQuery(id+"F0.wireOp",EDGE,"E680"),sQuery(id+"F0.wireOp",EDGE,"E681"),sQuery(id+"F0.wireOp",EDGE,"E682"),sQuery(id+"F0.wireOp",EDGE,"E683"),sQuery(id+"F0.wireOp",EDGE,"E684"),sQuery(id+"F0.wireOp",EDGE,"E685"),sQuery(id+"F0.wireOp",EDGE,"E686"),sQuery(id+"F0.wireOp",EDGE,"E687"),sQuery(id+"F0.wireOp",EDGE,"E688"),sQuery(id+"F0.wireOp",EDGE,"E689"),sQuery(id+"F0.wireOp",EDGE,"E690"),sQuery(id+"F0.wireOp",EDGE,"E691"),sQuery(id+"F0.wireOp",EDGE,"E692"),sQuery(id+"F0.wireOp",EDGE,"E693"),sQuery(id+"F0.wireOp",EDGE,"E694"),sQuery(id+"F0.wireOp",EDGE,"E695"),sQuery(id+"F0.wireOp",EDGE,"E696"),sQuery(id+"F0.wireOp",EDGE,"E697"),sQuery(id+"F0.wireOp",EDGE,"E698"),sQuery(id+"F0.wireOp",EDGE,"E699"),sQuery(id+"F0.wireOp",EDGE,"E700"),sQuery(id+"F0.wireOp",EDGE,"E701"),sQuery(id+"F0.wireOp",EDGE,"E702"),sQuery(id+"F0.wireOp",EDGE,"E703"),sQuery(id+"F0.wireOp",EDGE,"E704"),sQuery(id+"F0.wireOp",EDGE,"E705"),sQuery(id+"F0.wireOp",EDGE,"E706"),sQuery(id+"F0.wireOp",EDGE,"E707"),sQuery(id+"F0.wireOp",EDGE,"E708"),sQuery(id+"F0.wireOp",EDGE,"E709"),sQuery(id+"F0.wireOp",EDGE,"E710"),sQuery(id+"F0.wireOp",EDGE,"E711"),sQuery(id+"F0.wireOp",EDGE,"E712"),sQuery(id+"F0.wireOp",EDGE,"E713"),sQuery(id+"F0.wireOp",EDGE,"E714"),sQuery(id+"F0.wireOp",EDGE,"E715"),sQuery(id+"F0.wireOp",EDGE,"E716"),sQuery(id+"F0.wireOp",EDGE,"E717"),sQuery(id+"F0.wireOp",EDGE,"E718"),sQuery(id+"F0.wireOp",EDGE,"E719"),sQuery(id+"F0.wireOp",EDGE,"E720"),sQuery(id+"F0.wireOp",EDGE,"E721"),sQuery(id+"F0.wireOp",EDGE,"E722"),sQuery(id+"F0.wireOp",EDGE,"E723"),sQuery(id+"F0.wireOp",EDGE,"E724"),sQuery(id+"F0.wireOp",EDGE,"E725"),sQuery(id+"F0.wireOp",EDGE,"E726"),sQuery(id+"F0.wireOp",EDGE,"E727"),sQuery(id+"F0.wireOp",EDGE,"E728"),sQuery(id+"F0.wireOp",EDGE,"E729"),sQuery(id+"F0.wireOp",EDGE,"E730"),sQuery(id+"F0.wireOp",EDGE,"E731"),sQuery(id+"F0.wireOp",EDGE,"E732"),sQuery(id+"F0.wireOp",EDGE,"E733"),sQuery(id+"F0.wireOp",EDGE,"E734"),sQuery(id+"F0.wireOp",EDGE,"E735"),sQuery(id+"F0.wireOp",EDGE,"E736"),sQuery(id+"F0.wireOp",EDGE,"E737"),sQuery(id+"F0.wireOp",EDGE,"E738"),sQuery(id+"F0.wireOp",EDGE,"E739"),sQuery(id+"F0.wireOp",EDGE,"E740"),sQuery(id+"F0.wireOp",EDGE,"E741"),sQuery(id+"F0.wireOp",EDGE,"E742"),sQuery(id+"F0.wireOp",EDGE,"E743"),sQuery(id+"F0.wireOp",EDGE,"E744"),sQuery(id+"F0.wireOp",EDGE,"E745"),sQuery(id+"F0.wireOp",EDGE,"E746"),sQuery(id+"F0.wireOp",EDGE,"E747"),sQuery(id+"F0.wireOp",EDGE,"E748"),sQuery(id+"F0.wireOp",EDGE,"E749"),sQuery(id+"F0.wireOp",EDGE,"E750"),sQuery(id+"F0.wireOp",EDGE,"E751"),sQuery(id+"F0.wireOp",EDGE,"E752"),sQuery(id+"F0.wireOp",EDGE,"E753"),sQuery(id+"F0.wireOp",EDGE,"E754"),sQuery(id+"F0.wireOp",EDGE,"E755"),sQuery(id+"F0.wireOp",EDGE,"E756"),sQuery(id+"F0.wireOp",EDGE,"E757"),sQuery(id+"F0.wireOp",EDGE,"E758"),sQuery(id+"F0.wireOp",EDGE,"E759"),sQuery(id+"F0.wireOp",EDGE,"E760"),sQuery(id+"F0.wireOp",EDGE,"E761"),sQuery(id+"F0.wireOp",EDGE,"E762"),sQuery(id+"F0.wireOp",EDGE,"E763"),sQuery(id+"F0.wireOp",EDGE,"E764"),sQuery(id+"F0.wireOp",EDGE,"E765"),sQuery(id+"F0.wireOp",EDGE,"E766"),sQuery(id+"F0.wireOp",EDGE,"E767"),sQuery(id+"F0.wireOp",EDGE,"E768"),sQuery(id+"F0.wireOp",EDGE,"E769"),sQuery(id+"F0.wireOp",EDGE,"E770"),sQuery(id+"F0.wireOp",EDGE,"E771"),sQuery(id+"F0.wireOp",EDGE,"E772"),sQuery(id+"F0.wireOp",EDGE,"E773"),sQuery(id+"F0.wireOp",EDGE,"E774"),sQuery(id+"F0.wireOp",EDGE,"E775"),sQuery(id+"F0.wireOp",EDGE,"E776"),sQuery(id+"F0.wireOp",EDGE,"E777"),sQuery(id+"F0.wireOp",EDGE,"E778"),sQuery(id+"F0.wireOp",EDGE,"E779"),sQuery(id+"F0.wireOp",EDGE,"E780"),sQuery(id+"F0.wireOp",EDGE,"E781"),sQuery(id+"F0.wireOp",EDGE,"E782"),sQuery(id+"F0.wireOp",EDGE,"E783"),sQuery(id+"F0.wireOp",EDGE,"E784"),sQuery(id+"F0.wireOp",EDGE,"E785"),sQuery(id+"F0.wireOp",EDGE,"E786"),sQuery(id+"F0.wireOp",EDGE,"E787"),sQuery(id+"F0.wireOp",EDGE,"E788"),sQuery(id+"F0.wireOp",EDGE,"E789"),sQuery(id+"F0.wireOp",EDGE,"E790"),sQuery(id+"F0.wireOp",EDGE,"E791"),sQuery(id+"F0.wireOp",EDGE,"E792"),sQuery(id+"F0.wireOp",EDGE,"E793"),sQuery(id+"F0.wireOp",EDGE,"E794"),sQuery(id+"F0.wireOp",EDGE,"E795"),sQuery(id+"F0.wireOp",EDGE,"E796"),sQuery(id+"F0.wireOp",EDGE,"E797"),sQuery(id+"F0.wireOp",EDGE,"E798"),sQuery(id+"F0.wireOp",EDGE,"E799"),sQuery(id+"F0.wireOp",EDGE,"E800"),sQuery(id+"F0.wireOp",EDGE,"E801"),sQuery(id+"F0.wireOp",EDGE,"E802"),sQuery(id+"F0.wireOp",EDGE,"E803"),sQuery(id+"F0.wireOp",EDGE,"E804"),sQuery(id+"F0.wireOp",EDGE,"E805"),sQuery(id+"F0.wireOp",EDGE,"E806"),sQuery(id+"F0.wireOp",EDGE,"E807"),sQuery(id+"F0.wireOp",EDGE,"E808"),sQuery(id+"F0.wireOp",EDGE,"E809"),sQuery(id+"F0.wireOp",EDGE,"E810"),sQuery(id+"F0.wireOp",EDGE,"E811"),sQuery(id+"F0.wireOp",EDGE,"E812"),sQuery(id+"F0.wireOp",EDGE,"E813"),sQuery(id+"F0.wireOp",EDGE,"E814"),sQuery(id+"F0.wireOp",EDGE,"E815"),sQuery(id+"F0.wireOp",EDGE,"E816"),sQuery(id+"F0.wireOp",EDGE,"E817"),sQuery(id+"F0.wireOp",EDGE,"E818"),sQuery(id+"F0.wireOp",EDGE,"E819"),sQuery(id+"F0.wireOp",EDGE,"E820"),sQuery(id+"F0.wireOp",EDGE,"E821"),sQuery(id+"F0.wireOp",EDGE,"E822"),sQuery(id+"F0.wireOp",EDGE,"E823"),sQuery(id+"F0.wireOp",EDGE,"E824"),sQuery(id+"F0.wireOp",EDGE,"E825"),sQuery(id+"F0.wireOp",EDGE,"E826"),sQuery(id+"F0.wireOp",EDGE,"E827"),sQuery(id+"F0.wireOp",EDGE,"E828"),sQuery(id+"F0.wireOp",EDGE,"E829"),sQuery(id+"F0.wireOp",EDGE,"E830"),sQuery(id+"F0.wireOp",EDGE,"E831"),sQuery(id+"F0.wireOp",EDGE,"E832"),sQuery(id+"F0.wireOp",EDGE,"E833"),sQuery(id+"F0.wireOp",EDGE,"E834"),sQuery(id+"F0.wireOp",EDGE,"E835"),sQuery(id+"F0.wireOp",EDGE,"E836"),sQuery(id+"F0.wireOp",EDGE,"E837"),sQuery(id+"F0.wireOp",EDGE,"E838"),sQuery(id+"F0.wireOp",EDGE,"E839"),sQuery(id+"F0.wireOp",EDGE,"E840"),sQuery(id+"F0.wireOp",EDGE,"E841"),sQuery(id+"F0.wireOp",EDGE,"E842"),sQuery(id+"F0.wireOp",EDGE,"E843"),sQuery(id+"F0.wireOp",EDGE,"E844"),sQuery(id+"F0.wireOp",EDGE,"E845"),sQuery(id+"F0.wireOp",EDGE,"E846"),sQuery(id+"F0.wireOp",EDGE,"E847"),sQuery(id+"F0.wireOp",EDGE,"E848"),sQuery(id+"F0.wireOp",EDGE,"E849"),sQuery(id+"F0.wireOp",EDGE,"E850"),sQuery(id+"F0.wireOp",EDGE,"E851"),sQuery(id+"F0.wireOp",EDGE,"E852"),sQuery(id+"F0.wireOp",EDGE,"E853"),sQuery(id+"F0.wireOp",EDGE,"E854"),sQuery(id+"F0.wireOp",EDGE,"E855"),sQuery(id+"F0.wireOp",EDGE,"E856"),sQuery(id+"F0.wireOp",EDGE,"E857"),sQuery(id+"F0.wireOp",EDGE,"E858"),sQuery(id+"F0.wireOp",EDGE,"E859"),sQuery(id+"F0.wireOp",EDGE,"E860"),sQuery(id+"F0.wireOp",EDGE,"E861"),sQuery(id+"F0.wireOp",EDGE,"E862"),sQuery(id+"F0.wireOp",EDGE,"E863"),sQuery(id+"F0.wireOp",EDGE,"E864"),sQuery(id+"F0.wireOp",EDGE,"E865"),sQuery(id+"F0.wireOp",EDGE,"E866"),sQuery(id+"F0.wireOp",EDGE,"E867"),sQuery(id+"F0.wireOp",EDGE,"E868"),sQuery(id+"F0.wireOp",EDGE,"E869"),sQuery(id+"F0.wireOp",EDGE,"E870"),sQuery(id+"F0.wireOp",EDGE,"E871"),sQuery(id+"F0.wireOp",EDGE,"E872"),sQuery(id+"F0.wireOp",EDGE,"E873"),sQuery(id+"F0.wireOp",EDGE,"E874"),sQuery(id+"F0.wireOp",EDGE,"E875"),sQuery(id+"F0.wireOp",EDGE,"E876"),sQuery(id+"F0.wireOp",EDGE,"E877"),sQuery(id+"F0.wireOp",EDGE,"E878"),sQuery(id+"F0.wireOp",EDGE,"E879"),sQuery(id+"F0.wireOp",EDGE,"E880"),sQuery(id+"F0.wireOp",EDGE,"E881"),sQuery(id+"F0.wireOp",EDGE,"E882"),sQuery(id+"F0.wireOp",EDGE,"E883"),sQuery(id+"F0.wireOp",EDGE,"E884"),sQuery(id+"F0.wireOp",EDGE,"E885"),sQuery(id+"F0.wireOp",EDGE,"E886"),sQuery(id+"F0.wireOp",EDGE,"E887"),sQuery(id+"F0.wireOp",EDGE,"E888"),sQuery(id+"F0.wireOp",EDGE,"E889"),sQuery(id+"F0.wireOp",EDGE,"E890"),sQuery(id+"F0.wireOp",EDGE,"E891"),sQuery(id+"F0.wireOp",EDGE,"E892"),sQuery(id+"F0.wireOp",EDGE,"E893"),sQuery(id+"F0.wireOp",EDGE,"E894"),sQuery(id+"F0.wireOp",EDGE,"E895"),sQuery(id+"F0.wireOp",EDGE,"E896"),sQuery(id+"F0.wireOp",EDGE,"E897"),sQuery(id+"F0.wireOp",EDGE,"E898"),sQuery(id+"F0.wireOp",EDGE,"E899"),sQuery(id+"F0.wireOp",EDGE,"E900"),sQuery(id+"F0.wireOp",EDGE,"E901"),sQuery(id+"F0.wireOp",EDGE,"E902"),sQuery(id+"F0.wireOp",EDGE,"E903"),sQuery(id+"F0.wireOp",EDGE,"E904"),sQuery(id+"F0.wireOp",EDGE,"E905"),sQuery(id+"F0.wireOp",EDGE,"E906"),sQuery(id+"F0.wireOp",EDGE,"E907"),sQuery(id+"F0.wireOp",EDGE,"E908"),sQuery(id+"F0.wireOp",EDGE,"E909"),sQuery(id+"F0.wireOp",EDGE,"E910"),sQuery(id+"F0.wireOp",EDGE,"E911"),sQuery(id+"F0.wireOp",EDGE,"E912"),sQuery(id+"F0.wireOp",EDGE,"E913"),sQuery(id+"F0.wireOp",EDGE,"E914"),sQuery(id+"F0.wireOp",EDGE,"E915"),sQuery(id+"F0.wireOp",EDGE,"E916"),sQuery(id+"F0.wireOp",EDGE,"E917"),sQuery(id+"F0.wireOp",EDGE,"E918"),sQuery(id+"F0.wireOp",EDGE,"E919"),sQuery(id+"F0.wireOp",EDGE,"E920"),sQuery(id+"F0.wireOp",EDGE,"E921"),sQuery(id+"F0.wireOp",EDGE,"E922"),sQuery(id+"F0.wireOp",EDGE,"E923"),sQuery(id+"F0.wireOp",EDGE,"E924"),sQuery(id+"F0.wireOp",EDGE,"E925"),sQuery(id+"F0.wireOp",EDGE,"E926"),sQuery(id+"F0.wireOp",EDGE,"E927"),sQuery(id+"F0.wireOp",EDGE,"E928"),sQuery(id+"F0.wireOp",EDGE,"E929"),sQuery(id+"F0.wireOp",EDGE,"E930"),sQuery(id+"F0.wireOp",EDGE,"E931"),sQuery(id+"F0.wireOp",EDGE,"E932"),sQuery(id+"F0.wireOp",EDGE,"E933"),sQuery(id+"F0.wireOp",EDGE,"E934"),sQuery(id+"F0.wireOp",EDGE,"E935"),sQuery(id+"F0.wireOp",EDGE,"E936"),sQuery(id+"F0.wireOp",EDGE,"E937"),sQuery(id+"F0.wireOp",EDGE,"E938"),sQuery(id+"F0.wireOp",EDGE,"E939"),sQuery(id+"F0.wireOp",EDGE,"E940"),sQuery(id+"F0.wireOp",EDGE,"E941"),sQuery(id+"F0.wireOp",EDGE,"E942"),sQuery(id+"F0.wireOp",EDGE,"E943"),sQuery(id+"F0.wireOp",EDGE,"E944"),sQuery(id+"F0.wireOp",EDGE,"E945"),sQuery(id+"F0.wireOp",EDGE,"E946"),sQuery(id+"F0.wireOp",EDGE,"E947"),sQuery(id+"F0.wireOp",EDGE,"E948"),sQuery(id+"F0.wireOp",EDGE,"E949"),sQuery(id+"F0.wireOp",EDGE,"E950"),sQuery(id+"F0.wireOp",EDGE,"E951"),sQuery(id+"F0.wireOp",EDGE,"E952"),sQuery(id+"F0.wireOp",EDGE,"E953"),sQuery(id+"F0.wireOp",EDGE,"E954"),sQuery(id+"F0.wireOp",EDGE,"E955"),sQuery(id+"F0.wireOp",EDGE,"E956"),sQuery(id+"F0.wireOp",EDGE,"E957"),sQuery(id+"F0.wireOp",EDGE,"E958"),sQuery(id+"F0.wireOp",EDGE,"E959"),sQuery(id+"F0.wireOp",EDGE,"E960"),sQuery(id+"F0.wireOp",EDGE,"E961"),sQuery(id+"F0.wireOp",EDGE,"E962"),sQuery(id+"F0.wireOp",EDGE,"E963"),sQuery(id+"F0.wireOp",EDGE,"E964"),sQuery(id+"F0.wireOp",EDGE,"E965"),sQuery(id+"F0.wireOp",EDGE,"E966"),sQuery(id+"F0.wireOp",EDGE,"E967"),sQuery(id+"F0.wireOp",EDGE,"E968"),sQuery(id+"F0.wireOp",EDGE,"E969"),sQuery(id+"F0.wireOp",EDGE,"E970"),sQuery(id+"F0.wireOp",EDGE,"E971"),sQuery(id+"F0.wireOp",EDGE,"E972"),sQuery(id+"F0.wireOp",EDGE,"E973"),sQuery(id+"F0.wireOp",EDGE,"E974"),sQuery(id+"F0.wireOp",EDGE,"E975"),sQuery(id+"F0.wireOp",EDGE,"E976"),sQuery(id+"F0.wireOp",EDGE,"E977"),sQuery(id+"F0.wireOp",EDGE,"E978"),sQuery(id+"F0.wireOp",EDGE,"E979"),sQuery(id+"F0.wireOp",EDGE,"E980"),sQuery(id+"F0.wireOp",EDGE,"E981"),sQuery(id+"F0.wireOp",EDGE,"E982"),sQuery(id+"F0.wireOp",EDGE,"E983"),sQuery(id+"F0.wireOp",EDGE,"E984"),sQuery(id+"F0.wireOp",EDGE,"E985"),sQuery(id+"F0.wireOp",EDGE,"E986"),sQuery(id+"F0.wireOp",EDGE,"E987"),sQuery(id+"F0.wireOp",EDGE,"E988"),sQuery(id+"F0.wireOp",EDGE,"E989"),sQuery(id+"F0.wireOp",EDGE,"E990"),sQuery(id+"F0.wireOp",EDGE,"E991"),sQuery(id+"F0.wireOp",EDGE,"E992"),sQuery(id+"F0.wireOp",EDGE,"E993"),sQuery(id+"F0.wireOp",EDGE,"E994"),sQuery(id+"F0.wireOp",EDGE,"E995"),sQuery(id+"F0.wireOp",EDGE,"E996"),sQuery(id+"F0.wireOp",EDGE,"E997"),sQuery(id+"F0.wireOp",EDGE,"E998"),sQuery(id+"F0.wireOp",EDGE,"E999"),sQuery(id+"F0.wireOp",EDGE,"E1000"),sQuery(id+"F0.wireOp",EDGE,"E1001"),sQuery(id+"F0.wireOp",EDGE,"E1002"),sQuery(id+"F0.wireOp",EDGE,"E1003"),sQuery(id+"F0.wireOp",EDGE,"E1004"),sQuery(id+"F0.wireOp",EDGE,"E1005"),sQuery(id+"F0.wireOp",EDGE,"E1006"),sQuery(id+"F0.wireOp",EDGE,"E1007"),sQuery(id+"F0.wireOp",EDGE,"E1008"),sQuery(id+"F0.wireOp",EDGE,"E1009"),sQuery(id+"F0.wireOp",EDGE,"E1010"),sQuery(id+"F0.wireOp",EDGE,"E1011"),sQuery(id+"F0.wireOp",EDGE,"E1012"),sQuery(id+"F0.wireOp",EDGE,"E1013"),sQuery(id+"F0.wireOp",EDGE,"E1014"),sQuery(id+"F0.wireOp",EDGE,"E1015"),sQuery(id+"F0.wireOp",EDGE,"E1016"),sQuery(id+"F0.wireOp",EDGE,"E1017"),sQuery(id+"F0.wireOp",EDGE,"E1018"),sQuery(id+"F0.wireOp",EDGE,"E1019"),sQuery(id+"F0.wireOp",EDGE,"E1020"),sQuery(id+"F0.wireOp",EDGE,"E1021"),sQuery(id+"F0.wireOp",EDGE,"E1022"),sQuery(id+"F0.wireOp",EDGE,"E1023"),sQuery(id+"F0.wireOp",EDGE,"E1024"),sQuery(id+"F0.wireOp",EDGE,"E1025"),sQuery(id+"F0.wireOp",EDGE,"E1026"),sQuery(id+"F0.wireOp",EDGE,"E1027"),sQuery(id+"F0.wireOp",EDGE,"E1028"),sQuery(id+"F0.wireOp",EDGE,"E1029"),sQuery(id+"F0.wireOp",EDGE,"E1030"),sQuery(id+"F0.wireOp",EDGE,"E1031"),sQuery(id+"F0.wireOp",EDGE,"E1032"),sQuery(id+"F0.wireOp",EDGE,"E1033"),sQuery(id+"F0.wireOp",EDGE,"E1034"),sQuery(id+"F0.wireOp",EDGE,"E1035"),sQuery(id+"F0.wireOp",EDGE,"E1036"),sQuery(id+"F0.wireOp",EDGE,"E1037"),sQuery(id+"F0.wireOp",EDGE,"E1038"),sQuery(id+"F0.wireOp",EDGE,"E1039"),sQuery(id+"F0.wireOp",EDGE,"E1040"),sQuery(id+"F0.wireOp",EDGE,"E1041"),sQuery(id+"F0.wireOp",EDGE,"E1042"),sQuery(id+"F0.wireOp",EDGE,"E1043"),sQuery(id+"F0.wireOp",EDGE,"E1044"),sQuery(id+"F0.wireOp",EDGE,"E1045"),sQuery(id+"F0.wireOp",EDGE,"E1046"),sQuery(id+"F0.wireOp",EDGE,"E1047"),sQuery(id+"F0.wireOp",EDGE,"E1048"),sQuery(id+"F0.wireOp",EDGE,"E1049"),sQuery(id+"F0.wireOp",EDGE,"E1050"),sQuery(id+"F0.wireOp",EDGE,"E1051"),sQuery(id+"F0.wireOp",EDGE,"E1052"),sQuery(id+"F0.wireOp",EDGE,"E1053"),sQuery(id+"F0.wireOp",EDGE,"E1054"),sQuery(id+"F0.wireOp",EDGE,"E1055"),sQuery(id+"F0.wireOp",EDGE,"E1056"),sQuery(id+"F0.wireOp",EDGE,"E1057"),sQuery(id+"F0.wireOp",EDGE,"E1058"),sQuery(id+"F0.wireOp",EDGE,"E1059"),sQuery(id+"F0.wireOp",EDGE,"E1060"),sQuery(id+"F0.wireOp",EDGE,"E1061"),sQuery(id+"F0.wireOp",EDGE,"E1062"),sQuery(id+"F0.wireOp",EDGE,"E1063"),sQuery(id+"F0.wireOp",EDGE,"E1064"),sQuery(id+"F0.wireOp",EDGE,"E1065"),sQuery(id+"F0.wireOp",EDGE,"E1066"),sQuery(id+"F0.wireOp",EDGE,"E1067"),sQuery(id+"F0.wireOp",EDGE,"E1068"),sQuery(id+"F0.wireOp",EDGE,"E1069"),sQuery(id+"F0.wireOp",EDGE,"E1070"),sQuery(id+"F0.wireOp",EDGE,"E1071"),sQuery(id+"F0.wireOp",EDGE,"E1072"),sQuery(id+"F0.wireOp",EDGE,"E1073"),sQuery(id+"F0.wireOp",EDGE,"E1074"),sQuery(id+"F0.wireOp",EDGE,"E1075"),sQuery(id+"F0.wireOp",EDGE,"E1076"),sQuery(id+"F0.wireOp",EDGE,"E1077"),sQuery(id+"F0.wireOp",EDGE,"E1078"),sQuery(id+"F0.wireOp",EDGE,"E1079"),sQuery(id+"F0.wireOp",EDGE,"E1080"),sQuery(id+"F0.wireOp",EDGE,"E1081"),sQuery(id+"F0.wireOp",EDGE,"E1082"),sQuery(id+"F0.wireOp",EDGE,"E1083"),sQuery(id+"F0.wireOp",EDGE,"E1084"),sQuery(id+"F0.wireOp",EDGE,"E1085"),sQuery(id+"F0.wireOp",EDGE,"E1086"),sQuery(id+"F0.wireOp",EDGE,"E1087"),sQuery(id+"F0.wireOp",EDGE,"E1088"),sQuery(id+"F0.wireOp",EDGE,"E1089"),sQuery(id+"F0.wireOp",EDGE,"E1090"),sQuery(id+"F0.wireOp",EDGE,"E1091"),sQuery(id+"F0.wireOp",EDGE,"E1092"),sQuery(id+"F0.wireOp",EDGE,"E1093"),sQuery(id+"F0.wireOp",EDGE,"E1094"),sQuery(id+"F0.wireOp",EDGE,"E1095"),sQuery(id+"F0.wireOp",EDGE,"E1096"),sQuery(id+"F0.wireOp",EDGE,"E1097"),sQuery(id+"F0.wireOp",EDGE,"E1098"),sQuery(id+"F0.wireOp",EDGE,"E1099"),sQuery(id+"F0.wireOp",EDGE,"E1100"),sQuery(id+"F0.wireOp",EDGE,"E1101"),sQuery(id+"F0.wireOp",EDGE,"E1102"),sQuery(id+"F0.wireOp",EDGE,"E1103"),sQuery(id+"F0.wireOp",EDGE,"E1104"),sQuery(id+"F0.wireOp",EDGE,"E1105"),sQuery(id+"F0.wireOp",EDGE,"E1106"),sQuery(id+"F0.wireOp",EDGE,"E1107"),sQuery(id+"F0.wireOp",EDGE,"E1108"),sQuery(id+"F0.wireOp",EDGE,"E1109"),sQuery(id+"F0.wireOp",EDGE,"E1110"),sQuery(id+"F0.wireOp",EDGE,"E1111"),sQuery(id+"F0.wireOp",EDGE,"E1112"),sQuery(id+"F0.wireOp",EDGE,"E1113"),sQuery(id+"F0.wireOp",EDGE,"E1114"),sQuery(id+"F0.wireOp",EDGE,"E1115"),sQuery(id+"F0.wireOp",EDGE,"E1116"),sQuery(id+"F0.wireOp",EDGE,"E1117"),sQuery(id+"F0.wireOp",EDGE,"E1118"),sQuery(id+"F0.wireOp",EDGE,"E1119"),sQuery(id+"F0.wireOp",EDGE,"E1120"),sQuery(id+"F0.wireOp",EDGE,"E1121"),sQuery(id+"F0.wireOp",EDGE,"E1122"),sQuery(id+"F0.wireOp",EDGE,"E1123"),sQuery(id+"F0.wireOp",EDGE,"E1124"),sQuery(id+"F0.wireOp",EDGE,"E1125"),sQuery(id+"F0.wireOp",EDGE,"E1126"),sQuery(id+"F0.wireOp",EDGE,"E1127"),sQuery(id+"F0.wireOp",EDGE,"E1128"),sQuery(id+"F0.wireOp",EDGE,"E1129"),sQuery(id+"F0.wireOp",EDGE,"E1130"),sQuery(id+"F0.wireOp",EDGE,"E1131"),sQuery(id+"F0.wireOp",EDGE,"E1132"),sQuery(id+"F0.wireOp",EDGE,"E1133"),sQuery(id+"F0.wireOp",EDGE,"E1134"),sQuery(id+"F0.wireOp",EDGE,"E1135"),sQuery(id+"F0.wireOp",EDGE,"E1136"),sQuery(id+"F0.wireOp",EDGE,"E1137"),sQuery(id+"F0.wireOp",EDGE,"E1138"),sQuery(id+"F0.wireOp",EDGE,"E1139"),sQuery(id+"F0.wireOp",EDGE,"E1140"),sQuery(id+"F0.wireOp",EDGE,"E1141"),sQuery(id+"F0.wireOp",EDGE,"E1142"),sQuery(id+"F0.wireOp",EDGE,"E1143"),sQuery(id+"F0.wireOp",EDGE,"E1144"),sQuery(id+"F0.wireOp",EDGE,"E1145"),sQuery(id+"F0.wireOp",EDGE,"E1146"),sQuery(id+"F0.wireOp",EDGE,"E1147"),sQuery(id+"F0.wireOp",EDGE,"E1148"),sQuery(id+"F0.wireOp",EDGE,"E1149"),sQuery(id+"F0.wireOp",EDGE,"E1150"),sQuery(id+"F0.wireOp",EDGE,"E1151"),sQuery(id+"F0.wireOp",EDGE,"E1152"),sQuery(id+"F0.wireOp",EDGE,"E1153"),sQuery(id+"F0.wireOp",EDGE,"E1154"),sQuery(id+"F0.wireOp",EDGE,"E1155"),sQuery(id+"F0.wireOp",EDGE,"E1156"),sQuery(id+"F0.wireOp",EDGE,"E1157"),sQuery(id+"F0.wireOp",EDGE,"E1158"),sQuery(id+"F0.wireOp",EDGE,"E1159"),sQuery(id+"F0.wireOp",EDGE,"E1160"),sQuery(id+"F0.wireOp",EDGE,"E1161"),sQuery(id+"F0.wireOp",EDGE,"E1162"),sQuery(id+"F0.wireOp",EDGE,"E1163"),sQuery(id+"F0.wireOp",EDGE,"E1164"),sQuery(id+"F0.wireOp",EDGE,"E1165"),sQuery(id+"F0.wireOp",EDGE,"E1166"),sQuery(id+"F0.wireOp",EDGE,"E1167"),sQuery(id+"F0.wireOp",EDGE,"E1168"),sQuery(id+"F0.wireOp",EDGE,"E1169"),sQuery(id+"F0.wireOp",EDGE,"E1170"),sQuery(id+"F0.wireOp",EDGE,"E1171"),sQuery(id+"F0.wireOp",EDGE,"E1172"),sQuery(id+"F0.wireOp",EDGE,"E1173"),sQuery(id+"F0.wireOp",EDGE,"E1174"),sQuery(id+"F0.wireOp",EDGE,"E1175"),sQuery(id+"F0.wireOp",EDGE,"E1176"),sQuery(id+"F0.wireOp",EDGE,"E1177"),sQuery(id+"F0.wireOp",EDGE,"E1178"),sQuery(id+"F0.wireOp",EDGE,"E1179"),sQuery(id+"F0.wireOp",EDGE,"E1180"),sQuery(id+"F0.wireOp",EDGE,"E1181"),sQuery(id+"F0.wireOp",EDGE,"E1182"),sQuery(id+"F0.wireOp",EDGE,"E1183"),sQuery(id+"F0.wireOp",EDGE,"E1184"),sQuery(id+"F0.wireOp",EDGE,"E1185"),sQuery(id+"F0.wireOp",EDGE,"E1186"),sQuery(id+"F0.wireOp",EDGE,"E1187"),sQuery(id+"F0.wireOp",EDGE,"E1188"),sQuery(id+"F0.wireOp",EDGE,"E1189"),sQuery(id+"F0.wireOp",EDGE,"E1190"),sQuery(id+"F0.wireOp",EDGE,"E1191"),sQuery(id+"F0.wireOp",EDGE,"E1192"),sQuery(id+"F0.wireOp",EDGE,"E1193"),sQuery(id+"F0.wireOp",EDGE,"E1194"),sQuery(id+"F0.wireOp",EDGE,"E1195"),sQuery(id+"F0.wireOp",EDGE,"E1196"),sQuery(id+"F0.wireOp",EDGE,"E1197"),sQuery(id+"F0.wireOp",EDGE,"E1198"),sQuery(id+"F0.wireOp",EDGE,"E1199"),sQuery(id+"F0.wireOp",EDGE,"E1200"),sQuery(id+"F0.wireOp",EDGE,"E1201"),sQuery(id+"F0.wireOp",EDGE,"E1202"),sQuery(id+"F0.wireOp",EDGE,"E1203"),sQuery(id+"F0.wireOp",EDGE,"E1204"),sQuery(id+"F0.wireOp",EDGE,"E1205"),sQuery(id+"F0.wireOp",EDGE,"E1206"),sQuery(id+"F0.wireOp",EDGE,"E1207"),sQuery(id+"F0.wireOp",EDGE,"E1208"),sQuery(id+"F0.wireOp",EDGE,"E1209"),sQuery(id+"F0.wireOp",EDGE,"E1210"),sQuery(id+"F0.wireOp",EDGE,"E1211"),sQuery(id+"F0.wireOp",EDGE,"E1212"),sQuery(id+"F0.wireOp",EDGE,"E1213"),sQuery(id+"F0.wireOp",EDGE,"E1214"),sQuery(id+"F0.wireOp",EDGE,"E1215"),sQuery(id+"F0.wireOp",EDGE,"E1216"),sQuery(id+"F0.wireOp",EDGE,"E1217"),sQuery(id+"F0.wireOp",EDGE,"E1218"),sQuery(id+"F0.wireOp",EDGE,"E1219"),sQuery(id+"F0.wireOp",EDGE,"E1220"),sQuery(id+"F0.wireOp",EDGE,"E1221"),sQuery(id+"F0.wireOp",EDGE,"E1222"),sQuery(id+"F0.wireOp",EDGE,"E1223"),sQuery(id+"F0.wireOp",EDGE,"E1224"),sQuery(id+"F0.wireOp",EDGE,"E1225"),sQuery(id+"F0.wireOp",EDGE,"E1226"),sQuery(id+"F0.wireOp",EDGE,"E1227"),sQuery(id+"F0.wireOp",EDGE,"E1228"),sQuery(id+"F0.wireOp",EDGE,"E1229"),sQuery(id+"F0.wireOp",EDGE,"E1230"),sQuery(id+"F0.wireOp",EDGE,"E1231"),sQuery(id+"F0.wireOp",EDGE,"E1232"),sQuery(id+"F0.wireOp",EDGE,"E1233"),sQuery(id+"F0.wireOp",EDGE,"E1234"),sQuery(id+"F0.wireOp",EDGE,"E1235"),sQuery(id+"F0.wireOp",EDGE,"E1236"),sQuery(id+"F0.wireOp",EDGE,"E1237"),sQuery(id+"F0.wireOp",EDGE,"E1238"),sQuery(id+"F0.wireOp",EDGE,"E1239"),sQuery(id+"F0.wireOp",EDGE,"E1240"),sQuery(id+"F0.wireOp",EDGE,"E1241"),sQuery(id+"F0.wireOp",EDGE,"E1242"),sQuery(id+"F0.wireOp",EDGE,"E1243"),sQuery(id+"F0.wireOp",EDGE,"E1244"),sQuery(id+"F0.wireOp",EDGE,"E1245"),sQuery(id+"F0.wireOp",EDGE,"E1246"),sQuery(id+"F0.wireOp",EDGE,"E1247"),sQuery(id+"F0.wireOp",EDGE,"E1248"),sQuery(id+"F0.wireOp",EDGE,"E1249"),sQuery(id+"F0.wireOp",EDGE,"E1250"),sQuery(id+"F0.wireOp",EDGE,"E1251"),sQuery(id+"F0.wireOp",EDGE,"E1252"),sQuery(id+"F0.wireOp",EDGE,"E1253"),sQuery(id+"F0.wireOp",EDGE,"E1254"),sQuery(id+"F0.wireOp",EDGE,"E1255"),sQuery(id+"F0.wireOp",EDGE,"E1256"),sQuery(id+"F0.wireOp",EDGE,"E1257"),sQuery(id+"F0.wireOp",EDGE,"E1258"),sQuery(id+"F0.wireOp",EDGE,"E1259"),sQuery(id+"F0.wireOp",EDGE,"E1260"),sQuery(id+"F0.wireOp",EDGE,"E1261"),sQuery(id+"F0.wireOp",EDGE,"E1262"),sQuery(id+"F0.wireOp",EDGE,"E1263"),sQuery(id+"F0.wireOp",EDGE,"E1264"),sQuery(id+"F0.wireOp",EDGE,"E1265"),sQuery(id+"F0.wireOp",EDGE,"E1266"),sQuery(id+"F0.wireOp",EDGE,"E1267"),sQuery(id+"F0.wireOp",EDGE,"E1268"),sQuery(id+"F0.wireOp",EDGE,"E1269"),sQuery(id+"F0.wireOp",EDGE,"E1270"),sQuery(id+"F0.wireOp",EDGE,"E1271"),sQuery(id+"F0.wireOp",EDGE,"E1272"),sQuery(id+"F0.wireOp",EDGE,"E1273"),sQuery(id+"F0.wireOp",EDGE,"E1274"),sQuery(id+"F0.wireOp",EDGE,"E1275"),sQuery(id+"F0.wireOp",EDGE,"E1276"),sQuery(id+"F0.wireOp",EDGE,"E1277"),sQuery(id+"F0.wireOp",EDGE,"E1278"),sQuery(id+"F0.wireOp",EDGE,"E1279"),sQuery(id+"F0.wireOp",EDGE,"E1280"),sQuery(id+"F0.wireOp",EDGE,"E1281"),sQuery(id+"F0.wireOp",EDGE,"E1282"),sQuery(id+"F0.wireOp",EDGE,"E1283"),sQuery(id+"F0.wireOp",EDGE,"E1284"),sQuery(id+"F0.wireOp",EDGE,"E1285"),sQuery(id+"F0.wireOp",EDGE,"E1286"),sQuery(id+"F0.wireOp",EDGE,"E1287"),sQuery(id+"F0.wireOp",EDGE,"E1288"),sQuery(id+"F0.wireOp",EDGE,"E1289"),sQuery(id+"F0.wireOp",EDGE,"E1290"),sQuery(id+"F0.wireOp",EDGE,"E1291"),sQuery(id+"F0.wireOp",EDGE,"E1292"),sQuery(id+"F0.wireOp",EDGE,"E1293"),sQuery(id+"F0.wireOp",EDGE,"E1294"),sQuery(id+"F0.wireOp",EDGE,"E1295"),sQuery(id+"F0.wireOp",EDGE,"E1296"),sQuery(id+"F0.wireOp",EDGE,"E1297"),sQuery(id+"F0.wireOp",EDGE,"E1298"),sQuery(id+"F0.wireOp",EDGE,"E1299"),sQuery(id+"F0.wireOp",EDGE,"E1300"),sQuery(id+"F0.wireOp",EDGE,"E1301"),sQuery(id+"F0.wireOp",EDGE,"E1302"),sQuery(id+"F0.wireOp",EDGE,"E1303"),sQuery(id+"F0.wireOp",EDGE,"E1304"),sQuery(id+"F0.wireOp",EDGE,"E1305"),sQuery(id+"F0.wireOp",EDGE,"E1306"),sQuery(id+"F0.wireOp",EDGE,"E1307"),sQuery(id+"F0.wireOp",EDGE,"E1308"),sQuery(id+"F0.wireOp",EDGE,"E1309"),sQuery(id+"F0.wireOp",EDGE,"E1310"),sQuery(id+"F0.wireOp",EDGE,"E1311"),sQuery(id+"F0.wireOp",EDGE,"E1312"),sQuery(id+"F0.wireOp",EDGE,"E1313"),sQuery(id+"F0.wireOp",EDGE,"E1314"),sQuery(id+"F0.wireOp",EDGE,"E1315"),sQuery(id+"F0.wireOp",EDGE,"E1316"),sQuery(id+"F0.wireOp",EDGE,"E1317"),sQuery(id+"F0.wireOp",EDGE,"E1318"),sQuery(id+"F0.wireOp",EDGE,"E1319"),sQuery(id+"F0.wireOp",EDGE,"E1320"),sQuery(id+"F0.wireOp",EDGE,"E1321"),sQuery(id+"F0.wireOp",EDGE,"E1322")])]});
            var Q1;
            Q1=makeQuery(id+"F5.opExtrude","SWEPT_BODY",BODY,{"disambiguationData":[OSD([sQuery(id+"F2.wireOp",EDGE,"E1325"),sQuery(id+"F4.wireOp",EDGE,"E1326"),sQuery(id+"F4.wireOp",EDGE,"E1327"),sQuery(id+"F4.wireOp",EDGE,"E1328")])]});
            var Q2;
            Q2=makeQuery(id+"F7.opExtrude","SWEPT_BODY",BODY,{"disambiguationData":[OSD([sQuery(id+"F2.wireOp",EDGE,"E1323"),sQuery(id+"F6.wireOp",EDGE,"E1329"),sQuery(id+"F6.wireOp",EDGE,"E1330"),sQuery(id+"F6.wireOp",EDGE,"E1331")])]});
            booleanBodies(context, id + "F8", {"operationType" : BooleanOperationType.UNION, "tools" : qUnion([Q0, Q1, Q2])});
        }
        {
            var Q0;
            Q0=makeQuery(id+"F3.opExtrude","SWEPT_BODY",BODY,{"disambiguationData":[OSD([sQuery(id+"F0.wireOp",EDGE,"E4"),sQuery(id+"F0.wireOp",EDGE,"E5"),sQuery(id+"F0.wireOp",EDGE,"E6"),sQuery(id+"F0.wireOp",EDGE,"E123"),sQuery(id+"F0.wireOp",EDGE,"E124"),sQuery(id+"F2.wireOp",EDGE,"E1323"),sQuery(id+"F2.wireOp",EDGE,"E1324"),sQuery(id+"F2.wireOp",EDGE,"E1325")])]});
            var Q1;
            Q1=makeQuery(id+"F1.opExtrude","SWEPT_BODY",BODY,{"disambiguationData":[OSD([sQuery(id+"F0.wireOp",EDGE,"E2"),sQuery(id+"F0.wireOp",EDGE,"E4"),sQuery(id+"F0.wireOp",EDGE,"E5"),sQuery(id+"F0.wireOp",EDGE,"E6"),sQuery(id+"F0.wireOp",EDGE,"E7"),sQuery(id+"F0.wireOp",EDGE,"E8"),sQuery(id+"F0.wireOp",EDGE,"E9"),sQuery(id+"F0.wireOp",EDGE,"E10"),sQuery(id+"F0.wireOp",EDGE,"E11"),sQuery(id+"F0.wireOp",EDGE,"E12"),sQuery(id+"F0.wireOp",EDGE,"E13"),sQuery(id+"F0.wireOp",EDGE,"E14"),sQuery(id+"F0.wireOp",EDGE,"E15"),sQuery(id+"F0.wireOp",EDGE,"E16"),sQuery(id+"F0.wireOp",EDGE,"E17"),sQuery(id+"F0.wireOp",EDGE,"E18"),sQuery(id+"F0.wireOp",EDGE,"E19"),sQuery(id+"F0.wireOp",EDGE,"E20"),sQuery(id+"F0.wireOp",EDGE,"E21"),sQuery(id+"F0.wireOp",EDGE,"E22"),sQuery(id+"F0.wireOp",EDGE,"E23"),sQuery(id+"F0.wireOp",EDGE,"E24"),sQuery(id+"F0.wireOp",EDGE,"E25"),sQuery(id+"F0.wireOp",EDGE,"E26"),sQuery(id+"F0.wireOp",EDGE,"E27"),sQuery(id+"F0.wireOp",EDGE,"E28"),sQuery(id+"F0.wireOp",EDGE,"E29"),sQuery(id+"F0.wireOp",EDGE,"E30"),sQuery(id+"F0.wireOp",EDGE,"E31"),sQuery(id+"F0.wireOp",EDGE,"E32"),sQuery(id+"F0.wireOp",EDGE,"E33"),sQuery(id+"F0.wireOp",EDGE,"E34"),sQuery(id+"F0.wireOp",EDGE,"E35"),sQuery(id+"F0.wireOp",EDGE,"E36"),sQuery(id+"F0.wireOp",EDGE,"E37"),sQuery(id+"F0.wireOp",EDGE,"E38"),sQuery(id+"F0.wireOp",EDGE,"E39"),sQuery(id+"F0.wireOp",EDGE,"E40"),sQuery(id+"F0.wireOp",EDGE,"E41"),sQuery(id+"F0.wireOp",EDGE,"E42"),sQuery(id+"F0.wireOp",EDGE,"E43"),sQuery(id+"F0.wireOp",EDGE,"E44"),sQuery(id+"F0.wireOp",EDGE,"E45"),sQuery(id+"F0.wireOp",EDGE,"E46"),sQuery(id+"F0.wireOp",EDGE,"E47"),sQuery(id+"F0.wireOp",EDGE,"E48"),sQuery(id+"F0.wireOp",EDGE,"E49"),sQuery(id+"F0.wireOp",EDGE,"E50"),sQuery(id+"F0.wireOp",EDGE,"E51"),sQuery(id+"F0.wireOp",EDGE,"E52"),sQuery(id+"F0.wireOp",EDGE,"E53"),sQuery(id+"F0.wireOp",EDGE,"E54"),sQuery(id+"F0.wireOp",EDGE,"E55"),sQuery(id+"F0.wireOp",EDGE,"E56"),sQuery(id+"F0.wireOp",EDGE,"E57"),sQuery(id+"F0.wireOp",EDGE,"E58"),sQuery(id+"F0.wireOp",EDGE,"E59"),sQuery(id+"F0.wireOp",EDGE,"E60"),sQuery(id+"F0.wireOp",EDGE,"E61"),sQuery(id+"F0.wireOp",EDGE,"E62"),sQuery(id+"F0.wireOp",EDGE,"E63"),sQuery(id+"F0.wireOp",EDGE,"E64"),sQuery(id+"F0.wireOp",EDGE,"E65"),sQuery(id+"F0.wireOp",EDGE,"E66"),sQuery(id+"F0.wireOp",EDGE,"E67"),sQuery(id+"F0.wireOp",EDGE,"E68"),sQuery(id+"F0.wireOp",EDGE,"E69"),sQuery(id+"F0.wireOp",EDGE,"E70"),sQuery(id+"F0.wireOp",EDGE,"E71"),sQuery(id+"F0.wireOp",EDGE,"E72"),sQuery(id+"F0.wireOp",EDGE,"E73"),sQuery(id+"F0.wireOp",EDGE,"E74"),sQuery(id+"F0.wireOp",EDGE,"E75"),sQuery(id+"F0.wireOp",EDGE,"E76"),sQuery(id+"F0.wireOp",EDGE,"E77"),sQuery(id+"F0.wireOp",EDGE,"E78"),sQuery(id+"F0.wireOp",EDGE,"E79"),sQuery(id+"F0.wireOp",EDGE,"E80"),sQuery(id+"F0.wireOp",EDGE,"E81"),sQuery(id+"F0.wireOp",EDGE,"E82"),sQuery(id+"F0.wireOp",EDGE,"E83"),sQuery(id+"F0.wireOp",EDGE,"E84"),sQuery(id+"F0.wireOp",EDGE,"E85"),sQuery(id+"F0.wireOp",EDGE,"E86"),sQuery(id+"F0.wireOp",EDGE,"E87"),sQuery(id+"F0.wireOp",EDGE,"E88"),sQuery(id+"F0.wireOp",EDGE,"E89"),sQuery(id+"F0.wireOp",EDGE,"E90"),sQuery(id+"F0.wireOp",EDGE,"E91"),sQuery(id+"F0.wireOp",EDGE,"E93"),sQuery(id+"F0.wireOp",EDGE,"E94"),sQuery(id+"F0.wireOp",EDGE,"E95"),sQuery(id+"F0.wireOp",EDGE,"E96"),sQuery(id+"F0.wireOp",EDGE,"E97"),sQuery(id+"F0.wireOp",EDGE,"E98"),sQuery(id+"F0.wireOp",EDGE,"E99"),sQuery(id+"F0.wireOp",EDGE,"E100"),sQuery(id+"F0.wireOp",EDGE,"E101"),sQuery(id+"F0.wireOp",EDGE,"E102"),sQuery(id+"F0.wireOp",EDGE,"E103"),sQuery(id+"F0.wireOp",EDGE,"E104"),sQuery(id+"F0.wireOp",EDGE,"E105"),sQuery(id+"F0.wireOp",EDGE,"E106"),sQuery(id+"F0.wireOp",EDGE,"E107"),sQuery(id+"F0.wireOp",EDGE,"E108"),sQuery(id+"F0.wireOp",EDGE,"E125"),sQuery(id+"F0.wireOp",EDGE,"E126"),sQuery(id+"F0.wireOp",EDGE,"E127"),sQuery(id+"F0.wireOp",EDGE,"E128"),sQuery(id+"F0.wireOp",EDGE,"E129"),sQuery(id+"F0.wireOp",EDGE,"E130"),sQuery(id+"F0.wireOp",EDGE,"E131"),sQuery(id+"F0.wireOp",EDGE,"E132"),sQuery(id+"F0.wireOp",EDGE,"E133"),sQuery(id+"F0.wireOp",EDGE,"E134"),sQuery(id+"F0.wireOp",EDGE,"E135"),sQuery(id+"F0.wireOp",EDGE,"E136"),sQuery(id+"F0.wireOp",EDGE,"E137"),sQuery(id+"F0.wireOp",EDGE,"E138"),sQuery(id+"F0.wireOp",EDGE,"E139"),sQuery(id+"F0.wireOp",EDGE,"E140"),sQuery(id+"F0.wireOp",EDGE,"E141"),sQuery(id+"F0.wireOp",EDGE,"E142"),sQuery(id+"F0.wireOp",EDGE,"E143"),sQuery(id+"F0.wireOp",EDGE,"E144"),sQuery(id+"F0.wireOp",EDGE,"E145"),sQuery(id+"F0.wireOp",EDGE,"E146"),sQuery(id+"F0.wireOp",EDGE,"E147"),sQuery(id+"F0.wireOp",EDGE,"E148"),sQuery(id+"F0.wireOp",EDGE,"E149"),sQuery(id+"F0.wireOp",EDGE,"E150"),sQuery(id+"F0.wireOp",EDGE,"E151"),sQuery(id+"F0.wireOp",EDGE,"E152"),sQuery(id+"F0.wireOp",EDGE,"E153"),sQuery(id+"F0.wireOp",EDGE,"E154"),sQuery(id+"F0.wireOp",EDGE,"E155"),sQuery(id+"F0.wireOp",EDGE,"E156"),sQuery(id+"F0.wireOp",EDGE,"E157"),sQuery(id+"F0.wireOp",EDGE,"E158"),sQuery(id+"F0.wireOp",EDGE,"E159"),sQuery(id+"F0.wireOp",EDGE,"E160"),sQuery(id+"F0.wireOp",EDGE,"E161"),sQuery(id+"F0.wireOp",EDGE,"E162"),sQuery(id+"F0.wireOp",EDGE,"E163"),sQuery(id+"F0.wireOp",EDGE,"E164"),sQuery(id+"F0.wireOp",EDGE,"E165"),sQuery(id+"F0.wireOp",EDGE,"E166"),sQuery(id+"F0.wireOp",EDGE,"E167"),sQuery(id+"F0.wireOp",EDGE,"E168"),sQuery(id+"F0.wireOp",EDGE,"E169"),sQuery(id+"F0.wireOp",EDGE,"E170"),sQuery(id+"F0.wireOp",EDGE,"E171"),sQuery(id+"F0.wireOp",EDGE,"E172"),sQuery(id+"F0.wireOp",EDGE,"E173"),sQuery(id+"F0.wireOp",EDGE,"E174"),sQuery(id+"F0.wireOp",EDGE,"E175"),sQuery(id+"F0.wireOp",EDGE,"E176"),sQuery(id+"F0.wireOp",EDGE,"E177"),sQuery(id+"F0.wireOp",EDGE,"E178"),sQuery(id+"F0.wireOp",EDGE,"E179"),sQuery(id+"F0.wireOp",EDGE,"E180"),sQuery(id+"F0.wireOp",EDGE,"E181"),sQuery(id+"F0.wireOp",EDGE,"E182"),sQuery(id+"F0.wireOp",EDGE,"E183"),sQuery(id+"F0.wireOp",EDGE,"E184"),sQuery(id+"F0.wireOp",EDGE,"E185"),sQuery(id+"F0.wireOp",EDGE,"E186"),sQuery(id+"F0.wireOp",EDGE,"E187"),sQuery(id+"F0.wireOp",EDGE,"E188"),sQuery(id+"F0.wireOp",EDGE,"E189"),sQuery(id+"F0.wireOp",EDGE,"E190"),sQuery(id+"F0.wireOp",EDGE,"E191"),sQuery(id+"F0.wireOp",EDGE,"E192"),sQuery(id+"F0.wireOp",EDGE,"E193"),sQuery(id+"F0.wireOp",EDGE,"E194"),sQuery(id+"F0.wireOp",EDGE,"E195"),sQuery(id+"F0.wireOp",EDGE,"E196"),sQuery(id+"F0.wireOp",EDGE,"E197"),sQuery(id+"F0.wireOp",EDGE,"E198"),sQuery(id+"F0.wireOp",EDGE,"E199"),sQuery(id+"F0.wireOp",EDGE,"E200"),sQuery(id+"F0.wireOp",EDGE,"E201"),sQuery(id+"F0.wireOp",EDGE,"E202"),sQuery(id+"F0.wireOp",EDGE,"E203"),sQuery(id+"F0.wireOp",EDGE,"E204"),sQuery(id+"F0.wireOp",EDGE,"E205"),sQuery(id+"F0.wireOp",EDGE,"E206"),sQuery(id+"F0.wireOp",EDGE,"E207"),sQuery(id+"F0.wireOp",EDGE,"E208"),sQuery(id+"F0.wireOp",EDGE,"E209"),sQuery(id+"F0.wireOp",EDGE,"E210"),sQuery(id+"F0.wireOp",EDGE,"E211"),sQuery(id+"F0.wireOp",EDGE,"E212"),sQuery(id+"F0.wireOp",EDGE,"E213"),sQuery(id+"F0.wireOp",EDGE,"E214"),sQuery(id+"F0.wireOp",EDGE,"E215"),sQuery(id+"F0.wireOp",EDGE,"E216"),sQuery(id+"F0.wireOp",EDGE,"E217"),sQuery(id+"F0.wireOp",EDGE,"E218"),sQuery(id+"F0.wireOp",EDGE,"E219"),sQuery(id+"F0.wireOp",EDGE,"E220"),sQuery(id+"F0.wireOp",EDGE,"E221"),sQuery(id+"F0.wireOp",EDGE,"E222"),sQuery(id+"F0.wireOp",EDGE,"E223"),sQuery(id+"F0.wireOp",EDGE,"E224"),sQuery(id+"F0.wireOp",EDGE,"E225"),sQuery(id+"F0.wireOp",EDGE,"E226"),sQuery(id+"F0.wireOp",EDGE,"E227"),sQuery(id+"F0.wireOp",EDGE,"E228"),sQuery(id+"F0.wireOp",EDGE,"E229"),sQuery(id+"F0.wireOp",EDGE,"E230"),sQuery(id+"F0.wireOp",EDGE,"E231"),sQuery(id+"F0.wireOp",EDGE,"E232"),sQuery(id+"F0.wireOp",EDGE,"E233"),sQuery(id+"F0.wireOp",EDGE,"E234"),sQuery(id+"F0.wireOp",EDGE,"E235"),sQuery(id+"F0.wireOp",EDGE,"E236"),sQuery(id+"F0.wireOp",EDGE,"E237"),sQuery(id+"F0.wireOp",EDGE,"E238"),sQuery(id+"F0.wireOp",EDGE,"E239"),sQuery(id+"F0.wireOp",EDGE,"E240"),sQuery(id+"F0.wireOp",EDGE,"E241"),sQuery(id+"F0.wireOp",EDGE,"E242"),sQuery(id+"F0.wireOp",EDGE,"E243"),sQuery(id+"F0.wireOp",EDGE,"E244"),sQuery(id+"F0.wireOp",EDGE,"E245"),sQuery(id+"F0.wireOp",EDGE,"E246"),sQuery(id+"F0.wireOp",EDGE,"E247"),sQuery(id+"F0.wireOp",EDGE,"E248"),sQuery(id+"F0.wireOp",EDGE,"E249"),sQuery(id+"F0.wireOp",EDGE,"E250"),sQuery(id+"F0.wireOp",EDGE,"E251"),sQuery(id+"F0.wireOp",EDGE,"E252"),sQuery(id+"F0.wireOp",EDGE,"E253"),sQuery(id+"F0.wireOp",EDGE,"E254"),sQuery(id+"F0.wireOp",EDGE,"E255"),sQuery(id+"F0.wireOp",EDGE,"E256"),sQuery(id+"F0.wireOp",EDGE,"E257"),sQuery(id+"F0.wireOp",EDGE,"E258"),sQuery(id+"F0.wireOp",EDGE,"E259"),sQuery(id+"F0.wireOp",EDGE,"E260"),sQuery(id+"F0.wireOp",EDGE,"E261"),sQuery(id+"F0.wireOp",EDGE,"E262"),sQuery(id+"F0.wireOp",EDGE,"E263"),sQuery(id+"F0.wireOp",EDGE,"E264"),sQuery(id+"F0.wireOp",EDGE,"E265"),sQuery(id+"F0.wireOp",EDGE,"E266"),sQuery(id+"F0.wireOp",EDGE,"E267"),sQuery(id+"F0.wireOp",EDGE,"E268"),sQuery(id+"F0.wireOp",EDGE,"E269"),sQuery(id+"F0.wireOp",EDGE,"E270"),sQuery(id+"F0.wireOp",EDGE,"E271"),sQuery(id+"F0.wireOp",EDGE,"E272"),sQuery(id+"F0.wireOp",EDGE,"E273"),sQuery(id+"F0.wireOp",EDGE,"E274"),sQuery(id+"F0.wireOp",EDGE,"E275"),sQuery(id+"F0.wireOp",EDGE,"E276"),sQuery(id+"F0.wireOp",EDGE,"E277"),sQuery(id+"F0.wireOp",EDGE,"E278"),sQuery(id+"F0.wireOp",EDGE,"E279"),sQuery(id+"F0.wireOp",EDGE,"E280"),sQuery(id+"F0.wireOp",EDGE,"E281"),sQuery(id+"F0.wireOp",EDGE,"E282"),sQuery(id+"F0.wireOp",EDGE,"E283"),sQuery(id+"F0.wireOp",EDGE,"E284"),sQuery(id+"F0.wireOp",EDGE,"E285"),sQuery(id+"F0.wireOp",EDGE,"E92"),sQuery(id+"F0.wireOp",EDGE,"E286"),sQuery(id+"F0.wireOp",EDGE,"E287"),sQuery(id+"F0.wireOp",EDGE,"E288"),sQuery(id+"F0.wireOp",EDGE,"E289"),sQuery(id+"F0.wireOp",EDGE,"E290"),sQuery(id+"F0.wireOp",EDGE,"E291"),sQuery(id+"F0.wireOp",EDGE,"E292"),sQuery(id+"F0.wireOp",EDGE,"E293"),sQuery(id+"F0.wireOp",EDGE,"E294"),sQuery(id+"F0.wireOp",EDGE,"E295"),sQuery(id+"F0.wireOp",EDGE,"E296"),sQuery(id+"F0.wireOp",EDGE,"E297"),sQuery(id+"F0.wireOp",EDGE,"E298"),sQuery(id+"F0.wireOp",EDGE,"E299"),sQuery(id+"F0.wireOp",EDGE,"E300"),sQuery(id+"F0.wireOp",EDGE,"E301"),sQuery(id+"F0.wireOp",EDGE,"E302"),sQuery(id+"F0.wireOp",EDGE,"E303"),sQuery(id+"F0.wireOp",EDGE,"E304"),sQuery(id+"F0.wireOp",EDGE,"E305"),sQuery(id+"F0.wireOp",EDGE,"E306"),sQuery(id+"F0.wireOp",EDGE,"E307"),sQuery(id+"F0.wireOp",EDGE,"E308"),sQuery(id+"F0.wireOp",EDGE,"E309"),sQuery(id+"F0.wireOp",EDGE,"E310"),sQuery(id+"F0.wireOp",EDGE,"E311"),sQuery(id+"F0.wireOp",EDGE,"E312"),sQuery(id+"F0.wireOp",EDGE,"E313"),sQuery(id+"F0.wireOp",EDGE,"E314"),sQuery(id+"F0.wireOp",EDGE,"E315"),sQuery(id+"F0.wireOp",EDGE,"E316"),sQuery(id+"F0.wireOp",EDGE,"E317"),sQuery(id+"F0.wireOp",EDGE,"E318"),sQuery(id+"F0.wireOp",EDGE,"E319"),sQuery(id+"F0.wireOp",EDGE,"E320"),sQuery(id+"F0.wireOp",EDGE,"E321"),sQuery(id+"F0.wireOp",EDGE,"E322"),sQuery(id+"F0.wireOp",EDGE,"E323"),sQuery(id+"F0.wireOp",EDGE,"E324"),sQuery(id+"F0.wireOp",EDGE,"E325"),sQuery(id+"F0.wireOp",EDGE,"E326"),sQuery(id+"F0.wireOp",EDGE,"E327"),sQuery(id+"F0.wireOp",EDGE,"E328"),sQuery(id+"F0.wireOp",EDGE,"E329"),sQuery(id+"F0.wireOp",EDGE,"E330"),sQuery(id+"F0.wireOp",EDGE,"E331"),sQuery(id+"F0.wireOp",EDGE,"E332"),sQuery(id+"F0.wireOp",EDGE,"E333"),sQuery(id+"F0.wireOp",EDGE,"E334"),sQuery(id+"F0.wireOp",EDGE,"E335"),sQuery(id+"F0.wireOp",EDGE,"E336"),sQuery(id+"F0.wireOp",EDGE,"E337"),sQuery(id+"F0.wireOp",EDGE,"E338"),sQuery(id+"F0.wireOp",EDGE,"E339"),sQuery(id+"F0.wireOp",EDGE,"E340"),sQuery(id+"F0.wireOp",EDGE,"E341"),sQuery(id+"F0.wireOp",EDGE,"E342"),sQuery(id+"F0.wireOp",EDGE,"E343"),sQuery(id+"F0.wireOp",EDGE,"E344"),sQuery(id+"F0.wireOp",EDGE,"E345"),sQuery(id+"F0.wireOp",EDGE,"E346"),sQuery(id+"F0.wireOp",EDGE,"E347"),sQuery(id+"F0.wireOp",EDGE,"E348"),sQuery(id+"F0.wireOp",EDGE,"E349"),sQuery(id+"F0.wireOp",EDGE,"E350"),sQuery(id+"F0.wireOp",EDGE,"E351"),sQuery(id+"F0.wireOp",EDGE,"E352"),sQuery(id+"F0.wireOp",EDGE,"E353"),sQuery(id+"F0.wireOp",EDGE,"E354"),sQuery(id+"F0.wireOp",EDGE,"E355"),sQuery(id+"F0.wireOp",EDGE,"E356"),sQuery(id+"F0.wireOp",EDGE,"E357"),sQuery(id+"F0.wireOp",EDGE,"E358"),sQuery(id+"F0.wireOp",EDGE,"E359"),sQuery(id+"F0.wireOp",EDGE,"E360"),sQuery(id+"F0.wireOp",EDGE,"E361"),sQuery(id+"F0.wireOp",EDGE,"E362"),sQuery(id+"F0.wireOp",EDGE,"E363"),sQuery(id+"F0.wireOp",EDGE,"E364"),sQuery(id+"F0.wireOp",EDGE,"E365"),sQuery(id+"F0.wireOp",EDGE,"E366"),sQuery(id+"F0.wireOp",EDGE,"E367"),sQuery(id+"F0.wireOp",EDGE,"E368"),sQuery(id+"F0.wireOp",EDGE,"E369"),sQuery(id+"F0.wireOp",EDGE,"E370"),sQuery(id+"F0.wireOp",EDGE,"E371"),sQuery(id+"F0.wireOp",EDGE,"E372"),sQuery(id+"F0.wireOp",EDGE,"E373"),sQuery(id+"F0.wireOp",EDGE,"E374"),sQuery(id+"F0.wireOp",EDGE,"E375"),sQuery(id+"F0.wireOp",EDGE,"E376"),sQuery(id+"F0.wireOp",EDGE,"E377"),sQuery(id+"F0.wireOp",EDGE,"E378"),sQuery(id+"F0.wireOp",EDGE,"E379"),sQuery(id+"F0.wireOp",EDGE,"E380"),sQuery(id+"F0.wireOp",EDGE,"E381"),sQuery(id+"F0.wireOp",EDGE,"E382"),sQuery(id+"F0.wireOp",EDGE,"E383"),sQuery(id+"F0.wireOp",EDGE,"E384"),sQuery(id+"F0.wireOp",EDGE,"E385"),sQuery(id+"F0.wireOp",EDGE,"E386"),sQuery(id+"F0.wireOp",EDGE,"E387"),sQuery(id+"F0.wireOp",EDGE,"E388"),sQuery(id+"F0.wireOp",EDGE,"E389"),sQuery(id+"F0.wireOp",EDGE,"E390"),sQuery(id+"F0.wireOp",EDGE,"E391"),sQuery(id+"F0.wireOp",EDGE,"E392"),sQuery(id+"F0.wireOp",EDGE,"E393"),sQuery(id+"F0.wireOp",EDGE,"E394"),sQuery(id+"F0.wireOp",EDGE,"E395"),sQuery(id+"F0.wireOp",EDGE,"E396"),sQuery(id+"F0.wireOp",EDGE,"E397"),sQuery(id+"F0.wireOp",EDGE,"E398"),sQuery(id+"F0.wireOp",EDGE,"E399"),sQuery(id+"F0.wireOp",EDGE,"E400"),sQuery(id+"F0.wireOp",EDGE,"E401"),sQuery(id+"F0.wireOp",EDGE,"E402"),sQuery(id+"F0.wireOp",EDGE,"E403"),sQuery(id+"F0.wireOp",EDGE,"E404"),sQuery(id+"F0.wireOp",EDGE,"E405"),sQuery(id+"F0.wireOp",EDGE,"E406"),sQuery(id+"F0.wireOp",EDGE,"E407"),sQuery(id+"F0.wireOp",EDGE,"E408"),sQuery(id+"F0.wireOp",EDGE,"E409"),sQuery(id+"F0.wireOp",EDGE,"E410"),sQuery(id+"F0.wireOp",EDGE,"E411"),sQuery(id+"F0.wireOp",EDGE,"E412"),sQuery(id+"F0.wireOp",EDGE,"E413"),sQuery(id+"F0.wireOp",EDGE,"E414"),sQuery(id+"F0.wireOp",EDGE,"E415"),sQuery(id+"F0.wireOp",EDGE,"E416"),sQuery(id+"F0.wireOp",EDGE,"E417"),sQuery(id+"F0.wireOp",EDGE,"E418"),sQuery(id+"F0.wireOp",EDGE,"E419"),sQuery(id+"F0.wireOp",EDGE,"E420"),sQuery(id+"F0.wireOp",EDGE,"E421"),sQuery(id+"F0.wireOp",EDGE,"E422"),sQuery(id+"F0.wireOp",EDGE,"E423"),sQuery(id+"F0.wireOp",EDGE,"E424"),sQuery(id+"F0.wireOp",EDGE,"E425"),sQuery(id+"F0.wireOp",EDGE,"E426"),sQuery(id+"F0.wireOp",EDGE,"E427"),sQuery(id+"F0.wireOp",EDGE,"E428"),sQuery(id+"F0.wireOp",EDGE,"E429"),sQuery(id+"F0.wireOp",EDGE,"E430"),sQuery(id+"F0.wireOp",EDGE,"E431"),sQuery(id+"F0.wireOp",EDGE,"E432"),sQuery(id+"F0.wireOp",EDGE,"E433"),sQuery(id+"F0.wireOp",EDGE,"E434"),sQuery(id+"F0.wireOp",EDGE,"E435"),sQuery(id+"F0.wireOp",EDGE,"E436"),sQuery(id+"F0.wireOp",EDGE,"E437"),sQuery(id+"F0.wireOp",EDGE,"E438"),sQuery(id+"F0.wireOp",EDGE,"E439"),sQuery(id+"F0.wireOp",EDGE,"E440"),sQuery(id+"F0.wireOp",EDGE,"E441"),sQuery(id+"F0.wireOp",EDGE,"E442"),sQuery(id+"F0.wireOp",EDGE,"E443"),sQuery(id+"F0.wireOp",EDGE,"E444"),sQuery(id+"F0.wireOp",EDGE,"E445"),sQuery(id+"F0.wireOp",EDGE,"E446"),sQuery(id+"F0.wireOp",EDGE,"E447"),sQuery(id+"F0.wireOp",EDGE,"E448"),sQuery(id+"F0.wireOp",EDGE,"E449"),sQuery(id+"F0.wireOp",EDGE,"E450"),sQuery(id+"F0.wireOp",EDGE,"E451"),sQuery(id+"F0.wireOp",EDGE,"E452"),sQuery(id+"F0.wireOp",EDGE,"E453"),sQuery(id+"F0.wireOp",EDGE,"E454"),sQuery(id+"F0.wireOp",EDGE,"E455"),sQuery(id+"F0.wireOp",EDGE,"E456"),sQuery(id+"F0.wireOp",EDGE,"E457"),sQuery(id+"F0.wireOp",EDGE,"E458"),sQuery(id+"F0.wireOp",EDGE,"E459"),sQuery(id+"F0.wireOp",EDGE,"E460"),sQuery(id+"F0.wireOp",EDGE,"E461"),sQuery(id+"F0.wireOp",EDGE,"E462"),sQuery(id+"F0.wireOp",EDGE,"E463"),sQuery(id+"F0.wireOp",EDGE,"E464"),sQuery(id+"F0.wireOp",EDGE,"E465"),sQuery(id+"F0.wireOp",EDGE,"E466"),sQuery(id+"F0.wireOp",EDGE,"E467"),sQuery(id+"F0.wireOp",EDGE,"E468"),sQuery(id+"F0.wireOp",EDGE,"E469"),sQuery(id+"F0.wireOp",EDGE,"E470"),sQuery(id+"F0.wireOp",EDGE,"E471"),sQuery(id+"F0.wireOp",EDGE,"E472"),sQuery(id+"F0.wireOp",EDGE,"E473"),sQuery(id+"F0.wireOp",EDGE,"E474"),sQuery(id+"F0.wireOp",EDGE,"E475"),sQuery(id+"F0.wireOp",EDGE,"E476"),sQuery(id+"F0.wireOp",EDGE,"E477"),sQuery(id+"F0.wireOp",EDGE,"E478"),sQuery(id+"F0.wireOp",EDGE,"E479"),sQuery(id+"F0.wireOp",EDGE,"E480"),sQuery(id+"F0.wireOp",EDGE,"E481"),sQuery(id+"F0.wireOp",EDGE,"E482"),sQuery(id+"F0.wireOp",EDGE,"E483"),sQuery(id+"F0.wireOp",EDGE,"E484"),sQuery(id+"F0.wireOp",EDGE,"E485"),sQuery(id+"F0.wireOp",EDGE,"E486"),sQuery(id+"F0.wireOp",EDGE,"E487"),sQuery(id+"F0.wireOp",EDGE,"E488"),sQuery(id+"F0.wireOp",EDGE,"E489"),sQuery(id+"F0.wireOp",EDGE,"E490"),sQuery(id+"F0.wireOp",EDGE,"E491"),sQuery(id+"F0.wireOp",EDGE,"E492"),sQuery(id+"F0.wireOp",EDGE,"E493"),sQuery(id+"F0.wireOp",EDGE,"E494"),sQuery(id+"F0.wireOp",EDGE,"E495"),sQuery(id+"F0.wireOp",EDGE,"E496"),sQuery(id+"F0.wireOp",EDGE,"E497"),sQuery(id+"F0.wireOp",EDGE,"E498"),sQuery(id+"F0.wireOp",EDGE,"E499"),sQuery(id+"F0.wireOp",EDGE,"E500"),sQuery(id+"F0.wireOp",EDGE,"E501"),sQuery(id+"F0.wireOp",EDGE,"E502"),sQuery(id+"F0.wireOp",EDGE,"E503"),sQuery(id+"F0.wireOp",EDGE,"E504"),sQuery(id+"F0.wireOp",EDGE,"E505"),sQuery(id+"F0.wireOp",EDGE,"E506"),sQuery(id+"F0.wireOp",EDGE,"E507"),sQuery(id+"F0.wireOp",EDGE,"E508"),sQuery(id+"F0.wireOp",EDGE,"E509"),sQuery(id+"F0.wireOp",EDGE,"E510"),sQuery(id+"F0.wireOp",EDGE,"E511"),sQuery(id+"F0.wireOp",EDGE,"E512"),sQuery(id+"F0.wireOp",EDGE,"E513"),sQuery(id+"F0.wireOp",EDGE,"E514"),sQuery(id+"F0.wireOp",EDGE,"E515"),sQuery(id+"F0.wireOp",EDGE,"E516"),sQuery(id+"F0.wireOp",EDGE,"E517"),sQuery(id+"F0.wireOp",EDGE,"E518"),sQuery(id+"F0.wireOp",EDGE,"E519"),sQuery(id+"F0.wireOp",EDGE,"E520"),sQuery(id+"F0.wireOp",EDGE,"E521"),sQuery(id+"F0.wireOp",EDGE,"E522"),sQuery(id+"F0.wireOp",EDGE,"E523"),sQuery(id+"F0.wireOp",EDGE,"E524"),sQuery(id+"F0.wireOp",EDGE,"E525"),sQuery(id+"F0.wireOp",EDGE,"E526"),sQuery(id+"F0.wireOp",EDGE,"E527"),sQuery(id+"F0.wireOp",EDGE,"E528"),sQuery(id+"F0.wireOp",EDGE,"E529"),sQuery(id+"F0.wireOp",EDGE,"E530"),sQuery(id+"F0.wireOp",EDGE,"E531"),sQuery(id+"F0.wireOp",EDGE,"E532"),sQuery(id+"F0.wireOp",EDGE,"E533"),sQuery(id+"F0.wireOp",EDGE,"E534"),sQuery(id+"F0.wireOp",EDGE,"E535"),sQuery(id+"F0.wireOp",EDGE,"E536"),sQuery(id+"F0.wireOp",EDGE,"E537"),sQuery(id+"F0.wireOp",EDGE,"E538"),sQuery(id+"F0.wireOp",EDGE,"E539"),sQuery(id+"F0.wireOp",EDGE,"E540"),sQuery(id+"F0.wireOp",EDGE,"E541"),sQuery(id+"F0.wireOp",EDGE,"E542"),sQuery(id+"F0.wireOp",EDGE,"E543"),sQuery(id+"F0.wireOp",EDGE,"E544"),sQuery(id+"F0.wireOp",EDGE,"E545"),sQuery(id+"F0.wireOp",EDGE,"E546"),sQuery(id+"F0.wireOp",EDGE,"E547"),sQuery(id+"F0.wireOp",EDGE,"E548"),sQuery(id+"F0.wireOp",EDGE,"E549"),sQuery(id+"F0.wireOp",EDGE,"E550"),sQuery(id+"F0.wireOp",EDGE,"E551"),sQuery(id+"F0.wireOp",EDGE,"E552"),sQuery(id+"F0.wireOp",EDGE,"E553"),sQuery(id+"F0.wireOp",EDGE,"E554"),sQuery(id+"F0.wireOp",EDGE,"E555"),sQuery(id+"F0.wireOp",EDGE,"E556"),sQuery(id+"F0.wireOp",EDGE,"E557"),sQuery(id+"F0.wireOp",EDGE,"E558"),sQuery(id+"F0.wireOp",EDGE,"E559"),sQuery(id+"F0.wireOp",EDGE,"E560"),sQuery(id+"F0.wireOp",EDGE,"E561"),sQuery(id+"F0.wireOp",EDGE,"E562"),sQuery(id+"F0.wireOp",EDGE,"E563"),sQuery(id+"F0.wireOp",EDGE,"E564"),sQuery(id+"F0.wireOp",EDGE,"E565"),sQuery(id+"F0.wireOp",EDGE,"E566"),sQuery(id+"F0.wireOp",EDGE,"E567"),sQuery(id+"F0.wireOp",EDGE,"E568"),sQuery(id+"F0.wireOp",EDGE,"E569"),sQuery(id+"F0.wireOp",EDGE,"E570"),sQuery(id+"F0.wireOp",EDGE,"E571"),sQuery(id+"F0.wireOp",EDGE,"E572"),sQuery(id+"F0.wireOp",EDGE,"E573"),sQuery(id+"F0.wireOp",EDGE,"E574"),sQuery(id+"F0.wireOp",EDGE,"E575"),sQuery(id+"F0.wireOp",EDGE,"E576"),sQuery(id+"F0.wireOp",EDGE,"E577"),sQuery(id+"F0.wireOp",EDGE,"E578"),sQuery(id+"F0.wireOp",EDGE,"E579"),sQuery(id+"F0.wireOp",EDGE,"E580"),sQuery(id+"F0.wireOp",EDGE,"E581"),sQuery(id+"F0.wireOp",EDGE,"E582"),sQuery(id+"F0.wireOp",EDGE,"E583"),sQuery(id+"F0.wireOp",EDGE,"E584"),sQuery(id+"F0.wireOp",EDGE,"E585"),sQuery(id+"F0.wireOp",EDGE,"E586"),sQuery(id+"F0.wireOp",EDGE,"E587"),sQuery(id+"F0.wireOp",EDGE,"E588"),sQuery(id+"F0.wireOp",EDGE,"E589"),sQuery(id+"F0.wireOp",EDGE,"E590"),sQuery(id+"F0.wireOp",EDGE,"E591"),sQuery(id+"F0.wireOp",EDGE,"E592"),sQuery(id+"F0.wireOp",EDGE,"E593"),sQuery(id+"F0.wireOp",EDGE,"E594"),sQuery(id+"F0.wireOp",EDGE,"E595"),sQuery(id+"F0.wireOp",EDGE,"E596"),sQuery(id+"F0.wireOp",EDGE,"E597"),sQuery(id+"F0.wireOp",EDGE,"E598"),sQuery(id+"F0.wireOp",EDGE,"E599"),sQuery(id+"F0.wireOp",EDGE,"E600"),sQuery(id+"F0.wireOp",EDGE,"E601"),sQuery(id+"F0.wireOp",EDGE,"E602"),sQuery(id+"F0.wireOp",EDGE,"E603"),sQuery(id+"F0.wireOp",EDGE,"E604"),sQuery(id+"F0.wireOp",EDGE,"E605"),sQuery(id+"F0.wireOp",EDGE,"E606"),sQuery(id+"F0.wireOp",EDGE,"E607"),sQuery(id+"F0.wireOp",EDGE,"E608"),sQuery(id+"F0.wireOp",EDGE,"E609"),sQuery(id+"F0.wireOp",EDGE,"E610"),sQuery(id+"F0.wireOp",EDGE,"E611"),sQuery(id+"F0.wireOp",EDGE,"E612"),sQuery(id+"F0.wireOp",EDGE,"E613"),sQuery(id+"F0.wireOp",EDGE,"E614"),sQuery(id+"F0.wireOp",EDGE,"E615"),sQuery(id+"F0.wireOp",EDGE,"E616"),sQuery(id+"F0.wireOp",EDGE,"E617"),sQuery(id+"F0.wireOp",EDGE,"E618"),sQuery(id+"F0.wireOp",EDGE,"E619"),sQuery(id+"F0.wireOp",EDGE,"E620"),sQuery(id+"F0.wireOp",EDGE,"E621"),sQuery(id+"F0.wireOp",EDGE,"E622"),sQuery(id+"F0.wireOp",EDGE,"E623"),sQuery(id+"F0.wireOp",EDGE,"E624"),sQuery(id+"F0.wireOp",EDGE,"E625"),sQuery(id+"F0.wireOp",EDGE,"E626"),sQuery(id+"F0.wireOp",EDGE,"E627"),sQuery(id+"F0.wireOp",EDGE,"E628"),sQuery(id+"F0.wireOp",EDGE,"E629"),sQuery(id+"F0.wireOp",EDGE,"E630"),sQuery(id+"F0.wireOp",EDGE,"E631"),sQuery(id+"F0.wireOp",EDGE,"E632"),sQuery(id+"F0.wireOp",EDGE,"E633"),sQuery(id+"F0.wireOp",EDGE,"E634"),sQuery(id+"F0.wireOp",EDGE,"E635"),sQuery(id+"F0.wireOp",EDGE,"E636"),sQuery(id+"F0.wireOp",EDGE,"E637"),sQuery(id+"F0.wireOp",EDGE,"E638"),sQuery(id+"F0.wireOp",EDGE,"E639"),sQuery(id+"F0.wireOp",EDGE,"E640"),sQuery(id+"F0.wireOp",EDGE,"E641"),sQuery(id+"F0.wireOp",EDGE,"E642"),sQuery(id+"F0.wireOp",EDGE,"E643"),sQuery(id+"F0.wireOp",EDGE,"E644"),sQuery(id+"F0.wireOp",EDGE,"E645"),sQuery(id+"F0.wireOp",EDGE,"E646"),sQuery(id+"F0.wireOp",EDGE,"E647"),sQuery(id+"F0.wireOp",EDGE,"E648"),sQuery(id+"F0.wireOp",EDGE,"E649"),sQuery(id+"F0.wireOp",EDGE,"E650"),sQuery(id+"F0.wireOp",EDGE,"E651"),sQuery(id+"F0.wireOp",EDGE,"E652"),sQuery(id+"F0.wireOp",EDGE,"E653"),sQuery(id+"F0.wireOp",EDGE,"E654"),sQuery(id+"F0.wireOp",EDGE,"E655"),sQuery(id+"F0.wireOp",EDGE,"E656"),sQuery(id+"F0.wireOp",EDGE,"E657"),sQuery(id+"F0.wireOp",EDGE,"E658"),sQuery(id+"F0.wireOp",EDGE,"E659"),sQuery(id+"F0.wireOp",EDGE,"E660"),sQuery(id+"F0.wireOp",EDGE,"E661"),sQuery(id+"F0.wireOp",EDGE,"E662"),sQuery(id+"F0.wireOp",EDGE,"E663"),sQuery(id+"F0.wireOp",EDGE,"E664"),sQuery(id+"F0.wireOp",EDGE,"E665"),sQuery(id+"F0.wireOp",EDGE,"E666"),sQuery(id+"F0.wireOp",EDGE,"E667"),sQuery(id+"F0.wireOp",EDGE,"E668"),sQuery(id+"F0.wireOp",EDGE,"E669"),sQuery(id+"F0.wireOp",EDGE,"E670"),sQuery(id+"F0.wireOp",EDGE,"E671"),sQuery(id+"F0.wireOp",EDGE,"E672"),sQuery(id+"F0.wireOp",EDGE,"E673"),sQuery(id+"F0.wireOp",EDGE,"E674"),sQuery(id+"F0.wireOp",EDGE,"E675"),sQuery(id+"F0.wireOp",EDGE,"E676"),sQuery(id+"F0.wireOp",EDGE,"E677"),sQuery(id+"F0.wireOp",EDGE,"E678"),sQuery(id+"F0.wireOp",EDGE,"E679"),sQuery(id+"F0.wireOp",EDGE,"E680"),sQuery(id+"F0.wireOp",EDGE,"E681"),sQuery(id+"F0.wireOp",EDGE,"E682"),sQuery(id+"F0.wireOp",EDGE,"E683"),sQuery(id+"F0.wireOp",EDGE,"E684"),sQuery(id+"F0.wireOp",EDGE,"E685"),sQuery(id+"F0.wireOp",EDGE,"E686"),sQuery(id+"F0.wireOp",EDGE,"E687"),sQuery(id+"F0.wireOp",EDGE,"E688"),sQuery(id+"F0.wireOp",EDGE,"E689"),sQuery(id+"F0.wireOp",EDGE,"E690"),sQuery(id+"F0.wireOp",EDGE,"E691"),sQuery(id+"F0.wireOp",EDGE,"E692"),sQuery(id+"F0.wireOp",EDGE,"E693"),sQuery(id+"F0.wireOp",EDGE,"E694"),sQuery(id+"F0.wireOp",EDGE,"E695"),sQuery(id+"F0.wireOp",EDGE,"E696"),sQuery(id+"F0.wireOp",EDGE,"E697"),sQuery(id+"F0.wireOp",EDGE,"E698"),sQuery(id+"F0.wireOp",EDGE,"E699"),sQuery(id+"F0.wireOp",EDGE,"E700"),sQuery(id+"F0.wireOp",EDGE,"E701"),sQuery(id+"F0.wireOp",EDGE,"E702"),sQuery(id+"F0.wireOp",EDGE,"E703"),sQuery(id+"F0.wireOp",EDGE,"E704"),sQuery(id+"F0.wireOp",EDGE,"E705"),sQuery(id+"F0.wireOp",EDGE,"E706"),sQuery(id+"F0.wireOp",EDGE,"E707"),sQuery(id+"F0.wireOp",EDGE,"E708"),sQuery(id+"F0.wireOp",EDGE,"E709"),sQuery(id+"F0.wireOp",EDGE,"E710"),sQuery(id+"F0.wireOp",EDGE,"E711"),sQuery(id+"F0.wireOp",EDGE,"E712"),sQuery(id+"F0.wireOp",EDGE,"E713"),sQuery(id+"F0.wireOp",EDGE,"E714"),sQuery(id+"F0.wireOp",EDGE,"E715"),sQuery(id+"F0.wireOp",EDGE,"E716"),sQuery(id+"F0.wireOp",EDGE,"E717"),sQuery(id+"F0.wireOp",EDGE,"E718"),sQuery(id+"F0.wireOp",EDGE,"E719"),sQuery(id+"F0.wireOp",EDGE,"E720"),sQuery(id+"F0.wireOp",EDGE,"E721"),sQuery(id+"F0.wireOp",EDGE,"E722"),sQuery(id+"F0.wireOp",EDGE,"E723"),sQuery(id+"F0.wireOp",EDGE,"E724"),sQuery(id+"F0.wireOp",EDGE,"E725"),sQuery(id+"F0.wireOp",EDGE,"E726"),sQuery(id+"F0.wireOp",EDGE,"E727"),sQuery(id+"F0.wireOp",EDGE,"E728"),sQuery(id+"F0.wireOp",EDGE,"E729"),sQuery(id+"F0.wireOp",EDGE,"E730"),sQuery(id+"F0.wireOp",EDGE,"E731"),sQuery(id+"F0.wireOp",EDGE,"E732"),sQuery(id+"F0.wireOp",EDGE,"E733"),sQuery(id+"F0.wireOp",EDGE,"E734"),sQuery(id+"F0.wireOp",EDGE,"E735"),sQuery(id+"F0.wireOp",EDGE,"E736"),sQuery(id+"F0.wireOp",EDGE,"E737"),sQuery(id+"F0.wireOp",EDGE,"E738"),sQuery(id+"F0.wireOp",EDGE,"E739"),sQuery(id+"F0.wireOp",EDGE,"E740"),sQuery(id+"F0.wireOp",EDGE,"E741"),sQuery(id+"F0.wireOp",EDGE,"E742"),sQuery(id+"F0.wireOp",EDGE,"E743"),sQuery(id+"F0.wireOp",EDGE,"E744"),sQuery(id+"F0.wireOp",EDGE,"E745"),sQuery(id+"F0.wireOp",EDGE,"E746"),sQuery(id+"F0.wireOp",EDGE,"E747"),sQuery(id+"F0.wireOp",EDGE,"E748"),sQuery(id+"F0.wireOp",EDGE,"E749"),sQuery(id+"F0.wireOp",EDGE,"E750"),sQuery(id+"F0.wireOp",EDGE,"E751"),sQuery(id+"F0.wireOp",EDGE,"E752"),sQuery(id+"F0.wireOp",EDGE,"E753"),sQuery(id+"F0.wireOp",EDGE,"E754"),sQuery(id+"F0.wireOp",EDGE,"E755"),sQuery(id+"F0.wireOp",EDGE,"E756"),sQuery(id+"F0.wireOp",EDGE,"E757"),sQuery(id+"F0.wireOp",EDGE,"E758"),sQuery(id+"F0.wireOp",EDGE,"E759"),sQuery(id+"F0.wireOp",EDGE,"E760"),sQuery(id+"F0.wireOp",EDGE,"E761"),sQuery(id+"F0.wireOp",EDGE,"E762"),sQuery(id+"F0.wireOp",EDGE,"E763"),sQuery(id+"F0.wireOp",EDGE,"E764"),sQuery(id+"F0.wireOp",EDGE,"E765"),sQuery(id+"F0.wireOp",EDGE,"E766"),sQuery(id+"F0.wireOp",EDGE,"E767"),sQuery(id+"F0.wireOp",EDGE,"E768"),sQuery(id+"F0.wireOp",EDGE,"E769"),sQuery(id+"F0.wireOp",EDGE,"E770"),sQuery(id+"F0.wireOp",EDGE,"E771"),sQuery(id+"F0.wireOp",EDGE,"E772"),sQuery(id+"F0.wireOp",EDGE,"E773"),sQuery(id+"F0.wireOp",EDGE,"E774"),sQuery(id+"F0.wireOp",EDGE,"E775"),sQuery(id+"F0.wireOp",EDGE,"E776"),sQuery(id+"F0.wireOp",EDGE,"E777"),sQuery(id+"F0.wireOp",EDGE,"E778"),sQuery(id+"F0.wireOp",EDGE,"E779"),sQuery(id+"F0.wireOp",EDGE,"E780"),sQuery(id+"F0.wireOp",EDGE,"E781"),sQuery(id+"F0.wireOp",EDGE,"E782"),sQuery(id+"F0.wireOp",EDGE,"E783"),sQuery(id+"F0.wireOp",EDGE,"E784"),sQuery(id+"F0.wireOp",EDGE,"E785"),sQuery(id+"F0.wireOp",EDGE,"E786"),sQuery(id+"F0.wireOp",EDGE,"E787"),sQuery(id+"F0.wireOp",EDGE,"E788"),sQuery(id+"F0.wireOp",EDGE,"E789"),sQuery(id+"F0.wireOp",EDGE,"E790"),sQuery(id+"F0.wireOp",EDGE,"E791"),sQuery(id+"F0.wireOp",EDGE,"E792"),sQuery(id+"F0.wireOp",EDGE,"E793"),sQuery(id+"F0.wireOp",EDGE,"E794"),sQuery(id+"F0.wireOp",EDGE,"E795"),sQuery(id+"F0.wireOp",EDGE,"E796"),sQuery(id+"F0.wireOp",EDGE,"E797"),sQuery(id+"F0.wireOp",EDGE,"E798"),sQuery(id+"F0.wireOp",EDGE,"E799"),sQuery(id+"F0.wireOp",EDGE,"E800"),sQuery(id+"F0.wireOp",EDGE,"E801"),sQuery(id+"F0.wireOp",EDGE,"E802"),sQuery(id+"F0.wireOp",EDGE,"E803"),sQuery(id+"F0.wireOp",EDGE,"E804"),sQuery(id+"F0.wireOp",EDGE,"E805"),sQuery(id+"F0.wireOp",EDGE,"E806"),sQuery(id+"F0.wireOp",EDGE,"E807"),sQuery(id+"F0.wireOp",EDGE,"E808"),sQuery(id+"F0.wireOp",EDGE,"E809"),sQuery(id+"F0.wireOp",EDGE,"E810"),sQuery(id+"F0.wireOp",EDGE,"E811"),sQuery(id+"F0.wireOp",EDGE,"E812"),sQuery(id+"F0.wireOp",EDGE,"E813"),sQuery(id+"F0.wireOp",EDGE,"E814"),sQuery(id+"F0.wireOp",EDGE,"E815"),sQuery(id+"F0.wireOp",EDGE,"E816"),sQuery(id+"F0.wireOp",EDGE,"E817"),sQuery(id+"F0.wireOp",EDGE,"E818"),sQuery(id+"F0.wireOp",EDGE,"E819"),sQuery(id+"F0.wireOp",EDGE,"E820"),sQuery(id+"F0.wireOp",EDGE,"E821"),sQuery(id+"F0.wireOp",EDGE,"E822"),sQuery(id+"F0.wireOp",EDGE,"E823"),sQuery(id+"F0.wireOp",EDGE,"E824"),sQuery(id+"F0.wireOp",EDGE,"E825"),sQuery(id+"F0.wireOp",EDGE,"E826"),sQuery(id+"F0.wireOp",EDGE,"E827"),sQuery(id+"F0.wireOp",EDGE,"E828"),sQuery(id+"F0.wireOp",EDGE,"E829"),sQuery(id+"F0.wireOp",EDGE,"E830"),sQuery(id+"F0.wireOp",EDGE,"E831"),sQuery(id+"F0.wireOp",EDGE,"E832"),sQuery(id+"F0.wireOp",EDGE,"E833"),sQuery(id+"F0.wireOp",EDGE,"E834"),sQuery(id+"F0.wireOp",EDGE,"E835"),sQuery(id+"F0.wireOp",EDGE,"E836"),sQuery(id+"F0.wireOp",EDGE,"E837"),sQuery(id+"F0.wireOp",EDGE,"E838"),sQuery(id+"F0.wireOp",EDGE,"E839"),sQuery(id+"F0.wireOp",EDGE,"E840"),sQuery(id+"F0.wireOp",EDGE,"E841"),sQuery(id+"F0.wireOp",EDGE,"E842"),sQuery(id+"F0.wireOp",EDGE,"E843"),sQuery(id+"F0.wireOp",EDGE,"E844"),sQuery(id+"F0.wireOp",EDGE,"E845"),sQuery(id+"F0.wireOp",EDGE,"E846"),sQuery(id+"F0.wireOp",EDGE,"E847"),sQuery(id+"F0.wireOp",EDGE,"E848"),sQuery(id+"F0.wireOp",EDGE,"E849"),sQuery(id+"F0.wireOp",EDGE,"E850"),sQuery(id+"F0.wireOp",EDGE,"E851"),sQuery(id+"F0.wireOp",EDGE,"E852"),sQuery(id+"F0.wireOp",EDGE,"E853"),sQuery(id+"F0.wireOp",EDGE,"E854"),sQuery(id+"F0.wireOp",EDGE,"E855"),sQuery(id+"F0.wireOp",EDGE,"E856"),sQuery(id+"F0.wireOp",EDGE,"E857"),sQuery(id+"F0.wireOp",EDGE,"E858"),sQuery(id+"F0.wireOp",EDGE,"E859"),sQuery(id+"F0.wireOp",EDGE,"E860"),sQuery(id+"F0.wireOp",EDGE,"E861"),sQuery(id+"F0.wireOp",EDGE,"E862"),sQuery(id+"F0.wireOp",EDGE,"E863"),sQuery(id+"F0.wireOp",EDGE,"E864"),sQuery(id+"F0.wireOp",EDGE,"E865"),sQuery(id+"F0.wireOp",EDGE,"E866"),sQuery(id+"F0.wireOp",EDGE,"E867"),sQuery(id+"F0.wireOp",EDGE,"E868"),sQuery(id+"F0.wireOp",EDGE,"E869"),sQuery(id+"F0.wireOp",EDGE,"E870"),sQuery(id+"F0.wireOp",EDGE,"E871"),sQuery(id+"F0.wireOp",EDGE,"E872"),sQuery(id+"F0.wireOp",EDGE,"E873"),sQuery(id+"F0.wireOp",EDGE,"E874"),sQuery(id+"F0.wireOp",EDGE,"E875"),sQuery(id+"F0.wireOp",EDGE,"E876"),sQuery(id+"F0.wireOp",EDGE,"E877"),sQuery(id+"F0.wireOp",EDGE,"E878"),sQuery(id+"F0.wireOp",EDGE,"E879"),sQuery(id+"F0.wireOp",EDGE,"E880"),sQuery(id+"F0.wireOp",EDGE,"E881"),sQuery(id+"F0.wireOp",EDGE,"E882"),sQuery(id+"F0.wireOp",EDGE,"E883"),sQuery(id+"F0.wireOp",EDGE,"E884"),sQuery(id+"F0.wireOp",EDGE,"E885"),sQuery(id+"F0.wireOp",EDGE,"E886"),sQuery(id+"F0.wireOp",EDGE,"E887"),sQuery(id+"F0.wireOp",EDGE,"E888"),sQuery(id+"F0.wireOp",EDGE,"E889"),sQuery(id+"F0.wireOp",EDGE,"E890"),sQuery(id+"F0.wireOp",EDGE,"E891"),sQuery(id+"F0.wireOp",EDGE,"E892"),sQuery(id+"F0.wireOp",EDGE,"E893"),sQuery(id+"F0.wireOp",EDGE,"E894"),sQuery(id+"F0.wireOp",EDGE,"E895"),sQuery(id+"F0.wireOp",EDGE,"E896"),sQuery(id+"F0.wireOp",EDGE,"E897"),sQuery(id+"F0.wireOp",EDGE,"E898"),sQuery(id+"F0.wireOp",EDGE,"E899"),sQuery(id+"F0.wireOp",EDGE,"E900"),sQuery(id+"F0.wireOp",EDGE,"E901"),sQuery(id+"F0.wireOp",EDGE,"E902"),sQuery(id+"F0.wireOp",EDGE,"E903"),sQuery(id+"F0.wireOp",EDGE,"E904"),sQuery(id+"F0.wireOp",EDGE,"E905"),sQuery(id+"F0.wireOp",EDGE,"E906"),sQuery(id+"F0.wireOp",EDGE,"E907"),sQuery(id+"F0.wireOp",EDGE,"E908"),sQuery(id+"F0.wireOp",EDGE,"E909"),sQuery(id+"F0.wireOp",EDGE,"E910"),sQuery(id+"F0.wireOp",EDGE,"E911"),sQuery(id+"F0.wireOp",EDGE,"E912"),sQuery(id+"F0.wireOp",EDGE,"E913"),sQuery(id+"F0.wireOp",EDGE,"E914"),sQuery(id+"F0.wireOp",EDGE,"E915"),sQuery(id+"F0.wireOp",EDGE,"E916"),sQuery(id+"F0.wireOp",EDGE,"E917"),sQuery(id+"F0.wireOp",EDGE,"E918"),sQuery(id+"F0.wireOp",EDGE,"E919"),sQuery(id+"F0.wireOp",EDGE,"E920"),sQuery(id+"F0.wireOp",EDGE,"E921"),sQuery(id+"F0.wireOp",EDGE,"E922"),sQuery(id+"F0.wireOp",EDGE,"E923"),sQuery(id+"F0.wireOp",EDGE,"E924"),sQuery(id+"F0.wireOp",EDGE,"E925"),sQuery(id+"F0.wireOp",EDGE,"E926"),sQuery(id+"F0.wireOp",EDGE,"E927"),sQuery(id+"F0.wireOp",EDGE,"E928"),sQuery(id+"F0.wireOp",EDGE,"E929"),sQuery(id+"F0.wireOp",EDGE,"E930"),sQuery(id+"F0.wireOp",EDGE,"E931"),sQuery(id+"F0.wireOp",EDGE,"E932"),sQuery(id+"F0.wireOp",EDGE,"E933"),sQuery(id+"F0.wireOp",EDGE,"E934"),sQuery(id+"F0.wireOp",EDGE,"E935"),sQuery(id+"F0.wireOp",EDGE,"E936"),sQuery(id+"F0.wireOp",EDGE,"E937"),sQuery(id+"F0.wireOp",EDGE,"E938"),sQuery(id+"F0.wireOp",EDGE,"E939"),sQuery(id+"F0.wireOp",EDGE,"E940"),sQuery(id+"F0.wireOp",EDGE,"E941"),sQuery(id+"F0.wireOp",EDGE,"E942"),sQuery(id+"F0.wireOp",EDGE,"E943"),sQuery(id+"F0.wireOp",EDGE,"E944"),sQuery(id+"F0.wireOp",EDGE,"E945"),sQuery(id+"F0.wireOp",EDGE,"E946"),sQuery(id+"F0.wireOp",EDGE,"E947"),sQuery(id+"F0.wireOp",EDGE,"E948"),sQuery(id+"F0.wireOp",EDGE,"E949"),sQuery(id+"F0.wireOp",EDGE,"E950"),sQuery(id+"F0.wireOp",EDGE,"E951"),sQuery(id+"F0.wireOp",EDGE,"E952"),sQuery(id+"F0.wireOp",EDGE,"E953"),sQuery(id+"F0.wireOp",EDGE,"E954"),sQuery(id+"F0.wireOp",EDGE,"E955"),sQuery(id+"F0.wireOp",EDGE,"E956"),sQuery(id+"F0.wireOp",EDGE,"E957"),sQuery(id+"F0.wireOp",EDGE,"E958"),sQuery(id+"F0.wireOp",EDGE,"E959"),sQuery(id+"F0.wireOp",EDGE,"E960"),sQuery(id+"F0.wireOp",EDGE,"E961"),sQuery(id+"F0.wireOp",EDGE,"E962"),sQuery(id+"F0.wireOp",EDGE,"E963"),sQuery(id+"F0.wireOp",EDGE,"E964"),sQuery(id+"F0.wireOp",EDGE,"E965"),sQuery(id+"F0.wireOp",EDGE,"E966"),sQuery(id+"F0.wireOp",EDGE,"E967"),sQuery(id+"F0.wireOp",EDGE,"E968"),sQuery(id+"F0.wireOp",EDGE,"E969"),sQuery(id+"F0.wireOp",EDGE,"E970"),sQuery(id+"F0.wireOp",EDGE,"E971"),sQuery(id+"F0.wireOp",EDGE,"E972"),sQuery(id+"F0.wireOp",EDGE,"E973"),sQuery(id+"F0.wireOp",EDGE,"E974"),sQuery(id+"F0.wireOp",EDGE,"E975"),sQuery(id+"F0.wireOp",EDGE,"E976"),sQuery(id+"F0.wireOp",EDGE,"E977"),sQuery(id+"F0.wireOp",EDGE,"E978"),sQuery(id+"F0.wireOp",EDGE,"E979"),sQuery(id+"F0.wireOp",EDGE,"E980"),sQuery(id+"F0.wireOp",EDGE,"E981"),sQuery(id+"F0.wireOp",EDGE,"E982"),sQuery(id+"F0.wireOp",EDGE,"E983"),sQuery(id+"F0.wireOp",EDGE,"E984"),sQuery(id+"F0.wireOp",EDGE,"E985"),sQuery(id+"F0.wireOp",EDGE,"E986"),sQuery(id+"F0.wireOp",EDGE,"E987"),sQuery(id+"F0.wireOp",EDGE,"E988"),sQuery(id+"F0.wireOp",EDGE,"E989"),sQuery(id+"F0.wireOp",EDGE,"E990"),sQuery(id+"F0.wireOp",EDGE,"E991"),sQuery(id+"F0.wireOp",EDGE,"E992"),sQuery(id+"F0.wireOp",EDGE,"E993"),sQuery(id+"F0.wireOp",EDGE,"E994"),sQuery(id+"F0.wireOp",EDGE,"E995"),sQuery(id+"F0.wireOp",EDGE,"E996"),sQuery(id+"F0.wireOp",EDGE,"E997"),sQuery(id+"F0.wireOp",EDGE,"E998"),sQuery(id+"F0.wireOp",EDGE,"E999"),sQuery(id+"F0.wireOp",EDGE,"E1000"),sQuery(id+"F0.wireOp",EDGE,"E1001"),sQuery(id+"F0.wireOp",EDGE,"E1002"),sQuery(id+"F0.wireOp",EDGE,"E1003"),sQuery(id+"F0.wireOp",EDGE,"E1004"),sQuery(id+"F0.wireOp",EDGE,"E1005"),sQuery(id+"F0.wireOp",EDGE,"E1006"),sQuery(id+"F0.wireOp",EDGE,"E1007"),sQuery(id+"F0.wireOp",EDGE,"E1008"),sQuery(id+"F0.wireOp",EDGE,"E1009"),sQuery(id+"F0.wireOp",EDGE,"E1010"),sQuery(id+"F0.wireOp",EDGE,"E1011"),sQuery(id+"F0.wireOp",EDGE,"E1012"),sQuery(id+"F0.wireOp",EDGE,"E1013"),sQuery(id+"F0.wireOp",EDGE,"E1014"),sQuery(id+"F0.wireOp",EDGE,"E1015"),sQuery(id+"F0.wireOp",EDGE,"E1016"),sQuery(id+"F0.wireOp",EDGE,"E1017"),sQuery(id+"F0.wireOp",EDGE,"E1018"),sQuery(id+"F0.wireOp",EDGE,"E1019"),sQuery(id+"F0.wireOp",EDGE,"E1020"),sQuery(id+"F0.wireOp",EDGE,"E1021"),sQuery(id+"F0.wireOp",EDGE,"E1022"),sQuery(id+"F0.wireOp",EDGE,"E1023"),sQuery(id+"F0.wireOp",EDGE,"E1024"),sQuery(id+"F0.wireOp",EDGE,"E1025"),sQuery(id+"F0.wireOp",EDGE,"E1026"),sQuery(id+"F0.wireOp",EDGE,"E1027"),sQuery(id+"F0.wireOp",EDGE,"E1028"),sQuery(id+"F0.wireOp",EDGE,"E1029"),sQuery(id+"F0.wireOp",EDGE,"E1030"),sQuery(id+"F0.wireOp",EDGE,"E1031"),sQuery(id+"F0.wireOp",EDGE,"E1032"),sQuery(id+"F0.wireOp",EDGE,"E1033"),sQuery(id+"F0.wireOp",EDGE,"E1034"),sQuery(id+"F0.wireOp",EDGE,"E1035"),sQuery(id+"F0.wireOp",EDGE,"E1036"),sQuery(id+"F0.wireOp",EDGE,"E1037"),sQuery(id+"F0.wireOp",EDGE,"E1038"),sQuery(id+"F0.wireOp",EDGE,"E1039"),sQuery(id+"F0.wireOp",EDGE,"E1040"),sQuery(id+"F0.wireOp",EDGE,"E1041"),sQuery(id+"F0.wireOp",EDGE,"E1042"),sQuery(id+"F0.wireOp",EDGE,"E1043"),sQuery(id+"F0.wireOp",EDGE,"E1044"),sQuery(id+"F0.wireOp",EDGE,"E1045"),sQuery(id+"F0.wireOp",EDGE,"E1046"),sQuery(id+"F0.wireOp",EDGE,"E1047"),sQuery(id+"F0.wireOp",EDGE,"E1048"),sQuery(id+"F0.wireOp",EDGE,"E1049"),sQuery(id+"F0.wireOp",EDGE,"E1050"),sQuery(id+"F0.wireOp",EDGE,"E1051"),sQuery(id+"F0.wireOp",EDGE,"E1052"),sQuery(id+"F0.wireOp",EDGE,"E1053"),sQuery(id+"F0.wireOp",EDGE,"E1054"),sQuery(id+"F0.wireOp",EDGE,"E1055"),sQuery(id+"F0.wireOp",EDGE,"E1056"),sQuery(id+"F0.wireOp",EDGE,"E1057"),sQuery(id+"F0.wireOp",EDGE,"E1058"),sQuery(id+"F0.wireOp",EDGE,"E1059"),sQuery(id+"F0.wireOp",EDGE,"E1060"),sQuery(id+"F0.wireOp",EDGE,"E1061"),sQuery(id+"F0.wireOp",EDGE,"E1062"),sQuery(id+"F0.wireOp",EDGE,"E1063"),sQuery(id+"F0.wireOp",EDGE,"E1064"),sQuery(id+"F0.wireOp",EDGE,"E1065"),sQuery(id+"F0.wireOp",EDGE,"E1066"),sQuery(id+"F0.wireOp",EDGE,"E1067"),sQuery(id+"F0.wireOp",EDGE,"E1068"),sQuery(id+"F0.wireOp",EDGE,"E1069"),sQuery(id+"F0.wireOp",EDGE,"E1070"),sQuery(id+"F0.wireOp",EDGE,"E1071"),sQuery(id+"F0.wireOp",EDGE,"E1072"),sQuery(id+"F0.wireOp",EDGE,"E1073"),sQuery(id+"F0.wireOp",EDGE,"E1074"),sQuery(id+"F0.wireOp",EDGE,"E1075"),sQuery(id+"F0.wireOp",EDGE,"E1076"),sQuery(id+"F0.wireOp",EDGE,"E1077"),sQuery(id+"F0.wireOp",EDGE,"E1078"),sQuery(id+"F0.wireOp",EDGE,"E1079"),sQuery(id+"F0.wireOp",EDGE,"E1080"),sQuery(id+"F0.wireOp",EDGE,"E1081"),sQuery(id+"F0.wireOp",EDGE,"E1082"),sQuery(id+"F0.wireOp",EDGE,"E1083"),sQuery(id+"F0.wireOp",EDGE,"E1084"),sQuery(id+"F0.wireOp",EDGE,"E1085"),sQuery(id+"F0.wireOp",EDGE,"E1086"),sQuery(id+"F0.wireOp",EDGE,"E1087"),sQuery(id+"F0.wireOp",EDGE,"E1088"),sQuery(id+"F0.wireOp",EDGE,"E1089"),sQuery(id+"F0.wireOp",EDGE,"E1090"),sQuery(id+"F0.wireOp",EDGE,"E1091"),sQuery(id+"F0.wireOp",EDGE,"E1092"),sQuery(id+"F0.wireOp",EDGE,"E1093"),sQuery(id+"F0.wireOp",EDGE,"E1094"),sQuery(id+"F0.wireOp",EDGE,"E1095"),sQuery(id+"F0.wireOp",EDGE,"E1096"),sQuery(id+"F0.wireOp",EDGE,"E1097"),sQuery(id+"F0.wireOp",EDGE,"E1098"),sQuery(id+"F0.wireOp",EDGE,"E1099"),sQuery(id+"F0.wireOp",EDGE,"E1100"),sQuery(id+"F0.wireOp",EDGE,"E1101"),sQuery(id+"F0.wireOp",EDGE,"E1102"),sQuery(id+"F0.wireOp",EDGE,"E1103"),sQuery(id+"F0.wireOp",EDGE,"E1104"),sQuery(id+"F0.wireOp",EDGE,"E1105"),sQuery(id+"F0.wireOp",EDGE,"E1106"),sQuery(id+"F0.wireOp",EDGE,"E1107"),sQuery(id+"F0.wireOp",EDGE,"E1108"),sQuery(id+"F0.wireOp",EDGE,"E1109"),sQuery(id+"F0.wireOp",EDGE,"E1110"),sQuery(id+"F0.wireOp",EDGE,"E1111"),sQuery(id+"F0.wireOp",EDGE,"E1112"),sQuery(id+"F0.wireOp",EDGE,"E1113"),sQuery(id+"F0.wireOp",EDGE,"E1114"),sQuery(id+"F0.wireOp",EDGE,"E1115"),sQuery(id+"F0.wireOp",EDGE,"E1116"),sQuery(id+"F0.wireOp",EDGE,"E1117"),sQuery(id+"F0.wireOp",EDGE,"E1118"),sQuery(id+"F0.wireOp",EDGE,"E1119"),sQuery(id+"F0.wireOp",EDGE,"E1120"),sQuery(id+"F0.wireOp",EDGE,"E1121"),sQuery(id+"F0.wireOp",EDGE,"E1122"),sQuery(id+"F0.wireOp",EDGE,"E1123"),sQuery(id+"F0.wireOp",EDGE,"E1124"),sQuery(id+"F0.wireOp",EDGE,"E1125"),sQuery(id+"F0.wireOp",EDGE,"E1126"),sQuery(id+"F0.wireOp",EDGE,"E1127"),sQuery(id+"F0.wireOp",EDGE,"E1128"),sQuery(id+"F0.wireOp",EDGE,"E1129"),sQuery(id+"F0.wireOp",EDGE,"E1130"),sQuery(id+"F0.wireOp",EDGE,"E1131"),sQuery(id+"F0.wireOp",EDGE,"E1132"),sQuery(id+"F0.wireOp",EDGE,"E1133"),sQuery(id+"F0.wireOp",EDGE,"E1134"),sQuery(id+"F0.wireOp",EDGE,"E1135"),sQuery(id+"F0.wireOp",EDGE,"E1136"),sQuery(id+"F0.wireOp",EDGE,"E1137"),sQuery(id+"F0.wireOp",EDGE,"E1138"),sQuery(id+"F0.wireOp",EDGE,"E1139"),sQuery(id+"F0.wireOp",EDGE,"E1140"),sQuery(id+"F0.wireOp",EDGE,"E1141"),sQuery(id+"F0.wireOp",EDGE,"E1142"),sQuery(id+"F0.wireOp",EDGE,"E1143"),sQuery(id+"F0.wireOp",EDGE,"E1144"),sQuery(id+"F0.wireOp",EDGE,"E1145"),sQuery(id+"F0.wireOp",EDGE,"E1146"),sQuery(id+"F0.wireOp",EDGE,"E1147"),sQuery(id+"F0.wireOp",EDGE,"E1148"),sQuery(id+"F0.wireOp",EDGE,"E1149"),sQuery(id+"F0.wireOp",EDGE,"E1150"),sQuery(id+"F0.wireOp",EDGE,"E1151"),sQuery(id+"F0.wireOp",EDGE,"E1152"),sQuery(id+"F0.wireOp",EDGE,"E1153"),sQuery(id+"F0.wireOp",EDGE,"E1154"),sQuery(id+"F0.wireOp",EDGE,"E1155"),sQuery(id+"F0.wireOp",EDGE,"E1156"),sQuery(id+"F0.wireOp",EDGE,"E1157"),sQuery(id+"F0.wireOp",EDGE,"E1158"),sQuery(id+"F0.wireOp",EDGE,"E1159"),sQuery(id+"F0.wireOp",EDGE,"E1160"),sQuery(id+"F0.wireOp",EDGE,"E1161"),sQuery(id+"F0.wireOp",EDGE,"E1162"),sQuery(id+"F0.wireOp",EDGE,"E1163"),sQuery(id+"F0.wireOp",EDGE,"E1164"),sQuery(id+"F0.wireOp",EDGE,"E1165"),sQuery(id+"F0.wireOp",EDGE,"E1166"),sQuery(id+"F0.wireOp",EDGE,"E1167"),sQuery(id+"F0.wireOp",EDGE,"E1168"),sQuery(id+"F0.wireOp",EDGE,"E1169"),sQuery(id+"F0.wireOp",EDGE,"E1170"),sQuery(id+"F0.wireOp",EDGE,"E1171"),sQuery(id+"F0.wireOp",EDGE,"E1172"),sQuery(id+"F0.wireOp",EDGE,"E1173"),sQuery(id+"F0.wireOp",EDGE,"E1174"),sQuery(id+"F0.wireOp",EDGE,"E1175"),sQuery(id+"F0.wireOp",EDGE,"E1176"),sQuery(id+"F0.wireOp",EDGE,"E1177"),sQuery(id+"F0.wireOp",EDGE,"E1178"),sQuery(id+"F0.wireOp",EDGE,"E1179"),sQuery(id+"F0.wireOp",EDGE,"E1180"),sQuery(id+"F0.wireOp",EDGE,"E1181"),sQuery(id+"F0.wireOp",EDGE,"E1182"),sQuery(id+"F0.wireOp",EDGE,"E1183"),sQuery(id+"F0.wireOp",EDGE,"E1184"),sQuery(id+"F0.wireOp",EDGE,"E1185"),sQuery(id+"F0.wireOp",EDGE,"E1186"),sQuery(id+"F0.wireOp",EDGE,"E1187"),sQuery(id+"F0.wireOp",EDGE,"E1188"),sQuery(id+"F0.wireOp",EDGE,"E1189"),sQuery(id+"F0.wireOp",EDGE,"E1190"),sQuery(id+"F0.wireOp",EDGE,"E1191"),sQuery(id+"F0.wireOp",EDGE,"E1192"),sQuery(id+"F0.wireOp",EDGE,"E1193"),sQuery(id+"F0.wireOp",EDGE,"E1194"),sQuery(id+"F0.wireOp",EDGE,"E1195"),sQuery(id+"F0.wireOp",EDGE,"E1196"),sQuery(id+"F0.wireOp",EDGE,"E1197"),sQuery(id+"F0.wireOp",EDGE,"E1198"),sQuery(id+"F0.wireOp",EDGE,"E1199"),sQuery(id+"F0.wireOp",EDGE,"E1200"),sQuery(id+"F0.wireOp",EDGE,"E1201"),sQuery(id+"F0.wireOp",EDGE,"E1202"),sQuery(id+"F0.wireOp",EDGE,"E1203"),sQuery(id+"F0.wireOp",EDGE,"E1204"),sQuery(id+"F0.wireOp",EDGE,"E1205"),sQuery(id+"F0.wireOp",EDGE,"E1206"),sQuery(id+"F0.wireOp",EDGE,"E1207"),sQuery(id+"F0.wireOp",EDGE,"E1208"),sQuery(id+"F0.wireOp",EDGE,"E1209"),sQuery(id+"F0.wireOp",EDGE,"E1210"),sQuery(id+"F0.wireOp",EDGE,"E1211"),sQuery(id+"F0.wireOp",EDGE,"E1212"),sQuery(id+"F0.wireOp",EDGE,"E1213"),sQuery(id+"F0.wireOp",EDGE,"E1214"),sQuery(id+"F0.wireOp",EDGE,"E1215"),sQuery(id+"F0.wireOp",EDGE,"E1216"),sQuery(id+"F0.wireOp",EDGE,"E1217"),sQuery(id+"F0.wireOp",EDGE,"E1218"),sQuery(id+"F0.wireOp",EDGE,"E1219"),sQuery(id+"F0.wireOp",EDGE,"E1220"),sQuery(id+"F0.wireOp",EDGE,"E1221"),sQuery(id+"F0.wireOp",EDGE,"E1222"),sQuery(id+"F0.wireOp",EDGE,"E1223"),sQuery(id+"F0.wireOp",EDGE,"E1224"),sQuery(id+"F0.wireOp",EDGE,"E1225"),sQuery(id+"F0.wireOp",EDGE,"E1226"),sQuery(id+"F0.wireOp",EDGE,"E1227"),sQuery(id+"F0.wireOp",EDGE,"E1228"),sQuery(id+"F0.wireOp",EDGE,"E1229"),sQuery(id+"F0.wireOp",EDGE,"E1230"),sQuery(id+"F0.wireOp",EDGE,"E1231"),sQuery(id+"F0.wireOp",EDGE,"E1232"),sQuery(id+"F0.wireOp",EDGE,"E1233"),sQuery(id+"F0.wireOp",EDGE,"E1234"),sQuery(id+"F0.wireOp",EDGE,"E1235"),sQuery(id+"F0.wireOp",EDGE,"E1236"),sQuery(id+"F0.wireOp",EDGE,"E1237"),sQuery(id+"F0.wireOp",EDGE,"E1238"),sQuery(id+"F0.wireOp",EDGE,"E1239"),sQuery(id+"F0.wireOp",EDGE,"E1240"),sQuery(id+"F0.wireOp",EDGE,"E1241"),sQuery(id+"F0.wireOp",EDGE,"E1242"),sQuery(id+"F0.wireOp",EDGE,"E1243"),sQuery(id+"F0.wireOp",EDGE,"E1244"),sQuery(id+"F0.wireOp",EDGE,"E1245"),sQuery(id+"F0.wireOp",EDGE,"E1246"),sQuery(id+"F0.wireOp",EDGE,"E1247"),sQuery(id+"F0.wireOp",EDGE,"E1248"),sQuery(id+"F0.wireOp",EDGE,"E1249"),sQuery(id+"F0.wireOp",EDGE,"E1250"),sQuery(id+"F0.wireOp",EDGE,"E1251"),sQuery(id+"F0.wireOp",EDGE,"E1252"),sQuery(id+"F0.wireOp",EDGE,"E1253"),sQuery(id+"F0.wireOp",EDGE,"E1254"),sQuery(id+"F0.wireOp",EDGE,"E1255"),sQuery(id+"F0.wireOp",EDGE,"E1256"),sQuery(id+"F0.wireOp",EDGE,"E1257"),sQuery(id+"F0.wireOp",EDGE,"E1258"),sQuery(id+"F0.wireOp",EDGE,"E1259"),sQuery(id+"F0.wireOp",EDGE,"E1260"),sQuery(id+"F0.wireOp",EDGE,"E1261"),sQuery(id+"F0.wireOp",EDGE,"E1262"),sQuery(id+"F0.wireOp",EDGE,"E1263"),sQuery(id+"F0.wireOp",EDGE,"E1264"),sQuery(id+"F0.wireOp",EDGE,"E1265"),sQuery(id+"F0.wireOp",EDGE,"E1266"),sQuery(id+"F0.wireOp",EDGE,"E1267"),sQuery(id+"F0.wireOp",EDGE,"E1268"),sQuery(id+"F0.wireOp",EDGE,"E1269"),sQuery(id+"F0.wireOp",EDGE,"E1270"),sQuery(id+"F0.wireOp",EDGE,"E1271"),sQuery(id+"F0.wireOp",EDGE,"E1272"),sQuery(id+"F0.wireOp",EDGE,"E1273"),sQuery(id+"F0.wireOp",EDGE,"E1274"),sQuery(id+"F0.wireOp",EDGE,"E1275"),sQuery(id+"F0.wireOp",EDGE,"E1276"),sQuery(id+"F0.wireOp",EDGE,"E1277"),sQuery(id+"F0.wireOp",EDGE,"E1278"),sQuery(id+"F0.wireOp",EDGE,"E1279"),sQuery(id+"F0.wireOp",EDGE,"E1280"),sQuery(id+"F0.wireOp",EDGE,"E1281"),sQuery(id+"F0.wireOp",EDGE,"E1282"),sQuery(id+"F0.wireOp",EDGE,"E1283"),sQuery(id+"F0.wireOp",EDGE,"E1284"),sQuery(id+"F0.wireOp",EDGE,"E1285"),sQuery(id+"F0.wireOp",EDGE,"E1286"),sQuery(id+"F0.wireOp",EDGE,"E1287"),sQuery(id+"F0.wireOp",EDGE,"E1288"),sQuery(id+"F0.wireOp",EDGE,"E1289"),sQuery(id+"F0.wireOp",EDGE,"E1290"),sQuery(id+"F0.wireOp",EDGE,"E1291"),sQuery(id+"F0.wireOp",EDGE,"E1292"),sQuery(id+"F0.wireOp",EDGE,"E1293"),sQuery(id+"F0.wireOp",EDGE,"E1294"),sQuery(id+"F0.wireOp",EDGE,"E1295"),sQuery(id+"F0.wireOp",EDGE,"E1296"),sQuery(id+"F0.wireOp",EDGE,"E1297"),sQuery(id+"F0.wireOp",EDGE,"E1298"),sQuery(id+"F0.wireOp",EDGE,"E1299"),sQuery(id+"F0.wireOp",EDGE,"E1300"),sQuery(id+"F0.wireOp",EDGE,"E1301"),sQuery(id+"F0.wireOp",EDGE,"E1302"),sQuery(id+"F0.wireOp",EDGE,"E1303"),sQuery(id+"F0.wireOp",EDGE,"E1304"),sQuery(id+"F0.wireOp",EDGE,"E1305"),sQuery(id+"F0.wireOp",EDGE,"E1306"),sQuery(id+"F0.wireOp",EDGE,"E1307"),sQuery(id+"F0.wireOp",EDGE,"E1308"),sQuery(id+"F0.wireOp",EDGE,"E1309"),sQuery(id+"F0.wireOp",EDGE,"E1310"),sQuery(id+"F0.wireOp",EDGE,"E1311"),sQuery(id+"F0.wireOp",EDGE,"E1312"),sQuery(id+"F0.wireOp",EDGE,"E1313"),sQuery(id+"F0.wireOp",EDGE,"E1314"),sQuery(id+"F0.wireOp",EDGE,"E1315"),sQuery(id+"F0.wireOp",EDGE,"E1316"),sQuery(id+"F0.wireOp",EDGE,"E1317"),sQuery(id+"F0.wireOp",EDGE,"E1318"),sQuery(id+"F0.wireOp",EDGE,"E1319"),sQuery(id+"F0.wireOp",EDGE,"E1320"),sQuery(id+"F0.wireOp",EDGE,"E1321"),sQuery(id+"F0.wireOp",EDGE,"E1322")])]});
            booleanBodies(context, id + "F9", {"operationType" : BooleanOperationType.UNION, "tools" : qUnion([Q0, Q1])});
        }
        {
            var Q0;
            Q0=makeQuery(id+"F7.opExtrude","SWEPT_FACE",FACE,{"disambiguationData":[OSD([sQuery(id+"F6.wireOp",EDGE,"E1329")])]});
            extrude(context, id + "F10", {"entities" : qUnion([Q0]), "operationType" : NewBodyOperationType.REMOVE, "endBound" : BoundingType.THROUGH_ALL, "oppositeDirection" : true, "depth" : 25 * mm});
        }
        {
            var Q0;
            Q0=makeQuery(id+"F5.opExtrude","SWEPT_FACE",FACE,{"disambiguationData":[OSD([sQuery(id+"F4.wireOp",EDGE,"E1326")])]});
            extrude(context, id + "F11", {"entities" : qUnion([Q0]), "operationType" : NewBodyOperationType.REMOVE, "endBound" : BoundingType.THROUGH_ALL, "oppositeDirection" : true, "depth" : 25 * mm});
        }
        {
            var Q0;
            {var subQ0=sQuery(id+"F0.wireOp",EDGE,"E2");Q0=makeQuery(id+"F11.boolean.opBoolean","MERGE",FACE,{"derivedFrom":[makeQuery(id+"F10.boolean.opBoolean","MERGE",FACE,{"derivedFrom":[makeQuery(id+"F1.opExtrude","SWEPT_FACE",FACE,{"disambiguationData":[OSD([subQ0])]}),makeQuery(id+"F10.opExtrude","SWEPT_FACE",FACE,{"disambiguationData":[OSD([subQ0,sQuery(id+"F6.wireOp",EDGE,"E1329")])]})]}),makeQuery(id+"F11.opExtrude","SWEPT_FACE",FACE,{"disambiguationData":[OSD([subQ0,sQuery(id+"F4.wireOp",EDGE,"E1326")])]})]});}
            var sketch = newSketch(context, id + "F12", { "sketchPlane" : qUnion([Q0])});
            skLineSegment(sketch, "E1332", {"start": v(-647.84, -236.63) * mm, "end": v(-626.26, -257.47) * mm});
            skLineSegment(sketch, "E1333", {"start": v(-626.26, -257.47) * mm, "end": v(-409.5, -33) * mm});
            skLineSegment(sketch, "E1334", {"start": v(-409.5, -33) * mm, "end": v(409.5, -33) * mm});
            skLineSegment(sketch, "E1335", {"start": v(409.5, -33) * mm, "end": v(626.26, -257.47) * mm});
            skLineSegment(sketch, "E1336", {"start": v(626.26, -257.47) * mm, "end": v(647.84, -236.63) * mm});
            skSolve(sketch);
        }
        {
            var Q0;
            Q0=makeQuery(id+"F12.imprint","IMPRINT",FACE,{"disambiguationData":[TD([[makeQuery(id+"F12.imprint","IMPRINT",EDGE,{"derivedFrom":sQuery(id+"F12.wireOp",EDGE,"E1332")}),1.0]])]});
            extrude(context, id + "F13", {"entities" : qUnion([Q0]), "operationType" : NewBodyOperationType.ADD, "oppositeDirection" : true, "depth" : 2 * mm});
        }
        {
            var Q0;
            Q0=makeQuery(id+"F1.opExtrude","CAP_FACE",FACE,{"disambiguationData":[OSD([sQuery(id+"F0.wireOp",EDGE,"E2"),sQuery(id+"F0.wireOp",EDGE,"E4"),sQuery(id+"F0.wireOp",EDGE,"E5"),sQuery(id+"F0.wireOp",EDGE,"E6"),sQuery(id+"F0.wireOp",EDGE,"E7"),sQuery(id+"F0.wireOp",EDGE,"E8"),sQuery(id+"F0.wireOp",EDGE,"E9"),sQuery(id+"F0.wireOp",EDGE,"E10"),sQuery(id+"F0.wireOp",EDGE,"E11"),sQuery(id+"F0.wireOp",EDGE,"E12"),sQuery(id+"F0.wireOp",EDGE,"E13"),sQuery(id+"F0.wireOp",EDGE,"E14"),sQuery(id+"F0.wireOp",EDGE,"E15"),sQuery(id+"F0.wireOp",EDGE,"E16"),sQuery(id+"F0.wireOp",EDGE,"E17"),sQuery(id+"F0.wireOp",EDGE,"E18"),sQuery(id+"F0.wireOp",EDGE,"E19"),sQuery(id+"F0.wireOp",EDGE,"E20"),sQuery(id+"F0.wireOp",EDGE,"E21"),sQuery(id+"F0.wireOp",EDGE,"E22"),sQuery(id+"F0.wireOp",EDGE,"E23"),sQuery(id+"F0.wireOp",EDGE,"E24"),sQuery(id+"F0.wireOp",EDGE,"E25"),sQuery(id+"F0.wireOp",EDGE,"E26"),sQuery(id+"F0.wireOp",EDGE,"E27"),sQuery(id+"F0.wireOp",EDGE,"E28"),sQuery(id+"F0.wireOp",EDGE,"E29"),sQuery(id+"F0.wireOp",EDGE,"E30"),sQuery(id+"F0.wireOp",EDGE,"E31"),sQuery(id+"F0.wireOp",EDGE,"E32"),sQuery(id+"F0.wireOp",EDGE,"E33"),sQuery(id+"F0.wireOp",EDGE,"E34"),sQuery(id+"F0.wireOp",EDGE,"E35"),sQuery(id+"F0.wireOp",EDGE,"E36"),sQuery(id+"F0.wireOp",EDGE,"E37"),sQuery(id+"F0.wireOp",EDGE,"E38"),sQuery(id+"F0.wireOp",EDGE,"E39"),sQuery(id+"F0.wireOp",EDGE,"E40"),sQuery(id+"F0.wireOp",EDGE,"E41"),sQuery(id+"F0.wireOp",EDGE,"E42"),sQuery(id+"F0.wireOp",EDGE,"E43"),sQuery(id+"F0.wireOp",EDGE,"E44"),sQuery(id+"F0.wireOp",EDGE,"E45"),sQuery(id+"F0.wireOp",EDGE,"E46"),sQuery(id+"F0.wireOp",EDGE,"E47"),sQuery(id+"F0.wireOp",EDGE,"E48"),sQuery(id+"F0.wireOp",EDGE,"E49"),sQuery(id+"F0.wireOp",EDGE,"E50"),sQuery(id+"F0.wireOp",EDGE,"E51"),sQuery(id+"F0.wireOp",EDGE,"E52"),sQuery(id+"F0.wireOp",EDGE,"E53"),sQuery(id+"F0.wireOp",EDGE,"E54"),sQuery(id+"F0.wireOp",EDGE,"E55"),sQuery(id+"F0.wireOp",EDGE,"E56"),sQuery(id+"F0.wireOp",EDGE,"E57"),sQuery(id+"F0.wireOp",EDGE,"E58"),sQuery(id+"F0.wireOp",EDGE,"E59"),sQuery(id+"F0.wireOp",EDGE,"E60"),sQuery(id+"F0.wireOp",EDGE,"E61"),sQuery(id+"F0.wireOp",EDGE,"E62"),sQuery(id+"F0.wireOp",EDGE,"E63"),sQuery(id+"F0.wireOp",EDGE,"E64"),sQuery(id+"F0.wireOp",EDGE,"E65"),sQuery(id+"F0.wireOp",EDGE,"E66"),sQuery(id+"F0.wireOp",EDGE,"E67"),sQuery(id+"F0.wireOp",EDGE,"E68"),sQuery(id+"F0.wireOp",EDGE,"E69"),sQuery(id+"F0.wireOp",EDGE,"E70"),sQuery(id+"F0.wireOp",EDGE,"E71"),sQuery(id+"F0.wireOp",EDGE,"E72"),sQuery(id+"F0.wireOp",EDGE,"E73"),sQuery(id+"F0.wireOp",EDGE,"E74"),sQuery(id+"F0.wireOp",EDGE,"E75"),sQuery(id+"F0.wireOp",EDGE,"E76"),sQuery(id+"F0.wireOp",EDGE,"E77"),sQuery(id+"F0.wireOp",EDGE,"E78"),sQuery(id+"F0.wireOp",EDGE,"E79"),sQuery(id+"F0.wireOp",EDGE,"E80"),sQuery(id+"F0.wireOp",EDGE,"E81"),sQuery(id+"F0.wireOp",EDGE,"E82"),sQuery(id+"F0.wireOp",EDGE,"E83"),sQuery(id+"F0.wireOp",EDGE,"E84"),sQuery(id+"F0.wireOp",EDGE,"E85"),sQuery(id+"F0.wireOp",EDGE,"E86"),sQuery(id+"F0.wireOp",EDGE,"E87"),sQuery(id+"F0.wireOp",EDGE,"E88"),sQuery(id+"F0.wireOp",EDGE,"E89"),sQuery(id+"F0.wireOp",EDGE,"E90"),sQuery(id+"F0.wireOp",EDGE,"E91"),sQuery(id+"F0.wireOp",EDGE,"E93"),sQuery(id+"F0.wireOp",EDGE,"E94"),sQuery(id+"F0.wireOp",EDGE,"E95"),sQuery(id+"F0.wireOp",EDGE,"E96"),sQuery(id+"F0.wireOp",EDGE,"E97"),sQuery(id+"F0.wireOp",EDGE,"E98"),sQuery(id+"F0.wireOp",EDGE,"E99"),sQuery(id+"F0.wireOp",EDGE,"E100"),sQuery(id+"F0.wireOp",EDGE,"E101"),sQuery(id+"F0.wireOp",EDGE,"E102"),sQuery(id+"F0.wireOp",EDGE,"E103"),sQuery(id+"F0.wireOp",EDGE,"E104"),sQuery(id+"F0.wireOp",EDGE,"E105"),sQuery(id+"F0.wireOp",EDGE,"E106"),sQuery(id+"F0.wireOp",EDGE,"E107"),sQuery(id+"F0.wireOp",EDGE,"E108"),sQuery(id+"F0.wireOp",EDGE,"E125"),sQuery(id+"F0.wireOp",EDGE,"E126"),sQuery(id+"F0.wireOp",EDGE,"E127"),sQuery(id+"F0.wireOp",EDGE,"E128"),sQuery(id+"F0.wireOp",EDGE,"E129"),sQuery(id+"F0.wireOp",EDGE,"E130"),sQuery(id+"F0.wireOp",EDGE,"E131"),sQuery(id+"F0.wireOp",EDGE,"E132"),sQuery(id+"F0.wireOp",EDGE,"E133"),sQuery(id+"F0.wireOp",EDGE,"E134"),sQuery(id+"F0.wireOp",EDGE,"E135"),sQuery(id+"F0.wireOp",EDGE,"E136"),sQuery(id+"F0.wireOp",EDGE,"E137"),sQuery(id+"F0.wireOp",EDGE,"E138"),sQuery(id+"F0.wireOp",EDGE,"E139"),sQuery(id+"F0.wireOp",EDGE,"E140"),sQuery(id+"F0.wireOp",EDGE,"E141"),sQuery(id+"F0.wireOp",EDGE,"E142"),sQuery(id+"F0.wireOp",EDGE,"E143"),sQuery(id+"F0.wireOp",EDGE,"E144"),sQuery(id+"F0.wireOp",EDGE,"E145"),sQuery(id+"F0.wireOp",EDGE,"E146"),sQuery(id+"F0.wireOp",EDGE,"E147"),sQuery(id+"F0.wireOp",EDGE,"E148"),sQuery(id+"F0.wireOp",EDGE,"E149"),sQuery(id+"F0.wireOp",EDGE,"E150"),sQuery(id+"F0.wireOp",EDGE,"E151"),sQuery(id+"F0.wireOp",EDGE,"E152"),sQuery(id+"F0.wireOp",EDGE,"E153"),sQuery(id+"F0.wireOp",EDGE,"E154"),sQuery(id+"F0.wireOp",EDGE,"E155"),sQuery(id+"F0.wireOp",EDGE,"E156"),sQuery(id+"F0.wireOp",EDGE,"E157"),sQuery(id+"F0.wireOp",EDGE,"E158"),sQuery(id+"F0.wireOp",EDGE,"E159"),sQuery(id+"F0.wireOp",EDGE,"E160"),sQuery(id+"F0.wireOp",EDGE,"E161"),sQuery(id+"F0.wireOp",EDGE,"E162"),sQuery(id+"F0.wireOp",EDGE,"E163"),sQuery(id+"F0.wireOp",EDGE,"E164"),sQuery(id+"F0.wireOp",EDGE,"E165"),sQuery(id+"F0.wireOp",EDGE,"E166"),sQuery(id+"F0.wireOp",EDGE,"E167"),sQuery(id+"F0.wireOp",EDGE,"E168"),sQuery(id+"F0.wireOp",EDGE,"E169"),sQuery(id+"F0.wireOp",EDGE,"E170"),sQuery(id+"F0.wireOp",EDGE,"E171"),sQuery(id+"F0.wireOp",EDGE,"E172"),sQuery(id+"F0.wireOp",EDGE,"E173"),sQuery(id+"F0.wireOp",EDGE,"E174"),sQuery(id+"F0.wireOp",EDGE,"E175"),sQuery(id+"F0.wireOp",EDGE,"E176"),sQuery(id+"F0.wireOp",EDGE,"E177"),sQuery(id+"F0.wireOp",EDGE,"E178"),sQuery(id+"F0.wireOp",EDGE,"E179"),sQuery(id+"F0.wireOp",EDGE,"E180"),sQuery(id+"F0.wireOp",EDGE,"E181"),sQuery(id+"F0.wireOp",EDGE,"E182"),sQuery(id+"F0.wireOp",EDGE,"E183"),sQuery(id+"F0.wireOp",EDGE,"E184"),sQuery(id+"F0.wireOp",EDGE,"E185"),sQuery(id+"F0.wireOp",EDGE,"E186"),sQuery(id+"F0.wireOp",EDGE,"E187"),sQuery(id+"F0.wireOp",EDGE,"E188"),sQuery(id+"F0.wireOp",EDGE,"E189"),sQuery(id+"F0.wireOp",EDGE,"E190"),sQuery(id+"F0.wireOp",EDGE,"E191"),sQuery(id+"F0.wireOp",EDGE,"E192"),sQuery(id+"F0.wireOp",EDGE,"E193"),sQuery(id+"F0.wireOp",EDGE,"E194"),sQuery(id+"F0.wireOp",EDGE,"E195"),sQuery(id+"F0.wireOp",EDGE,"E196"),sQuery(id+"F0.wireOp",EDGE,"E197"),sQuery(id+"F0.wireOp",EDGE,"E198"),sQuery(id+"F0.wireOp",EDGE,"E199"),sQuery(id+"F0.wireOp",EDGE,"E200"),sQuery(id+"F0.wireOp",EDGE,"E201"),sQuery(id+"F0.wireOp",EDGE,"E202"),sQuery(id+"F0.wireOp",EDGE,"E203"),sQuery(id+"F0.wireOp",EDGE,"E204"),sQuery(id+"F0.wireOp",EDGE,"E205"),sQuery(id+"F0.wireOp",EDGE,"E206"),sQuery(id+"F0.wireOp",EDGE,"E207"),sQuery(id+"F0.wireOp",EDGE,"E208"),sQuery(id+"F0.wireOp",EDGE,"E209"),sQuery(id+"F0.wireOp",EDGE,"E210"),sQuery(id+"F0.wireOp",EDGE,"E211"),sQuery(id+"F0.wireOp",EDGE,"E212"),sQuery(id+"F0.wireOp",EDGE,"E213"),sQuery(id+"F0.wireOp",EDGE,"E214"),sQuery(id+"F0.wireOp",EDGE,"E215"),sQuery(id+"F0.wireOp",EDGE,"E216"),sQuery(id+"F0.wireOp",EDGE,"E217"),sQuery(id+"F0.wireOp",EDGE,"E218"),sQuery(id+"F0.wireOp",EDGE,"E219"),sQuery(id+"F0.wireOp",EDGE,"E220"),sQuery(id+"F0.wireOp",EDGE,"E221"),sQuery(id+"F0.wireOp",EDGE,"E222"),sQuery(id+"F0.wireOp",EDGE,"E223"),sQuery(id+"F0.wireOp",EDGE,"E224"),sQuery(id+"F0.wireOp",EDGE,"E225"),sQuery(id+"F0.wireOp",EDGE,"E226"),sQuery(id+"F0.wireOp",EDGE,"E227"),sQuery(id+"F0.wireOp",EDGE,"E228"),sQuery(id+"F0.wireOp",EDGE,"E229"),sQuery(id+"F0.wireOp",EDGE,"E230"),sQuery(id+"F0.wireOp",EDGE,"E231"),sQuery(id+"F0.wireOp",EDGE,"E232"),sQuery(id+"F0.wireOp",EDGE,"E233"),sQuery(id+"F0.wireOp",EDGE,"E234"),sQuery(id+"F0.wireOp",EDGE,"E235"),sQuery(id+"F0.wireOp",EDGE,"E236"),sQuery(id+"F0.wireOp",EDGE,"E237"),sQuery(id+"F0.wireOp",EDGE,"E238"),sQuery(id+"F0.wireOp",EDGE,"E239"),sQuery(id+"F0.wireOp",EDGE,"E240"),sQuery(id+"F0.wireOp",EDGE,"E241"),sQuery(id+"F0.wireOp",EDGE,"E242"),sQuery(id+"F0.wireOp",EDGE,"E243"),sQuery(id+"F0.wireOp",EDGE,"E244"),sQuery(id+"F0.wireOp",EDGE,"E245"),sQuery(id+"F0.wireOp",EDGE,"E246"),sQuery(id+"F0.wireOp",EDGE,"E247"),sQuery(id+"F0.wireOp",EDGE,"E248"),sQuery(id+"F0.wireOp",EDGE,"E249"),sQuery(id+"F0.wireOp",EDGE,"E250"),sQuery(id+"F0.wireOp",EDGE,"E251"),sQuery(id+"F0.wireOp",EDGE,"E252"),sQuery(id+"F0.wireOp",EDGE,"E253"),sQuery(id+"F0.wireOp",EDGE,"E254"),sQuery(id+"F0.wireOp",EDGE,"E255"),sQuery(id+"F0.wireOp",EDGE,"E256"),sQuery(id+"F0.wireOp",EDGE,"E257"),sQuery(id+"F0.wireOp",EDGE,"E258"),sQuery(id+"F0.wireOp",EDGE,"E259"),sQuery(id+"F0.wireOp",EDGE,"E260"),sQuery(id+"F0.wireOp",EDGE,"E261"),sQuery(id+"F0.wireOp",EDGE,"E262"),sQuery(id+"F0.wireOp",EDGE,"E263"),sQuery(id+"F0.wireOp",EDGE,"E264"),sQuery(id+"F0.wireOp",EDGE,"E265"),sQuery(id+"F0.wireOp",EDGE,"E266"),sQuery(id+"F0.wireOp",EDGE,"E267"),sQuery(id+"F0.wireOp",EDGE,"E268"),sQuery(id+"F0.wireOp",EDGE,"E269"),sQuery(id+"F0.wireOp",EDGE,"E270"),sQuery(id+"F0.wireOp",EDGE,"E271"),sQuery(id+"F0.wireOp",EDGE,"E272"),sQuery(id+"F0.wireOp",EDGE,"E273"),sQuery(id+"F0.wireOp",EDGE,"E274"),sQuery(id+"F0.wireOp",EDGE,"E275"),sQuery(id+"F0.wireOp",EDGE,"E276"),sQuery(id+"F0.wireOp",EDGE,"E277"),sQuery(id+"F0.wireOp",EDGE,"E278"),sQuery(id+"F0.wireOp",EDGE,"E279"),sQuery(id+"F0.wireOp",EDGE,"E280"),sQuery(id+"F0.wireOp",EDGE,"E281"),sQuery(id+"F0.wireOp",EDGE,"E282"),sQuery(id+"F0.wireOp",EDGE,"E283"),sQuery(id+"F0.wireOp",EDGE,"E284"),sQuery(id+"F0.wireOp",EDGE,"E285"),sQuery(id+"F0.wireOp",EDGE,"E92"),sQuery(id+"F0.wireOp",EDGE,"E286"),sQuery(id+"F0.wireOp",EDGE,"E287"),sQuery(id+"F0.wireOp",EDGE,"E288"),sQuery(id+"F0.wireOp",EDGE,"E289"),sQuery(id+"F0.wireOp",EDGE,"E290"),sQuery(id+"F0.wireOp",EDGE,"E291"),sQuery(id+"F0.wireOp",EDGE,"E292"),sQuery(id+"F0.wireOp",EDGE,"E293"),sQuery(id+"F0.wireOp",EDGE,"E294"),sQuery(id+"F0.wireOp",EDGE,"E295"),sQuery(id+"F0.wireOp",EDGE,"E296"),sQuery(id+"F0.wireOp",EDGE,"E297"),sQuery(id+"F0.wireOp",EDGE,"E298"),sQuery(id+"F0.wireOp",EDGE,"E299"),sQuery(id+"F0.wireOp",EDGE,"E300"),sQuery(id+"F0.wireOp",EDGE,"E301"),sQuery(id+"F0.wireOp",EDGE,"E302"),sQuery(id+"F0.wireOp",EDGE,"E303"),sQuery(id+"F0.wireOp",EDGE,"E304"),sQuery(id+"F0.wireOp",EDGE,"E305"),sQuery(id+"F0.wireOp",EDGE,"E306"),sQuery(id+"F0.wireOp",EDGE,"E307"),sQuery(id+"F0.wireOp",EDGE,"E308"),sQuery(id+"F0.wireOp",EDGE,"E309"),sQuery(id+"F0.wireOp",EDGE,"E310"),sQuery(id+"F0.wireOp",EDGE,"E311"),sQuery(id+"F0.wireOp",EDGE,"E312"),sQuery(id+"F0.wireOp",EDGE,"E313"),sQuery(id+"F0.wireOp",EDGE,"E314"),sQuery(id+"F0.wireOp",EDGE,"E315"),sQuery(id+"F0.wireOp",EDGE,"E316"),sQuery(id+"F0.wireOp",EDGE,"E317"),sQuery(id+"F0.wireOp",EDGE,"E318"),sQuery(id+"F0.wireOp",EDGE,"E319"),sQuery(id+"F0.wireOp",EDGE,"E320"),sQuery(id+"F0.wireOp",EDGE,"E321"),sQuery(id+"F0.wireOp",EDGE,"E322"),sQuery(id+"F0.wireOp",EDGE,"E323"),sQuery(id+"F0.wireOp",EDGE,"E324"),sQuery(id+"F0.wireOp",EDGE,"E325"),sQuery(id+"F0.wireOp",EDGE,"E326"),sQuery(id+"F0.wireOp",EDGE,"E327"),sQuery(id+"F0.wireOp",EDGE,"E328"),sQuery(id+"F0.wireOp",EDGE,"E329"),sQuery(id+"F0.wireOp",EDGE,"E330"),sQuery(id+"F0.wireOp",EDGE,"E331"),sQuery(id+"F0.wireOp",EDGE,"E332"),sQuery(id+"F0.wireOp",EDGE,"E333"),sQuery(id+"F0.wireOp",EDGE,"E334"),sQuery(id+"F0.wireOp",EDGE,"E335"),sQuery(id+"F0.wireOp",EDGE,"E336"),sQuery(id+"F0.wireOp",EDGE,"E337"),sQuery(id+"F0.wireOp",EDGE,"E338"),sQuery(id+"F0.wireOp",EDGE,"E339"),sQuery(id+"F0.wireOp",EDGE,"E340"),sQuery(id+"F0.wireOp",EDGE,"E341"),sQuery(id+"F0.wireOp",EDGE,"E342"),sQuery(id+"F0.wireOp",EDGE,"E343"),sQuery(id+"F0.wireOp",EDGE,"E344"),sQuery(id+"F0.wireOp",EDGE,"E345"),sQuery(id+"F0.wireOp",EDGE,"E346"),sQuery(id+"F0.wireOp",EDGE,"E347"),sQuery(id+"F0.wireOp",EDGE,"E348"),sQuery(id+"F0.wireOp",EDGE,"E349"),sQuery(id+"F0.wireOp",EDGE,"E350"),sQuery(id+"F0.wireOp",EDGE,"E351"),sQuery(id+"F0.wireOp",EDGE,"E352"),sQuery(id+"F0.wireOp",EDGE,"E353"),sQuery(id+"F0.wireOp",EDGE,"E354"),sQuery(id+"F0.wireOp",EDGE,"E355"),sQuery(id+"F0.wireOp",EDGE,"E356"),sQuery(id+"F0.wireOp",EDGE,"E357"),sQuery(id+"F0.wireOp",EDGE,"E358"),sQuery(id+"F0.wireOp",EDGE,"E359"),sQuery(id+"F0.wireOp",EDGE,"E360"),sQuery(id+"F0.wireOp",EDGE,"E361"),sQuery(id+"F0.wireOp",EDGE,"E362"),sQuery(id+"F0.wireOp",EDGE,"E363"),sQuery(id+"F0.wireOp",EDGE,"E364"),sQuery(id+"F0.wireOp",EDGE,"E365"),sQuery(id+"F0.wireOp",EDGE,"E366"),sQuery(id+"F0.wireOp",EDGE,"E367"),sQuery(id+"F0.wireOp",EDGE,"E368"),sQuery(id+"F0.wireOp",EDGE,"E369"),sQuery(id+"F0.wireOp",EDGE,"E370"),sQuery(id+"F0.wireOp",EDGE,"E371"),sQuery(id+"F0.wireOp",EDGE,"E372"),sQuery(id+"F0.wireOp",EDGE,"E373"),sQuery(id+"F0.wireOp",EDGE,"E374"),sQuery(id+"F0.wireOp",EDGE,"E375"),sQuery(id+"F0.wireOp",EDGE,"E376"),sQuery(id+"F0.wireOp",EDGE,"E377"),sQuery(id+"F0.wireOp",EDGE,"E378"),sQuery(id+"F0.wireOp",EDGE,"E379"),sQuery(id+"F0.wireOp",EDGE,"E380"),sQuery(id+"F0.wireOp",EDGE,"E381"),sQuery(id+"F0.wireOp",EDGE,"E382"),sQuery(id+"F0.wireOp",EDGE,"E383"),sQuery(id+"F0.wireOp",EDGE,"E384"),sQuery(id+"F0.wireOp",EDGE,"E385"),sQuery(id+"F0.wireOp",EDGE,"E386"),sQuery(id+"F0.wireOp",EDGE,"E387"),sQuery(id+"F0.wireOp",EDGE,"E388"),sQuery(id+"F0.wireOp",EDGE,"E389"),sQuery(id+"F0.wireOp",EDGE,"E390"),sQuery(id+"F0.wireOp",EDGE,"E391"),sQuery(id+"F0.wireOp",EDGE,"E392"),sQuery(id+"F0.wireOp",EDGE,"E393"),sQuery(id+"F0.wireOp",EDGE,"E394"),sQuery(id+"F0.wireOp",EDGE,"E395"),sQuery(id+"F0.wireOp",EDGE,"E396"),sQuery(id+"F0.wireOp",EDGE,"E397"),sQuery(id+"F0.wireOp",EDGE,"E398"),sQuery(id+"F0.wireOp",EDGE,"E399"),sQuery(id+"F0.wireOp",EDGE,"E400"),sQuery(id+"F0.wireOp",EDGE,"E401"),sQuery(id+"F0.wireOp",EDGE,"E402"),sQuery(id+"F0.wireOp",EDGE,"E403"),sQuery(id+"F0.wireOp",EDGE,"E404"),sQuery(id+"F0.wireOp",EDGE,"E405"),sQuery(id+"F0.wireOp",EDGE,"E406"),sQuery(id+"F0.wireOp",EDGE,"E407"),sQuery(id+"F0.wireOp",EDGE,"E408"),sQuery(id+"F0.wireOp",EDGE,"E409"),sQuery(id+"F0.wireOp",EDGE,"E410"),sQuery(id+"F0.wireOp",EDGE,"E411"),sQuery(id+"F0.wireOp",EDGE,"E412"),sQuery(id+"F0.wireOp",EDGE,"E413"),sQuery(id+"F0.wireOp",EDGE,"E414"),sQuery(id+"F0.wireOp",EDGE,"E415"),sQuery(id+"F0.wireOp",EDGE,"E416"),sQuery(id+"F0.wireOp",EDGE,"E417"),sQuery(id+"F0.wireOp",EDGE,"E418"),sQuery(id+"F0.wireOp",EDGE,"E419"),sQuery(id+"F0.wireOp",EDGE,"E420"),sQuery(id+"F0.wireOp",EDGE,"E421"),sQuery(id+"F0.wireOp",EDGE,"E422"),sQuery(id+"F0.wireOp",EDGE,"E423"),sQuery(id+"F0.wireOp",EDGE,"E424"),sQuery(id+"F0.wireOp",EDGE,"E425"),sQuery(id+"F0.wireOp",EDGE,"E426"),sQuery(id+"F0.wireOp",EDGE,"E427"),sQuery(id+"F0.wireOp",EDGE,"E428"),sQuery(id+"F0.wireOp",EDGE,"E429"),sQuery(id+"F0.wireOp",EDGE,"E430"),sQuery(id+"F0.wireOp",EDGE,"E431"),sQuery(id+"F0.wireOp",EDGE,"E432"),sQuery(id+"F0.wireOp",EDGE,"E433"),sQuery(id+"F0.wireOp",EDGE,"E434"),sQuery(id+"F0.wireOp",EDGE,"E435"),sQuery(id+"F0.wireOp",EDGE,"E436"),sQuery(id+"F0.wireOp",EDGE,"E437"),sQuery(id+"F0.wireOp",EDGE,"E438"),sQuery(id+"F0.wireOp",EDGE,"E439"),sQuery(id+"F0.wireOp",EDGE,"E440"),sQuery(id+"F0.wireOp",EDGE,"E441"),sQuery(id+"F0.wireOp",EDGE,"E442"),sQuery(id+"F0.wireOp",EDGE,"E443"),sQuery(id+"F0.wireOp",EDGE,"E444"),sQuery(id+"F0.wireOp",EDGE,"E445"),sQuery(id+"F0.wireOp",EDGE,"E446"),sQuery(id+"F0.wireOp",EDGE,"E447"),sQuery(id+"F0.wireOp",EDGE,"E448"),sQuery(id+"F0.wireOp",EDGE,"E449"),sQuery(id+"F0.wireOp",EDGE,"E450"),sQuery(id+"F0.wireOp",EDGE,"E451"),sQuery(id+"F0.wireOp",EDGE,"E452"),sQuery(id+"F0.wireOp",EDGE,"E453"),sQuery(id+"F0.wireOp",EDGE,"E454"),sQuery(id+"F0.wireOp",EDGE,"E455"),sQuery(id+"F0.wireOp",EDGE,"E456"),sQuery(id+"F0.wireOp",EDGE,"E457"),sQuery(id+"F0.wireOp",EDGE,"E458"),sQuery(id+"F0.wireOp",EDGE,"E459"),sQuery(id+"F0.wireOp",EDGE,"E460"),sQuery(id+"F0.wireOp",EDGE,"E461"),sQuery(id+"F0.wireOp",EDGE,"E462"),sQuery(id+"F0.wireOp",EDGE,"E463"),sQuery(id+"F0.wireOp",EDGE,"E464"),sQuery(id+"F0.wireOp",EDGE,"E465"),sQuery(id+"F0.wireOp",EDGE,"E466"),sQuery(id+"F0.wireOp",EDGE,"E467"),sQuery(id+"F0.wireOp",EDGE,"E468"),sQuery(id+"F0.wireOp",EDGE,"E469"),sQuery(id+"F0.wireOp",EDGE,"E470"),sQuery(id+"F0.wireOp",EDGE,"E471"),sQuery(id+"F0.wireOp",EDGE,"E472"),sQuery(id+"F0.wireOp",EDGE,"E473"),sQuery(id+"F0.wireOp",EDGE,"E474"),sQuery(id+"F0.wireOp",EDGE,"E475"),sQuery(id+"F0.wireOp",EDGE,"E476"),sQuery(id+"F0.wireOp",EDGE,"E477"),sQuery(id+"F0.wireOp",EDGE,"E478"),sQuery(id+"F0.wireOp",EDGE,"E479"),sQuery(id+"F0.wireOp",EDGE,"E480"),sQuery(id+"F0.wireOp",EDGE,"E481"),sQuery(id+"F0.wireOp",EDGE,"E482"),sQuery(id+"F0.wireOp",EDGE,"E483"),sQuery(id+"F0.wireOp",EDGE,"E484"),sQuery(id+"F0.wireOp",EDGE,"E485"),sQuery(id+"F0.wireOp",EDGE,"E486"),sQuery(id+"F0.wireOp",EDGE,"E487"),sQuery(id+"F0.wireOp",EDGE,"E488"),sQuery(id+"F0.wireOp",EDGE,"E489"),sQuery(id+"F0.wireOp",EDGE,"E490"),sQuery(id+"F0.wireOp",EDGE,"E491"),sQuery(id+"F0.wireOp",EDGE,"E492"),sQuery(id+"F0.wireOp",EDGE,"E493"),sQuery(id+"F0.wireOp",EDGE,"E494"),sQuery(id+"F0.wireOp",EDGE,"E495"),sQuery(id+"F0.wireOp",EDGE,"E496"),sQuery(id+"F0.wireOp",EDGE,"E497"),sQuery(id+"F0.wireOp",EDGE,"E498"),sQuery(id+"F0.wireOp",EDGE,"E499"),sQuery(id+"F0.wireOp",EDGE,"E500"),sQuery(id+"F0.wireOp",EDGE,"E501"),sQuery(id+"F0.wireOp",EDGE,"E502"),sQuery(id+"F0.wireOp",EDGE,"E503"),sQuery(id+"F0.wireOp",EDGE,"E504"),sQuery(id+"F0.wireOp",EDGE,"E505"),sQuery(id+"F0.wireOp",EDGE,"E506"),sQuery(id+"F0.wireOp",EDGE,"E507"),sQuery(id+"F0.wireOp",EDGE,"E508"),sQuery(id+"F0.wireOp",EDGE,"E509"),sQuery(id+"F0.wireOp",EDGE,"E510"),sQuery(id+"F0.wireOp",EDGE,"E511"),sQuery(id+"F0.wireOp",EDGE,"E512"),sQuery(id+"F0.wireOp",EDGE,"E513"),sQuery(id+"F0.wireOp",EDGE,"E514"),sQuery(id+"F0.wireOp",EDGE,"E515"),sQuery(id+"F0.wireOp",EDGE,"E516"),sQuery(id+"F0.wireOp",EDGE,"E517"),sQuery(id+"F0.wireOp",EDGE,"E518"),sQuery(id+"F0.wireOp",EDGE,"E519"),sQuery(id+"F0.wireOp",EDGE,"E520"),sQuery(id+"F0.wireOp",EDGE,"E521"),sQuery(id+"F0.wireOp",EDGE,"E522"),sQuery(id+"F0.wireOp",EDGE,"E523"),sQuery(id+"F0.wireOp",EDGE,"E524"),sQuery(id+"F0.wireOp",EDGE,"E525"),sQuery(id+"F0.wireOp",EDGE,"E526"),sQuery(id+"F0.wireOp",EDGE,"E527"),sQuery(id+"F0.wireOp",EDGE,"E528"),sQuery(id+"F0.wireOp",EDGE,"E529"),sQuery(id+"F0.wireOp",EDGE,"E530"),sQuery(id+"F0.wireOp",EDGE,"E531"),sQuery(id+"F0.wireOp",EDGE,"E532"),sQuery(id+"F0.wireOp",EDGE,"E533"),sQuery(id+"F0.wireOp",EDGE,"E534"),sQuery(id+"F0.wireOp",EDGE,"E535"),sQuery(id+"F0.wireOp",EDGE,"E536"),sQuery(id+"F0.wireOp",EDGE,"E537"),sQuery(id+"F0.wireOp",EDGE,"E538"),sQuery(id+"F0.wireOp",EDGE,"E539"),sQuery(id+"F0.wireOp",EDGE,"E540"),sQuery(id+"F0.wireOp",EDGE,"E541"),sQuery(id+"F0.wireOp",EDGE,"E542"),sQuery(id+"F0.wireOp",EDGE,"E543"),sQuery(id+"F0.wireOp",EDGE,"E544"),sQuery(id+"F0.wireOp",EDGE,"E545"),sQuery(id+"F0.wireOp",EDGE,"E546"),sQuery(id+"F0.wireOp",EDGE,"E547"),sQuery(id+"F0.wireOp",EDGE,"E548"),sQuery(id+"F0.wireOp",EDGE,"E549"),sQuery(id+"F0.wireOp",EDGE,"E550"),sQuery(id+"F0.wireOp",EDGE,"E551"),sQuery(id+"F0.wireOp",EDGE,"E552"),sQuery(id+"F0.wireOp",EDGE,"E553"),sQuery(id+"F0.wireOp",EDGE,"E554"),sQuery(id+"F0.wireOp",EDGE,"E555"),sQuery(id+"F0.wireOp",EDGE,"E556"),sQuery(id+"F0.wireOp",EDGE,"E557"),sQuery(id+"F0.wireOp",EDGE,"E558"),sQuery(id+"F0.wireOp",EDGE,"E559"),sQuery(id+"F0.wireOp",EDGE,"E560"),sQuery(id+"F0.wireOp",EDGE,"E561"),sQuery(id+"F0.wireOp",EDGE,"E562"),sQuery(id+"F0.wireOp",EDGE,"E563"),sQuery(id+"F0.wireOp",EDGE,"E564"),sQuery(id+"F0.wireOp",EDGE,"E565"),sQuery(id+"F0.wireOp",EDGE,"E566"),sQuery(id+"F0.wireOp",EDGE,"E567"),sQuery(id+"F0.wireOp",EDGE,"E568"),sQuery(id+"F0.wireOp",EDGE,"E569"),sQuery(id+"F0.wireOp",EDGE,"E570"),sQuery(id+"F0.wireOp",EDGE,"E571"),sQuery(id+"F0.wireOp",EDGE,"E572"),sQuery(id+"F0.wireOp",EDGE,"E573"),sQuery(id+"F0.wireOp",EDGE,"E574"),sQuery(id+"F0.wireOp",EDGE,"E575"),sQuery(id+"F0.wireOp",EDGE,"E576"),sQuery(id+"F0.wireOp",EDGE,"E577"),sQuery(id+"F0.wireOp",EDGE,"E578"),sQuery(id+"F0.wireOp",EDGE,"E579"),sQuery(id+"F0.wireOp",EDGE,"E580"),sQuery(id+"F0.wireOp",EDGE,"E581"),sQuery(id+"F0.wireOp",EDGE,"E582"),sQuery(id+"F0.wireOp",EDGE,"E583"),sQuery(id+"F0.wireOp",EDGE,"E584"),sQuery(id+"F0.wireOp",EDGE,"E585"),sQuery(id+"F0.wireOp",EDGE,"E586"),sQuery(id+"F0.wireOp",EDGE,"E587"),sQuery(id+"F0.wireOp",EDGE,"E588"),sQuery(id+"F0.wireOp",EDGE,"E589"),sQuery(id+"F0.wireOp",EDGE,"E590"),sQuery(id+"F0.wireOp",EDGE,"E591"),sQuery(id+"F0.wireOp",EDGE,"E592"),sQuery(id+"F0.wireOp",EDGE,"E593"),sQuery(id+"F0.wireOp",EDGE,"E594"),sQuery(id+"F0.wireOp",EDGE,"E595"),sQuery(id+"F0.wireOp",EDGE,"E596"),sQuery(id+"F0.wireOp",EDGE,"E597"),sQuery(id+"F0.wireOp",EDGE,"E598"),sQuery(id+"F0.wireOp",EDGE,"E599"),sQuery(id+"F0.wireOp",EDGE,"E600"),sQuery(id+"F0.wireOp",EDGE,"E601"),sQuery(id+"F0.wireOp",EDGE,"E602"),sQuery(id+"F0.wireOp",EDGE,"E603"),sQuery(id+"F0.wireOp",EDGE,"E604"),sQuery(id+"F0.wireOp",EDGE,"E605"),sQuery(id+"F0.wireOp",EDGE,"E606"),sQuery(id+"F0.wireOp",EDGE,"E607"),sQuery(id+"F0.wireOp",EDGE,"E608"),sQuery(id+"F0.wireOp",EDGE,"E609"),sQuery(id+"F0.wireOp",EDGE,"E610"),sQuery(id+"F0.wireOp",EDGE,"E611"),sQuery(id+"F0.wireOp",EDGE,"E612"),sQuery(id+"F0.wireOp",EDGE,"E613"),sQuery(id+"F0.wireOp",EDGE,"E614"),sQuery(id+"F0.wireOp",EDGE,"E615"),sQuery(id+"F0.wireOp",EDGE,"E616"),sQuery(id+"F0.wireOp",EDGE,"E617"),sQuery(id+"F0.wireOp",EDGE,"E618"),sQuery(id+"F0.wireOp",EDGE,"E619"),sQuery(id+"F0.wireOp",EDGE,"E620"),sQuery(id+"F0.wireOp",EDGE,"E621"),sQuery(id+"F0.wireOp",EDGE,"E622"),sQuery(id+"F0.wireOp",EDGE,"E623"),sQuery(id+"F0.wireOp",EDGE,"E624"),sQuery(id+"F0.wireOp",EDGE,"E625"),sQuery(id+"F0.wireOp",EDGE,"E626"),sQuery(id+"F0.wireOp",EDGE,"E627"),sQuery(id+"F0.wireOp",EDGE,"E628"),sQuery(id+"F0.wireOp",EDGE,"E629"),sQuery(id+"F0.wireOp",EDGE,"E630"),sQuery(id+"F0.wireOp",EDGE,"E631"),sQuery(id+"F0.wireOp",EDGE,"E632"),sQuery(id+"F0.wireOp",EDGE,"E633"),sQuery(id+"F0.wireOp",EDGE,"E634"),sQuery(id+"F0.wireOp",EDGE,"E635"),sQuery(id+"F0.wireOp",EDGE,"E636"),sQuery(id+"F0.wireOp",EDGE,"E637"),sQuery(id+"F0.wireOp",EDGE,"E638"),sQuery(id+"F0.wireOp",EDGE,"E639"),sQuery(id+"F0.wireOp",EDGE,"E640"),sQuery(id+"F0.wireOp",EDGE,"E641"),sQuery(id+"F0.wireOp",EDGE,"E642"),sQuery(id+"F0.wireOp",EDGE,"E643"),sQuery(id+"F0.wireOp",EDGE,"E644"),sQuery(id+"F0.wireOp",EDGE,"E645"),sQuery(id+"F0.wireOp",EDGE,"E646"),sQuery(id+"F0.wireOp",EDGE,"E647"),sQuery(id+"F0.wireOp",EDGE,"E648"),sQuery(id+"F0.wireOp",EDGE,"E649"),sQuery(id+"F0.wireOp",EDGE,"E650"),sQuery(id+"F0.wireOp",EDGE,"E651"),sQuery(id+"F0.wireOp",EDGE,"E652"),sQuery(id+"F0.wireOp",EDGE,"E653"),sQuery(id+"F0.wireOp",EDGE,"E654"),sQuery(id+"F0.wireOp",EDGE,"E655"),sQuery(id+"F0.wireOp",EDGE,"E656"),sQuery(id+"F0.wireOp",EDGE,"E657"),sQuery(id+"F0.wireOp",EDGE,"E658"),sQuery(id+"F0.wireOp",EDGE,"E659"),sQuery(id+"F0.wireOp",EDGE,"E660"),sQuery(id+"F0.wireOp",EDGE,"E661"),sQuery(id+"F0.wireOp",EDGE,"E662"),sQuery(id+"F0.wireOp",EDGE,"E663"),sQuery(id+"F0.wireOp",EDGE,"E664"),sQuery(id+"F0.wireOp",EDGE,"E665"),sQuery(id+"F0.wireOp",EDGE,"E666"),sQuery(id+"F0.wireOp",EDGE,"E667"),sQuery(id+"F0.wireOp",EDGE,"E668"),sQuery(id+"F0.wireOp",EDGE,"E669"),sQuery(id+"F0.wireOp",EDGE,"E670"),sQuery(id+"F0.wireOp",EDGE,"E671"),sQuery(id+"F0.wireOp",EDGE,"E672"),sQuery(id+"F0.wireOp",EDGE,"E673"),sQuery(id+"F0.wireOp",EDGE,"E674"),sQuery(id+"F0.wireOp",EDGE,"E675"),sQuery(id+"F0.wireOp",EDGE,"E676"),sQuery(id+"F0.wireOp",EDGE,"E677"),sQuery(id+"F0.wireOp",EDGE,"E678"),sQuery(id+"F0.wireOp",EDGE,"E679"),sQuery(id+"F0.wireOp",EDGE,"E680"),sQuery(id+"F0.wireOp",EDGE,"E681"),sQuery(id+"F0.wireOp",EDGE,"E682"),sQuery(id+"F0.wireOp",EDGE,"E683"),sQuery(id+"F0.wireOp",EDGE,"E684"),sQuery(id+"F0.wireOp",EDGE,"E685"),sQuery(id+"F0.wireOp",EDGE,"E686"),sQuery(id+"F0.wireOp",EDGE,"E687"),sQuery(id+"F0.wireOp",EDGE,"E688"),sQuery(id+"F0.wireOp",EDGE,"E689"),sQuery(id+"F0.wireOp",EDGE,"E690"),sQuery(id+"F0.wireOp",EDGE,"E691"),sQuery(id+"F0.wireOp",EDGE,"E692"),sQuery(id+"F0.wireOp",EDGE,"E693"),sQuery(id+"F0.wireOp",EDGE,"E694"),sQuery(id+"F0.wireOp",EDGE,"E695"),sQuery(id+"F0.wireOp",EDGE,"E696"),sQuery(id+"F0.wireOp",EDGE,"E697"),sQuery(id+"F0.wireOp",EDGE,"E698"),sQuery(id+"F0.wireOp",EDGE,"E699"),sQuery(id+"F0.wireOp",EDGE,"E700"),sQuery(id+"F0.wireOp",EDGE,"E701"),sQuery(id+"F0.wireOp",EDGE,"E702"),sQuery(id+"F0.wireOp",EDGE,"E703"),sQuery(id+"F0.wireOp",EDGE,"E704"),sQuery(id+"F0.wireOp",EDGE,"E705"),sQuery(id+"F0.wireOp",EDGE,"E706"),sQuery(id+"F0.wireOp",EDGE,"E707"),sQuery(id+"F0.wireOp",EDGE,"E708"),sQuery(id+"F0.wireOp",EDGE,"E709"),sQuery(id+"F0.wireOp",EDGE,"E710"),sQuery(id+"F0.wireOp",EDGE,"E711"),sQuery(id+"F0.wireOp",EDGE,"E712"),sQuery(id+"F0.wireOp",EDGE,"E713"),sQuery(id+"F0.wireOp",EDGE,"E714"),sQuery(id+"F0.wireOp",EDGE,"E715"),sQuery(id+"F0.wireOp",EDGE,"E716"),sQuery(id+"F0.wireOp",EDGE,"E717"),sQuery(id+"F0.wireOp",EDGE,"E718"),sQuery(id+"F0.wireOp",EDGE,"E719"),sQuery(id+"F0.wireOp",EDGE,"E720"),sQuery(id+"F0.wireOp",EDGE,"E721"),sQuery(id+"F0.wireOp",EDGE,"E722"),sQuery(id+"F0.wireOp",EDGE,"E723"),sQuery(id+"F0.wireOp",EDGE,"E724"),sQuery(id+"F0.wireOp",EDGE,"E725"),sQuery(id+"F0.wireOp",EDGE,"E726"),sQuery(id+"F0.wireOp",EDGE,"E727"),sQuery(id+"F0.wireOp",EDGE,"E728"),sQuery(id+"F0.wireOp",EDGE,"E729"),sQuery(id+"F0.wireOp",EDGE,"E730"),sQuery(id+"F0.wireOp",EDGE,"E731"),sQuery(id+"F0.wireOp",EDGE,"E732"),sQuery(id+"F0.wireOp",EDGE,"E733"),sQuery(id+"F0.wireOp",EDGE,"E734"),sQuery(id+"F0.wireOp",EDGE,"E735"),sQuery(id+"F0.wireOp",EDGE,"E736"),sQuery(id+"F0.wireOp",EDGE,"E737"),sQuery(id+"F0.wireOp",EDGE,"E738"),sQuery(id+"F0.wireOp",EDGE,"E739"),sQuery(id+"F0.wireOp",EDGE,"E740"),sQuery(id+"F0.wireOp",EDGE,"E741"),sQuery(id+"F0.wireOp",EDGE,"E742"),sQuery(id+"F0.wireOp",EDGE,"E743"),sQuery(id+"F0.wireOp",EDGE,"E744"),sQuery(id+"F0.wireOp",EDGE,"E745"),sQuery(id+"F0.wireOp",EDGE,"E746"),sQuery(id+"F0.wireOp",EDGE,"E747"),sQuery(id+"F0.wireOp",EDGE,"E748"),sQuery(id+"F0.wireOp",EDGE,"E749"),sQuery(id+"F0.wireOp",EDGE,"E750"),sQuery(id+"F0.wireOp",EDGE,"E751"),sQuery(id+"F0.wireOp",EDGE,"E752"),sQuery(id+"F0.wireOp",EDGE,"E753"),sQuery(id+"F0.wireOp",EDGE,"E754"),sQuery(id+"F0.wireOp",EDGE,"E755"),sQuery(id+"F0.wireOp",EDGE,"E756"),sQuery(id+"F0.wireOp",EDGE,"E757"),sQuery(id+"F0.wireOp",EDGE,"E758"),sQuery(id+"F0.wireOp",EDGE,"E759"),sQuery(id+"F0.wireOp",EDGE,"E760"),sQuery(id+"F0.wireOp",EDGE,"E761"),sQuery(id+"F0.wireOp",EDGE,"E762"),sQuery(id+"F0.wireOp",EDGE,"E763"),sQuery(id+"F0.wireOp",EDGE,"E764"),sQuery(id+"F0.wireOp",EDGE,"E765"),sQuery(id+"F0.wireOp",EDGE,"E766"),sQuery(id+"F0.wireOp",EDGE,"E767"),sQuery(id+"F0.wireOp",EDGE,"E768"),sQuery(id+"F0.wireOp",EDGE,"E769"),sQuery(id+"F0.wireOp",EDGE,"E770"),sQuery(id+"F0.wireOp",EDGE,"E771"),sQuery(id+"F0.wireOp",EDGE,"E772"),sQuery(id+"F0.wireOp",EDGE,"E773"),sQuery(id+"F0.wireOp",EDGE,"E774"),sQuery(id+"F0.wireOp",EDGE,"E775"),sQuery(id+"F0.wireOp",EDGE,"E776"),sQuery(id+"F0.wireOp",EDGE,"E777"),sQuery(id+"F0.wireOp",EDGE,"E778"),sQuery(id+"F0.wireOp",EDGE,"E779"),sQuery(id+"F0.wireOp",EDGE,"E780"),sQuery(id+"F0.wireOp",EDGE,"E781"),sQuery(id+"F0.wireOp",EDGE,"E782"),sQuery(id+"F0.wireOp",EDGE,"E783"),sQuery(id+"F0.wireOp",EDGE,"E784"),sQuery(id+"F0.wireOp",EDGE,"E785"),sQuery(id+"F0.wireOp",EDGE,"E786"),sQuery(id+"F0.wireOp",EDGE,"E787"),sQuery(id+"F0.wireOp",EDGE,"E788"),sQuery(id+"F0.wireOp",EDGE,"E789"),sQuery(id+"F0.wireOp",EDGE,"E790"),sQuery(id+"F0.wireOp",EDGE,"E791"),sQuery(id+"F0.wireOp",EDGE,"E792"),sQuery(id+"F0.wireOp",EDGE,"E793"),sQuery(id+"F0.wireOp",EDGE,"E794"),sQuery(id+"F0.wireOp",EDGE,"E795"),sQuery(id+"F0.wireOp",EDGE,"E796"),sQuery(id+"F0.wireOp",EDGE,"E797"),sQuery(id+"F0.wireOp",EDGE,"E798"),sQuery(id+"F0.wireOp",EDGE,"E799"),sQuery(id+"F0.wireOp",EDGE,"E800"),sQuery(id+"F0.wireOp",EDGE,"E801"),sQuery(id+"F0.wireOp",EDGE,"E802"),sQuery(id+"F0.wireOp",EDGE,"E803"),sQuery(id+"F0.wireOp",EDGE,"E804"),sQuery(id+"F0.wireOp",EDGE,"E805"),sQuery(id+"F0.wireOp",EDGE,"E806"),sQuery(id+"F0.wireOp",EDGE,"E807"),sQuery(id+"F0.wireOp",EDGE,"E808"),sQuery(id+"F0.wireOp",EDGE,"E809"),sQuery(id+"F0.wireOp",EDGE,"E810"),sQuery(id+"F0.wireOp",EDGE,"E811"),sQuery(id+"F0.wireOp",EDGE,"E812"),sQuery(id+"F0.wireOp",EDGE,"E813"),sQuery(id+"F0.wireOp",EDGE,"E814"),sQuery(id+"F0.wireOp",EDGE,"E815"),sQuery(id+"F0.wireOp",EDGE,"E816"),sQuery(id+"F0.wireOp",EDGE,"E817"),sQuery(id+"F0.wireOp",EDGE,"E818"),sQuery(id+"F0.wireOp",EDGE,"E819"),sQuery(id+"F0.wireOp",EDGE,"E820"),sQuery(id+"F0.wireOp",EDGE,"E821"),sQuery(id+"F0.wireOp",EDGE,"E822"),sQuery(id+"F0.wireOp",EDGE,"E823"),sQuery(id+"F0.wireOp",EDGE,"E824"),sQuery(id+"F0.wireOp",EDGE,"E825"),sQuery(id+"F0.wireOp",EDGE,"E826"),sQuery(id+"F0.wireOp",EDGE,"E827"),sQuery(id+"F0.wireOp",EDGE,"E828"),sQuery(id+"F0.wireOp",EDGE,"E829"),sQuery(id+"F0.wireOp",EDGE,"E830"),sQuery(id+"F0.wireOp",EDGE,"E831"),sQuery(id+"F0.wireOp",EDGE,"E832"),sQuery(id+"F0.wireOp",EDGE,"E833"),sQuery(id+"F0.wireOp",EDGE,"E834"),sQuery(id+"F0.wireOp",EDGE,"E835"),sQuery(id+"F0.wireOp",EDGE,"E836"),sQuery(id+"F0.wireOp",EDGE,"E837"),sQuery(id+"F0.wireOp",EDGE,"E838"),sQuery(id+"F0.wireOp",EDGE,"E839"),sQuery(id+"F0.wireOp",EDGE,"E840"),sQuery(id+"F0.wireOp",EDGE,"E841"),sQuery(id+"F0.wireOp",EDGE,"E842"),sQuery(id+"F0.wireOp",EDGE,"E843"),sQuery(id+"F0.wireOp",EDGE,"E844"),sQuery(id+"F0.wireOp",EDGE,"E845"),sQuery(id+"F0.wireOp",EDGE,"E846"),sQuery(id+"F0.wireOp",EDGE,"E847"),sQuery(id+"F0.wireOp",EDGE,"E848"),sQuery(id+"F0.wireOp",EDGE,"E849"),sQuery(id+"F0.wireOp",EDGE,"E850"),sQuery(id+"F0.wireOp",EDGE,"E851"),sQuery(id+"F0.wireOp",EDGE,"E852"),sQuery(id+"F0.wireOp",EDGE,"E853"),sQuery(id+"F0.wireOp",EDGE,"E854"),sQuery(id+"F0.wireOp",EDGE,"E855"),sQuery(id+"F0.wireOp",EDGE,"E856"),sQuery(id+"F0.wireOp",EDGE,"E857"),sQuery(id+"F0.wireOp",EDGE,"E858"),sQuery(id+"F0.wireOp",EDGE,"E859"),sQuery(id+"F0.wireOp",EDGE,"E860"),sQuery(id+"F0.wireOp",EDGE,"E861"),sQuery(id+"F0.wireOp",EDGE,"E862"),sQuery(id+"F0.wireOp",EDGE,"E863"),sQuery(id+"F0.wireOp",EDGE,"E864"),sQuery(id+"F0.wireOp",EDGE,"E865"),sQuery(id+"F0.wireOp",EDGE,"E866"),sQuery(id+"F0.wireOp",EDGE,"E867"),sQuery(id+"F0.wireOp",EDGE,"E868"),sQuery(id+"F0.wireOp",EDGE,"E869"),sQuery(id+"F0.wireOp",EDGE,"E870"),sQuery(id+"F0.wireOp",EDGE,"E871"),sQuery(id+"F0.wireOp",EDGE,"E872"),sQuery(id+"F0.wireOp",EDGE,"E873"),sQuery(id+"F0.wireOp",EDGE,"E874"),sQuery(id+"F0.wireOp",EDGE,"E875"),sQuery(id+"F0.wireOp",EDGE,"E876"),sQuery(id+"F0.wireOp",EDGE,"E877"),sQuery(id+"F0.wireOp",EDGE,"E878"),sQuery(id+"F0.wireOp",EDGE,"E879"),sQuery(id+"F0.wireOp",EDGE,"E880"),sQuery(id+"F0.wireOp",EDGE,"E881"),sQuery(id+"F0.wireOp",EDGE,"E882"),sQuery(id+"F0.wireOp",EDGE,"E883"),sQuery(id+"F0.wireOp",EDGE,"E884"),sQuery(id+"F0.wireOp",EDGE,"E885"),sQuery(id+"F0.wireOp",EDGE,"E886"),sQuery(id+"F0.wireOp",EDGE,"E887"),sQuery(id+"F0.wireOp",EDGE,"E888"),sQuery(id+"F0.wireOp",EDGE,"E889"),sQuery(id+"F0.wireOp",EDGE,"E890"),sQuery(id+"F0.wireOp",EDGE,"E891"),sQuery(id+"F0.wireOp",EDGE,"E892"),sQuery(id+"F0.wireOp",EDGE,"E893"),sQuery(id+"F0.wireOp",EDGE,"E894"),sQuery(id+"F0.wireOp",EDGE,"E895"),sQuery(id+"F0.wireOp",EDGE,"E896"),sQuery(id+"F0.wireOp",EDGE,"E897"),sQuery(id+"F0.wireOp",EDGE,"E898"),sQuery(id+"F0.wireOp",EDGE,"E899"),sQuery(id+"F0.wireOp",EDGE,"E900"),sQuery(id+"F0.wireOp",EDGE,"E901"),sQuery(id+"F0.wireOp",EDGE,"E902"),sQuery(id+"F0.wireOp",EDGE,"E903"),sQuery(id+"F0.wireOp",EDGE,"E904"),sQuery(id+"F0.wireOp",EDGE,"E905"),sQuery(id+"F0.wireOp",EDGE,"E906"),sQuery(id+"F0.wireOp",EDGE,"E907"),sQuery(id+"F0.wireOp",EDGE,"E908"),sQuery(id+"F0.wireOp",EDGE,"E909"),sQuery(id+"F0.wireOp",EDGE,"E910"),sQuery(id+"F0.wireOp",EDGE,"E911"),sQuery(id+"F0.wireOp",EDGE,"E912"),sQuery(id+"F0.wireOp",EDGE,"E913"),sQuery(id+"F0.wireOp",EDGE,"E914"),sQuery(id+"F0.wireOp",EDGE,"E915"),sQuery(id+"F0.wireOp",EDGE,"E916"),sQuery(id+"F0.wireOp",EDGE,"E917"),sQuery(id+"F0.wireOp",EDGE,"E918"),sQuery(id+"F0.wireOp",EDGE,"E919"),sQuery(id+"F0.wireOp",EDGE,"E920"),sQuery(id+"F0.wireOp",EDGE,"E921"),sQuery(id+"F0.wireOp",EDGE,"E922"),sQuery(id+"F0.wireOp",EDGE,"E923"),sQuery(id+"F0.wireOp",EDGE,"E924"),sQuery(id+"F0.wireOp",EDGE,"E925"),sQuery(id+"F0.wireOp",EDGE,"E926"),sQuery(id+"F0.wireOp",EDGE,"E927"),sQuery(id+"F0.wireOp",EDGE,"E928"),sQuery(id+"F0.wireOp",EDGE,"E929"),sQuery(id+"F0.wireOp",EDGE,"E930"),sQuery(id+"F0.wireOp",EDGE,"E931"),sQuery(id+"F0.wireOp",EDGE,"E932"),sQuery(id+"F0.wireOp",EDGE,"E933"),sQuery(id+"F0.wireOp",EDGE,"E934"),sQuery(id+"F0.wireOp",EDGE,"E935"),sQuery(id+"F0.wireOp",EDGE,"E936"),sQuery(id+"F0.wireOp",EDGE,"E937"),sQuery(id+"F0.wireOp",EDGE,"E938"),sQuery(id+"F0.wireOp",EDGE,"E939"),sQuery(id+"F0.wireOp",EDGE,"E940"),sQuery(id+"F0.wireOp",EDGE,"E941"),sQuery(id+"F0.wireOp",EDGE,"E942"),sQuery(id+"F0.wireOp",EDGE,"E943"),sQuery(id+"F0.wireOp",EDGE,"E944"),sQuery(id+"F0.wireOp",EDGE,"E945"),sQuery(id+"F0.wireOp",EDGE,"E946"),sQuery(id+"F0.wireOp",EDGE,"E947"),sQuery(id+"F0.wireOp",EDGE,"E948"),sQuery(id+"F0.wireOp",EDGE,"E949"),sQuery(id+"F0.wireOp",EDGE,"E950"),sQuery(id+"F0.wireOp",EDGE,"E951"),sQuery(id+"F0.wireOp",EDGE,"E952"),sQuery(id+"F0.wireOp",EDGE,"E953"),sQuery(id+"F0.wireOp",EDGE,"E954"),sQuery(id+"F0.wireOp",EDGE,"E955"),sQuery(id+"F0.wireOp",EDGE,"E956"),sQuery(id+"F0.wireOp",EDGE,"E957"),sQuery(id+"F0.wireOp",EDGE,"E958"),sQuery(id+"F0.wireOp",EDGE,"E959"),sQuery(id+"F0.wireOp",EDGE,"E960"),sQuery(id+"F0.wireOp",EDGE,"E961"),sQuery(id+"F0.wireOp",EDGE,"E962"),sQuery(id+"F0.wireOp",EDGE,"E963"),sQuery(id+"F0.wireOp",EDGE,"E964"),sQuery(id+"F0.wireOp",EDGE,"E965"),sQuery(id+"F0.wireOp",EDGE,"E966"),sQuery(id+"F0.wireOp",EDGE,"E967"),sQuery(id+"F0.wireOp",EDGE,"E968"),sQuery(id+"F0.wireOp",EDGE,"E969"),sQuery(id+"F0.wireOp",EDGE,"E970"),sQuery(id+"F0.wireOp",EDGE,"E971"),sQuery(id+"F0.wireOp",EDGE,"E972"),sQuery(id+"F0.wireOp",EDGE,"E973"),sQuery(id+"F0.wireOp",EDGE,"E974"),sQuery(id+"F0.wireOp",EDGE,"E975"),sQuery(id+"F0.wireOp",EDGE,"E976"),sQuery(id+"F0.wireOp",EDGE,"E977"),sQuery(id+"F0.wireOp",EDGE,"E978"),sQuery(id+"F0.wireOp",EDGE,"E979"),sQuery(id+"F0.wireOp",EDGE,"E980"),sQuery(id+"F0.wireOp",EDGE,"E981"),sQuery(id+"F0.wireOp",EDGE,"E982"),sQuery(id+"F0.wireOp",EDGE,"E983"),sQuery(id+"F0.wireOp",EDGE,"E984"),sQuery(id+"F0.wireOp",EDGE,"E985"),sQuery(id+"F0.wireOp",EDGE,"E986"),sQuery(id+"F0.wireOp",EDGE,"E987"),sQuery(id+"F0.wireOp",EDGE,"E988"),sQuery(id+"F0.wireOp",EDGE,"E989"),sQuery(id+"F0.wireOp",EDGE,"E990"),sQuery(id+"F0.wireOp",EDGE,"E991"),sQuery(id+"F0.wireOp",EDGE,"E992"),sQuery(id+"F0.wireOp",EDGE,"E993"),sQuery(id+"F0.wireOp",EDGE,"E994"),sQuery(id+"F0.wireOp",EDGE,"E995"),sQuery(id+"F0.wireOp",EDGE,"E996"),sQuery(id+"F0.wireOp",EDGE,"E997"),sQuery(id+"F0.wireOp",EDGE,"E998"),sQuery(id+"F0.wireOp",EDGE,"E999"),sQuery(id+"F0.wireOp",EDGE,"E1000"),sQuery(id+"F0.wireOp",EDGE,"E1001"),sQuery(id+"F0.wireOp",EDGE,"E1002"),sQuery(id+"F0.wireOp",EDGE,"E1003"),sQuery(id+"F0.wireOp",EDGE,"E1004"),sQuery(id+"F0.wireOp",EDGE,"E1005"),sQuery(id+"F0.wireOp",EDGE,"E1006"),sQuery(id+"F0.wireOp",EDGE,"E1007"),sQuery(id+"F0.wireOp",EDGE,"E1008"),sQuery(id+"F0.wireOp",EDGE,"E1009"),sQuery(id+"F0.wireOp",EDGE,"E1010"),sQuery(id+"F0.wireOp",EDGE,"E1011"),sQuery(id+"F0.wireOp",EDGE,"E1012"),sQuery(id+"F0.wireOp",EDGE,"E1013"),sQuery(id+"F0.wireOp",EDGE,"E1014"),sQuery(id+"F0.wireOp",EDGE,"E1015"),sQuery(id+"F0.wireOp",EDGE,"E1016"),sQuery(id+"F0.wireOp",EDGE,"E1017"),sQuery(id+"F0.wireOp",EDGE,"E1018"),sQuery(id+"F0.wireOp",EDGE,"E1019"),sQuery(id+"F0.wireOp",EDGE,"E1020"),sQuery(id+"F0.wireOp",EDGE,"E1021"),sQuery(id+"F0.wireOp",EDGE,"E1022"),sQuery(id+"F0.wireOp",EDGE,"E1023"),sQuery(id+"F0.wireOp",EDGE,"E1024"),sQuery(id+"F0.wireOp",EDGE,"E1025"),sQuery(id+"F0.wireOp",EDGE,"E1026"),sQuery(id+"F0.wireOp",EDGE,"E1027"),sQuery(id+"F0.wireOp",EDGE,"E1028"),sQuery(id+"F0.wireOp",EDGE,"E1029"),sQuery(id+"F0.wireOp",EDGE,"E1030"),sQuery(id+"F0.wireOp",EDGE,"E1031"),sQuery(id+"F0.wireOp",EDGE,"E1032"),sQuery(id+"F0.wireOp",EDGE,"E1033"),sQuery(id+"F0.wireOp",EDGE,"E1034"),sQuery(id+"F0.wireOp",EDGE,"E1035"),sQuery(id+"F0.wireOp",EDGE,"E1036"),sQuery(id+"F0.wireOp",EDGE,"E1037"),sQuery(id+"F0.wireOp",EDGE,"E1038"),sQuery(id+"F0.wireOp",EDGE,"E1039"),sQuery(id+"F0.wireOp",EDGE,"E1040"),sQuery(id+"F0.wireOp",EDGE,"E1041"),sQuery(id+"F0.wireOp",EDGE,"E1042"),sQuery(id+"F0.wireOp",EDGE,"E1043"),sQuery(id+"F0.wireOp",EDGE,"E1044"),sQuery(id+"F0.wireOp",EDGE,"E1045"),sQuery(id+"F0.wireOp",EDGE,"E1046"),sQuery(id+"F0.wireOp",EDGE,"E1047"),sQuery(id+"F0.wireOp",EDGE,"E1048"),sQuery(id+"F0.wireOp",EDGE,"E1049"),sQuery(id+"F0.wireOp",EDGE,"E1050"),sQuery(id+"F0.wireOp",EDGE,"E1051"),sQuery(id+"F0.wireOp",EDGE,"E1052"),sQuery(id+"F0.wireOp",EDGE,"E1053"),sQuery(id+"F0.wireOp",EDGE,"E1054"),sQuery(id+"F0.wireOp",EDGE,"E1055"),sQuery(id+"F0.wireOp",EDGE,"E1056"),sQuery(id+"F0.wireOp",EDGE,"E1057"),sQuery(id+"F0.wireOp",EDGE,"E1058"),sQuery(id+"F0.wireOp",EDGE,"E1059"),sQuery(id+"F0.wireOp",EDGE,"E1060"),sQuery(id+"F0.wireOp",EDGE,"E1061"),sQuery(id+"F0.wireOp",EDGE,"E1062"),sQuery(id+"F0.wireOp",EDGE,"E1063"),sQuery(id+"F0.wireOp",EDGE,"E1064"),sQuery(id+"F0.wireOp",EDGE,"E1065"),sQuery(id+"F0.wireOp",EDGE,"E1066"),sQuery(id+"F0.wireOp",EDGE,"E1067"),sQuery(id+"F0.wireOp",EDGE,"E1068"),sQuery(id+"F0.wireOp",EDGE,"E1069"),sQuery(id+"F0.wireOp",EDGE,"E1070"),sQuery(id+"F0.wireOp",EDGE,"E1071"),sQuery(id+"F0.wireOp",EDGE,"E1072"),sQuery(id+"F0.wireOp",EDGE,"E1073"),sQuery(id+"F0.wireOp",EDGE,"E1074"),sQuery(id+"F0.wireOp",EDGE,"E1075"),sQuery(id+"F0.wireOp",EDGE,"E1076"),sQuery(id+"F0.wireOp",EDGE,"E1077"),sQuery(id+"F0.wireOp",EDGE,"E1078"),sQuery(id+"F0.wireOp",EDGE,"E1079"),sQuery(id+"F0.wireOp",EDGE,"E1080"),sQuery(id+"F0.wireOp",EDGE,"E1081"),sQuery(id+"F0.wireOp",EDGE,"E1082"),sQuery(id+"F0.wireOp",EDGE,"E1083"),sQuery(id+"F0.wireOp",EDGE,"E1084"),sQuery(id+"F0.wireOp",EDGE,"E1085"),sQuery(id+"F0.wireOp",EDGE,"E1086"),sQuery(id+"F0.wireOp",EDGE,"E1087"),sQuery(id+"F0.wireOp",EDGE,"E1088"),sQuery(id+"F0.wireOp",EDGE,"E1089"),sQuery(id+"F0.wireOp",EDGE,"E1090"),sQuery(id+"F0.wireOp",EDGE,"E1091"),sQuery(id+"F0.wireOp",EDGE,"E1092"),sQuery(id+"F0.wireOp",EDGE,"E1093"),sQuery(id+"F0.wireOp",EDGE,"E1094"),sQuery(id+"F0.wireOp",EDGE,"E1095"),sQuery(id+"F0.wireOp",EDGE,"E1096"),sQuery(id+"F0.wireOp",EDGE,"E1097"),sQuery(id+"F0.wireOp",EDGE,"E1098"),sQuery(id+"F0.wireOp",EDGE,"E1099"),sQuery(id+"F0.wireOp",EDGE,"E1100"),sQuery(id+"F0.wireOp",EDGE,"E1101"),sQuery(id+"F0.wireOp",EDGE,"E1102"),sQuery(id+"F0.wireOp",EDGE,"E1103"),sQuery(id+"F0.wireOp",EDGE,"E1104"),sQuery(id+"F0.wireOp",EDGE,"E1105"),sQuery(id+"F0.wireOp",EDGE,"E1106"),sQuery(id+"F0.wireOp",EDGE,"E1107"),sQuery(id+"F0.wireOp",EDGE,"E1108"),sQuery(id+"F0.wireOp",EDGE,"E1109"),sQuery(id+"F0.wireOp",EDGE,"E1110"),sQuery(id+"F0.wireOp",EDGE,"E1111"),sQuery(id+"F0.wireOp",EDGE,"E1112"),sQuery(id+"F0.wireOp",EDGE,"E1113"),sQuery(id+"F0.wireOp",EDGE,"E1114"),sQuery(id+"F0.wireOp",EDGE,"E1115"),sQuery(id+"F0.wireOp",EDGE,"E1116"),sQuery(id+"F0.wireOp",EDGE,"E1117"),sQuery(id+"F0.wireOp",EDGE,"E1118"),sQuery(id+"F0.wireOp",EDGE,"E1119"),sQuery(id+"F0.wireOp",EDGE,"E1120"),sQuery(id+"F0.wireOp",EDGE,"E1121"),sQuery(id+"F0.wireOp",EDGE,"E1122"),sQuery(id+"F0.wireOp",EDGE,"E1123"),sQuery(id+"F0.wireOp",EDGE,"E1124"),sQuery(id+"F0.wireOp",EDGE,"E1125"),sQuery(id+"F0.wireOp",EDGE,"E1126"),sQuery(id+"F0.wireOp",EDGE,"E1127"),sQuery(id+"F0.wireOp",EDGE,"E1128"),sQuery(id+"F0.wireOp",EDGE,"E1129"),sQuery(id+"F0.wireOp",EDGE,"E1130"),sQuery(id+"F0.wireOp",EDGE,"E1131"),sQuery(id+"F0.wireOp",EDGE,"E1132"),sQuery(id+"F0.wireOp",EDGE,"E1133"),sQuery(id+"F0.wireOp",EDGE,"E1134"),sQuery(id+"F0.wireOp",EDGE,"E1135"),sQuery(id+"F0.wireOp",EDGE,"E1136"),sQuery(id+"F0.wireOp",EDGE,"E1137"),sQuery(id+"F0.wireOp",EDGE,"E1138"),sQuery(id+"F0.wireOp",EDGE,"E1139"),sQuery(id+"F0.wireOp",EDGE,"E1140"),sQuery(id+"F0.wireOp",EDGE,"E1141"),sQuery(id+"F0.wireOp",EDGE,"E1142"),sQuery(id+"F0.wireOp",EDGE,"E1143"),sQuery(id+"F0.wireOp",EDGE,"E1144"),sQuery(id+"F0.wireOp",EDGE,"E1145"),sQuery(id+"F0.wireOp",EDGE,"E1146"),sQuery(id+"F0.wireOp",EDGE,"E1147"),sQuery(id+"F0.wireOp",EDGE,"E1148"),sQuery(id+"F0.wireOp",EDGE,"E1149"),sQuery(id+"F0.wireOp",EDGE,"E1150"),sQuery(id+"F0.wireOp",EDGE,"E1151"),sQuery(id+"F0.wireOp",EDGE,"E1152"),sQuery(id+"F0.wireOp",EDGE,"E1153"),sQuery(id+"F0.wireOp",EDGE,"E1154"),sQuery(id+"F0.wireOp",EDGE,"E1155"),sQuery(id+"F0.wireOp",EDGE,"E1156"),sQuery(id+"F0.wireOp",EDGE,"E1157"),sQuery(id+"F0.wireOp",EDGE,"E1158"),sQuery(id+"F0.wireOp",EDGE,"E1159"),sQuery(id+"F0.wireOp",EDGE,"E1160"),sQuery(id+"F0.wireOp",EDGE,"E1161"),sQuery(id+"F0.wireOp",EDGE,"E1162"),sQuery(id+"F0.wireOp",EDGE,"E1163"),sQuery(id+"F0.wireOp",EDGE,"E1164"),sQuery(id+"F0.wireOp",EDGE,"E1165"),sQuery(id+"F0.wireOp",EDGE,"E1166"),sQuery(id+"F0.wireOp",EDGE,"E1167"),sQuery(id+"F0.wireOp",EDGE,"E1168"),sQuery(id+"F0.wireOp",EDGE,"E1169"),sQuery(id+"F0.wireOp",EDGE,"E1170"),sQuery(id+"F0.wireOp",EDGE,"E1171"),sQuery(id+"F0.wireOp",EDGE,"E1172"),sQuery(id+"F0.wireOp",EDGE,"E1173"),sQuery(id+"F0.wireOp",EDGE,"E1174"),sQuery(id+"F0.wireOp",EDGE,"E1175"),sQuery(id+"F0.wireOp",EDGE,"E1176"),sQuery(id+"F0.wireOp",EDGE,"E1177"),sQuery(id+"F0.wireOp",EDGE,"E1178"),sQuery(id+"F0.wireOp",EDGE,"E1179"),sQuery(id+"F0.wireOp",EDGE,"E1180"),sQuery(id+"F0.wireOp",EDGE,"E1181"),sQuery(id+"F0.wireOp",EDGE,"E1182"),sQuery(id+"F0.wireOp",EDGE,"E1183"),sQuery(id+"F0.wireOp",EDGE,"E1184"),sQuery(id+"F0.wireOp",EDGE,"E1185"),sQuery(id+"F0.wireOp",EDGE,"E1186"),sQuery(id+"F0.wireOp",EDGE,"E1187"),sQuery(id+"F0.wireOp",EDGE,"E1188"),sQuery(id+"F0.wireOp",EDGE,"E1189"),sQuery(id+"F0.wireOp",EDGE,"E1190"),sQuery(id+"F0.wireOp",EDGE,"E1191"),sQuery(id+"F0.wireOp",EDGE,"E1192"),sQuery(id+"F0.wireOp",EDGE,"E1193"),sQuery(id+"F0.wireOp",EDGE,"E1194"),sQuery(id+"F0.wireOp",EDGE,"E1195"),sQuery(id+"F0.wireOp",EDGE,"E1196"),sQuery(id+"F0.wireOp",EDGE,"E1197"),sQuery(id+"F0.wireOp",EDGE,"E1198"),sQuery(id+"F0.wireOp",EDGE,"E1199"),sQuery(id+"F0.wireOp",EDGE,"E1200"),sQuery(id+"F0.wireOp",EDGE,"E1201"),sQuery(id+"F0.wireOp",EDGE,"E1202"),sQuery(id+"F0.wireOp",EDGE,"E1203"),sQuery(id+"F0.wireOp",EDGE,"E1204"),sQuery(id+"F0.wireOp",EDGE,"E1205"),sQuery(id+"F0.wireOp",EDGE,"E1206"),sQuery(id+"F0.wireOp",EDGE,"E1207"),sQuery(id+"F0.wireOp",EDGE,"E1208"),sQuery(id+"F0.wireOp",EDGE,"E1209"),sQuery(id+"F0.wireOp",EDGE,"E1210"),sQuery(id+"F0.wireOp",EDGE,"E1211"),sQuery(id+"F0.wireOp",EDGE,"E1212"),sQuery(id+"F0.wireOp",EDGE,"E1213"),sQuery(id+"F0.wireOp",EDGE,"E1214"),sQuery(id+"F0.wireOp",EDGE,"E1215"),sQuery(id+"F0.wireOp",EDGE,"E1216"),sQuery(id+"F0.wireOp",EDGE,"E1217"),sQuery(id+"F0.wireOp",EDGE,"E1218"),sQuery(id+"F0.wireOp",EDGE,"E1219"),sQuery(id+"F0.wireOp",EDGE,"E1220"),sQuery(id+"F0.wireOp",EDGE,"E1221"),sQuery(id+"F0.wireOp",EDGE,"E1222"),sQuery(id+"F0.wireOp",EDGE,"E1223"),sQuery(id+"F0.wireOp",EDGE,"E1224"),sQuery(id+"F0.wireOp",EDGE,"E1225"),sQuery(id+"F0.wireOp",EDGE,"E1226"),sQuery(id+"F0.wireOp",EDGE,"E1227"),sQuery(id+"F0.wireOp",EDGE,"E1228"),sQuery(id+"F0.wireOp",EDGE,"E1229"),sQuery(id+"F0.wireOp",EDGE,"E1230"),sQuery(id+"F0.wireOp",EDGE,"E1231"),sQuery(id+"F0.wireOp",EDGE,"E1232"),sQuery(id+"F0.wireOp",EDGE,"E1233"),sQuery(id+"F0.wireOp",EDGE,"E1234"),sQuery(id+"F0.wireOp",EDGE,"E1235"),sQuery(id+"F0.wireOp",EDGE,"E1236"),sQuery(id+"F0.wireOp",EDGE,"E1237"),sQuery(id+"F0.wireOp",EDGE,"E1238"),sQuery(id+"F0.wireOp",EDGE,"E1239"),sQuery(id+"F0.wireOp",EDGE,"E1240"),sQuery(id+"F0.wireOp",EDGE,"E1241"),sQuery(id+"F0.wireOp",EDGE,"E1242"),sQuery(id+"F0.wireOp",EDGE,"E1243"),sQuery(id+"F0.wireOp",EDGE,"E1244"),sQuery(id+"F0.wireOp",EDGE,"E1245"),sQuery(id+"F0.wireOp",EDGE,"E1246"),sQuery(id+"F0.wireOp",EDGE,"E1247"),sQuery(id+"F0.wireOp",EDGE,"E1248"),sQuery(id+"F0.wireOp",EDGE,"E1249"),sQuery(id+"F0.wireOp",EDGE,"E1250"),sQuery(id+"F0.wireOp",EDGE,"E1251"),sQuery(id+"F0.wireOp",EDGE,"E1252"),sQuery(id+"F0.wireOp",EDGE,"E1253"),sQuery(id+"F0.wireOp",EDGE,"E1254"),sQuery(id+"F0.wireOp",EDGE,"E1255"),sQuery(id+"F0.wireOp",EDGE,"E1256"),sQuery(id+"F0.wireOp",EDGE,"E1257"),sQuery(id+"F0.wireOp",EDGE,"E1258"),sQuery(id+"F0.wireOp",EDGE,"E1259"),sQuery(id+"F0.wireOp",EDGE,"E1260"),sQuery(id+"F0.wireOp",EDGE,"E1261"),sQuery(id+"F0.wireOp",EDGE,"E1262"),sQuery(id+"F0.wireOp",EDGE,"E1263"),sQuery(id+"F0.wireOp",EDGE,"E1264"),sQuery(id+"F0.wireOp",EDGE,"E1265"),sQuery(id+"F0.wireOp",EDGE,"E1266"),sQuery(id+"F0.wireOp",EDGE,"E1267"),sQuery(id+"F0.wireOp",EDGE,"E1268"),sQuery(id+"F0.wireOp",EDGE,"E1269"),sQuery(id+"F0.wireOp",EDGE,"E1270"),sQuery(id+"F0.wireOp",EDGE,"E1271"),sQuery(id+"F0.wireOp",EDGE,"E1272"),sQuery(id+"F0.wireOp",EDGE,"E1273"),sQuery(id+"F0.wireOp",EDGE,"E1274"),sQuery(id+"F0.wireOp",EDGE,"E1275"),sQuery(id+"F0.wireOp",EDGE,"E1276"),sQuery(id+"F0.wireOp",EDGE,"E1277"),sQuery(id+"F0.wireOp",EDGE,"E1278"),sQuery(id+"F0.wireOp",EDGE,"E1279"),sQuery(id+"F0.wireOp",EDGE,"E1280"),sQuery(id+"F0.wireOp",EDGE,"E1281"),sQuery(id+"F0.wireOp",EDGE,"E1282"),sQuery(id+"F0.wireOp",EDGE,"E1283"),sQuery(id+"F0.wireOp",EDGE,"E1284"),sQuery(id+"F0.wireOp",EDGE,"E1285"),sQuery(id+"F0.wireOp",EDGE,"E1286"),sQuery(id+"F0.wireOp",EDGE,"E1287"),sQuery(id+"F0.wireOp",EDGE,"E1288"),sQuery(id+"F0.wireOp",EDGE,"E1289"),sQuery(id+"F0.wireOp",EDGE,"E1290"),sQuery(id+"F0.wireOp",EDGE,"E1291"),sQuery(id+"F0.wireOp",EDGE,"E1292"),sQuery(id+"F0.wireOp",EDGE,"E1293"),sQuery(id+"F0.wireOp",EDGE,"E1294"),sQuery(id+"F0.wireOp",EDGE,"E1295"),sQuery(id+"F0.wireOp",EDGE,"E1296"),sQuery(id+"F0.wireOp",EDGE,"E1297"),sQuery(id+"F0.wireOp",EDGE,"E1298"),sQuery(id+"F0.wireOp",EDGE,"E1299"),sQuery(id+"F0.wireOp",EDGE,"E1300"),sQuery(id+"F0.wireOp",EDGE,"E1301"),sQuery(id+"F0.wireOp",EDGE,"E1302"),sQuery(id+"F0.wireOp",EDGE,"E1303"),sQuery(id+"F0.wireOp",EDGE,"E1304"),sQuery(id+"F0.wireOp",EDGE,"E1305"),sQuery(id+"F0.wireOp",EDGE,"E1306"),sQuery(id+"F0.wireOp",EDGE,"E1307"),sQuery(id+"F0.wireOp",EDGE,"E1308"),sQuery(id+"F0.wireOp",EDGE,"E1309"),sQuery(id+"F0.wireOp",EDGE,"E1310"),sQuery(id+"F0.wireOp",EDGE,"E1311"),sQuery(id+"F0.wireOp",EDGE,"E1312"),sQuery(id+"F0.wireOp",EDGE,"E1313"),sQuery(id+"F0.wireOp",EDGE,"E1314"),sQuery(id+"F0.wireOp",EDGE,"E1315"),sQuery(id+"F0.wireOp",EDGE,"E1316"),sQuery(id+"F0.wireOp",EDGE,"E1317"),sQuery(id+"F0.wireOp",EDGE,"E1318"),sQuery(id+"F0.wireOp",EDGE,"E1319"),sQuery(id+"F0.wireOp",EDGE,"E1320"),sQuery(id+"F0.wireOp",EDGE,"E1321"),sQuery(id+"F0.wireOp",EDGE,"E1322")])],"isStart":false});
            var sketch = newSketch(context, id + "F14", { "sketchPlane" : qUnion([Q0])});
            skLineSegment(sketch, "E1337.bottom", {"start": v(-119, -226.82) * mm, "end": v(-259, -226.82) * mm});
            skLineSegment(sketch, "E1337.top", {"start": v(-119, -233.74) * mm, "end": v(-259, -233.74) * mm});
            skLineSegment(sketch, "E1337.left", {"start": v(-119, -226.82) * mm, "end": v(-119, -233.74) * mm});
            skLineSegment(sketch, "E1337.right", {"start": v(-259, -226.82) * mm, "end": v(-259, -233.74) * mm});
            skLineSegment(sketch, "E1338.bottom", {"start": v(260, -226.82) * mm, "end": v(120, -226.82) * mm});
            skLineSegment(sketch, "E1338.top", {"start": v(260, -234.78) * mm, "end": v(120, -234.78) * mm});
            skLineSegment(sketch, "E1338.left", {"start": v(260, -226.82) * mm, "end": v(260, -234.78) * mm});
            skLineSegment(sketch, "E1338.right", {"start": v(120, -226.82) * mm, "end": v(120, -234.78) * mm});
            skSolve(sketch);
        }
        {
            var Q0;
            Q0=makeQuery(id+"F14.imprint","IMPRINT",FACE,{"disambiguationData":[TD([[makeQuery(id+"F14.imprint","IMPRINT",EDGE,{"derivedFrom":sQuery(id+"F14.wireOp",EDGE,"E1338.bottom")}),1.0]])]});
            var Q1;
            Q1=makeQuery(id+"F14.imprint","IMPRINT",FACE,{"disambiguationData":[TD([[makeQuery(id+"F14.imprint","IMPRINT",EDGE,{"derivedFrom":sQuery(id+"F14.wireOp",EDGE,"E1337.bottom")}),1.0]])]});
            extrude(context, id + "F15", {"entities" : qUnion([Q0, Q1]), "operationType" : NewBodyOperationType.ADD, "depth" : 30 * mm});
        }
        {
            var Q0;
            {var subQ0=sQuery(id+"F0.wireOp",EDGE,"E4");var subQ1=makeQuery(id+"F1.opExtrude","CAP_EDGE",EDGE,{"disambiguationData":[OSD([subQ0])],"isStart":true});Q0=makeQuery(id+"F9.opBoolean","MERGE",EDGE,{"derivedFrom":[makeQuery(id+"F3.opExtrude","SWEPT_EDGE",EDGE,{"disambiguationData":[OSD([subQ0,sQuery(id+"F0.wireOp",EDGE,"E6"),sQuery(id+"F0.wireOp",EDGE,"E124"),sQuery(id+"F2.wireOp",EDGE,"E1325")])]}),makeQuery(id+"F8.opBoolean","MERGE",EDGE,{"derivedFrom":[subQ1,makeQuery(id+"F5.opExtrude","CAP_EDGE",EDGE,{"disambiguationData":[OSD([sQuery(id+"F4.wireOp",EDGE,"E1326")])],"isStart":true})]}),subQ1]});}
            var Q1;
            {var subQ0=sQuery(id+"F0.wireOp",EDGE,"E5");var subQ1=makeQuery(id+"F1.opExtrude","CAP_EDGE",EDGE,{"disambiguationData":[OSD([subQ0])],"isStart":true});Q1=makeQuery(id+"F9.opBoolean","MERGE",EDGE,{"derivedFrom":[makeQuery(id+"F3.opExtrude","SWEPT_EDGE",EDGE,{"disambiguationData":[OSD([subQ0,sQuery(id+"F0.wireOp",EDGE,"E6"),sQuery(id+"F0.wireOp",EDGE,"E123"),sQuery(id+"F2.wireOp",EDGE,"E1323")])]}),makeQuery(id+"F8.opBoolean","MERGE",EDGE,{"derivedFrom":[subQ1,makeQuery(id+"F7.opExtrude","CAP_EDGE",EDGE,{"disambiguationData":[OSD([sQuery(id+"F6.wireOp",EDGE,"E1329")])],"isStart":true})]}),subQ1]});}
            fillet(context, id + "F16", {"entities" : qUnion([Q0, Q1]), "radius" : 10 * mm, "tangentPropagation" : true, "allowEdgeOverflow" : false});
        }
    });
